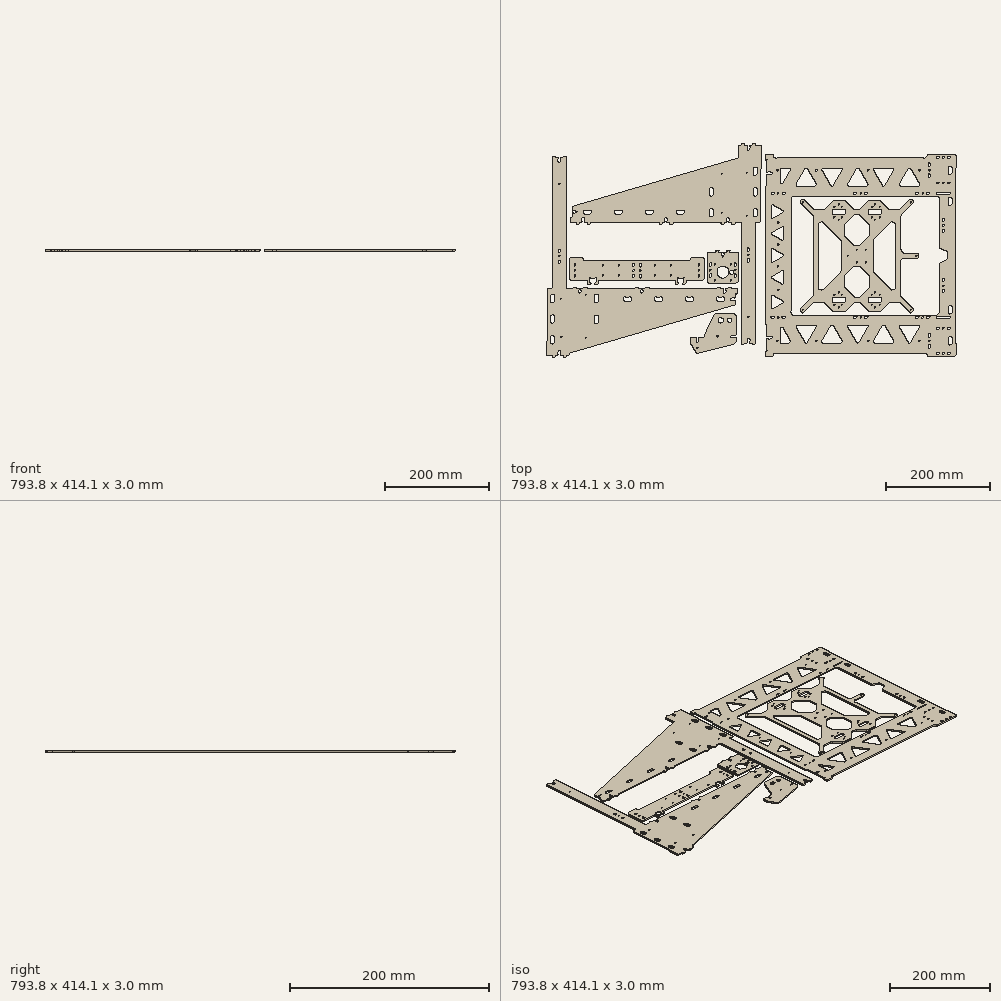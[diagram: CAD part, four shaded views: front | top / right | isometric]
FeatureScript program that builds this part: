
annotation { "Feature Type Name" : "Feature", "Feature Type Description" : "" }
export const myFeature = defineFeature(function(context is Context, id is Id, definition is map)
    precondition{}
    {
        {
            var Q0;
            Q0=qCreatedBy(makeId("Top.planeOp"),FACE);
            var sketch = newSketch(context, id + "F0", { "sketchPlane" : qUnion([Q0])});
            skFitSpline(sketch, "E0", {"points": [v(-205.76, 133.1) * mm, v(-205.54, 133.1) * mm, v(-205.33, 133.16) * mm, v(-205.16, 133.3) * mm]});
            skFitSpline(sketch, "E1", {"points": [v(-211.3, 171.1) * mm, v(-211.08, 171.1) * mm, v(-210.87, 171.16) * mm, v(-210.7, 171.3) * mm]});
            skFitSpline(sketch, "E2", {"points": [v(-203.99, 176.1) * mm, v(-204.2, 176.1) * mm, v(-204.42, 176.02) * mm, v(-204.59, 175.9) * mm]});
            skLineSegment(sketch, "E3", {"start": v(-205.16, 133.3) * mm, "end": v(-198.79, 138.1) * mm});
            skLineSegment(sketch, "E4", {"start": v(-210.7, 171.3) * mm, "end": v(-204.59, 175.9) * mm});
            skLineSegment(sketch, "E5", {"start": v(-213.3, 171.1) * mm, "end": v(-211.3, 171.1) * mm});
            skFitSpline(sketch, "E6", {"points": [v(-141.15, -195.58) * mm, v(-140.94, -195.58) * mm, v(-140.73, -195.5) * mm, v(-140.55, -195.38) * mm]});
            skFitSpline(sketch, "E7", {"points": [v(-146.69, -157.58) * mm, v(-146.47, -157.58) * mm, v(-146.26, -157.5) * mm, v(-146.09, -157.38) * mm]});
            skFitSpline(sketch, "E8", {"points": [v(-139.38, -152.58) * mm, v(-139.6, -152.58) * mm, v(-139.8, -152.65) * mm, v(-139.98, -152.78) * mm]});
            skLineSegment(sketch, "E9", {"start": v(-207.76, 133.1) * mm, "end": v(-205.91, 133.1) * mm});
            skLineSegment(sketch, "E10", {"start": v(-205.91, 133.1) * mm, "end": v(-205.77, 133.1) * mm});
            skLineSegment(sketch, "E11", {"start": v(-205.77, 133.1) * mm, "end": v(-205.76, 133.1) * mm});
            skLineSegment(sketch, "E12", {"start": v(-140.55, -195.38) * mm, "end": v(-134.18, -190.58) * mm});
            skLineSegment(sketch, "E13", {"start": v(-146.09, -157.38) * mm, "end": v(-139.98, -152.78) * mm});
            skLineSegment(sketch, "E14", {"start": v(-148.69, -157.58) * mm, "end": v(-146.68, -157.58) * mm});
            skFitSpline(sketch, "E15", {"points": [v(-352, -198.94) * mm, v(-352.22, -199) * mm, v(-352.37, -199.2) * mm, v(-352.37, -199.42) * mm]});
            skLineSegment(sketch, "E16", {"start": v(-143.15, -195.58) * mm, "end": v(-141.3, -195.58) * mm});
            skLineSegment(sketch, "E17", {"start": v(-141.3, -195.58) * mm, "end": v(-141.16, -195.58) * mm});
            skLineSegment(sketch, "E18", {"start": v(-141.16, -195.58) * mm, "end": v(-141.15, -195.58) * mm});
            skLineSegment(sketch, "E19", {"start": v(-396.82, -199.05) * mm, "end": v(-396.82, -204.05) * mm});
            skFitSpline(sketch, "E20", {"points": [v(396.82, 180.1) * mm, v(396.82, 182.86) * mm, v(394.58, 185.1) * mm, v(391.82, 185.1) * mm]});
            skFitSpline(sketch, "E21", {"points": [v(332.72, 179.1) * mm, v(336.37, 179.1) * mm, v(339.56, 181.57) * mm, v(340.47, 185.1) * mm]});
            skLineSegment(sketch, "E22", {"start": v(-352.37, -199.42) * mm, "end": v(-352.37, -204.05) * mm});
            skFitSpline(sketch, "E23", {"points": [v(41.82, 185.1) * mm, v(42.73, 181.57) * mm, v(45.92, 179.1) * mm, v(49.56, 179.1) * mm]});
            skLineSegment(sketch, "E24", {"start": v(394.82, 158.1) * mm, "end": v(396.82, 160.1) * mm});
            skLineSegment(sketch, "E25", {"start": v(396.82, 160.1) * mm, "end": v(396.82, 180.1) * mm});
            skFitSpline(sketch, "E26", {"points": [v(29.05, 175.1) * mm, v(29.23, 175.1) * mm, v(29.4, 175.2) * mm, v(29.48, 175.35) * mm]});
            skFitSpline(sketch, "E27", {"points": [v(30.17, 174.66) * mm, v(30.35, 174.77) * mm, v(30.45, 174.98) * mm, v(30.4, 175.18) * mm]});
            skFitSpline(sketch, "E28", {"points": [v(30.4, 175.18) * mm, v(30.37, 175.4) * mm, v(30.21, 175.55) * mm, v(30, 175.6) * mm]});
            skFitSpline(sketch, "E29", {"points": [v(30, 175.6) * mm, v(29.8, 175.63) * mm, v(29.59, 175.53) * mm, v(29.48, 175.35) * mm]});
            skFitSpline(sketch, "E30", {"points": [v(30.17, 174.66) * mm, v(30.01, 174.58) * mm, v(29.92, 174.41) * mm, v(29.92, 174.23) * mm]});
            skLineSegment(sketch, "E31", {"start": v(391.82, 185.1) * mm, "end": v(340.47, 185.1) * mm});
            skFitSpline(sketch, "E32", {"points": [v(29.92, 124.31) * mm, v(29.92, 124.14) * mm, v(30.01, 123.97) * mm, v(30.17, 123.88) * mm]});
            skFitSpline(sketch, "E33", {"points": [v(29.48, 123.2) * mm, v(29.59, 123.02) * mm, v(29.8, 122.92) * mm, v(30, 122.96) * mm]});
            skFitSpline(sketch, "E34", {"points": [v(30, 122.96) * mm, v(30.21, 123) * mm, v(30.37, 123.15) * mm, v(30.4, 123.36) * mm]});
            skFitSpline(sketch, "E35", {"points": [v(30.4, 123.36) * mm, v(30.45, 123.57) * mm, v(30.35, 123.78) * mm, v(30.17, 123.88) * mm]});
            skFitSpline(sketch, "E36", {"points": [v(29.48, 123.2) * mm, v(29.4, 123.35) * mm, v(29.23, 123.45) * mm, v(29.05, 123.45) * mm]});
            skLineSegment(sketch, "E37", {"start": v(332.72, 179.1) * mm, "end": v(49.56, 179.1) * mm});
            skFitSpline(sketch, "E38", {"points": [v(29.05, -143.25) * mm, v(29.23, -143.25) * mm, v(29.4, -143.16) * mm, v(29.48, -143) * mm]});
            skFitSpline(sketch, "E39", {"points": [v(30.17, -143.69) * mm, v(30.35, -143.58) * mm, v(30.45, -143.37) * mm, v(30.4, -143.17) * mm]});
            skFitSpline(sketch, "E40", {"points": [v(30.4, -143.17) * mm, v(30.37, -142.96) * mm, v(30.21, -142.8) * mm, v(30, -142.76) * mm]});
            skFitSpline(sketch, "E41", {"points": [v(30, -142.76) * mm, v(29.8, -142.72) * mm, v(29.59, -142.82) * mm, v(29.48, -143) * mm]});
            skFitSpline(sketch, "E42", {"points": [v(30.17, -143.69) * mm, v(30.01, -143.77) * mm, v(29.92, -143.94) * mm, v(29.92, -144.12) * mm]});
            skLineSegment(sketch, "E43", {"start": v(41.82, 185.1) * mm, "end": v(26.82, 185.1) * mm});
            skLineSegment(sketch, "E44", {"start": v(26.82, 185.1) * mm, "end": v(26.82, 175.1) * mm});
            skLineSegment(sketch, "E45", {"start": v(26.82, 175.1) * mm, "end": v(29.05, 175.1) * mm});
            skFitSpline(sketch, "E46", {"points": [v(29.92, -194.04) * mm, v(29.92, -194.21) * mm, v(30.01, -194.38) * mm, v(30.17, -194.47) * mm]});
            skFitSpline(sketch, "E47", {"points": [v(29.48, -195.15) * mm, v(29.59, -195.33) * mm, v(29.8, -195.43) * mm, v(30, -195.4) * mm]});
            skFitSpline(sketch, "E48", {"points": [v(30, -195.4) * mm, v(30.21, -195.36) * mm, v(30.37, -195.2) * mm, v(30.4, -194.99) * mm]});
            skFitSpline(sketch, "E49", {"points": [v(30.4, -194.99) * mm, v(30.45, -194.78) * mm, v(30.35, -194.57) * mm, v(30.17, -194.47) * mm]});
            skFitSpline(sketch, "E50", {"points": [v(29.48, -195.15) * mm, v(29.4, -195) * mm, v(29.23, -194.9) * mm, v(29.05, -194.9) * mm]});
            skLineSegment(sketch, "E51", {"start": v(29.92, 174.23) * mm, "end": v(29.92, 150.87) * mm});
            skLineSegment(sketch, "E52", {"start": v(29.92, 150.87) * mm, "end": v(32.92, 150.87) * mm});
            skLineSegment(sketch, "E53", {"start": v(32.92, 150.87) * mm, "end": v(32.92, 152.15) * mm});
            skLineSegment(sketch, "E54", {"start": v(32.92, 152.15) * mm, "end": v(36.92, 152.15) * mm});
            skLineSegment(sketch, "E55", {"start": v(36.92, 152.15) * mm, "end": v(36.92, 150.87) * mm});
            skLineSegment(sketch, "E56", {"start": v(36.92, 150.87) * mm, "end": v(39.92, 150.87) * mm});
            skLineSegment(sketch, "E57", {"start": v(39.92, 150.87) * mm, "end": v(39.92, 147.67) * mm});
            skLineSegment(sketch, "E58", {"start": v(39.92, 147.67) * mm, "end": v(36.92, 147.67) * mm});
            skLineSegment(sketch, "E59", {"start": v(36.92, 147.67) * mm, "end": v(36.92, 146.4) * mm});
            skLineSegment(sketch, "E60", {"start": v(36.92, 146.4) * mm, "end": v(32.92, 146.4) * mm});
            skLineSegment(sketch, "E61", {"start": v(32.92, 146.4) * mm, "end": v(32.92, 147.67) * mm});
            skLineSegment(sketch, "E62", {"start": v(32.92, 147.67) * mm, "end": v(29.92, 147.67) * mm});
            skLineSegment(sketch, "E63", {"start": v(29.92, 147.67) * mm, "end": v(29.92, 124.31) * mm});
            skFitSpline(sketch, "E64", {"points": [v(49.56, -198.9) * mm, v(45.92, -198.9) * mm, v(42.73, -201.37) * mm, v(41.82, -204.9) * mm]});
            skLineSegment(sketch, "E65", {"start": v(29.05, 123.45) * mm, "end": v(26.82, 123.45) * mm});
            skLineSegment(sketch, "E66", {"start": v(26.82, 123.45) * mm, "end": v(26.82, -143.25) * mm});
            skLineSegment(sketch, "E67", {"start": v(26.82, -143.25) * mm, "end": v(29.05, -143.25) * mm});
            skFitSpline(sketch, "E68", {"points": [v(340.47, -204.9) * mm, v(339.56, -201.37) * mm, v(336.37, -198.9) * mm, v(332.72, -198.9) * mm]});
            skLineSegment(sketch, "E69", {"start": v(29.92, -144.12) * mm, "end": v(29.92, -167.48) * mm});
            skLineSegment(sketch, "E70", {"start": v(29.92, -167.48) * mm, "end": v(32.92, -167.48) * mm});
            skLineSegment(sketch, "E71", {"start": v(32.92, -167.48) * mm, "end": v(32.92, -166.2) * mm});
            skLineSegment(sketch, "E72", {"start": v(32.92, -166.2) * mm, "end": v(36.92, -166.2) * mm});
            skLineSegment(sketch, "E73", {"start": v(36.92, -166.2) * mm, "end": v(36.92, -167.48) * mm});
            skLineSegment(sketch, "E74", {"start": v(36.92, -167.48) * mm, "end": v(39.92, -167.48) * mm});
            skLineSegment(sketch, "E75", {"start": v(39.92, -167.48) * mm, "end": v(39.92, -170.68) * mm});
            skLineSegment(sketch, "E76", {"start": v(39.92, -170.68) * mm, "end": v(36.92, -170.68) * mm});
            skLineSegment(sketch, "E77", {"start": v(36.92, -170.68) * mm, "end": v(36.92, -171.95) * mm});
            skLineSegment(sketch, "E78", {"start": v(36.92, -171.95) * mm, "end": v(32.92, -171.95) * mm});
            skLineSegment(sketch, "E79", {"start": v(32.92, -171.95) * mm, "end": v(32.92, -170.68) * mm});
            skLineSegment(sketch, "E80", {"start": v(32.92, -170.68) * mm, "end": v(29.92, -170.68) * mm});
            skLineSegment(sketch, "E81", {"start": v(29.92, -170.68) * mm, "end": v(29.92, -194.04) * mm});
            skFitSpline(sketch, "E82", {"points": [v(391.82, -204.9) * mm, v(394.58, -204.9) * mm, v(396.82, -202.66) * mm, v(396.82, -199.9) * mm]});
            skLineSegment(sketch, "E83", {"start": v(29.05, -194.9) * mm, "end": v(26.82, -194.9) * mm});
            skLineSegment(sketch, "E84", {"start": v(26.82, -194.9) * mm, "end": v(26.82, -204.9) * mm});
            skLineSegment(sketch, "E85", {"start": v(26.82, -204.9) * mm, "end": v(41.82, -204.9) * mm});
            skLineSegment(sketch, "E86", {"start": v(49.56, -198.9) * mm, "end": v(332.72, -198.9) * mm});
            skFitSpline(sketch, "E87", {"points": [v(378.82, -3.18) * mm, v(378.82, -2.4) * mm, v(378.37, -1.7) * mm, v(377.66, -1.36) * mm]});
            skLineSegment(sketch, "E88", {"start": v(340.47, -204.9) * mm, "end": v(391.82, -204.9) * mm});
            skFitSpline(sketch, "E89", {"points": [v(363.7, 6.43) * mm, v(363.7, 5.65) * mm, v(364.14, 4.94) * mm, v(364.85, 4.61) * mm]});
            skLineSegment(sketch, "E90", {"start": v(396.82, -199.9) * mm, "end": v(396.82, -179.9) * mm});
            skLineSegment(sketch, "E91", {"start": v(396.82, -179.9) * mm, "end": v(394.82, -177.9) * mm});
            skLineSegment(sketch, "E92", {"start": v(394.82, -177.9) * mm, "end": v(394.82, 158.1) * mm});
            skFitSpline(sketch, "E93", {"points": [v(363.7, 97.1) * mm, v(363.7, 101.5) * mm, v(360.12, 105.09) * mm, v(355.71, 105.1) * mm]});
            skLineSegment(sketch, "E94", {"start": v(378.82, -16.62) * mm, "end": v(378.82, -3.18) * mm});
            skFitSpline(sketch, "E95", {"points": [v(84.82, 105.1) * mm, v(82.7, 105.1) * mm, v(80.66, 104.25) * mm, v(79.16, 102.75) * mm]});
            skFitSpline(sketch, "E96", {"points": [v(79.16, 102.75) * mm, v(77.66, 101.25) * mm, v(76.82, 99.22) * mm, v(76.82, 97.1) * mm]});
            skLineSegment(sketch, "E97", {"start": v(377.66, -1.36) * mm, "end": v(364.85, 4.61) * mm});
            skFitSpline(sketch, "E98", {"points": [v(76.82, -116.9) * mm, v(76.82, -121.32) * mm, v(80.4, -124.9) * mm, v(84.82, -124.9) * mm]});
            skLineSegment(sketch, "E99", {"start": v(363.7, 6.43) * mm, "end": v(363.7, 97.1) * mm});
            skFitSpline(sketch, "E100", {"points": [v(355.71, -124.9) * mm, v(360.12, -124.9) * mm, v(363.7, -121.31) * mm, v(363.7, -116.9) * mm]});
            skLineSegment(sketch, "E101", {"start": v(355.71, 105.1) * mm, "end": v(84.82, 105.1) * mm});
            skFitSpline(sketch, "E102", {"points": [v(364.86, -24.31) * mm, v(364.15, -24.64) * mm, v(363.7, -25.35) * mm, v(363.7, -26.13) * mm]});
            skLineSegment(sketch, "E103", {"start": v(76.82, 97.1) * mm, "end": v(76.82, -116.9) * mm});
            skFitSpline(sketch, "E104", {"points": [v(377.65, -18.44) * mm, v(378.36, -18.11) * mm, v(378.82, -17.4) * mm, v(378.82, -16.62) * mm]});
            skLineSegment(sketch, "E105", {"start": v(84.82, -124.9) * mm, "end": v(355.71, -124.9) * mm});
            skFitSpline(sketch, "E106", {"points": [v(289.45, -144.33) * mm, v(288.38, -144.33) * mm, v(287.4, -144.9) * mm, v(286.86, -145.83) * mm]});
            skFitSpline(sketch, "E107", {"points": [v(286.86, -145.83) * mm, v(286.32, -146.76) * mm, v(286.32, -147.9) * mm, v(286.86, -148.83) * mm]});
            skLineSegment(sketch, "E108", {"start": v(363.7, -116.9) * mm, "end": v(363.7, -26.13) * mm});
            skFitSpline(sketch, "E109", {"points": [v(303.56, -177.76) * mm, v(304.1, -178.69) * mm, v(305.08, -179.26) * mm, v(306.16, -179.26) * mm]});
            skFitSpline(sketch, "E110", {"points": [v(306.16, -179.26) * mm, v(307.23, -179.26) * mm, v(308.22, -178.69) * mm, v(308.75, -177.76) * mm]});
            skLineSegment(sketch, "E111", {"start": v(364.86, -24.31) * mm, "end": v(377.65, -18.44) * mm});
            skFitSpline(sketch, "E112", {"points": [v(325.45, -148.83) * mm, v(326, -147.9) * mm, v(326, -146.76) * mm, v(325.45, -145.83) * mm]});
            skFitSpline(sketch, "E113", {"points": [v(325.45, -145.83) * mm, v(324.92, -144.9) * mm, v(323.93, -144.33) * mm, v(322.86, -144.33) * mm]});
            skLineSegment(sketch, "E114", {"start": v(322.86, -144.33) * mm, "end": v(289.45, -144.33) * mm});
            skFitSpline(sketch, "E115", {"points": [v(236.86, -174.76) * mm, v(236.32, -175.69) * mm, v(236.32, -176.83) * mm, v(236.86, -177.76) * mm]});
            skFitSpline(sketch, "E116", {"points": [v(236.86, -177.76) * mm, v(237.4, -178.69) * mm, v(238.38, -179.26) * mm, v(239.46, -179.26) * mm]});
            skLineSegment(sketch, "E117", {"start": v(286.86, -148.83) * mm, "end": v(303.56, -177.76) * mm});
            skFitSpline(sketch, "E118", {"points": [v(258.75, -145.83) * mm, v(258.22, -144.9) * mm, v(257.23, -144.33) * mm, v(256.16, -144.33) * mm]});
            skFitSpline(sketch, "E119", {"points": [v(256.16, -144.33) * mm, v(255.08, -144.33) * mm, v(254.1, -144.9) * mm, v(253.56, -145.83) * mm]});
            skLineSegment(sketch, "E120", {"start": v(308.75, -177.76) * mm, "end": v(325.45, -148.83) * mm});
            skFitSpline(sketch, "E121", {"points": [v(272.86, -179.26) * mm, v(273.93, -179.26) * mm, v(274.92, -178.69) * mm, v(275.46, -177.76) * mm]});
            skFitSpline(sketch, "E122", {"points": [v(275.46, -177.76) * mm, v(276, -176.83) * mm, v(276, -175.69) * mm, v(275.46, -174.76) * mm]});
            skLineSegment(sketch, "E123", {"start": v(272.86, -179.26) * mm, "end": v(239.46, -179.26) * mm});
            skFitSpline(sketch, "E124", {"points": [v(189.45, -144.33) * mm, v(188.38, -144.33) * mm, v(187.4, -144.9) * mm, v(186.86, -145.83) * mm]});
            skFitSpline(sketch, "E125", {"points": [v(186.86, -145.83) * mm, v(186.32, -146.76) * mm, v(186.32, -147.9) * mm, v(186.86, -148.83) * mm]});
            skLineSegment(sketch, "E126", {"start": v(236.86, -174.76) * mm, "end": v(253.56, -145.83) * mm});
            skFitSpline(sketch, "E127", {"points": [v(203.56, -177.76) * mm, v(204.1, -178.69) * mm, v(205.08, -179.26) * mm, v(206.16, -179.26) * mm]});
            skFitSpline(sketch, "E128", {"points": [v(206.16, -179.26) * mm, v(207.23, -179.26) * mm, v(208.22, -178.69) * mm, v(208.75, -177.76) * mm]});
            skLineSegment(sketch, "E129", {"start": v(258.75, -145.83) * mm, "end": v(275.46, -174.76) * mm});
            skFitSpline(sketch, "E130", {"points": [v(225.45, -148.83) * mm, v(226, -147.9) * mm, v(226, -146.76) * mm, v(225.45, -145.83) * mm]});
            skFitSpline(sketch, "E131", {"points": [v(225.45, -145.83) * mm, v(224.92, -144.9) * mm, v(223.93, -144.33) * mm, v(222.86, -144.33) * mm]});
            skLineSegment(sketch, "E132", {"start": v(222.86, -144.33) * mm, "end": v(189.45, -144.33) * mm});
            skFitSpline(sketch, "E133", {"points": [v(136.86, -174.76) * mm, v(136.32, -175.69) * mm, v(136.32, -176.83) * mm, v(136.86, -177.76) * mm]});
            skFitSpline(sketch, "E134", {"points": [v(136.86, -177.76) * mm, v(137.4, -178.69) * mm, v(138.38, -179.26) * mm, v(139.46, -179.26) * mm]});
            skLineSegment(sketch, "E135", {"start": v(186.86, -148.83) * mm, "end": v(203.56, -177.76) * mm});
            skFitSpline(sketch, "E136", {"points": [v(158.75, -145.83) * mm, v(158.22, -144.9) * mm, v(157.23, -144.33) * mm, v(156.16, -144.33) * mm]});
            skFitSpline(sketch, "E137", {"points": [v(156.16, -144.33) * mm, v(155.08, -144.33) * mm, v(154.1, -144.9) * mm, v(153.56, -145.83) * mm]});
            skLineSegment(sketch, "E138", {"start": v(208.75, -177.76) * mm, "end": v(225.45, -148.83) * mm});
            skFitSpline(sketch, "E139", {"points": [v(172.86, -179.26) * mm, v(173.93, -179.26) * mm, v(174.92, -178.69) * mm, v(175.46, -177.76) * mm]});
            skFitSpline(sketch, "E140", {"points": [v(175.46, -177.76) * mm, v(176, -176.83) * mm, v(176, -175.69) * mm, v(175.46, -174.76) * mm]});
            skLineSegment(sketch, "E141", {"start": v(172.86, -179.26) * mm, "end": v(139.46, -179.26) * mm});
            skFitSpline(sketch, "E142", {"points": [v(89.45, -144.33) * mm, v(88.38, -144.33) * mm, v(87.4, -144.9) * mm, v(86.86, -145.83) * mm]});
            skFitSpline(sketch, "E143", {"points": [v(86.86, -145.83) * mm, v(86.32, -146.76) * mm, v(86.32, -147.9) * mm, v(86.86, -148.83) * mm]});
            skLineSegment(sketch, "E144", {"start": v(136.86, -174.76) * mm, "end": v(153.56, -145.83) * mm});
            skFitSpline(sketch, "E145", {"points": [v(103.56, -177.76) * mm, v(104.1, -178.69) * mm, v(105.08, -179.26) * mm, v(106.16, -179.26) * mm]});
            skFitSpline(sketch, "E146", {"points": [v(106.16, -179.26) * mm, v(107.23, -179.26) * mm, v(108.22, -178.69) * mm, v(108.75, -177.76) * mm]});
            skLineSegment(sketch, "E147", {"start": v(158.75, -145.83) * mm, "end": v(175.46, -174.76) * mm});
            skFitSpline(sketch, "E148", {"points": [v(125.45, -148.83) * mm, v(126, -147.9) * mm, v(126, -146.76) * mm, v(125.45, -145.83) * mm]});
            skFitSpline(sketch, "E149", {"points": [v(125.45, -145.83) * mm, v(124.92, -144.9) * mm, v(123.93, -144.33) * mm, v(122.86, -144.33) * mm]});
            skLineSegment(sketch, "E150", {"start": v(122.86, -144.33) * mm, "end": v(89.45, -144.33) * mm});
            skFitSpline(sketch, "E151", {"points": [v(286.86, 129.03) * mm, v(286.32, 128.1) * mm, v(286.32, 126.95) * mm, v(286.86, 126.03) * mm]});
            skFitSpline(sketch, "E152", {"points": [v(286.86, 126.03) * mm, v(287.4, 125.1) * mm, v(288.38, 124.53) * mm, v(289.45, 124.53) * mm]});
            skLineSegment(sketch, "E153", {"start": v(86.86, -148.83) * mm, "end": v(103.56, -177.76) * mm});
            skFitSpline(sketch, "E154", {"points": [v(308.75, 157.95) * mm, v(308.22, 158.88) * mm, v(307.23, 159.45) * mm, v(306.16, 159.45) * mm]});
            skFitSpline(sketch, "E155", {"points": [v(306.16, 159.45) * mm, v(305.08, 159.45) * mm, v(304.1, 158.88) * mm, v(303.56, 157.95) * mm]});
            skLineSegment(sketch, "E156", {"start": v(108.75, -177.76) * mm, "end": v(125.45, -148.83) * mm});
            skFitSpline(sketch, "E157", {"points": [v(322.86, 124.53) * mm, v(323.93, 124.53) * mm, v(324.92, 125.1) * mm, v(325.45, 126.03) * mm]});
            skFitSpline(sketch, "E158", {"points": [v(325.45, 126.03) * mm, v(326, 126.95) * mm, v(326, 128.1) * mm, v(325.45, 129.03) * mm]});
            skLineSegment(sketch, "E159", {"start": v(322.86, 124.53) * mm, "end": v(289.45, 124.53) * mm});
            skFitSpline(sketch, "E160", {"points": [v(239.46, 159.45) * mm, v(238.38, 159.45) * mm, v(237.4, 158.88) * mm, v(236.86, 157.95) * mm]});
            skFitSpline(sketch, "E161", {"points": [v(236.86, 157.95) * mm, v(236.32, 157.02) * mm, v(236.32, 155.88) * mm, v(236.86, 154.95) * mm]});
            skLineSegment(sketch, "E162", {"start": v(286.86, 129.03) * mm, "end": v(303.56, 157.95) * mm});
            skFitSpline(sketch, "E163", {"points": [v(253.56, 126.03) * mm, v(254.1, 125.1) * mm, v(255.08, 124.53) * mm, v(256.16, 124.53) * mm]});
            skFitSpline(sketch, "E164", {"points": [v(256.16, 124.53) * mm, v(257.23, 124.53) * mm, v(258.22, 125.1) * mm, v(258.75, 126.03) * mm]});
            skLineSegment(sketch, "E165", {"start": v(308.75, 157.95) * mm, "end": v(325.45, 129.03) * mm});
            skFitSpline(sketch, "E166", {"points": [v(275.46, 154.95) * mm, v(276, 155.88) * mm, v(276, 157.02) * mm, v(275.46, 157.95) * mm]});
            skFitSpline(sketch, "E167", {"points": [v(275.46, 157.95) * mm, v(274.92, 158.88) * mm, v(273.93, 159.45) * mm, v(272.86, 159.45) * mm]});
            skLineSegment(sketch, "E168", {"start": v(272.86, 159.45) * mm, "end": v(239.46, 159.45) * mm});
            skFitSpline(sketch, "E169", {"points": [v(186.86, 129.03) * mm, v(186.32, 128.1) * mm, v(186.32, 126.95) * mm, v(186.86, 126.03) * mm]});
            skFitSpline(sketch, "E170", {"points": [v(186.86, 126.03) * mm, v(187.4, 125.1) * mm, v(188.38, 124.53) * mm, v(189.45, 124.53) * mm]});
            skLineSegment(sketch, "E171", {"start": v(236.86, 154.95) * mm, "end": v(253.56, 126.03) * mm});
            skFitSpline(sketch, "E172", {"points": [v(208.75, 157.95) * mm, v(208.22, 158.88) * mm, v(207.23, 159.45) * mm, v(206.16, 159.45) * mm]});
            skFitSpline(sketch, "E173", {"points": [v(206.16, 159.45) * mm, v(205.08, 159.45) * mm, v(204.1, 158.88) * mm, v(203.56, 157.95) * mm]});
            skLineSegment(sketch, "E174", {"start": v(258.75, 126.03) * mm, "end": v(275.46, 154.95) * mm});
            skFitSpline(sketch, "E175", {"points": [v(222.86, 124.53) * mm, v(223.93, 124.53) * mm, v(224.92, 125.1) * mm, v(225.45, 126.03) * mm]});
            skFitSpline(sketch, "E176", {"points": [v(225.45, 126.03) * mm, v(226, 126.95) * mm, v(226, 128.1) * mm, v(225.45, 129.03) * mm]});
            skLineSegment(sketch, "E177", {"start": v(222.86, 124.53) * mm, "end": v(189.45, 124.53) * mm});
            skFitSpline(sketch, "E178", {"points": [v(139.46, 159.45) * mm, v(138.38, 159.45) * mm, v(137.4, 158.88) * mm, v(136.86, 157.95) * mm]});
            skFitSpline(sketch, "E179", {"points": [v(136.86, 157.95) * mm, v(136.32, 157.02) * mm, v(136.32, 155.88) * mm, v(136.86, 154.95) * mm]});
            skLineSegment(sketch, "E180", {"start": v(186.86, 129.03) * mm, "end": v(203.56, 157.95) * mm});
            skFitSpline(sketch, "E181", {"points": [v(153.56, 126.03) * mm, v(154.1, 125.1) * mm, v(155.08, 124.53) * mm, v(156.16, 124.53) * mm]});
            skFitSpline(sketch, "E182", {"points": [v(156.16, 124.53) * mm, v(157.23, 124.53) * mm, v(158.22, 125.1) * mm, v(158.75, 126.03) * mm]});
            skLineSegment(sketch, "E183", {"start": v(208.75, 157.95) * mm, "end": v(225.45, 129.03) * mm});
            skFitSpline(sketch, "E184", {"points": [v(175.46, 154.95) * mm, v(176, 155.88) * mm, v(176, 157.02) * mm, v(175.46, 157.95) * mm]});
            skFitSpline(sketch, "E185", {"points": [v(175.46, 157.95) * mm, v(174.92, 158.88) * mm, v(173.93, 159.45) * mm, v(172.86, 159.45) * mm]});
            skLineSegment(sketch, "E186", {"start": v(172.86, 159.45) * mm, "end": v(139.46, 159.45) * mm});
            skFitSpline(sketch, "E187", {"points": [v(86.86, 129.03) * mm, v(86.32, 128.1) * mm, v(86.32, 126.95) * mm, v(86.86, 126.03) * mm]});
            skFitSpline(sketch, "E188", {"points": [v(86.86, 126.03) * mm, v(87.4, 125.1) * mm, v(88.38, 124.53) * mm, v(89.45, 124.53) * mm]});
            skLineSegment(sketch, "E189", {"start": v(136.86, 154.95) * mm, "end": v(153.56, 126.03) * mm});
            skFitSpline(sketch, "E190", {"points": [v(108.75, 157.95) * mm, v(108.22, 158.88) * mm, v(107.23, 159.45) * mm, v(106.16, 159.45) * mm]});
            skFitSpline(sketch, "E191", {"points": [v(106.16, 159.45) * mm, v(105.08, 159.45) * mm, v(104.1, 158.88) * mm, v(103.56, 157.95) * mm]});
            skLineSegment(sketch, "E192", {"start": v(158.75, 126.03) * mm, "end": v(175.46, 154.95) * mm});
            skFitSpline(sketch, "E193", {"points": [v(122.86, 124.53) * mm, v(123.93, 124.53) * mm, v(124.92, 125.1) * mm, v(125.45, 126.03) * mm]});
            skFitSpline(sketch, "E194", {"points": [v(125.45, 126.03) * mm, v(126, 126.95) * mm, v(126, 128.1) * mm, v(125.45, 129.03) * mm]});
            skLineSegment(sketch, "E195", {"start": v(122.86, 124.53) * mm, "end": v(89.45, 124.53) * mm});
            skFitSpline(sketch, "E196", {"points": [v(39.12, -111.23) * mm, v(39.12, -111.95) * mm, v(39.51, -112.62) * mm, v(40.14, -112.98) * mm]});
            skFitSpline(sketch, "E197", {"points": [v(40.14, -112.98) * mm, v(40.76, -113.35) * mm, v(41.54, -113.35) * mm, v(42.16, -112.98) * mm]});
            skLineSegment(sketch, "E198", {"start": v(86.86, 129.03) * mm, "end": v(103.56, 157.95) * mm});
            skFitSpline(sketch, "E199", {"points": [v(61.69, -101.71) * mm, v(62.31, -101.35) * mm, v(62.7, -100.68) * mm, v(62.7, -99.96) * mm]});
            skFitSpline(sketch, "E200", {"points": [v(62.7, -99.96) * mm, v(62.7, -99.23) * mm, v(62.31, -98.57) * mm, v(61.69, -98.2) * mm]});
            skLineSegment(sketch, "E201", {"start": v(108.75, 157.95) * mm, "end": v(125.45, 129.03) * mm});
            skFitSpline(sketch, "E202", {"points": [v(42.16, -86.93) * mm, v(41.54, -86.57) * mm, v(40.76, -86.57) * mm, v(40.14, -86.93) * mm]});
            skFitSpline(sketch, "E203", {"points": [v(40.14, -86.93) * mm, v(39.51, -87.3) * mm, v(39.12, -87.96) * mm, v(39.12, -88.68) * mm]});
            skLineSegment(sketch, "E204", {"start": v(39.12, -88.68) * mm, "end": v(39.12, -111.23) * mm});
            skFitSpline(sketch, "E205", {"points": [v(59.66, -65.44) * mm, v(60.29, -65.8) * mm, v(61.06, -65.8) * mm, v(61.69, -65.44) * mm]});
            skFitSpline(sketch, "E206", {"points": [v(61.69, -65.44) * mm, v(62.31, -65.08) * mm, v(62.7, -64.4) * mm, v(62.7, -63.68) * mm]});
            skLineSegment(sketch, "E207", {"start": v(42.16, -112.98) * mm, "end": v(61.69, -101.71) * mm});
            skFitSpline(sketch, "E208", {"points": [v(40.14, -50.66) * mm, v(39.51, -51.02) * mm, v(39.12, -51.69) * mm, v(39.12, -52.41) * mm]});
            skFitSpline(sketch, "E209", {"points": [v(39.12, -52.41) * mm, v(39.12, -53.13) * mm, v(39.51, -53.8) * mm, v(40.14, -54.16) * mm]});
            skLineSegment(sketch, "E210", {"start": v(61.69, -98.2) * mm, "end": v(42.16, -86.93) * mm});
            skFitSpline(sketch, "E211", {"points": [v(62.7, -41.14) * mm, v(62.7, -40.41) * mm, v(62.31, -39.75) * mm, v(61.69, -39.38) * mm]});
            skFitSpline(sketch, "E212", {"points": [v(61.69, -39.38) * mm, v(61.06, -39.02) * mm, v(60.29, -39.02) * mm, v(59.66, -39.38) * mm]});
            skLineSegment(sketch, "E213", {"start": v(62.7, -41.14) * mm, "end": v(62.7, -63.68) * mm});
            skFitSpline(sketch, "E214", {"points": [v(39.12, -21.18) * mm, v(39.12, -21.9) * mm, v(39.51, -22.58) * mm, v(40.14, -22.94) * mm]});
            skFitSpline(sketch, "E215", {"points": [v(40.14, -22.94) * mm, v(40.76, -23.3) * mm, v(41.54, -23.3) * mm, v(42.16, -22.94) * mm]});
            skLineSegment(sketch, "E216", {"start": v(59.66, -65.44) * mm, "end": v(40.14, -54.16) * mm});
            skFitSpline(sketch, "E217", {"points": [v(61.69, -11.66) * mm, v(62.31, -11.3) * mm, v(62.7, -10.63) * mm, v(62.7, -9.91) * mm]});
            skFitSpline(sketch, "E218", {"points": [v(62.7, -9.91) * mm, v(62.7, -9.19) * mm, v(62.31, -8.52) * mm, v(61.69, -8.16) * mm]});
            skLineSegment(sketch, "E219", {"start": v(40.14, -50.66) * mm, "end": v(59.66, -39.38) * mm});
            skFitSpline(sketch, "E220", {"points": [v(42.16, 3.12) * mm, v(41.54, 3.48) * mm, v(40.76, 3.48) * mm, v(40.14, 3.12) * mm]});
            skFitSpline(sketch, "E221", {"points": [v(40.14, 3.12) * mm, v(39.51, 2.75) * mm, v(39.12, 2.09) * mm, v(39.12, 1.36) * mm]});
            skLineSegment(sketch, "E222", {"start": v(39.12, 1.36) * mm, "end": v(39.12, -21.18) * mm});
            skFitSpline(sketch, "E223", {"points": [v(59.66, 19.57) * mm, v(60.29, 19.2) * mm, v(61.06, 19.2) * mm, v(61.69, 19.57) * mm]});
            skFitSpline(sketch, "E224", {"points": [v(61.69, 19.57) * mm, v(62.31, 19.93) * mm, v(62.7, 20.6) * mm, v(62.7, 21.32) * mm]});
            skLineSegment(sketch, "E225", {"start": v(42.16, -22.94) * mm, "end": v(61.69, -11.66) * mm});
            skFitSpline(sketch, "E226", {"points": [v(40.14, 34.35) * mm, v(39.51, 33.99) * mm, v(39.12, 33.32) * mm, v(39.12, 32.6) * mm]});
            skFitSpline(sketch, "E227", {"points": [v(39.12, 32.6) * mm, v(39.12, 31.87) * mm, v(39.51, 31.2) * mm, v(40.14, 30.84) * mm]});
            skLineSegment(sketch, "E228", {"start": v(61.69, -8.16) * mm, "end": v(42.16, 3.12) * mm});
            skFitSpline(sketch, "E229", {"points": [v(62.7, 43.87) * mm, v(62.7, 44.6) * mm, v(62.31, 45.26) * mm, v(61.69, 45.62) * mm]});
            skFitSpline(sketch, "E230", {"points": [v(61.69, 45.62) * mm, v(61.06, 45.99) * mm, v(60.29, 45.99) * mm, v(59.66, 45.62) * mm]});
            skLineSegment(sketch, "E231", {"start": v(62.7, 43.87) * mm, "end": v(62.7, 21.32) * mm});
            skFitSpline(sketch, "E232", {"points": [v(39.12, 63.82) * mm, v(39.12, 63.1) * mm, v(39.51, 62.43) * mm, v(40.14, 62.07) * mm]});
            skFitSpline(sketch, "E233", {"points": [v(40.14, 62.07) * mm, v(40.76, 61.7) * mm, v(41.54, 61.7) * mm, v(42.16, 62.07) * mm]});
            skLineSegment(sketch, "E234", {"start": v(59.66, 19.57) * mm, "end": v(40.14, 30.84) * mm});
            skFitSpline(sketch, "E235", {"points": [v(61.69, 73.34) * mm, v(62.31, 73.7) * mm, v(62.7, 74.37) * mm, v(62.7, 75.1) * mm]});
            skFitSpline(sketch, "E236", {"points": [v(62.7, 75.1) * mm, v(62.7, 75.82) * mm, v(62.31, 76.49) * mm, v(61.69, 76.85) * mm]});
            skLineSegment(sketch, "E237", {"start": v(40.14, 34.35) * mm, "end": v(59.66, 45.62) * mm});
            skFitSpline(sketch, "E238", {"points": [v(42.16, 88.12) * mm, v(41.54, 88.49) * mm, v(40.76, 88.49) * mm, v(40.14, 88.12) * mm]});
            skFitSpline(sketch, "E239", {"points": [v(40.14, 88.12) * mm, v(39.51, 87.76) * mm, v(39.12, 87.1) * mm, v(39.12, 86.37) * mm]});
            skLineSegment(sketch, "E240", {"start": v(39.12, 86.37) * mm, "end": v(39.12, 63.82) * mm});
            skFitSpline(sketch, "E241", {"points": [v(388.82, -170.9) * mm, v(388.82, -169.47) * mm, v(388.05, -168.15) * mm, v(386.82, -167.44) * mm]});
            skFitSpline(sketch, "E242", {"points": [v(386.82, -167.44) * mm, v(385.58, -166.72) * mm, v(384.05, -166.72) * mm, v(382.82, -167.44) * mm]});
            skFitSpline(sketch, "E243", {"points": [v(382.82, -167.44) * mm, v(381.58, -168.15) * mm, v(380.82, -169.47) * mm, v(380.82, -170.9) * mm]});
            skLineSegment(sketch, "E244", {"start": v(42.16, 62.07) * mm, "end": v(61.69, 73.34) * mm});
            skFitSpline(sketch, "E245", {"points": [v(380.82, -178.9) * mm, v(380.82, -180.33) * mm, v(381.58, -181.65) * mm, v(382.82, -182.37) * mm]});
            skFitSpline(sketch, "E246", {"points": [v(382.82, -182.37) * mm, v(384.05, -183.08) * mm, v(385.58, -183.08) * mm, v(386.82, -182.37) * mm]});
            skFitSpline(sketch, "E247", {"points": [v(386.82, -182.37) * mm, v(388.05, -181.65) * mm, v(388.82, -180.33) * mm, v(388.82, -178.9) * mm]});
            skLineSegment(sketch, "E248", {"start": v(61.69, 76.85) * mm, "end": v(42.16, 88.12) * mm});
            skFitSpline(sketch, "E249", {"points": [v(388.82, -110.9) * mm, v(388.82, -109.47) * mm, v(388.05, -108.15) * mm, v(386.82, -107.44) * mm]});
            skFitSpline(sketch, "E250", {"points": [v(386.82, -107.44) * mm, v(385.58, -106.72) * mm, v(384.05, -106.72) * mm, v(382.82, -107.44) * mm]});
            skFitSpline(sketch, "E251", {"points": [v(382.82, -107.44) * mm, v(381.58, -108.15) * mm, v(380.82, -109.47) * mm, v(380.82, -110.9) * mm]});
            skLineSegment(sketch, "E252", {"start": v(388.82, -178.9) * mm, "end": v(388.82, -170.9) * mm});
            skFitSpline(sketch, "E253", {"points": [v(380.82, -118.9) * mm, v(380.82, -120.33) * mm, v(381.58, -121.65) * mm, v(382.82, -122.37) * mm]});
            skFitSpline(sketch, "E254", {"points": [v(382.82, -122.37) * mm, v(384.05, -123.08) * mm, v(385.58, -123.08) * mm, v(386.82, -122.37) * mm]});
            skFitSpline(sketch, "E255", {"points": [v(386.82, -122.37) * mm, v(388.05, -121.65) * mm, v(388.82, -120.33) * mm, v(388.82, -118.9) * mm]});
            skLineSegment(sketch, "E256", {"start": v(380.82, -170.9) * mm, "end": v(380.82, -178.9) * mm});
            skFitSpline(sketch, "E257", {"points": [v(388.82, 99.1) * mm, v(388.82, 100.53) * mm, v(388.05, 101.85) * mm, v(386.82, 102.56) * mm]});
            skFitSpline(sketch, "E258", {"points": [v(386.82, 102.56) * mm, v(385.58, 103.28) * mm, v(384.05, 103.28) * mm, v(382.82, 102.56) * mm]});
            skFitSpline(sketch, "E259", {"points": [v(382.82, 102.56) * mm, v(381.58, 101.85) * mm, v(380.82, 100.53) * mm, v(380.82, 99.1) * mm]});
            skLineSegment(sketch, "E260", {"start": v(388.82, -118.9) * mm, "end": v(388.82, -110.9) * mm});
            skFitSpline(sketch, "E261", {"points": [v(380.82, 91.1) * mm, v(380.82, 89.67) * mm, v(381.58, 88.35) * mm, v(382.82, 87.63) * mm]});
            skFitSpline(sketch, "E262", {"points": [v(382.82, 87.63) * mm, v(384.05, 86.92) * mm, v(385.58, 86.92) * mm, v(386.82, 87.63) * mm]});
            skFitSpline(sketch, "E263", {"points": [v(386.82, 87.63) * mm, v(388.05, 88.35) * mm, v(388.82, 89.67) * mm, v(388.82, 91.1) * mm]});
            skLineSegment(sketch, "E264", {"start": v(380.82, -110.9) * mm, "end": v(380.82, -118.9) * mm});
            skFitSpline(sketch, "E265", {"points": [v(388.82, 159.1) * mm, v(388.82, 160.53) * mm, v(388.05, 161.85) * mm, v(386.82, 162.56) * mm]});
            skFitSpline(sketch, "E266", {"points": [v(386.82, 162.56) * mm, v(385.58, 163.28) * mm, v(384.05, 163.28) * mm, v(382.82, 162.56) * mm]});
            skFitSpline(sketch, "E267", {"points": [v(382.82, 162.56) * mm, v(381.58, 161.85) * mm, v(380.82, 160.53) * mm, v(380.82, 159.1) * mm]});
            skLineSegment(sketch, "E268", {"start": v(388.82, 91.1) * mm, "end": v(388.82, 99.1) * mm});
            skFitSpline(sketch, "E269", {"points": [v(380.82, 151.1) * mm, v(380.82, 149.67) * mm, v(381.58, 148.35) * mm, v(382.82, 147.63) * mm]});
            skFitSpline(sketch, "E270", {"points": [v(382.82, 147.63) * mm, v(384.05, 146.92) * mm, v(385.58, 146.92) * mm, v(386.82, 147.63) * mm]});
            skFitSpline(sketch, "E271", {"points": [v(386.82, 147.63) * mm, v(388.05, 148.35) * mm, v(388.82, 149.67) * mm, v(388.82, 151.1) * mm]});
            skFitSpline(sketch, "E272", {"points": [v(358.12, -129.3) * mm, v(358.12, -129.11) * mm, v(358.02, -128.95) * mm, v(357.87, -128.86) * mm]});
            skFitSpline(sketch, "E273", {"points": [v(358.55, -128.18) * mm, v(358.45, -128) * mm, v(358.24, -127.9) * mm, v(358.03, -127.93) * mm]});
            skFitSpline(sketch, "E274", {"points": [v(358.03, -127.93) * mm, v(357.82, -127.97) * mm, v(357.66, -128.13) * mm, v(357.62, -128.34) * mm]});
            skFitSpline(sketch, "E275", {"points": [v(357.62, -128.34) * mm, v(357.59, -128.55) * mm, v(357.69, -128.76) * mm, v(357.87, -128.86) * mm]});
            skFitSpline(sketch, "E276", {"points": [v(358.55, -128.18) * mm, v(358.64, -128.33) * mm, v(358.8, -128.43) * mm, v(358.98, -128.43) * mm]});
            skLineSegment(sketch, "E277", {"start": v(380.82, 99.1) * mm, "end": v(380.82, 91.1) * mm});
            skFitSpline(sketch, "E278", {"points": [v(384.65, -128.43) * mm, v(384.83, -128.43) * mm, v(385, -128.33) * mm, v(385.08, -128.18) * mm]});
            skFitSpline(sketch, "E279", {"points": [v(385.77, -128.86) * mm, v(385.95, -128.76) * mm, v(386.05, -128.55) * mm, v(386, -128.34) * mm]});
            skFitSpline(sketch, "E280", {"points": [v(386, -128.34) * mm, v(385.97, -128.13) * mm, v(385.81, -127.97) * mm, v(385.6, -127.93) * mm]});
            skFitSpline(sketch, "E281", {"points": [v(385.6, -127.93) * mm, v(385.4, -127.9) * mm, v(385.19, -128) * mm, v(385.08, -128.18) * mm]});
            skFitSpline(sketch, "E282", {"points": [v(385.77, -128.86) * mm, v(385.61, -128.95) * mm, v(385.52, -129.11) * mm, v(385.52, -129.3) * mm]});
            skLineSegment(sketch, "E283", {"start": v(388.82, 151.1) * mm, "end": v(388.82, 159.1) * mm});
            skFitSpline(sketch, "E284", {"points": [v(385.52, -130.86) * mm, v(385.52, -131.04) * mm, v(385.61, -131.2) * mm, v(385.77, -131.3) * mm]});
            skFitSpline(sketch, "E285", {"points": [v(385.08, -131.98) * mm, v(385.19, -132.16) * mm, v(385.4, -132.26) * mm, v(385.6, -132.22) * mm]});
            skFitSpline(sketch, "E286", {"points": [v(385.6, -132.22) * mm, v(385.81, -132.18) * mm, v(385.97, -132.02) * mm, v(386, -131.81) * mm]});
            skFitSpline(sketch, "E287", {"points": [v(386, -131.81) * mm, v(386.05, -131.6) * mm, v(385.95, -131.4) * mm, v(385.77, -131.3) * mm]});
            skFitSpline(sketch, "E288", {"points": [v(385.08, -131.98) * mm, v(385, -131.82) * mm, v(384.83, -131.73) * mm, v(384.65, -131.73) * mm]});
            skLineSegment(sketch, "E289", {"start": v(380.82, 159.1) * mm, "end": v(380.82, 151.1) * mm});
            skFitSpline(sketch, "E290", {"points": [v(358.98, -131.73) * mm, v(358.8, -131.73) * mm, v(358.64, -131.82) * mm, v(358.55, -131.98) * mm]});
            skFitSpline(sketch, "E291", {"points": [v(357.87, -131.3) * mm, v(357.69, -131.4) * mm, v(357.59, -131.6) * mm, v(357.62, -131.81) * mm]});
            skFitSpline(sketch, "E292", {"points": [v(357.62, -131.81) * mm, v(357.66, -132.02) * mm, v(357.82, -132.18) * mm, v(358.03, -132.22) * mm]});
            skFitSpline(sketch, "E293", {"points": [v(358.03, -132.22) * mm, v(358.24, -132.26) * mm, v(358.45, -132.16) * mm, v(358.55, -131.98) * mm]});
            skFitSpline(sketch, "E294", {"points": [v(357.87, -131.3) * mm, v(358.02, -131.2) * mm, v(358.12, -131.04) * mm, v(358.12, -130.86) * mm]});
            skLineSegment(sketch, "E295", {"start": v(358.98, -128.43) * mm, "end": v(384.65, -128.43) * mm});
            skFitSpline(sketch, "E296", {"points": [v(358.12, 111.06) * mm, v(358.12, 111.24) * mm, v(358.02, 111.4) * mm, v(357.87, 111.49) * mm]});
            skFitSpline(sketch, "E297", {"points": [v(358.55, 112.17) * mm, v(358.45, 112.35) * mm, v(358.24, 112.45) * mm, v(358.03, 112.42) * mm]});
            skFitSpline(sketch, "E298", {"points": [v(358.03, 112.42) * mm, v(357.82, 112.38) * mm, v(357.66, 112.22) * mm, v(357.62, 112) * mm]});
            skFitSpline(sketch, "E299", {"points": [v(357.62, 112) * mm, v(357.59, 111.8) * mm, v(357.69, 111.6) * mm, v(357.87, 111.49) * mm]});
            skFitSpline(sketch, "E300", {"points": [v(358.55, 112.17) * mm, v(358.64, 112.02) * mm, v(358.8, 111.92) * mm, v(358.98, 111.92) * mm]});
            skLineSegment(sketch, "E301", {"start": v(385.52, -129.3) * mm, "end": v(385.52, -130.86) * mm});
            skFitSpline(sketch, "E302", {"points": [v(384.65, 111.92) * mm, v(384.83, 111.92) * mm, v(385, 112.02) * mm, v(385.08, 112.17) * mm]});
            skFitSpline(sketch, "E303", {"points": [v(385.77, 111.49) * mm, v(385.95, 111.6) * mm, v(386.05, 111.8) * mm, v(386, 112) * mm]});
            skFitSpline(sketch, "E304", {"points": [v(386, 112) * mm, v(385.97, 112.22) * mm, v(385.81, 112.38) * mm, v(385.6, 112.42) * mm]});
            skFitSpline(sketch, "E305", {"points": [v(385.6, 112.42) * mm, v(385.4, 112.45) * mm, v(385.19, 112.35) * mm, v(385.08, 112.17) * mm]});
            skFitSpline(sketch, "E306", {"points": [v(385.77, 111.49) * mm, v(385.61, 111.4) * mm, v(385.52, 111.24) * mm, v(385.52, 111.06) * mm]});
            skLineSegment(sketch, "E307", {"start": v(384.65, -131.73) * mm, "end": v(358.98, -131.73) * mm});
            skFitSpline(sketch, "E308", {"points": [v(385.52, 109.49) * mm, v(385.52, 109.31) * mm, v(385.61, 109.15) * mm, v(385.77, 109.06) * mm]});
            skFitSpline(sketch, "E309", {"points": [v(385.08, 108.37) * mm, v(385.19, 108.2) * mm, v(385.4, 108.1) * mm, v(385.6, 108.13) * mm]});
            skFitSpline(sketch, "E310", {"points": [v(385.6, 108.13) * mm, v(385.81, 108.17) * mm, v(385.97, 108.33) * mm, v(386, 108.54) * mm]});
            skFitSpline(sketch, "E311", {"points": [v(386, 108.54) * mm, v(386.05, 108.74) * mm, v(385.95, 108.95) * mm, v(385.77, 109.06) * mm]});
            skFitSpline(sketch, "E312", {"points": [v(385.08, 108.37) * mm, v(385, 108.53) * mm, v(384.83, 108.62) * mm, v(384.65, 108.62) * mm]});
            skLineSegment(sketch, "E313", {"start": v(358.12, -130.86) * mm, "end": v(358.12, -129.3) * mm});
            skFitSpline(sketch, "E314", {"points": [v(358.98, 108.62) * mm, v(358.8, 108.62) * mm, v(358.64, 108.53) * mm, v(358.55, 108.37) * mm]});
            skFitSpline(sketch, "E315", {"points": [v(357.87, 109.06) * mm, v(357.69, 108.95) * mm, v(357.59, 108.74) * mm, v(357.62, 108.54) * mm]});
            skFitSpline(sketch, "E316", {"points": [v(357.62, 108.54) * mm, v(357.66, 108.33) * mm, v(357.82, 108.17) * mm, v(358.03, 108.13) * mm]});
            skFitSpline(sketch, "E317", {"points": [v(358.03, 108.13) * mm, v(358.24, 108.1) * mm, v(358.45, 108.2) * mm, v(358.55, 108.37) * mm]});
            skFitSpline(sketch, "E318", {"points": [v(357.87, 109.06) * mm, v(358.02, 109.15) * mm, v(358.12, 109.31) * mm, v(358.12, 109.49) * mm]});
            skLineSegment(sketch, "E319", {"start": v(358.98, 111.92) * mm, "end": v(384.65, 111.92) * mm});
            skFitSpline(sketch, "E320", {"points": [v(379.32, -198.94) * mm, v(379.32, -198.76) * mm, v(379.22, -198.6) * mm, v(379.07, -198.5) * mm]});
            skFitSpline(sketch, "E321", {"points": [v(379.75, -197.82) * mm, v(379.65, -197.64) * mm, v(379.44, -197.54) * mm, v(379.23, -197.58) * mm]});
            skFitSpline(sketch, "E322", {"points": [v(379.23, -197.58) * mm, v(379.02, -197.62) * mm, v(378.86, -197.78) * mm, v(378.82, -197.99) * mm]});
            skFitSpline(sketch, "E323", {"points": [v(378.82, -197.99) * mm, v(378.79, -198.2) * mm, v(378.89, -198.4) * mm, v(379.07, -198.5) * mm]});
            skFitSpline(sketch, "E324", {"points": [v(379.75, -197.82) * mm, v(379.84, -197.98) * mm, v(380, -198.07) * mm, v(380.18, -198.07) * mm]});
            skLineSegment(sketch, "E325", {"start": v(385.52, 111.06) * mm, "end": v(385.52, 109.49) * mm});
            skFitSpline(sketch, "E326", {"points": [v(384.65, -198.07) * mm, v(384.83, -198.07) * mm, v(385, -197.98) * mm, v(385.08, -197.82) * mm]});
            skFitSpline(sketch, "E327", {"points": [v(385.77, -198.5) * mm, v(385.95, -198.4) * mm, v(386.05, -198.2) * mm, v(386, -197.99) * mm]});
            skFitSpline(sketch, "E328", {"points": [v(386, -197.99) * mm, v(385.97, -197.78) * mm, v(385.81, -197.62) * mm, v(385.6, -197.58) * mm]});
            skFitSpline(sketch, "E329", {"points": [v(385.6, -197.58) * mm, v(385.4, -197.54) * mm, v(385.19, -197.64) * mm, v(385.08, -197.82) * mm]});
            skFitSpline(sketch, "E330", {"points": [v(385.77, -198.5) * mm, v(385.61, -198.6) * mm, v(385.52, -198.76) * mm, v(385.52, -198.94) * mm]});
            skLineSegment(sketch, "E331", {"start": v(384.65, 108.62) * mm, "end": v(358.98, 108.62) * mm});
            skFitSpline(sketch, "E332", {"points": [v(385.52, -200.5) * mm, v(385.52, -200.68) * mm, v(385.61, -200.85) * mm, v(385.77, -200.94) * mm]});
            skFitSpline(sketch, "E333", {"points": [v(385.08, -201.62) * mm, v(385.19, -201.8) * mm, v(385.4, -201.9) * mm, v(385.6, -201.86) * mm]});
            skFitSpline(sketch, "E334", {"points": [v(385.6, -201.86) * mm, v(385.81, -201.83) * mm, v(385.97, -201.67) * mm, v(386, -201.46) * mm]});
            skFitSpline(sketch, "E335", {"points": [v(386, -201.46) * mm, v(386.05, -201.25) * mm, v(385.95, -201.04) * mm, v(385.77, -200.94) * mm]});
            skFitSpline(sketch, "E336", {"points": [v(385.08, -201.62) * mm, v(385, -201.47) * mm, v(384.83, -201.37) * mm, v(384.65, -201.37) * mm]});
            skLineSegment(sketch, "E337", {"start": v(358.12, 109.49) * mm, "end": v(358.12, 111.06) * mm});
            skFitSpline(sketch, "E338", {"points": [v(380.18, -201.37) * mm, v(380, -201.37) * mm, v(379.84, -201.47) * mm, v(379.75, -201.62) * mm]});
            skFitSpline(sketch, "E339", {"points": [v(379.07, -200.94) * mm, v(378.89, -201.04) * mm, v(378.79, -201.25) * mm, v(378.82, -201.46) * mm]});
            skFitSpline(sketch, "E340", {"points": [v(378.82, -201.46) * mm, v(378.86, -201.67) * mm, v(379.02, -201.83) * mm, v(379.23, -201.86) * mm]});
            skFitSpline(sketch, "E341", {"points": [v(379.23, -201.86) * mm, v(379.44, -201.9) * mm, v(379.65, -201.8) * mm, v(379.75, -201.62) * mm]});
            skFitSpline(sketch, "E342", {"points": [v(379.07, -200.94) * mm, v(379.22, -200.85) * mm, v(379.32, -200.68) * mm, v(379.32, -200.5) * mm]});
            skLineSegment(sketch, "E343", {"start": v(380.18, -198.07) * mm, "end": v(384.65, -198.07) * mm});
            skFitSpline(sketch, "E344", {"points": [v(358.12, -198.94) * mm, v(358.12, -198.76) * mm, v(358.02, -198.6) * mm, v(357.87, -198.5) * mm]});
            skFitSpline(sketch, "E345", {"points": [v(358.55, -197.82) * mm, v(358.45, -197.64) * mm, v(358.24, -197.54) * mm, v(358.03, -197.58) * mm]});
            skFitSpline(sketch, "E346", {"points": [v(358.03, -197.58) * mm, v(357.82, -197.62) * mm, v(357.66, -197.78) * mm, v(357.62, -197.99) * mm]});
            skFitSpline(sketch, "E347", {"points": [v(357.62, -197.99) * mm, v(357.59, -198.2) * mm, v(357.69, -198.4) * mm, v(357.87, -198.5) * mm]});
            skFitSpline(sketch, "E348", {"points": [v(358.55, -197.82) * mm, v(358.64, -197.98) * mm, v(358.8, -198.07) * mm, v(358.98, -198.07) * mm]});
            skLineSegment(sketch, "E349", {"start": v(385.52, -198.94) * mm, "end": v(385.52, -200.5) * mm});
            skFitSpline(sketch, "E350", {"points": [v(363.45, -198.07) * mm, v(363.63, -198.07) * mm, v(363.8, -197.98) * mm, v(363.88, -197.82) * mm]});
            skFitSpline(sketch, "E351", {"points": [v(364.57, -198.5) * mm, v(364.75, -198.4) * mm, v(364.85, -198.2) * mm, v(364.8, -197.99) * mm]});
            skFitSpline(sketch, "E352", {"points": [v(364.8, -197.99) * mm, v(364.77, -197.78) * mm, v(364.61, -197.62) * mm, v(364.4, -197.58) * mm]});
            skFitSpline(sketch, "E353", {"points": [v(364.4, -197.58) * mm, v(364.2, -197.54) * mm, v(363.99, -197.64) * mm, v(363.88, -197.82) * mm]});
            skFitSpline(sketch, "E354", {"points": [v(364.57, -198.5) * mm, v(364.41, -198.6) * mm, v(364.32, -198.76) * mm, v(364.32, -198.94) * mm]});
            skLineSegment(sketch, "E355", {"start": v(384.65, -201.37) * mm, "end": v(380.18, -201.37) * mm});
            skFitSpline(sketch, "E356", {"points": [v(364.32, -200.5) * mm, v(364.32, -200.68) * mm, v(364.41, -200.85) * mm, v(364.57, -200.94) * mm]});
            skFitSpline(sketch, "E357", {"points": [v(363.88, -201.62) * mm, v(363.99, -201.8) * mm, v(364.2, -201.9) * mm, v(364.4, -201.86) * mm]});
            skFitSpline(sketch, "E358", {"points": [v(364.4, -201.86) * mm, v(364.61, -201.83) * mm, v(364.77, -201.67) * mm, v(364.8, -201.46) * mm]});
            skFitSpline(sketch, "E359", {"points": [v(364.8, -201.46) * mm, v(364.85, -201.25) * mm, v(364.75, -201.04) * mm, v(364.57, -200.94) * mm]});
            skFitSpline(sketch, "E360", {"points": [v(363.88, -201.62) * mm, v(363.8, -201.47) * mm, v(363.63, -201.37) * mm, v(363.45, -201.37) * mm]});
            skLineSegment(sketch, "E361", {"start": v(379.32, -200.5) * mm, "end": v(379.32, -198.94) * mm});
            skFitSpline(sketch, "E362", {"points": [v(358.98, -201.37) * mm, v(358.8, -201.37) * mm, v(358.64, -201.47) * mm, v(358.55, -201.62) * mm]});
            skFitSpline(sketch, "E363", {"points": [v(357.87, -200.94) * mm, v(357.69, -201.04) * mm, v(357.59, -201.25) * mm, v(357.62, -201.46) * mm]});
            skFitSpline(sketch, "E364", {"points": [v(357.62, -201.46) * mm, v(357.66, -201.67) * mm, v(357.82, -201.83) * mm, v(358.03, -201.86) * mm]});
            skFitSpline(sketch, "E365", {"points": [v(358.03, -201.86) * mm, v(358.24, -201.9) * mm, v(358.45, -201.8) * mm, v(358.55, -201.62) * mm]});
            skFitSpline(sketch, "E366", {"points": [v(357.87, -200.94) * mm, v(358.02, -200.85) * mm, v(358.12, -200.68) * mm, v(358.12, -200.5) * mm]});
            skLineSegment(sketch, "E367", {"start": v(358.98, -198.07) * mm, "end": v(363.45, -198.07) * mm});
            skFitSpline(sketch, "E368", {"points": [v(344.39, -188.9) * mm, v(344.2, -188.9) * mm, v(344.04, -189) * mm, v(343.96, -189.15) * mm]});
            skFitSpline(sketch, "E369", {"points": [v(343.27, -188.47) * mm, v(343.1, -188.57) * mm, v(343, -188.78) * mm, v(343.03, -188.99) * mm]});
            skFitSpline(sketch, "E370", {"points": [v(343.03, -188.99) * mm, v(343.07, -189.2) * mm, v(343.23, -189.36) * mm, v(343.44, -189.4) * mm]});
            skFitSpline(sketch, "E371", {"points": [v(343.44, -189.4) * mm, v(343.64, -189.43) * mm, v(343.85, -189.33) * mm, v(343.96, -189.15) * mm]});
            skFitSpline(sketch, "E372", {"points": [v(343.27, -188.47) * mm, v(343.43, -188.38) * mm, v(343.52, -188.21) * mm, v(343.52, -188.04) * mm]});
            skLineSegment(sketch, "E373", {"start": v(364.32, -198.94) * mm, "end": v(364.32, -200.5) * mm});
            skFitSpline(sketch, "E374", {"points": [v(343.52, -183.57) * mm, v(343.52, -183.39) * mm, v(343.43, -183.22) * mm, v(343.27, -183.14) * mm]});
            skFitSpline(sketch, "E375", {"points": [v(343.96, -182.45) * mm, v(343.85, -182.27) * mm, v(343.64, -182.17) * mm, v(343.44, -182.2) * mm]});
            skFitSpline(sketch, "E376", {"points": [v(343.44, -182.2) * mm, v(343.23, -182.25) * mm, v(343.07, -182.4) * mm, v(343.03, -182.62) * mm]});
            skFitSpline(sketch, "E377", {"points": [v(343.03, -182.62) * mm, v(343, -182.82) * mm, v(343.1, -183.03) * mm, v(343.27, -183.14) * mm]});
            skFitSpline(sketch, "E378", {"points": [v(343.96, -182.45) * mm, v(344.04, -182.6) * mm, v(344.2, -182.7) * mm, v(344.39, -182.7) * mm]});
            skLineSegment(sketch, "E379", {"start": v(363.45, -201.37) * mm, "end": v(358.98, -201.37) * mm});
            skFitSpline(sketch, "E380", {"points": [v(345.96, -182.7) * mm, v(346.13, -182.7) * mm, v(346.3, -182.6) * mm, v(346.39, -182.45) * mm]});
            skFitSpline(sketch, "E381", {"points": [v(347.07, -183.14) * mm, v(347.25, -183.03) * mm, v(347.35, -182.82) * mm, v(347.31, -182.62) * mm]});
            skFitSpline(sketch, "E382", {"points": [v(347.31, -182.62) * mm, v(347.28, -182.4) * mm, v(347.12, -182.25) * mm, v(346.9, -182.2) * mm]});
            skFitSpline(sketch, "E383", {"points": [v(346.9, -182.2) * mm, v(346.7, -182.17) * mm, v(346.5, -182.27) * mm, v(346.39, -182.45) * mm]});
            skFitSpline(sketch, "E384", {"points": [v(347.07, -183.14) * mm, v(346.92, -183.22) * mm, v(346.82, -183.39) * mm, v(346.82, -183.57) * mm]});
            skLineSegment(sketch, "E385", {"start": v(358.12, -200.5) * mm, "end": v(358.12, -198.94) * mm});
            skFitSpline(sketch, "E386", {"points": [v(346.82, -188.04) * mm, v(346.82, -188.21) * mm, v(346.92, -188.38) * mm, v(347.07, -188.47) * mm]});
            skFitSpline(sketch, "E387", {"points": [v(346.39, -189.15) * mm, v(346.5, -189.33) * mm, v(346.7, -189.43) * mm, v(346.9, -189.4) * mm]});
            skFitSpline(sketch, "E388", {"points": [v(346.9, -189.4) * mm, v(347.12, -189.36) * mm, v(347.28, -189.2) * mm, v(347.31, -188.99) * mm]});
            skFitSpline(sketch, "E389", {"points": [v(347.31, -188.99) * mm, v(347.35, -188.78) * mm, v(347.25, -188.57) * mm, v(347.07, -188.47) * mm]});
            skFitSpline(sketch, "E390", {"points": [v(346.39, -189.15) * mm, v(346.3, -189) * mm, v(346.13, -188.9) * mm, v(345.96, -188.9) * mm]});
            skLineSegment(sketch, "E391", {"start": v(343.52, -188.04) * mm, "end": v(343.52, -183.57) * mm});
            skFitSpline(sketch, "E392", {"points": [v(344.39, -167.7) * mm, v(344.2, -167.7) * mm, v(344.04, -167.8) * mm, v(343.96, -167.95) * mm]});
            skFitSpline(sketch, "E393", {"points": [v(343.27, -167.27) * mm, v(343.1, -167.37) * mm, v(343, -167.58) * mm, v(343.03, -167.79) * mm]});
            skFitSpline(sketch, "E394", {"points": [v(343.03, -167.79) * mm, v(343.07, -168) * mm, v(343.23, -168.16) * mm, v(343.44, -168.2) * mm]});
            skFitSpline(sketch, "E395", {"points": [v(343.44, -168.2) * mm, v(343.64, -168.23) * mm, v(343.85, -168.13) * mm, v(343.96, -167.95) * mm]});
            skFitSpline(sketch, "E396", {"points": [v(343.27, -167.27) * mm, v(343.43, -167.18) * mm, v(343.52, -167.01) * mm, v(343.52, -166.84) * mm]});
            skLineSegment(sketch, "E397", {"start": v(344.39, -182.7) * mm, "end": v(345.96, -182.7) * mm});
            skFitSpline(sketch, "E398", {"points": [v(343.52, -162.37) * mm, v(343.52, -162.19) * mm, v(343.43, -162.02) * mm, v(343.27, -161.94) * mm]});
            skFitSpline(sketch, "E399", {"points": [v(343.96, -161.25) * mm, v(343.85, -161.07) * mm, v(343.64, -160.97) * mm, v(343.44, -161) * mm]});
            skFitSpline(sketch, "E400", {"points": [v(343.44, -161) * mm, v(343.23, -161.05) * mm, v(343.07, -161.2) * mm, v(343.03, -161.42) * mm]});
            skFitSpline(sketch, "E401", {"points": [v(343.03, -161.42) * mm, v(343, -161.62) * mm, v(343.1, -161.83) * mm, v(343.27, -161.94) * mm]});
            skFitSpline(sketch, "E402", {"points": [v(343.96, -161.25) * mm, v(344.04, -161.4) * mm, v(344.2, -161.5) * mm, v(344.39, -161.5) * mm]});
            skLineSegment(sketch, "E403", {"start": v(346.82, -183.57) * mm, "end": v(346.82, -188.04) * mm});
            skFitSpline(sketch, "E404", {"points": [v(345.96, -161.5) * mm, v(346.13, -161.5) * mm, v(346.3, -161.4) * mm, v(346.39, -161.25) * mm]});
            skFitSpline(sketch, "E405", {"points": [v(347.07, -161.94) * mm, v(347.25, -161.83) * mm, v(347.35, -161.62) * mm, v(347.31, -161.42) * mm]});
            skFitSpline(sketch, "E406", {"points": [v(347.31, -161.42) * mm, v(347.28, -161.2) * mm, v(347.12, -161.05) * mm, v(346.9, -161) * mm]});
            skFitSpline(sketch, "E407", {"points": [v(346.9, -161) * mm, v(346.7, -160.97) * mm, v(346.5, -161.07) * mm, v(346.39, -161.25) * mm]});
            skFitSpline(sketch, "E408", {"points": [v(347.07, -161.94) * mm, v(346.92, -162.02) * mm, v(346.82, -162.19) * mm, v(346.82, -162.37) * mm]});
            skLineSegment(sketch, "E409", {"start": v(345.96, -188.9) * mm, "end": v(344.39, -188.9) * mm});
            skFitSpline(sketch, "E410", {"points": [v(346.82, -166.84) * mm, v(346.82, -167.01) * mm, v(346.92, -167.18) * mm, v(347.07, -167.27) * mm]});
            skFitSpline(sketch, "E411", {"points": [v(346.39, -167.95) * mm, v(346.5, -168.13) * mm, v(346.7, -168.23) * mm, v(346.9, -168.2) * mm]});
            skFitSpline(sketch, "E412", {"points": [v(346.9, -168.2) * mm, v(347.12, -168.16) * mm, v(347.28, -168) * mm, v(347.31, -167.79) * mm]});
            skFitSpline(sketch, "E413", {"points": [v(347.31, -167.79) * mm, v(347.35, -167.58) * mm, v(347.25, -167.37) * mm, v(347.07, -167.27) * mm]});
            skFitSpline(sketch, "E414", {"points": [v(346.39, -167.95) * mm, v(346.3, -167.8) * mm, v(346.13, -167.7) * mm, v(345.96, -167.7) * mm]});
            skLineSegment(sketch, "E415", {"start": v(343.52, -166.84) * mm, "end": v(343.52, -162.37) * mm});
            skFitSpline(sketch, "E416", {"points": [v(379.32, -149.9) * mm, v(379.32, -149.72) * mm, v(379.22, -149.55) * mm, v(379.07, -149.47) * mm]});
            skFitSpline(sketch, "E417", {"points": [v(379.75, -148.78) * mm, v(379.65, -148.6) * mm, v(379.44, -148.5) * mm, v(379.23, -148.54) * mm]});
            skFitSpline(sketch, "E418", {"points": [v(379.23, -148.54) * mm, v(379.02, -148.58) * mm, v(378.86, -148.74) * mm, v(378.82, -148.95) * mm]});
            skFitSpline(sketch, "E419", {"points": [v(378.82, -148.95) * mm, v(378.79, -149.15) * mm, v(378.89, -149.36) * mm, v(379.07, -149.47) * mm]});
            skFitSpline(sketch, "E420", {"points": [v(379.75, -148.78) * mm, v(379.84, -148.94) * mm, v(380, -149.03) * mm, v(380.18, -149.03) * mm]});
            skLineSegment(sketch, "E421", {"start": v(344.39, -161.5) * mm, "end": v(345.96, -161.5) * mm});
            skFitSpline(sketch, "E422", {"points": [v(384.65, -149.03) * mm, v(384.83, -149.03) * mm, v(385, -148.94) * mm, v(385.08, -148.78) * mm]});
            skFitSpline(sketch, "E423", {"points": [v(385.77, -149.47) * mm, v(385.95, -149.36) * mm, v(386.05, -149.15) * mm, v(386, -148.95) * mm]});
            skFitSpline(sketch, "E424", {"points": [v(386, -148.95) * mm, v(385.97, -148.74) * mm, v(385.81, -148.58) * mm, v(385.6, -148.54) * mm]});
            skFitSpline(sketch, "E425", {"points": [v(385.6, -148.54) * mm, v(385.4, -148.5) * mm, v(385.19, -148.6) * mm, v(385.08, -148.78) * mm]});
            skFitSpline(sketch, "E426", {"points": [v(385.77, -149.47) * mm, v(385.61, -149.55) * mm, v(385.52, -149.72) * mm, v(385.52, -149.9) * mm]});
            skLineSegment(sketch, "E427", {"start": v(346.82, -162.37) * mm, "end": v(346.82, -166.84) * mm});
            skFitSpline(sketch, "E428", {"points": [v(385.52, -151.47) * mm, v(385.52, -151.64) * mm, v(385.61, -151.8) * mm, v(385.77, -151.9) * mm]});
            skFitSpline(sketch, "E429", {"points": [v(385.08, -152.58) * mm, v(385.19, -152.76) * mm, v(385.4, -152.86) * mm, v(385.6, -152.82) * mm]});
            skFitSpline(sketch, "E430", {"points": [v(385.6, -152.82) * mm, v(385.81, -152.79) * mm, v(385.97, -152.63) * mm, v(386, -152.42) * mm]});
            skFitSpline(sketch, "E431", {"points": [v(386, -152.42) * mm, v(386.05, -152.21) * mm, v(385.95, -152) * mm, v(385.77, -151.9) * mm]});
            skFitSpline(sketch, "E432", {"points": [v(385.08, -152.58) * mm, v(385, -152.43) * mm, v(384.83, -152.33) * mm, v(384.65, -152.33) * mm]});
            skLineSegment(sketch, "E433", {"start": v(345.96, -167.7) * mm, "end": v(344.39, -167.7) * mm});
            skFitSpline(sketch, "E434", {"points": [v(380.18, -152.33) * mm, v(380, -152.33) * mm, v(379.84, -152.43) * mm, v(379.75, -152.58) * mm]});
            skFitSpline(sketch, "E435", {"points": [v(379.07, -151.9) * mm, v(378.89, -152) * mm, v(378.79, -152.21) * mm, v(378.82, -152.42) * mm]});
            skFitSpline(sketch, "E436", {"points": [v(378.82, -152.42) * mm, v(378.86, -152.63) * mm, v(379.02, -152.79) * mm, v(379.23, -152.82) * mm]});
            skFitSpline(sketch, "E437", {"points": [v(379.23, -152.82) * mm, v(379.44, -152.86) * mm, v(379.65, -152.76) * mm, v(379.75, -152.58) * mm]});
            skFitSpline(sketch, "E438", {"points": [v(379.07, -151.9) * mm, v(379.22, -151.8) * mm, v(379.32, -151.64) * mm, v(379.32, -151.47) * mm]});
            skLineSegment(sketch, "E439", {"start": v(380.18, -149.03) * mm, "end": v(384.65, -149.03) * mm});
            skFitSpline(sketch, "E440", {"points": [v(358.12, -149.9) * mm, v(358.12, -149.72) * mm, v(358.02, -149.55) * mm, v(357.87, -149.47) * mm]});
            skFitSpline(sketch, "E441", {"points": [v(358.55, -148.78) * mm, v(358.45, -148.6) * mm, v(358.24, -148.5) * mm, v(358.03, -148.54) * mm]});
            skFitSpline(sketch, "E442", {"points": [v(358.03, -148.54) * mm, v(357.82, -148.58) * mm, v(357.66, -148.74) * mm, v(357.62, -148.95) * mm]});
            skFitSpline(sketch, "E443", {"points": [v(357.62, -148.95) * mm, v(357.59, -149.15) * mm, v(357.69, -149.36) * mm, v(357.87, -149.47) * mm]});
            skFitSpline(sketch, "E444", {"points": [v(358.55, -148.78) * mm, v(358.64, -148.94) * mm, v(358.8, -149.03) * mm, v(358.98, -149.03) * mm]});
            skLineSegment(sketch, "E445", {"start": v(385.52, -149.9) * mm, "end": v(385.52, -151.47) * mm});
            skFitSpline(sketch, "E446", {"points": [v(363.45, -149.03) * mm, v(363.63, -149.03) * mm, v(363.8, -148.94) * mm, v(363.88, -148.78) * mm]});
            skFitSpline(sketch, "E447", {"points": [v(364.57, -149.47) * mm, v(364.75, -149.36) * mm, v(364.85, -149.15) * mm, v(364.8, -148.95) * mm]});
            skFitSpline(sketch, "E448", {"points": [v(364.8, -148.95) * mm, v(364.77, -148.74) * mm, v(364.61, -148.58) * mm, v(364.4, -148.54) * mm]});
            skFitSpline(sketch, "E449", {"points": [v(364.4, -148.54) * mm, v(364.2, -148.5) * mm, v(363.99, -148.6) * mm, v(363.88, -148.78) * mm]});
            skFitSpline(sketch, "E450", {"points": [v(364.57, -149.47) * mm, v(364.41, -149.55) * mm, v(364.32, -149.72) * mm, v(364.32, -149.9) * mm]});
            skLineSegment(sketch, "E451", {"start": v(384.65, -152.33) * mm, "end": v(380.18, -152.33) * mm});
            skFitSpline(sketch, "E452", {"points": [v(364.32, -151.47) * mm, v(364.32, -151.64) * mm, v(364.41, -151.8) * mm, v(364.57, -151.9) * mm]});
            skFitSpline(sketch, "E453", {"points": [v(363.88, -152.58) * mm, v(363.99, -152.76) * mm, v(364.2, -152.86) * mm, v(364.4, -152.82) * mm]});
            skFitSpline(sketch, "E454", {"points": [v(364.4, -152.82) * mm, v(364.61, -152.79) * mm, v(364.77, -152.63) * mm, v(364.8, -152.42) * mm]});
            skFitSpline(sketch, "E455", {"points": [v(364.8, -152.42) * mm, v(364.85, -152.21) * mm, v(364.75, -152) * mm, v(364.57, -151.9) * mm]});
            skFitSpline(sketch, "E456", {"points": [v(363.88, -152.58) * mm, v(363.8, -152.43) * mm, v(363.63, -152.33) * mm, v(363.45, -152.33) * mm]});
            skLineSegment(sketch, "E457", {"start": v(379.32, -151.47) * mm, "end": v(379.32, -149.9) * mm});
            skFitSpline(sketch, "E458", {"points": [v(358.98, -152.33) * mm, v(358.8, -152.33) * mm, v(358.64, -152.43) * mm, v(358.55, -152.58) * mm]});
            skFitSpline(sketch, "E459", {"points": [v(357.87, -151.9) * mm, v(357.69, -152) * mm, v(357.59, -152.21) * mm, v(357.62, -152.42) * mm]});
            skFitSpline(sketch, "E460", {"points": [v(357.62, -152.42) * mm, v(357.66, -152.63) * mm, v(357.82, -152.79) * mm, v(358.03, -152.82) * mm]});
            skFitSpline(sketch, "E461", {"points": [v(358.03, -152.82) * mm, v(358.24, -152.86) * mm, v(358.45, -152.76) * mm, v(358.55, -152.58) * mm]});
            skFitSpline(sketch, "E462", {"points": [v(357.87, -151.9) * mm, v(358.02, -151.8) * mm, v(358.12, -151.64) * mm, v(358.12, -151.47) * mm]});
            skLineSegment(sketch, "E463", {"start": v(358.98, -149.03) * mm, "end": v(363.45, -149.03) * mm});
            skFitSpline(sketch, "E464", {"points": [v(339.07, -131.3) * mm, v(339.22, -131.2) * mm, v(339.32, -131.04) * mm, v(339.32, -130.86) * mm]});
            skFitSpline(sketch, "E465", {"points": [v(339.07, -131.3) * mm, v(338.89, -131.4) * mm, v(338.79, -131.6) * mm, v(338.82, -131.81) * mm]});
            skFitSpline(sketch, "E466", {"points": [v(338.82, -131.81) * mm, v(338.86, -132.02) * mm, v(339.02, -132.18) * mm, v(339.23, -132.22) * mm]});
            skFitSpline(sketch, "E467", {"points": [v(339.23, -132.22) * mm, v(339.44, -132.26) * mm, v(339.65, -132.16) * mm, v(339.75, -131.98) * mm]});
            skFitSpline(sketch, "E468", {"points": [v(340.18, -131.73) * mm, v(340, -131.73) * mm, v(339.84, -131.82) * mm, v(339.75, -131.98) * mm]});
            skLineSegment(sketch, "E469", {"start": v(364.32, -149.9) * mm, "end": v(364.32, -151.47) * mm});
            skFitSpline(sketch, "E470", {"points": [v(345.08, -131.98) * mm, v(345, -131.82) * mm, v(344.83, -131.73) * mm, v(344.65, -131.73) * mm]});
            skFitSpline(sketch, "E471", {"points": [v(345.08, -131.98) * mm, v(345.19, -132.16) * mm, v(345.4, -132.26) * mm, v(345.6, -132.22) * mm]});
            skFitSpline(sketch, "E472", {"points": [v(345.6, -132.22) * mm, v(345.81, -132.18) * mm, v(345.97, -132.02) * mm, v(346, -131.81) * mm]});
            skFitSpline(sketch, "E473", {"points": [v(346, -131.81) * mm, v(346.05, -131.6) * mm, v(345.95, -131.4) * mm, v(345.77, -131.3) * mm]});
            skFitSpline(sketch, "E474", {"points": [v(345.52, -130.86) * mm, v(345.52, -131.04) * mm, v(345.61, -131.2) * mm, v(345.77, -131.3) * mm]});
            skLineSegment(sketch, "E475", {"start": v(363.45, -152.33) * mm, "end": v(358.98, -152.33) * mm});
            skFitSpline(sketch, "E476", {"points": [v(345.77, -128.86) * mm, v(345.61, -128.95) * mm, v(345.52, -129.11) * mm, v(345.52, -129.3) * mm]});
            skFitSpline(sketch, "E477", {"points": [v(345.77, -128.86) * mm, v(345.95, -128.76) * mm, v(346.05, -128.55) * mm, v(346, -128.34) * mm]});
            skFitSpline(sketch, "E478", {"points": [v(346, -128.34) * mm, v(345.97, -128.13) * mm, v(345.81, -127.97) * mm, v(345.6, -127.93) * mm]});
            skFitSpline(sketch, "E479", {"points": [v(345.6, -127.93) * mm, v(345.4, -127.9) * mm, v(345.19, -128) * mm, v(345.08, -128.18) * mm]});
            skFitSpline(sketch, "E480", {"points": [v(344.65, -128.43) * mm, v(344.83, -128.43) * mm, v(345, -128.33) * mm, v(345.08, -128.18) * mm]});
            skLineSegment(sketch, "E481", {"start": v(358.12, -151.47) * mm, "end": v(358.12, -149.9) * mm});
            skFitSpline(sketch, "E482", {"points": [v(339.75, -128.18) * mm, v(339.84, -128.33) * mm, v(340, -128.43) * mm, v(340.18, -128.43) * mm]});
            skFitSpline(sketch, "E483", {"points": [v(339.75, -128.18) * mm, v(339.65, -128) * mm, v(339.44, -127.9) * mm, v(339.23, -127.93) * mm]});
            skFitSpline(sketch, "E484", {"points": [v(339.23, -127.93) * mm, v(339.02, -127.97) * mm, v(338.86, -128.13) * mm, v(338.82, -128.34) * mm]});
            skFitSpline(sketch, "E485", {"points": [v(338.82, -128.34) * mm, v(338.79, -128.55) * mm, v(338.89, -128.76) * mm, v(339.07, -128.86) * mm]});
            skFitSpline(sketch, "E486", {"points": [v(339.32, -129.3) * mm, v(339.32, -129.11) * mm, v(339.22, -128.95) * mm, v(339.07, -128.86) * mm]});
            skLineSegment(sketch, "E487", {"start": v(340.18, -131.73) * mm, "end": v(344.65, -131.73) * mm});
            skFitSpline(sketch, "E488", {"points": [v(317.87, -131.3) * mm, v(318.02, -131.2) * mm, v(318.12, -131.04) * mm, v(318.12, -130.86) * mm]});
            skFitSpline(sketch, "E489", {"points": [v(317.87, -131.3) * mm, v(317.69, -131.4) * mm, v(317.59, -131.6) * mm, v(317.62, -131.81) * mm]});
            skFitSpline(sketch, "E490", {"points": [v(317.62, -131.81) * mm, v(317.66, -132.02) * mm, v(317.82, -132.18) * mm, v(318.03, -132.22) * mm]});
            skFitSpline(sketch, "E491", {"points": [v(318.03, -132.22) * mm, v(318.24, -132.26) * mm, v(318.45, -132.16) * mm, v(318.55, -131.98) * mm]});
            skFitSpline(sketch, "E492", {"points": [v(318.98, -131.73) * mm, v(318.8, -131.73) * mm, v(318.64, -131.82) * mm, v(318.55, -131.98) * mm]});
            skLineSegment(sketch, "E493", {"start": v(345.52, -130.86) * mm, "end": v(345.52, -129.3) * mm});
            skFitSpline(sketch, "E494", {"points": [v(323.88, -131.98) * mm, v(323.8, -131.82) * mm, v(323.63, -131.73) * mm, v(323.45, -131.73) * mm]});
            skFitSpline(sketch, "E495", {"points": [v(323.88, -131.98) * mm, v(323.99, -132.16) * mm, v(324.2, -132.26) * mm, v(324.4, -132.22) * mm]});
            skFitSpline(sketch, "E496", {"points": [v(324.4, -132.22) * mm, v(324.61, -132.18) * mm, v(324.77, -132.02) * mm, v(324.8, -131.81) * mm]});
            skFitSpline(sketch, "E497", {"points": [v(324.8, -131.81) * mm, v(324.85, -131.6) * mm, v(324.75, -131.4) * mm, v(324.57, -131.3) * mm]});
            skFitSpline(sketch, "E498", {"points": [v(324.32, -130.86) * mm, v(324.32, -131.04) * mm, v(324.41, -131.2) * mm, v(324.57, -131.3) * mm]});
            skLineSegment(sketch, "E499", {"start": v(344.65, -128.43) * mm, "end": v(340.18, -128.43) * mm});
            skFitSpline(sketch, "E500", {"points": [v(324.57, -128.86) * mm, v(324.41, -128.95) * mm, v(324.32, -129.11) * mm, v(324.32, -129.3) * mm]});
            skFitSpline(sketch, "E501", {"points": [v(324.57, -128.86) * mm, v(324.75, -128.76) * mm, v(324.85, -128.55) * mm, v(324.8, -128.34) * mm]});
            skFitSpline(sketch, "E502", {"points": [v(324.8, -128.34) * mm, v(324.77, -128.13) * mm, v(324.61, -127.97) * mm, v(324.4, -127.93) * mm]});
            skFitSpline(sketch, "E503", {"points": [v(324.4, -127.93) * mm, v(324.2, -127.9) * mm, v(323.99, -128) * mm, v(323.88, -128.18) * mm]});
            skFitSpline(sketch, "E504", {"points": [v(323.45, -128.43) * mm, v(323.63, -128.43) * mm, v(323.8, -128.33) * mm, v(323.88, -128.18) * mm]});
            skLineSegment(sketch, "E505", {"start": v(339.32, -129.3) * mm, "end": v(339.32, -130.86) * mm});
            skFitSpline(sketch, "E506", {"points": [v(318.55, -128.18) * mm, v(318.64, -128.33) * mm, v(318.8, -128.43) * mm, v(318.98, -128.43) * mm]});
            skFitSpline(sketch, "E507", {"points": [v(318.55, -128.18) * mm, v(318.45, -128) * mm, v(318.24, -127.9) * mm, v(318.03, -127.93) * mm]});
            skFitSpline(sketch, "E508", {"points": [v(318.03, -127.93) * mm, v(317.82, -127.97) * mm, v(317.66, -128.13) * mm, v(317.62, -128.34) * mm]});
            skFitSpline(sketch, "E509", {"points": [v(317.62, -128.34) * mm, v(317.59, -128.55) * mm, v(317.69, -128.76) * mm, v(317.87, -128.86) * mm]});
            skFitSpline(sketch, "E510", {"points": [v(318.12, -129.3) * mm, v(318.12, -129.11) * mm, v(318.02, -128.95) * mm, v(317.87, -128.86) * mm]});
            skLineSegment(sketch, "E511", {"start": v(318.98, -131.73) * mm, "end": v(323.45, -131.73) * mm});
            skFitSpline(sketch, "E512", {"points": [v(219.32, -129.3) * mm, v(219.32, -129.11) * mm, v(219.22, -128.95) * mm, v(219.07, -128.86) * mm]});
            skFitSpline(sketch, "E513", {"points": [v(219.75, -128.18) * mm, v(219.65, -128) * mm, v(219.44, -127.9) * mm, v(219.23, -127.93) * mm]});
            skFitSpline(sketch, "E514", {"points": [v(219.23, -127.93) * mm, v(219.02, -127.97) * mm, v(218.86, -128.13) * mm, v(218.82, -128.34) * mm]});
            skFitSpline(sketch, "E515", {"points": [v(218.82, -128.34) * mm, v(218.79, -128.55) * mm, v(218.89, -128.76) * mm, v(219.07, -128.86) * mm]});
            skFitSpline(sketch, "E516", {"points": [v(219.75, -128.18) * mm, v(219.84, -128.33) * mm, v(220, -128.43) * mm, v(220.18, -128.43) * mm]});
            skLineSegment(sketch, "E517", {"start": v(324.32, -130.86) * mm, "end": v(324.32, -129.3) * mm});
            skFitSpline(sketch, "E518", {"points": [v(224.65, -128.43) * mm, v(224.83, -128.43) * mm, v(225, -128.33) * mm, v(225.08, -128.18) * mm]});
            skFitSpline(sketch, "E519", {"points": [v(225.77, -128.86) * mm, v(225.95, -128.76) * mm, v(226.05, -128.55) * mm, v(226, -128.34) * mm]});
            skFitSpline(sketch, "E520", {"points": [v(226, -128.34) * mm, v(225.97, -128.13) * mm, v(225.81, -127.97) * mm, v(225.6, -127.93) * mm]});
            skFitSpline(sketch, "E521", {"points": [v(225.6, -127.93) * mm, v(225.4, -127.9) * mm, v(225.19, -128) * mm, v(225.08, -128.18) * mm]});
            skFitSpline(sketch, "E522", {"points": [v(225.77, -128.86) * mm, v(225.61, -128.95) * mm, v(225.52, -129.11) * mm, v(225.52, -129.3) * mm]});
            skLineSegment(sketch, "E523", {"start": v(323.45, -128.43) * mm, "end": v(318.98, -128.43) * mm});
            skFitSpline(sketch, "E524", {"points": [v(225.52, -130.86) * mm, v(225.52, -131.04) * mm, v(225.61, -131.2) * mm, v(225.77, -131.3) * mm]});
            skFitSpline(sketch, "E525", {"points": [v(225.08, -131.98) * mm, v(225.19, -132.16) * mm, v(225.4, -132.26) * mm, v(225.6, -132.22) * mm]});
            skFitSpline(sketch, "E526", {"points": [v(225.6, -132.22) * mm, v(225.81, -132.18) * mm, v(225.97, -132.02) * mm, v(226, -131.81) * mm]});
            skFitSpline(sketch, "E527", {"points": [v(226, -131.81) * mm, v(226.05, -131.6) * mm, v(225.95, -131.4) * mm, v(225.77, -131.3) * mm]});
            skFitSpline(sketch, "E528", {"points": [v(225.08, -131.98) * mm, v(225, -131.82) * mm, v(224.83, -131.73) * mm, v(224.65, -131.73) * mm]});
            skLineSegment(sketch, "E529", {"start": v(318.12, -129.3) * mm, "end": v(318.12, -130.86) * mm});
            skFitSpline(sketch, "E530", {"points": [v(220.18, -131.73) * mm, v(220, -131.73) * mm, v(219.84, -131.82) * mm, v(219.75, -131.98) * mm]});
            skFitSpline(sketch, "E531", {"points": [v(219.07, -131.3) * mm, v(218.89, -131.4) * mm, v(218.79, -131.6) * mm, v(218.82, -131.81) * mm]});
            skFitSpline(sketch, "E532", {"points": [v(218.82, -131.81) * mm, v(218.86, -132.02) * mm, v(219.02, -132.18) * mm, v(219.23, -132.22) * mm]});
            skFitSpline(sketch, "E533", {"points": [v(219.23, -132.22) * mm, v(219.44, -132.26) * mm, v(219.65, -132.16) * mm, v(219.75, -131.98) * mm]});
            skFitSpline(sketch, "E534", {"points": [v(219.07, -131.3) * mm, v(219.22, -131.2) * mm, v(219.32, -131.04) * mm, v(219.32, -130.86) * mm]});
            skLineSegment(sketch, "E535", {"start": v(220.18, -128.43) * mm, "end": v(224.65, -128.43) * mm});
            skFitSpline(sketch, "E536", {"points": [v(198.12, -129.3) * mm, v(198.12, -129.11) * mm, v(198.02, -128.95) * mm, v(197.87, -128.86) * mm]});
            skFitSpline(sketch, "E537", {"points": [v(198.55, -128.18) * mm, v(198.45, -128) * mm, v(198.24, -127.9) * mm, v(198.03, -127.93) * mm]});
            skFitSpline(sketch, "E538", {"points": [v(198.03, -127.93) * mm, v(197.82, -127.97) * mm, v(197.66, -128.13) * mm, v(197.62, -128.34) * mm]});
            skFitSpline(sketch, "E539", {"points": [v(197.62, -128.34) * mm, v(197.59, -128.55) * mm, v(197.69, -128.76) * mm, v(197.87, -128.86) * mm]});
            skFitSpline(sketch, "E540", {"points": [v(198.55, -128.18) * mm, v(198.64, -128.33) * mm, v(198.8, -128.43) * mm, v(198.98, -128.43) * mm]});
            skLineSegment(sketch, "E541", {"start": v(225.52, -129.3) * mm, "end": v(225.52, -130.86) * mm});
            skFitSpline(sketch, "E542", {"points": [v(203.45, -128.43) * mm, v(203.63, -128.43) * mm, v(203.8, -128.33) * mm, v(203.88, -128.18) * mm]});
            skFitSpline(sketch, "E543", {"points": [v(204.57, -128.86) * mm, v(204.75, -128.76) * mm, v(204.85, -128.55) * mm, v(204.8, -128.34) * mm]});
            skFitSpline(sketch, "E544", {"points": [v(204.8, -128.34) * mm, v(204.77, -128.13) * mm, v(204.61, -127.97) * mm, v(204.4, -127.93) * mm]});
            skFitSpline(sketch, "E545", {"points": [v(204.4, -127.93) * mm, v(204.2, -127.9) * mm, v(203.99, -128) * mm, v(203.88, -128.18) * mm]});
            skFitSpline(sketch, "E546", {"points": [v(204.57, -128.86) * mm, v(204.41, -128.95) * mm, v(204.32, -129.11) * mm, v(204.32, -129.3) * mm]});
            skLineSegment(sketch, "E547", {"start": v(224.65, -131.73) * mm, "end": v(220.18, -131.73) * mm});
            skFitSpline(sketch, "E548", {"points": [v(204.32, -130.86) * mm, v(204.32, -131.04) * mm, v(204.41, -131.2) * mm, v(204.57, -131.3) * mm]});
            skFitSpline(sketch, "E549", {"points": [v(203.88, -131.98) * mm, v(203.99, -132.16) * mm, v(204.2, -132.26) * mm, v(204.4, -132.22) * mm]});
            skFitSpline(sketch, "E550", {"points": [v(204.4, -132.22) * mm, v(204.61, -132.18) * mm, v(204.77, -132.02) * mm, v(204.8, -131.81) * mm]});
            skFitSpline(sketch, "E551", {"points": [v(204.8, -131.81) * mm, v(204.85, -131.6) * mm, v(204.75, -131.4) * mm, v(204.57, -131.3) * mm]});
            skFitSpline(sketch, "E552", {"points": [v(203.88, -131.98) * mm, v(203.8, -131.82) * mm, v(203.63, -131.73) * mm, v(203.45, -131.73) * mm]});
            skLineSegment(sketch, "E553", {"start": v(219.32, -130.86) * mm, "end": v(219.32, -129.3) * mm});
            skFitSpline(sketch, "E554", {"points": [v(198.98, -131.73) * mm, v(198.8, -131.73) * mm, v(198.64, -131.82) * mm, v(198.55, -131.98) * mm]});
            skFitSpline(sketch, "E555", {"points": [v(197.87, -131.3) * mm, v(197.69, -131.4) * mm, v(197.59, -131.6) * mm, v(197.62, -131.81) * mm]});
            skFitSpline(sketch, "E556", {"points": [v(197.62, -131.81) * mm, v(197.66, -132.02) * mm, v(197.82, -132.18) * mm, v(198.03, -132.22) * mm]});
            skFitSpline(sketch, "E557", {"points": [v(198.03, -132.22) * mm, v(198.24, -132.26) * mm, v(198.45, -132.16) * mm, v(198.55, -131.98) * mm]});
            skFitSpline(sketch, "E558", {"points": [v(197.87, -131.3) * mm, v(198.02, -131.2) * mm, v(198.12, -131.04) * mm, v(198.12, -130.86) * mm]});
            skLineSegment(sketch, "E559", {"start": v(198.98, -128.43) * mm, "end": v(203.45, -128.43) * mm});
            skFitSpline(sketch, "E560", {"points": [v(59.32, -129.3) * mm, v(59.32, -129.11) * mm, v(59.22, -128.95) * mm, v(59.07, -128.86) * mm]});
            skFitSpline(sketch, "E561", {"points": [v(59.75, -128.18) * mm, v(59.65, -128) * mm, v(59.44, -127.9) * mm, v(59.23, -127.93) * mm]});
            skFitSpline(sketch, "E562", {"points": [v(59.23, -127.93) * mm, v(59.02, -127.97) * mm, v(58.86, -128.13) * mm, v(58.82, -128.34) * mm]});
            skFitSpline(sketch, "E563", {"points": [v(58.82, -128.34) * mm, v(58.79, -128.55) * mm, v(58.89, -128.76) * mm, v(59.07, -128.86) * mm]});
            skFitSpline(sketch, "E564", {"points": [v(59.75, -128.18) * mm, v(59.84, -128.33) * mm, v(60, -128.43) * mm, v(60.18, -128.43) * mm]});
            skLineSegment(sketch, "E565", {"start": v(204.32, -129.3) * mm, "end": v(204.32, -130.86) * mm});
            skFitSpline(sketch, "E566", {"points": [v(64.65, -128.43) * mm, v(64.83, -128.43) * mm, v(65, -128.33) * mm, v(65.08, -128.18) * mm]});
            skFitSpline(sketch, "E567", {"points": [v(65.77, -128.86) * mm, v(65.95, -128.76) * mm, v(66.05, -128.55) * mm, v(66, -128.34) * mm]});
            skFitSpline(sketch, "E568", {"points": [v(66, -128.34) * mm, v(65.97, -128.13) * mm, v(65.81, -127.97) * mm, v(65.6, -127.93) * mm]});
            skFitSpline(sketch, "E569", {"points": [v(65.6, -127.93) * mm, v(65.4, -127.9) * mm, v(65.19, -128) * mm, v(65.08, -128.18) * mm]});
            skFitSpline(sketch, "E570", {"points": [v(65.77, -128.86) * mm, v(65.61, -128.95) * mm, v(65.52, -129.11) * mm, v(65.52, -129.3) * mm]});
            skLineSegment(sketch, "E571", {"start": v(203.45, -131.73) * mm, "end": v(198.98, -131.73) * mm});
            skFitSpline(sketch, "E572", {"points": [v(65.52, -130.86) * mm, v(65.52, -131.04) * mm, v(65.61, -131.2) * mm, v(65.77, -131.3) * mm]});
            skFitSpline(sketch, "E573", {"points": [v(65.08, -131.98) * mm, v(65.19, -132.16) * mm, v(65.4, -132.26) * mm, v(65.6, -132.22) * mm]});
            skFitSpline(sketch, "E574", {"points": [v(65.6, -132.22) * mm, v(65.81, -132.18) * mm, v(65.97, -132.02) * mm, v(66, -131.81) * mm]});
            skFitSpline(sketch, "E575", {"points": [v(66, -131.81) * mm, v(66.05, -131.6) * mm, v(65.95, -131.4) * mm, v(65.77, -131.3) * mm]});
            skFitSpline(sketch, "E576", {"points": [v(65.08, -131.98) * mm, v(65, -131.82) * mm, v(64.83, -131.73) * mm, v(64.65, -131.73) * mm]});
            skLineSegment(sketch, "E577", {"start": v(198.12, -130.86) * mm, "end": v(198.12, -129.3) * mm});
            skFitSpline(sketch, "E578", {"points": [v(60.18, -131.73) * mm, v(60, -131.73) * mm, v(59.84, -131.82) * mm, v(59.75, -131.98) * mm]});
            skFitSpline(sketch, "E579", {"points": [v(59.07, -131.3) * mm, v(58.89, -131.4) * mm, v(58.79, -131.6) * mm, v(58.82, -131.81) * mm]});
            skFitSpline(sketch, "E580", {"points": [v(58.82, -131.81) * mm, v(58.86, -132.02) * mm, v(59.02, -132.18) * mm, v(59.23, -132.22) * mm]});
            skFitSpline(sketch, "E581", {"points": [v(59.23, -132.22) * mm, v(59.44, -132.26) * mm, v(59.65, -132.16) * mm, v(59.75, -131.98) * mm]});
            skFitSpline(sketch, "E582", {"points": [v(59.07, -131.3) * mm, v(59.22, -131.2) * mm, v(59.32, -131.04) * mm, v(59.32, -130.86) * mm]});
            skLineSegment(sketch, "E583", {"start": v(60.18, -128.43) * mm, "end": v(64.65, -128.43) * mm});
            skFitSpline(sketch, "E584", {"points": [v(38.12, -129.3) * mm, v(38.12, -129.11) * mm, v(38.02, -128.95) * mm, v(37.87, -128.86) * mm]});
            skFitSpline(sketch, "E585", {"points": [v(38.55, -128.18) * mm, v(38.45, -128) * mm, v(38.24, -127.9) * mm, v(38.03, -127.93) * mm]});
            skFitSpline(sketch, "E586", {"points": [v(38.03, -127.93) * mm, v(37.82, -127.97) * mm, v(37.66, -128.13) * mm, v(37.62, -128.34) * mm]});
            skFitSpline(sketch, "E587", {"points": [v(37.62, -128.34) * mm, v(37.59, -128.55) * mm, v(37.69, -128.76) * mm, v(37.87, -128.86) * mm]});
            skFitSpline(sketch, "E588", {"points": [v(38.55, -128.18) * mm, v(38.64, -128.33) * mm, v(38.8, -128.43) * mm, v(38.98, -128.43) * mm]});
            skLineSegment(sketch, "E589", {"start": v(65.52, -129.3) * mm, "end": v(65.52, -130.86) * mm});
            skFitSpline(sketch, "E590", {"points": [v(43.45, -128.43) * mm, v(43.63, -128.43) * mm, v(43.8, -128.33) * mm, v(43.88, -128.18) * mm]});
            skFitSpline(sketch, "E591", {"points": [v(44.57, -128.86) * mm, v(44.75, -128.76) * mm, v(44.85, -128.55) * mm, v(44.8, -128.34) * mm]});
            skFitSpline(sketch, "E592", {"points": [v(44.8, -128.34) * mm, v(44.77, -128.13) * mm, v(44.61, -127.97) * mm, v(44.4, -127.93) * mm]});
            skFitSpline(sketch, "E593", {"points": [v(44.4, -127.93) * mm, v(44.2, -127.9) * mm, v(43.99, -128) * mm, v(43.88, -128.18) * mm]});
            skFitSpline(sketch, "E594", {"points": [v(44.57, -128.86) * mm, v(44.41, -128.95) * mm, v(44.32, -129.11) * mm, v(44.32, -129.3) * mm]});
            skLineSegment(sketch, "E595", {"start": v(64.65, -131.73) * mm, "end": v(60.18, -131.73) * mm});
            skFitSpline(sketch, "E596", {"points": [v(44.32, -130.86) * mm, v(44.32, -131.04) * mm, v(44.41, -131.2) * mm, v(44.57, -131.3) * mm]});
            skFitSpline(sketch, "E597", {"points": [v(43.88, -131.98) * mm, v(43.99, -132.16) * mm, v(44.2, -132.26) * mm, v(44.4, -132.22) * mm]});
            skFitSpline(sketch, "E598", {"points": [v(44.4, -132.22) * mm, v(44.61, -132.18) * mm, v(44.77, -132.02) * mm, v(44.8, -131.81) * mm]});
            skFitSpline(sketch, "E599", {"points": [v(44.8, -131.81) * mm, v(44.85, -131.6) * mm, v(44.75, -131.4) * mm, v(44.57, -131.3) * mm]});
            skFitSpline(sketch, "E600", {"points": [v(43.88, -131.98) * mm, v(43.8, -131.82) * mm, v(43.63, -131.73) * mm, v(43.45, -131.73) * mm]});
            skLineSegment(sketch, "E601", {"start": v(59.32, -130.86) * mm, "end": v(59.32, -129.3) * mm});
            skFitSpline(sketch, "E602", {"points": [v(38.98, -131.73) * mm, v(38.8, -131.73) * mm, v(38.64, -131.82) * mm, v(38.55, -131.98) * mm]});
            skFitSpline(sketch, "E603", {"points": [v(37.87, -131.3) * mm, v(37.69, -131.4) * mm, v(37.59, -131.6) * mm, v(37.62, -131.81) * mm]});
            skFitSpline(sketch, "E604", {"points": [v(37.62, -131.81) * mm, v(37.66, -132.02) * mm, v(37.82, -132.18) * mm, v(38.03, -132.22) * mm]});
            skFitSpline(sketch, "E605", {"points": [v(38.03, -132.22) * mm, v(38.24, -132.26) * mm, v(38.45, -132.16) * mm, v(38.55, -131.98) * mm]});
            skFitSpline(sketch, "E606", {"points": [v(37.87, -131.3) * mm, v(38.02, -131.2) * mm, v(38.12, -131.04) * mm, v(38.12, -130.86) * mm]});
            skLineSegment(sketch, "E607", {"start": v(38.98, -128.43) * mm, "end": v(43.45, -128.43) * mm});
            skFitSpline(sketch, "E608", {"points": [v(339.07, 109.06) * mm, v(339.22, 109.15) * mm, v(339.32, 109.31) * mm, v(339.32, 109.49) * mm]});
            skFitSpline(sketch, "E609", {"points": [v(339.07, 109.06) * mm, v(338.89, 108.95) * mm, v(338.79, 108.74) * mm, v(338.82, 108.54) * mm]});
            skFitSpline(sketch, "E610", {"points": [v(338.82, 108.54) * mm, v(338.86, 108.33) * mm, v(339.02, 108.17) * mm, v(339.23, 108.13) * mm]});
            skFitSpline(sketch, "E611", {"points": [v(339.23, 108.13) * mm, v(339.44, 108.1) * mm, v(339.65, 108.2) * mm, v(339.75, 108.37) * mm]});
            skFitSpline(sketch, "E612", {"points": [v(340.18, 108.62) * mm, v(340, 108.62) * mm, v(339.84, 108.53) * mm, v(339.75, 108.37) * mm]});
            skLineSegment(sketch, "E613", {"start": v(44.32, -129.3) * mm, "end": v(44.32, -130.86) * mm});
            skFitSpline(sketch, "E614", {"points": [v(345.08, 108.37) * mm, v(345, 108.53) * mm, v(344.83, 108.62) * mm, v(344.65, 108.62) * mm]});
            skFitSpline(sketch, "E615", {"points": [v(345.08, 108.37) * mm, v(345.19, 108.2) * mm, v(345.4, 108.1) * mm, v(345.6, 108.13) * mm]});
            skFitSpline(sketch, "E616", {"points": [v(345.6, 108.13) * mm, v(345.81, 108.17) * mm, v(345.97, 108.33) * mm, v(346, 108.54) * mm]});
            skFitSpline(sketch, "E617", {"points": [v(346, 108.54) * mm, v(346.05, 108.74) * mm, v(345.95, 108.95) * mm, v(345.77, 109.06) * mm]});
            skFitSpline(sketch, "E618", {"points": [v(345.52, 109.49) * mm, v(345.52, 109.31) * mm, v(345.61, 109.15) * mm, v(345.77, 109.06) * mm]});
            skLineSegment(sketch, "E619", {"start": v(43.45, -131.73) * mm, "end": v(38.98, -131.73) * mm});
            skFitSpline(sketch, "E620", {"points": [v(345.77, 111.49) * mm, v(345.61, 111.4) * mm, v(345.52, 111.24) * mm, v(345.52, 111.06) * mm]});
            skFitSpline(sketch, "E621", {"points": [v(345.77, 111.49) * mm, v(345.95, 111.6) * mm, v(346.05, 111.8) * mm, v(346, 112) * mm]});
            skFitSpline(sketch, "E622", {"points": [v(346, 112) * mm, v(345.97, 112.22) * mm, v(345.81, 112.38) * mm, v(345.6, 112.42) * mm]});
            skFitSpline(sketch, "E623", {"points": [v(345.6, 112.42) * mm, v(345.4, 112.45) * mm, v(345.19, 112.35) * mm, v(345.08, 112.17) * mm]});
            skFitSpline(sketch, "E624", {"points": [v(344.65, 111.92) * mm, v(344.83, 111.92) * mm, v(345, 112.02) * mm, v(345.08, 112.17) * mm]});
            skLineSegment(sketch, "E625", {"start": v(38.12, -130.86) * mm, "end": v(38.12, -129.3) * mm});
            skFitSpline(sketch, "E626", {"points": [v(339.75, 112.17) * mm, v(339.84, 112.02) * mm, v(340, 111.92) * mm, v(340.18, 111.92) * mm]});
            skFitSpline(sketch, "E627", {"points": [v(339.75, 112.17) * mm, v(339.65, 112.35) * mm, v(339.44, 112.45) * mm, v(339.23, 112.42) * mm]});
            skFitSpline(sketch, "E628", {"points": [v(339.23, 112.42) * mm, v(339.02, 112.38) * mm, v(338.86, 112.22) * mm, v(338.82, 112) * mm]});
            skFitSpline(sketch, "E629", {"points": [v(338.82, 112) * mm, v(338.79, 111.8) * mm, v(338.89, 111.6) * mm, v(339.07, 111.49) * mm]});
            skFitSpline(sketch, "E630", {"points": [v(339.32, 111.06) * mm, v(339.32, 111.24) * mm, v(339.22, 111.4) * mm, v(339.07, 111.49) * mm]});
            skLineSegment(sketch, "E631", {"start": v(340.18, 108.62) * mm, "end": v(344.65, 108.62) * mm});
            skFitSpline(sketch, "E632", {"points": [v(317.87, 109.06) * mm, v(318.02, 109.15) * mm, v(318.12, 109.31) * mm, v(318.12, 109.49) * mm]});
            skFitSpline(sketch, "E633", {"points": [v(317.87, 109.06) * mm, v(317.69, 108.95) * mm, v(317.59, 108.74) * mm, v(317.62, 108.54) * mm]});
            skFitSpline(sketch, "E634", {"points": [v(317.62, 108.54) * mm, v(317.66, 108.33) * mm, v(317.82, 108.17) * mm, v(318.03, 108.13) * mm]});
            skFitSpline(sketch, "E635", {"points": [v(318.03, 108.13) * mm, v(318.24, 108.1) * mm, v(318.45, 108.2) * mm, v(318.55, 108.37) * mm]});
            skFitSpline(sketch, "E636", {"points": [v(318.98, 108.62) * mm, v(318.8, 108.62) * mm, v(318.64, 108.53) * mm, v(318.55, 108.37) * mm]});
            skLineSegment(sketch, "E637", {"start": v(345.52, 109.49) * mm, "end": v(345.52, 111.06) * mm});
            skFitSpline(sketch, "E638", {"points": [v(323.88, 108.37) * mm, v(323.8, 108.53) * mm, v(323.63, 108.62) * mm, v(323.45, 108.62) * mm]});
            skFitSpline(sketch, "E639", {"points": [v(323.88, 108.37) * mm, v(323.99, 108.2) * mm, v(324.2, 108.1) * mm, v(324.4, 108.13) * mm]});
            skFitSpline(sketch, "E640", {"points": [v(324.4, 108.13) * mm, v(324.61, 108.17) * mm, v(324.77, 108.33) * mm, v(324.8, 108.54) * mm]});
            skFitSpline(sketch, "E641", {"points": [v(324.8, 108.54) * mm, v(324.85, 108.74) * mm, v(324.75, 108.95) * mm, v(324.57, 109.06) * mm]});
            skFitSpline(sketch, "E642", {"points": [v(324.32, 109.49) * mm, v(324.32, 109.31) * mm, v(324.41, 109.15) * mm, v(324.57, 109.06) * mm]});
            skLineSegment(sketch, "E643", {"start": v(344.65, 111.92) * mm, "end": v(340.18, 111.92) * mm});
            skFitSpline(sketch, "E644", {"points": [v(324.57, 111.49) * mm, v(324.41, 111.4) * mm, v(324.32, 111.24) * mm, v(324.32, 111.06) * mm]});
            skFitSpline(sketch, "E645", {"points": [v(324.57, 111.49) * mm, v(324.75, 111.6) * mm, v(324.85, 111.8) * mm, v(324.8, 112) * mm]});
            skFitSpline(sketch, "E646", {"points": [v(324.8, 112) * mm, v(324.77, 112.22) * mm, v(324.61, 112.38) * mm, v(324.4, 112.42) * mm]});
            skFitSpline(sketch, "E647", {"points": [v(324.4, 112.42) * mm, v(324.2, 112.45) * mm, v(323.99, 112.35) * mm, v(323.88, 112.17) * mm]});
            skFitSpline(sketch, "E648", {"points": [v(323.45, 111.92) * mm, v(323.63, 111.92) * mm, v(323.8, 112.02) * mm, v(323.88, 112.17) * mm]});
            skLineSegment(sketch, "E649", {"start": v(339.32, 111.06) * mm, "end": v(339.32, 109.49) * mm});
            skFitSpline(sketch, "E650", {"points": [v(318.55, 112.17) * mm, v(318.64, 112.02) * mm, v(318.8, 111.92) * mm, v(318.98, 111.92) * mm]});
            skFitSpline(sketch, "E651", {"points": [v(318.55, 112.17) * mm, v(318.45, 112.35) * mm, v(318.24, 112.45) * mm, v(318.03, 112.42) * mm]});
            skFitSpline(sketch, "E652", {"points": [v(318.03, 112.42) * mm, v(317.82, 112.38) * mm, v(317.66, 112.22) * mm, v(317.62, 112) * mm]});
            skFitSpline(sketch, "E653", {"points": [v(317.62, 112) * mm, v(317.59, 111.8) * mm, v(317.69, 111.6) * mm, v(317.87, 111.49) * mm]});
            skFitSpline(sketch, "E654", {"points": [v(318.12, 111.06) * mm, v(318.12, 111.24) * mm, v(318.02, 111.4) * mm, v(317.87, 111.49) * mm]});
            skLineSegment(sketch, "E655", {"start": v(318.98, 108.62) * mm, "end": v(323.45, 108.62) * mm});
            skFitSpline(sketch, "E656", {"points": [v(219.32, 111.06) * mm, v(219.32, 111.24) * mm, v(219.22, 111.4) * mm, v(219.07, 111.49) * mm]});
            skFitSpline(sketch, "E657", {"points": [v(219.75, 112.17) * mm, v(219.65, 112.35) * mm, v(219.44, 112.45) * mm, v(219.23, 112.42) * mm]});
            skFitSpline(sketch, "E658", {"points": [v(219.23, 112.42) * mm, v(219.02, 112.38) * mm, v(218.86, 112.22) * mm, v(218.82, 112) * mm]});
            skFitSpline(sketch, "E659", {"points": [v(218.82, 112) * mm, v(218.79, 111.8) * mm, v(218.89, 111.6) * mm, v(219.07, 111.49) * mm]});
            skFitSpline(sketch, "E660", {"points": [v(219.75, 112.17) * mm, v(219.84, 112.02) * mm, v(220, 111.92) * mm, v(220.18, 111.92) * mm]});
            skLineSegment(sketch, "E661", {"start": v(324.32, 109.49) * mm, "end": v(324.32, 111.06) * mm});
            skFitSpline(sketch, "E662", {"points": [v(224.65, 111.92) * mm, v(224.83, 111.92) * mm, v(225, 112.02) * mm, v(225.08, 112.17) * mm]});
            skFitSpline(sketch, "E663", {"points": [v(225.77, 111.49) * mm, v(225.95, 111.6) * mm, v(226.05, 111.8) * mm, v(226, 112) * mm]});
            skFitSpline(sketch, "E664", {"points": [v(226, 112) * mm, v(225.97, 112.22) * mm, v(225.81, 112.38) * mm, v(225.6, 112.42) * mm]});
            skFitSpline(sketch, "E665", {"points": [v(225.6, 112.42) * mm, v(225.4, 112.45) * mm, v(225.19, 112.35) * mm, v(225.08, 112.17) * mm]});
            skFitSpline(sketch, "E666", {"points": [v(225.77, 111.49) * mm, v(225.61, 111.4) * mm, v(225.52, 111.24) * mm, v(225.52, 111.06) * mm]});
            skLineSegment(sketch, "E667", {"start": v(323.45, 111.92) * mm, "end": v(318.98, 111.92) * mm});
            skFitSpline(sketch, "E668", {"points": [v(225.52, 109.49) * mm, v(225.52, 109.31) * mm, v(225.61, 109.15) * mm, v(225.77, 109.06) * mm]});
            skFitSpline(sketch, "E669", {"points": [v(225.08, 108.37) * mm, v(225.19, 108.2) * mm, v(225.4, 108.1) * mm, v(225.6, 108.13) * mm]});
            skFitSpline(sketch, "E670", {"points": [v(225.6, 108.13) * mm, v(225.81, 108.17) * mm, v(225.97, 108.33) * mm, v(226, 108.54) * mm]});
            skFitSpline(sketch, "E671", {"points": [v(226, 108.54) * mm, v(226.05, 108.74) * mm, v(225.95, 108.95) * mm, v(225.77, 109.06) * mm]});
            skFitSpline(sketch, "E672", {"points": [v(225.08, 108.37) * mm, v(225, 108.53) * mm, v(224.83, 108.62) * mm, v(224.65, 108.62) * mm]});
            skLineSegment(sketch, "E673", {"start": v(318.12, 111.06) * mm, "end": v(318.12, 109.49) * mm});
            skFitSpline(sketch, "E674", {"points": [v(220.18, 108.62) * mm, v(220, 108.62) * mm, v(219.84, 108.53) * mm, v(219.75, 108.37) * mm]});
            skFitSpline(sketch, "E675", {"points": [v(219.07, 109.06) * mm, v(218.89, 108.95) * mm, v(218.79, 108.74) * mm, v(218.82, 108.54) * mm]});
            skFitSpline(sketch, "E676", {"points": [v(218.82, 108.54) * mm, v(218.86, 108.33) * mm, v(219.02, 108.17) * mm, v(219.23, 108.13) * mm]});
            skFitSpline(sketch, "E677", {"points": [v(219.23, 108.13) * mm, v(219.44, 108.1) * mm, v(219.65, 108.2) * mm, v(219.75, 108.37) * mm]});
            skFitSpline(sketch, "E678", {"points": [v(219.07, 109.06) * mm, v(219.22, 109.15) * mm, v(219.32, 109.31) * mm, v(219.32, 109.49) * mm]});
            skLineSegment(sketch, "E679", {"start": v(220.18, 111.92) * mm, "end": v(224.65, 111.92) * mm});
            skFitSpline(sketch, "E680", {"points": [v(198.12, 111.06) * mm, v(198.12, 111.24) * mm, v(198.02, 111.4) * mm, v(197.87, 111.49) * mm]});
            skFitSpline(sketch, "E681", {"points": [v(198.55, 112.17) * mm, v(198.45, 112.35) * mm, v(198.24, 112.45) * mm, v(198.03, 112.42) * mm]});
            skFitSpline(sketch, "E682", {"points": [v(198.03, 112.42) * mm, v(197.82, 112.38) * mm, v(197.66, 112.22) * mm, v(197.62, 112) * mm]});
            skFitSpline(sketch, "E683", {"points": [v(197.62, 112) * mm, v(197.59, 111.8) * mm, v(197.69, 111.6) * mm, v(197.87, 111.49) * mm]});
            skFitSpline(sketch, "E684", {"points": [v(198.55, 112.17) * mm, v(198.64, 112.02) * mm, v(198.8, 111.92) * mm, v(198.98, 111.92) * mm]});
            skLineSegment(sketch, "E685", {"start": v(225.52, 111.06) * mm, "end": v(225.52, 109.49) * mm});
            skFitSpline(sketch, "E686", {"points": [v(203.45, 111.92) * mm, v(203.63, 111.92) * mm, v(203.8, 112.02) * mm, v(203.88, 112.17) * mm]});
            skFitSpline(sketch, "E687", {"points": [v(204.57, 111.49) * mm, v(204.75, 111.6) * mm, v(204.85, 111.8) * mm, v(204.8, 112) * mm]});
            skFitSpline(sketch, "E688", {"points": [v(204.8, 112) * mm, v(204.77, 112.22) * mm, v(204.61, 112.38) * mm, v(204.4, 112.42) * mm]});
            skFitSpline(sketch, "E689", {"points": [v(204.4, 112.42) * mm, v(204.2, 112.45) * mm, v(203.99, 112.35) * mm, v(203.88, 112.17) * mm]});
            skFitSpline(sketch, "E690", {"points": [v(204.57, 111.49) * mm, v(204.41, 111.4) * mm, v(204.32, 111.24) * mm, v(204.32, 111.06) * mm]});
            skLineSegment(sketch, "E691", {"start": v(224.65, 108.62) * mm, "end": v(220.18, 108.62) * mm});
            skFitSpline(sketch, "E692", {"points": [v(204.32, 109.49) * mm, v(204.32, 109.31) * mm, v(204.41, 109.15) * mm, v(204.57, 109.06) * mm]});
            skFitSpline(sketch, "E693", {"points": [v(203.88, 108.37) * mm, v(203.99, 108.2) * mm, v(204.2, 108.1) * mm, v(204.4, 108.13) * mm]});
            skFitSpline(sketch, "E694", {"points": [v(204.4, 108.13) * mm, v(204.61, 108.17) * mm, v(204.77, 108.33) * mm, v(204.8, 108.54) * mm]});
            skFitSpline(sketch, "E695", {"points": [v(204.8, 108.54) * mm, v(204.85, 108.74) * mm, v(204.75, 108.95) * mm, v(204.57, 109.06) * mm]});
            skFitSpline(sketch, "E696", {"points": [v(203.88, 108.37) * mm, v(203.8, 108.53) * mm, v(203.63, 108.62) * mm, v(203.45, 108.62) * mm]});
            skLineSegment(sketch, "E697", {"start": v(219.32, 109.49) * mm, "end": v(219.32, 111.06) * mm});
            skFitSpline(sketch, "E698", {"points": [v(198.98, 108.62) * mm, v(198.8, 108.62) * mm, v(198.64, 108.53) * mm, v(198.55, 108.37) * mm]});
            skFitSpline(sketch, "E699", {"points": [v(197.87, 109.06) * mm, v(197.69, 108.95) * mm, v(197.59, 108.74) * mm, v(197.62, 108.54) * mm]});
            skFitSpline(sketch, "E700", {"points": [v(197.62, 108.54) * mm, v(197.66, 108.33) * mm, v(197.82, 108.17) * mm, v(198.03, 108.13) * mm]});
            skFitSpline(sketch, "E701", {"points": [v(198.03, 108.13) * mm, v(198.24, 108.1) * mm, v(198.45, 108.2) * mm, v(198.55, 108.37) * mm]});
            skFitSpline(sketch, "E702", {"points": [v(197.87, 109.06) * mm, v(198.02, 109.15) * mm, v(198.12, 109.31) * mm, v(198.12, 109.49) * mm]});
            skLineSegment(sketch, "E703", {"start": v(198.98, 111.92) * mm, "end": v(203.45, 111.92) * mm});
            skFitSpline(sketch, "E704", {"points": [v(59.32, 111.06) * mm, v(59.32, 111.24) * mm, v(59.22, 111.4) * mm, v(59.07, 111.49) * mm]});
            skFitSpline(sketch, "E705", {"points": [v(59.75, 112.17) * mm, v(59.65, 112.35) * mm, v(59.44, 112.45) * mm, v(59.23, 112.42) * mm]});
            skFitSpline(sketch, "E706", {"points": [v(59.23, 112.42) * mm, v(59.02, 112.38) * mm, v(58.86, 112.22) * mm, v(58.82, 112) * mm]});
            skFitSpline(sketch, "E707", {"points": [v(58.82, 112) * mm, v(58.79, 111.8) * mm, v(58.89, 111.6) * mm, v(59.07, 111.49) * mm]});
            skFitSpline(sketch, "E708", {"points": [v(59.75, 112.17) * mm, v(59.84, 112.02) * mm, v(60, 111.92) * mm, v(60.18, 111.92) * mm]});
            skLineSegment(sketch, "E709", {"start": v(204.32, 111.06) * mm, "end": v(204.32, 109.49) * mm});
            skFitSpline(sketch, "E710", {"points": [v(64.65, 111.92) * mm, v(64.83, 111.92) * mm, v(65, 112.02) * mm, v(65.08, 112.17) * mm]});
            skFitSpline(sketch, "E711", {"points": [v(65.77, 111.49) * mm, v(65.95, 111.6) * mm, v(66.05, 111.8) * mm, v(66, 112) * mm]});
            skFitSpline(sketch, "E712", {"points": [v(66, 112) * mm, v(65.97, 112.22) * mm, v(65.81, 112.38) * mm, v(65.6, 112.42) * mm]});
            skFitSpline(sketch, "E713", {"points": [v(65.6, 112.42) * mm, v(65.4, 112.45) * mm, v(65.19, 112.35) * mm, v(65.08, 112.17) * mm]});
            skFitSpline(sketch, "E714", {"points": [v(65.77, 111.49) * mm, v(65.61, 111.4) * mm, v(65.52, 111.24) * mm, v(65.52, 111.06) * mm]});
            skLineSegment(sketch, "E715", {"start": v(203.45, 108.62) * mm, "end": v(198.98, 108.62) * mm});
            skFitSpline(sketch, "E716", {"points": [v(65.52, 109.49) * mm, v(65.52, 109.31) * mm, v(65.61, 109.15) * mm, v(65.77, 109.06) * mm]});
            skFitSpline(sketch, "E717", {"points": [v(65.08, 108.37) * mm, v(65.19, 108.2) * mm, v(65.4, 108.1) * mm, v(65.6, 108.13) * mm]});
            skFitSpline(sketch, "E718", {"points": [v(65.6, 108.13) * mm, v(65.81, 108.17) * mm, v(65.97, 108.33) * mm, v(66, 108.54) * mm]});
            skFitSpline(sketch, "E719", {"points": [v(66, 108.54) * mm, v(66.05, 108.74) * mm, v(65.95, 108.95) * mm, v(65.77, 109.06) * mm]});
            skFitSpline(sketch, "E720", {"points": [v(65.08, 108.37) * mm, v(65, 108.53) * mm, v(64.83, 108.62) * mm, v(64.65, 108.62) * mm]});
            skLineSegment(sketch, "E721", {"start": v(198.12, 109.49) * mm, "end": v(198.12, 111.06) * mm});
            skFitSpline(sketch, "E722", {"points": [v(60.18, 108.62) * mm, v(60, 108.62) * mm, v(59.84, 108.53) * mm, v(59.75, 108.37) * mm]});
            skFitSpline(sketch, "E723", {"points": [v(59.07, 109.06) * mm, v(58.89, 108.95) * mm, v(58.79, 108.74) * mm, v(58.82, 108.54) * mm]});
            skFitSpline(sketch, "E724", {"points": [v(58.82, 108.54) * mm, v(58.86, 108.33) * mm, v(59.02, 108.17) * mm, v(59.23, 108.13) * mm]});
            skFitSpline(sketch, "E725", {"points": [v(59.23, 108.13) * mm, v(59.44, 108.1) * mm, v(59.65, 108.2) * mm, v(59.75, 108.37) * mm]});
            skFitSpline(sketch, "E726", {"points": [v(59.07, 109.06) * mm, v(59.22, 109.15) * mm, v(59.32, 109.31) * mm, v(59.32, 109.49) * mm]});
            skLineSegment(sketch, "E727", {"start": v(60.18, 111.92) * mm, "end": v(64.65, 111.92) * mm});
            skFitSpline(sketch, "E728", {"points": [v(38.12, 111.06) * mm, v(38.12, 111.24) * mm, v(38.02, 111.4) * mm, v(37.87, 111.49) * mm]});
            skFitSpline(sketch, "E729", {"points": [v(38.55, 112.17) * mm, v(38.45, 112.35) * mm, v(38.24, 112.45) * mm, v(38.03, 112.42) * mm]});
            skFitSpline(sketch, "E730", {"points": [v(38.03, 112.42) * mm, v(37.82, 112.38) * mm, v(37.66, 112.22) * mm, v(37.62, 112) * mm]});
            skFitSpline(sketch, "E731", {"points": [v(37.62, 112) * mm, v(37.59, 111.8) * mm, v(37.69, 111.6) * mm, v(37.87, 111.49) * mm]});
            skFitSpline(sketch, "E732", {"points": [v(38.55, 112.17) * mm, v(38.64, 112.02) * mm, v(38.8, 111.92) * mm, v(38.98, 111.92) * mm]});
            skLineSegment(sketch, "E733", {"start": v(65.52, 111.06) * mm, "end": v(65.52, 109.49) * mm});
            skFitSpline(sketch, "E734", {"points": [v(43.45, 111.92) * mm, v(43.63, 111.92) * mm, v(43.8, 112.02) * mm, v(43.88, 112.17) * mm]});
            skFitSpline(sketch, "E735", {"points": [v(44.57, 111.49) * mm, v(44.75, 111.6) * mm, v(44.85, 111.8) * mm, v(44.8, 112) * mm]});
            skFitSpline(sketch, "E736", {"points": [v(44.8, 112) * mm, v(44.77, 112.22) * mm, v(44.61, 112.38) * mm, v(44.4, 112.42) * mm]});
            skFitSpline(sketch, "E737", {"points": [v(44.4, 112.42) * mm, v(44.2, 112.45) * mm, v(43.99, 112.35) * mm, v(43.88, 112.17) * mm]});
            skFitSpline(sketch, "E738", {"points": [v(44.57, 111.49) * mm, v(44.41, 111.4) * mm, v(44.32, 111.24) * mm, v(44.32, 111.06) * mm]});
            skLineSegment(sketch, "E739", {"start": v(64.65, 108.62) * mm, "end": v(60.18, 108.62) * mm});
            skFitSpline(sketch, "E740", {"points": [v(44.32, 109.49) * mm, v(44.32, 109.31) * mm, v(44.41, 109.15) * mm, v(44.57, 109.06) * mm]});
            skFitSpline(sketch, "E741", {"points": [v(43.88, 108.37) * mm, v(43.99, 108.2) * mm, v(44.2, 108.1) * mm, v(44.4, 108.13) * mm]});
            skFitSpline(sketch, "E742", {"points": [v(44.4, 108.13) * mm, v(44.61, 108.17) * mm, v(44.77, 108.33) * mm, v(44.8, 108.54) * mm]});
            skFitSpline(sketch, "E743", {"points": [v(44.8, 108.54) * mm, v(44.85, 108.74) * mm, v(44.75, 108.95) * mm, v(44.57, 109.06) * mm]});
            skFitSpline(sketch, "E744", {"points": [v(43.88, 108.37) * mm, v(43.8, 108.53) * mm, v(43.63, 108.62) * mm, v(43.45, 108.62) * mm]});
            skLineSegment(sketch, "E745", {"start": v(59.32, 109.49) * mm, "end": v(59.32, 111.06) * mm});
            skFitSpline(sketch, "E746", {"points": [v(38.98, 108.62) * mm, v(38.8, 108.62) * mm, v(38.64, 108.53) * mm, v(38.55, 108.37) * mm]});
            skFitSpline(sketch, "E747", {"points": [v(37.87, 109.06) * mm, v(37.69, 108.95) * mm, v(37.59, 108.74) * mm, v(37.62, 108.54) * mm]});
            skFitSpline(sketch, "E748", {"points": [v(37.62, 108.54) * mm, v(37.66, 108.33) * mm, v(37.82, 108.17) * mm, v(38.03, 108.13) * mm]});
            skFitSpline(sketch, "E749", {"points": [v(38.03, 108.13) * mm, v(38.24, 108.1) * mm, v(38.45, 108.2) * mm, v(38.55, 108.37) * mm]});
            skFitSpline(sketch, "E750", {"points": [v(37.87, 109.06) * mm, v(38.02, 109.15) * mm, v(38.12, 109.31) * mm, v(38.12, 109.49) * mm]});
            skLineSegment(sketch, "E751", {"start": v(38.98, 111.92) * mm, "end": v(43.45, 111.92) * mm});
            skFitSpline(sketch, "E752", {"points": [v(379.07, 129.66) * mm, v(379.22, 129.75) * mm, v(379.32, 129.92) * mm, v(379.32, 130.1) * mm]});
            skFitSpline(sketch, "E753", {"points": [v(379.07, 129.66) * mm, v(378.89, 129.56) * mm, v(378.79, 129.35) * mm, v(378.82, 129.14) * mm]});
            skFitSpline(sketch, "E754", {"points": [v(378.82, 129.14) * mm, v(378.86, 128.93) * mm, v(379.02, 128.77) * mm, v(379.23, 128.74) * mm]});
            skFitSpline(sketch, "E755", {"points": [v(379.23, 128.74) * mm, v(379.44, 128.7) * mm, v(379.65, 128.8) * mm, v(379.75, 128.98) * mm]});
            skFitSpline(sketch, "E756", {"points": [v(380.18, 129.23) * mm, v(380, 129.23) * mm, v(379.84, 129.13) * mm, v(379.75, 128.98) * mm]});
            skLineSegment(sketch, "E757", {"start": v(44.32, 111.06) * mm, "end": v(44.32, 109.49) * mm});
            skFitSpline(sketch, "E758", {"points": [v(385.08, 128.98) * mm, v(385, 129.13) * mm, v(384.83, 129.23) * mm, v(384.65, 129.23) * mm]});
            skFitSpline(sketch, "E759", {"points": [v(385.08, 128.98) * mm, v(385.19, 128.8) * mm, v(385.4, 128.7) * mm, v(385.6, 128.74) * mm]});
            skFitSpline(sketch, "E760", {"points": [v(385.6, 128.74) * mm, v(385.81, 128.77) * mm, v(385.97, 128.93) * mm, v(386, 129.14) * mm]});
            skFitSpline(sketch, "E761", {"points": [v(386, 129.14) * mm, v(386.05, 129.35) * mm, v(385.95, 129.56) * mm, v(385.77, 129.66) * mm]});
            skFitSpline(sketch, "E762", {"points": [v(385.52, 130.1) * mm, v(385.52, 129.92) * mm, v(385.61, 129.75) * mm, v(385.77, 129.66) * mm]});
            skLineSegment(sketch, "E763", {"start": v(43.45, 108.62) * mm, "end": v(38.98, 108.62) * mm});
            skFitSpline(sketch, "E764", {"points": [v(385.77, 132.1) * mm, v(385.61, 132) * mm, v(385.52, 131.84) * mm, v(385.52, 131.66) * mm]});
            skFitSpline(sketch, "E765", {"points": [v(385.77, 132.1) * mm, v(385.95, 132.2) * mm, v(386.05, 132.4) * mm, v(386, 132.61) * mm]});
            skFitSpline(sketch, "E766", {"points": [v(386, 132.61) * mm, v(385.97, 132.82) * mm, v(385.81, 132.98) * mm, v(385.6, 133.02) * mm]});
            skFitSpline(sketch, "E767", {"points": [v(385.6, 133.02) * mm, v(385.4, 133.06) * mm, v(385.19, 132.96) * mm, v(385.08, 132.78) * mm]});
            skFitSpline(sketch, "E768", {"points": [v(384.65, 132.53) * mm, v(384.83, 132.53) * mm, v(385, 132.62) * mm, v(385.08, 132.78) * mm]});
            skLineSegment(sketch, "E769", {"start": v(38.12, 109.49) * mm, "end": v(38.12, 111.06) * mm});
            skFitSpline(sketch, "E770", {"points": [v(379.75, 132.78) * mm, v(379.84, 132.62) * mm, v(380, 132.53) * mm, v(380.18, 132.53) * mm]});
            skFitSpline(sketch, "E771", {"points": [v(379.75, 132.78) * mm, v(379.65, 132.96) * mm, v(379.44, 133.06) * mm, v(379.23, 133.02) * mm]});
            skFitSpline(sketch, "E772", {"points": [v(379.23, 133.02) * mm, v(379.02, 132.98) * mm, v(378.86, 132.82) * mm, v(378.82, 132.61) * mm]});
            skFitSpline(sketch, "E773", {"points": [v(378.82, 132.61) * mm, v(378.79, 132.4) * mm, v(378.89, 132.2) * mm, v(379.07, 132.1) * mm]});
            skFitSpline(sketch, "E774", {"points": [v(379.32, 131.66) * mm, v(379.32, 131.84) * mm, v(379.22, 132) * mm, v(379.07, 132.1) * mm]});
            skLineSegment(sketch, "E775", {"start": v(380.18, 129.23) * mm, "end": v(384.65, 129.23) * mm});
            skFitSpline(sketch, "E776", {"points": [v(357.87, 129.66) * mm, v(358.02, 129.75) * mm, v(358.12, 129.92) * mm, v(358.12, 130.1) * mm]});
            skFitSpline(sketch, "E777", {"points": [v(357.87, 129.66) * mm, v(357.69, 129.56) * mm, v(357.59, 129.35) * mm, v(357.62, 129.14) * mm]});
            skFitSpline(sketch, "E778", {"points": [v(357.62, 129.14) * mm, v(357.66, 128.93) * mm, v(357.82, 128.77) * mm, v(358.03, 128.74) * mm]});
            skFitSpline(sketch, "E779", {"points": [v(358.03, 128.74) * mm, v(358.24, 128.7) * mm, v(358.45, 128.8) * mm, v(358.55, 128.98) * mm]});
            skFitSpline(sketch, "E780", {"points": [v(358.98, 129.23) * mm, v(358.8, 129.23) * mm, v(358.64, 129.13) * mm, v(358.55, 128.98) * mm]});
            skLineSegment(sketch, "E781", {"start": v(385.52, 130.1) * mm, "end": v(385.52, 131.66) * mm});
            skFitSpline(sketch, "E782", {"points": [v(363.88, 128.98) * mm, v(363.8, 129.13) * mm, v(363.63, 129.23) * mm, v(363.45, 129.23) * mm]});
            skFitSpline(sketch, "E783", {"points": [v(363.88, 128.98) * mm, v(363.99, 128.8) * mm, v(364.2, 128.7) * mm, v(364.4, 128.74) * mm]});
            skFitSpline(sketch, "E784", {"points": [v(364.4, 128.74) * mm, v(364.61, 128.77) * mm, v(364.77, 128.93) * mm, v(364.8, 129.14) * mm]});
            skFitSpline(sketch, "E785", {"points": [v(364.8, 129.14) * mm, v(364.85, 129.35) * mm, v(364.75, 129.56) * mm, v(364.57, 129.66) * mm]});
            skFitSpline(sketch, "E786", {"points": [v(364.32, 130.1) * mm, v(364.32, 129.92) * mm, v(364.41, 129.75) * mm, v(364.57, 129.66) * mm]});
            skLineSegment(sketch, "E787", {"start": v(384.65, 132.53) * mm, "end": v(380.18, 132.53) * mm});
            skFitSpline(sketch, "E788", {"points": [v(364.57, 132.1) * mm, v(364.41, 132) * mm, v(364.32, 131.84) * mm, v(364.32, 131.66) * mm]});
            skFitSpline(sketch, "E789", {"points": [v(364.57, 132.1) * mm, v(364.75, 132.2) * mm, v(364.85, 132.4) * mm, v(364.8, 132.61) * mm]});
            skFitSpline(sketch, "E790", {"points": [v(364.8, 132.61) * mm, v(364.77, 132.82) * mm, v(364.61, 132.98) * mm, v(364.4, 133.02) * mm]});
            skFitSpline(sketch, "E791", {"points": [v(364.4, 133.02) * mm, v(364.2, 133.06) * mm, v(363.99, 132.96) * mm, v(363.88, 132.78) * mm]});
            skFitSpline(sketch, "E792", {"points": [v(363.45, 132.53) * mm, v(363.63, 132.53) * mm, v(363.8, 132.62) * mm, v(363.88, 132.78) * mm]});
            skLineSegment(sketch, "E793", {"start": v(379.32, 131.66) * mm, "end": v(379.32, 130.1) * mm});
            skFitSpline(sketch, "E794", {"points": [v(358.55, 132.78) * mm, v(358.64, 132.62) * mm, v(358.8, 132.53) * mm, v(358.98, 132.53) * mm]});
            skFitSpline(sketch, "E795", {"points": [v(358.55, 132.78) * mm, v(358.45, 132.96) * mm, v(358.24, 133.06) * mm, v(358.03, 133.02) * mm]});
            skFitSpline(sketch, "E796", {"points": [v(358.03, 133.02) * mm, v(357.82, 132.98) * mm, v(357.66, 132.82) * mm, v(357.62, 132.61) * mm]});
            skFitSpline(sketch, "E797", {"points": [v(357.62, 132.61) * mm, v(357.59, 132.4) * mm, v(357.69, 132.2) * mm, v(357.87, 132.1) * mm]});
            skFitSpline(sketch, "E798", {"points": [v(358.12, 131.66) * mm, v(358.12, 131.84) * mm, v(358.02, 132) * mm, v(357.87, 132.1) * mm]});
            skLineSegment(sketch, "E799", {"start": v(358.98, 129.23) * mm, "end": v(363.45, 129.23) * mm});
            skFitSpline(sketch, "E800", {"points": [v(343.96, 148.15) * mm, v(344.04, 148) * mm, v(344.2, 147.9) * mm, v(344.39, 147.9) * mm]});
            skFitSpline(sketch, "E801", {"points": [v(343.96, 148.15) * mm, v(343.85, 148.33) * mm, v(343.64, 148.43) * mm, v(343.44, 148.4) * mm]});
            skFitSpline(sketch, "E802", {"points": [v(343.44, 148.4) * mm, v(343.23, 148.35) * mm, v(343.07, 148.2) * mm, v(343.03, 147.98) * mm]});
            skFitSpline(sketch, "E803", {"points": [v(343.03, 147.98) * mm, v(343, 147.78) * mm, v(343.1, 147.57) * mm, v(343.27, 147.46) * mm]});
            skFitSpline(sketch, "E804", {"points": [v(343.52, 147.03) * mm, v(343.52, 147.21) * mm, v(343.43, 147.38) * mm, v(343.27, 147.46) * mm]});
            skLineSegment(sketch, "E805", {"start": v(364.32, 130.1) * mm, "end": v(364.32, 131.66) * mm});
            skFitSpline(sketch, "E806", {"points": [v(343.27, 142.13) * mm, v(343.43, 142.22) * mm, v(343.52, 142.39) * mm, v(343.52, 142.56) * mm]});
            skFitSpline(sketch, "E807", {"points": [v(343.27, 142.13) * mm, v(343.1, 142.03) * mm, v(343, 141.82) * mm, v(343.03, 141.61) * mm]});
            skFitSpline(sketch, "E808", {"points": [v(343.03, 141.61) * mm, v(343.07, 141.4) * mm, v(343.23, 141.24) * mm, v(343.44, 141.2) * mm]});
            skFitSpline(sketch, "E809", {"points": [v(343.44, 141.2) * mm, v(343.64, 141.17) * mm, v(343.85, 141.27) * mm, v(343.96, 141.45) * mm]});
            skFitSpline(sketch, "E810", {"points": [v(344.39, 141.7) * mm, v(344.2, 141.7) * mm, v(344.04, 141.6) * mm, v(343.96, 141.45) * mm]});
            skLineSegment(sketch, "E811", {"start": v(363.45, 132.53) * mm, "end": v(358.98, 132.53) * mm});
            skFitSpline(sketch, "E812", {"points": [v(346.39, 141.45) * mm, v(346.3, 141.6) * mm, v(346.13, 141.7) * mm, v(345.96, 141.7) * mm]});
            skFitSpline(sketch, "E813", {"points": [v(346.39, 141.45) * mm, v(346.5, 141.27) * mm, v(346.7, 141.17) * mm, v(346.9, 141.2) * mm]});
            skFitSpline(sketch, "E814", {"points": [v(346.9, 141.2) * mm, v(347.12, 141.24) * mm, v(347.28, 141.4) * mm, v(347.31, 141.61) * mm]});
            skFitSpline(sketch, "E815", {"points": [v(347.31, 141.61) * mm, v(347.35, 141.82) * mm, v(347.25, 142.03) * mm, v(347.07, 142.13) * mm]});
            skFitSpline(sketch, "E816", {"points": [v(346.82, 142.56) * mm, v(346.82, 142.39) * mm, v(346.92, 142.22) * mm, v(347.07, 142.13) * mm]});
            skLineSegment(sketch, "E817", {"start": v(358.12, 131.66) * mm, "end": v(358.12, 130.1) * mm});
            skFitSpline(sketch, "E818", {"points": [v(347.07, 147.46) * mm, v(346.92, 147.38) * mm, v(346.82, 147.21) * mm, v(346.82, 147.03) * mm]});
            skFitSpline(sketch, "E819", {"points": [v(347.07, 147.46) * mm, v(347.25, 147.57) * mm, v(347.35, 147.78) * mm, v(347.31, 147.98) * mm]});
            skFitSpline(sketch, "E820", {"points": [v(347.31, 147.98) * mm, v(347.28, 148.2) * mm, v(347.12, 148.35) * mm, v(346.9, 148.4) * mm]});
            skFitSpline(sketch, "E821", {"points": [v(346.9, 148.4) * mm, v(346.7, 148.43) * mm, v(346.5, 148.33) * mm, v(346.39, 148.15) * mm]});
            skFitSpline(sketch, "E822", {"points": [v(345.96, 147.9) * mm, v(346.13, 147.9) * mm, v(346.3, 148) * mm, v(346.39, 148.15) * mm]});
            skLineSegment(sketch, "E823", {"start": v(343.52, 147.03) * mm, "end": v(343.52, 142.56) * mm});
            skFitSpline(sketch, "E824", {"points": [v(343.96, 169.35) * mm, v(344.04, 169.2) * mm, v(344.2, 169.1) * mm, v(344.39, 169.1) * mm]});
            skFitSpline(sketch, "E825", {"points": [v(343.96, 169.35) * mm, v(343.85, 169.53) * mm, v(343.64, 169.63) * mm, v(343.44, 169.6) * mm]});
            skFitSpline(sketch, "E826", {"points": [v(343.44, 169.6) * mm, v(343.23, 169.55) * mm, v(343.07, 169.4) * mm, v(343.03, 169.18) * mm]});
            skFitSpline(sketch, "E827", {"points": [v(343.03, 169.18) * mm, v(343, 168.98) * mm, v(343.1, 168.77) * mm, v(343.27, 168.66) * mm]});
            skFitSpline(sketch, "E828", {"points": [v(343.52, 168.23) * mm, v(343.52, 168.41) * mm, v(343.43, 168.58) * mm, v(343.27, 168.66) * mm]});
            skLineSegment(sketch, "E829", {"start": v(344.39, 141.7) * mm, "end": v(345.96, 141.7) * mm});
            skFitSpline(sketch, "E830", {"points": [v(343.27, 163.33) * mm, v(343.43, 163.42) * mm, v(343.52, 163.59) * mm, v(343.52, 163.76) * mm]});
            skFitSpline(sketch, "E831", {"points": [v(343.27, 163.33) * mm, v(343.1, 163.23) * mm, v(343, 163.02) * mm, v(343.03, 162.81) * mm]});
            skFitSpline(sketch, "E832", {"points": [v(343.03, 162.81) * mm, v(343.07, 162.6) * mm, v(343.23, 162.44) * mm, v(343.44, 162.4) * mm]});
            skFitSpline(sketch, "E833", {"points": [v(343.44, 162.4) * mm, v(343.64, 162.37) * mm, v(343.85, 162.47) * mm, v(343.96, 162.65) * mm]});
            skFitSpline(sketch, "E834", {"points": [v(344.39, 162.9) * mm, v(344.2, 162.9) * mm, v(344.04, 162.8) * mm, v(343.96, 162.65) * mm]});
            skLineSegment(sketch, "E835", {"start": v(346.82, 142.56) * mm, "end": v(346.82, 147.03) * mm});
            skFitSpline(sketch, "E836", {"points": [v(346.39, 162.65) * mm, v(346.3, 162.8) * mm, v(346.13, 162.9) * mm, v(345.96, 162.9) * mm]});
            skFitSpline(sketch, "E837", {"points": [v(346.39, 162.65) * mm, v(346.5, 162.47) * mm, v(346.7, 162.37) * mm, v(346.9, 162.4) * mm]});
            skFitSpline(sketch, "E838", {"points": [v(346.9, 162.4) * mm, v(347.12, 162.44) * mm, v(347.28, 162.6) * mm, v(347.31, 162.81) * mm]});
            skFitSpline(sketch, "E839", {"points": [v(347.31, 162.81) * mm, v(347.35, 163.02) * mm, v(347.25, 163.23) * mm, v(347.07, 163.33) * mm]});
            skFitSpline(sketch, "E840", {"points": [v(346.82, 163.76) * mm, v(346.82, 163.59) * mm, v(346.92, 163.42) * mm, v(347.07, 163.33) * mm]});
            skLineSegment(sketch, "E841", {"start": v(345.96, 147.9) * mm, "end": v(344.39, 147.9) * mm});
            skFitSpline(sketch, "E842", {"points": [v(347.07, 168.66) * mm, v(346.92, 168.58) * mm, v(346.82, 168.41) * mm, v(346.82, 168.23) * mm]});
            skFitSpline(sketch, "E843", {"points": [v(347.07, 168.66) * mm, v(347.25, 168.77) * mm, v(347.35, 168.98) * mm, v(347.31, 169.18) * mm]});
            skFitSpline(sketch, "E844", {"points": [v(347.31, 169.18) * mm, v(347.28, 169.4) * mm, v(347.12, 169.55) * mm, v(346.9, 169.6) * mm]});
            skFitSpline(sketch, "E845", {"points": [v(346.9, 169.6) * mm, v(346.7, 169.63) * mm, v(346.5, 169.53) * mm, v(346.39, 169.35) * mm]});
            skFitSpline(sketch, "E846", {"points": [v(345.96, 169.1) * mm, v(346.13, 169.1) * mm, v(346.3, 169.2) * mm, v(346.39, 169.35) * mm]});
            skLineSegment(sketch, "E847", {"start": v(343.52, 168.23) * mm, "end": v(343.52, 163.76) * mm});
            skFitSpline(sketch, "E848", {"points": [v(379.07, 178.7) * mm, v(379.22, 178.8) * mm, v(379.32, 178.96) * mm, v(379.32, 179.13) * mm]});
            skFitSpline(sketch, "E849", {"points": [v(379.07, 178.7) * mm, v(378.89, 178.6) * mm, v(378.79, 178.39) * mm, v(378.82, 178.18) * mm]});
            skFitSpline(sketch, "E850", {"points": [v(378.82, 178.18) * mm, v(378.86, 177.97) * mm, v(379.02, 177.81) * mm, v(379.23, 177.78) * mm]});
            skFitSpline(sketch, "E851", {"points": [v(379.23, 177.78) * mm, v(379.44, 177.74) * mm, v(379.65, 177.84) * mm, v(379.75, 178.02) * mm]});
            skFitSpline(sketch, "E852", {"points": [v(380.18, 178.27) * mm, v(380, 178.27) * mm, v(379.84, 178.17) * mm, v(379.75, 178.02) * mm]});
            skLineSegment(sketch, "E853", {"start": v(344.39, 162.9) * mm, "end": v(345.96, 162.9) * mm});
            skFitSpline(sketch, "E854", {"points": [v(385.08, 178.02) * mm, v(385, 178.17) * mm, v(384.83, 178.27) * mm, v(384.65, 178.27) * mm]});
            skFitSpline(sketch, "E855", {"points": [v(385.08, 178.02) * mm, v(385.19, 177.84) * mm, v(385.4, 177.74) * mm, v(385.6, 177.78) * mm]});
            skFitSpline(sketch, "E856", {"points": [v(385.6, 177.78) * mm, v(385.81, 177.81) * mm, v(385.97, 177.97) * mm, v(386, 178.18) * mm]});
            skFitSpline(sketch, "E857", {"points": [v(386, 178.18) * mm, v(386.05, 178.39) * mm, v(385.95, 178.6) * mm, v(385.77, 178.7) * mm]});
            skFitSpline(sketch, "E858", {"points": [v(385.52, 179.13) * mm, v(385.52, 178.96) * mm, v(385.61, 178.8) * mm, v(385.77, 178.7) * mm]});
            skLineSegment(sketch, "E859", {"start": v(346.82, 163.76) * mm, "end": v(346.82, 168.23) * mm});
            skFitSpline(sketch, "E860", {"points": [v(385.77, 181.13) * mm, v(385.61, 181.05) * mm, v(385.52, 180.88) * mm, v(385.52, 180.7) * mm]});
            skFitSpline(sketch, "E861", {"points": [v(385.77, 181.13) * mm, v(385.95, 181.24) * mm, v(386.05, 181.45) * mm, v(386, 181.65) * mm]});
            skFitSpline(sketch, "E862", {"points": [v(386, 181.65) * mm, v(385.97, 181.86) * mm, v(385.81, 182.02) * mm, v(385.6, 182.06) * mm]});
            skFitSpline(sketch, "E863", {"points": [v(385.6, 182.06) * mm, v(385.4, 182.1) * mm, v(385.19, 182) * mm, v(385.08, 181.82) * mm]});
            skFitSpline(sketch, "E864", {"points": [v(384.65, 181.57) * mm, v(384.83, 181.57) * mm, v(385, 181.66) * mm, v(385.08, 181.82) * mm]});
            skLineSegment(sketch, "E865", {"start": v(345.96, 169.1) * mm, "end": v(344.39, 169.1) * mm});
            skFitSpline(sketch, "E866", {"points": [v(379.75, 181.82) * mm, v(379.84, 181.66) * mm, v(380, 181.57) * mm, v(380.18, 181.57) * mm]});
            skFitSpline(sketch, "E867", {"points": [v(379.75, 181.82) * mm, v(379.65, 182) * mm, v(379.44, 182.1) * mm, v(379.23, 182.06) * mm]});
            skFitSpline(sketch, "E868", {"points": [v(379.23, 182.06) * mm, v(379.02, 182.02) * mm, v(378.86, 181.86) * mm, v(378.82, 181.65) * mm]});
            skFitSpline(sketch, "E869", {"points": [v(378.82, 181.65) * mm, v(378.79, 181.45) * mm, v(378.89, 181.24) * mm, v(379.07, 181.13) * mm]});
            skFitSpline(sketch, "E870", {"points": [v(379.32, 180.7) * mm, v(379.32, 180.88) * mm, v(379.22, 181.05) * mm, v(379.07, 181.13) * mm]});
            skLineSegment(sketch, "E871", {"start": v(380.18, 178.27) * mm, "end": v(384.65, 178.27) * mm});
            skFitSpline(sketch, "E872", {"points": [v(357.87, 178.7) * mm, v(358.02, 178.8) * mm, v(358.12, 178.96) * mm, v(358.12, 179.13) * mm]});
            skFitSpline(sketch, "E873", {"points": [v(357.87, 178.7) * mm, v(357.69, 178.6) * mm, v(357.59, 178.39) * mm, v(357.62, 178.18) * mm]});
            skFitSpline(sketch, "E874", {"points": [v(357.62, 178.18) * mm, v(357.66, 177.97) * mm, v(357.82, 177.81) * mm, v(358.03, 177.78) * mm]});
            skFitSpline(sketch, "E875", {"points": [v(358.03, 177.78) * mm, v(358.24, 177.74) * mm, v(358.45, 177.84) * mm, v(358.55, 178.02) * mm]});
            skFitSpline(sketch, "E876", {"points": [v(358.98, 178.27) * mm, v(358.8, 178.27) * mm, v(358.64, 178.17) * mm, v(358.55, 178.02) * mm]});
            skLineSegment(sketch, "E877", {"start": v(385.52, 179.13) * mm, "end": v(385.52, 180.7) * mm});
            skFitSpline(sketch, "E878", {"points": [v(363.88, 178.02) * mm, v(363.8, 178.17) * mm, v(363.63, 178.27) * mm, v(363.45, 178.27) * mm]});
            skFitSpline(sketch, "E879", {"points": [v(363.88, 178.02) * mm, v(363.99, 177.84) * mm, v(364.2, 177.74) * mm, v(364.4, 177.78) * mm]});
            skFitSpline(sketch, "E880", {"points": [v(364.4, 177.78) * mm, v(364.61, 177.81) * mm, v(364.77, 177.97) * mm, v(364.8, 178.18) * mm]});
            skFitSpline(sketch, "E881", {"points": [v(364.8, 178.18) * mm, v(364.85, 178.39) * mm, v(364.75, 178.6) * mm, v(364.57, 178.7) * mm]});
            skFitSpline(sketch, "E882", {"points": [v(364.32, 179.13) * mm, v(364.32, 178.96) * mm, v(364.41, 178.8) * mm, v(364.57, 178.7) * mm]});
            skLineSegment(sketch, "E883", {"start": v(384.65, 181.57) * mm, "end": v(380.18, 181.57) * mm});
            skFitSpline(sketch, "E884", {"points": [v(364.57, 181.13) * mm, v(364.41, 181.05) * mm, v(364.32, 180.88) * mm, v(364.32, 180.7) * mm]});
            skFitSpline(sketch, "E885", {"points": [v(364.57, 181.13) * mm, v(364.75, 181.24) * mm, v(364.85, 181.45) * mm, v(364.8, 181.65) * mm]});
            skFitSpline(sketch, "E886", {"points": [v(364.8, 181.65) * mm, v(364.77, 181.86) * mm, v(364.61, 182.02) * mm, v(364.4, 182.06) * mm]});
            skFitSpline(sketch, "E887", {"points": [v(364.4, 182.06) * mm, v(364.2, 182.1) * mm, v(363.99, 182) * mm, v(363.88, 181.82) * mm]});
            skFitSpline(sketch, "E888", {"points": [v(363.45, 181.57) * mm, v(363.63, 181.57) * mm, v(363.8, 181.66) * mm, v(363.88, 181.82) * mm]});
            skLineSegment(sketch, "E889", {"start": v(379.32, 180.7) * mm, "end": v(379.32, 179.13) * mm});
            skFitSpline(sketch, "E890", {"points": [v(358.55, 181.82) * mm, v(358.64, 181.66) * mm, v(358.8, 181.57) * mm, v(358.98, 181.57) * mm]});
            skFitSpline(sketch, "E891", {"points": [v(358.55, 181.82) * mm, v(358.45, 182) * mm, v(358.24, 182.1) * mm, v(358.03, 182.06) * mm]});
            skFitSpline(sketch, "E892", {"points": [v(358.03, 182.06) * mm, v(357.82, 182.02) * mm, v(357.66, 181.86) * mm, v(357.62, 181.65) * mm]});
            skFitSpline(sketch, "E893", {"points": [v(357.62, 181.65) * mm, v(357.59, 181.45) * mm, v(357.69, 181.24) * mm, v(357.87, 181.13) * mm]});
            skFitSpline(sketch, "E894", {"points": [v(358.12, 180.7) * mm, v(358.12, 180.88) * mm, v(358.02, 181.05) * mm, v(357.87, 181.13) * mm]});
            skLineSegment(sketch, "E895", {"start": v(358.98, 178.27) * mm, "end": v(363.45, 178.27) * mm});
            skFitSpline(sketch, "E896", {"points": [v(373.42, -199.72) * mm, v(373.42, -199.15) * mm, v(373.11, -198.62) * mm, v(372.62, -198.34) * mm]});
            skFitSpline(sketch, "E897", {"points": [v(372.62, -198.34) * mm, v(372.12, -198.05) * mm, v(371.51, -198.05) * mm, v(371.02, -198.34) * mm]});
            skFitSpline(sketch, "E898", {"points": [v(371.02, -198.34) * mm, v(370.52, -198.62) * mm, v(370.22, -199.15) * mm, v(370.22, -199.72) * mm]});
            skFitSpline(sketch, "E899", {"points": [v(370.22, -199.72) * mm, v(370.22, -200.3) * mm, v(370.52, -200.82) * mm, v(371.02, -201.1) * mm]});
            skFitSpline(sketch, "E900", {"points": [v(371.02, -201.1) * mm, v(371.51, -201.4) * mm, v(372.12, -201.4) * mm, v(372.62, -201.1) * mm]});
            skFitSpline(sketch, "E901", {"points": [v(372.62, -201.1) * mm, v(373.11, -200.82) * mm, v(373.42, -200.3) * mm, v(373.42, -199.72) * mm]});
            skLineSegment(sketch, "E902", {"start": v(364.32, 179.13) * mm, "end": v(364.32, 180.7) * mm});
            skFitSpline(sketch, "E903", {"points": [v(346.77, -175.2) * mm, v(346.77, -174.63) * mm, v(346.47, -174.1) * mm, v(345.97, -173.82) * mm]});
            skFitSpline(sketch, "E904", {"points": [v(345.97, -173.82) * mm, v(345.48, -173.53) * mm, v(344.87, -173.53) * mm, v(344.37, -173.82) * mm]});
            skFitSpline(sketch, "E905", {"points": [v(344.37, -173.82) * mm, v(343.88, -174.1) * mm, v(343.57, -174.63) * mm, v(343.57, -175.2) * mm]});
            skFitSpline(sketch, "E906", {"points": [v(343.57, -175.2) * mm, v(343.57, -175.77) * mm, v(343.88, -176.3) * mm, v(344.37, -176.59) * mm]});
            skFitSpline(sketch, "E907", {"points": [v(344.37, -176.59) * mm, v(344.87, -176.87) * mm, v(345.48, -176.87) * mm, v(345.97, -176.59) * mm]});
            skFitSpline(sketch, "E908", {"points": [v(345.97, -176.59) * mm, v(346.47, -176.3) * mm, v(346.77, -175.77) * mm, v(346.77, -175.2) * mm]});
            skLineSegment(sketch, "E909", {"start": v(363.45, 181.57) * mm, "end": v(358.98, 181.57) * mm});
            skFitSpline(sketch, "E910", {"points": [v(373.42, -150.68) * mm, v(373.42, -150.11) * mm, v(373.11, -149.58) * mm, v(372.62, -149.3) * mm]});
            skFitSpline(sketch, "E911", {"points": [v(372.62, -149.3) * mm, v(372.12, -149.01) * mm, v(371.51, -149.01) * mm, v(371.02, -149.3) * mm]});
            skFitSpline(sketch, "E912", {"points": [v(371.02, -149.3) * mm, v(370.52, -149.58) * mm, v(370.22, -150.11) * mm, v(370.22, -150.68) * mm]});
            skFitSpline(sketch, "E913", {"points": [v(370.22, -150.68) * mm, v(370.22, -151.25) * mm, v(370.52, -151.78) * mm, v(371.02, -152.07) * mm]});
            skFitSpline(sketch, "E914", {"points": [v(371.02, -152.07) * mm, v(371.51, -152.35) * mm, v(372.12, -152.35) * mm, v(372.62, -152.07) * mm]});
            skFitSpline(sketch, "E915", {"points": [v(372.62, -152.07) * mm, v(373.11, -151.78) * mm, v(373.42, -151.25) * mm, v(373.42, -150.68) * mm]});
            skLineSegment(sketch, "E916", {"start": v(358.12, 180.7) * mm, "end": v(358.12, 179.13) * mm});
            skFitSpline(sketch, "E917", {"points": [v(333.42, -130.08) * mm, v(333.42, -129.5) * mm, v(333.11, -128.98) * mm, v(332.62, -128.7) * mm]});
            skFitSpline(sketch, "E918", {"points": [v(332.62, -128.7) * mm, v(332.12, -128.4) * mm, v(331.51, -128.4) * mm, v(331.02, -128.7) * mm]});
            skFitSpline(sketch, "E919", {"points": [v(331.02, -128.7) * mm, v(330.52, -128.98) * mm, v(330.22, -129.5) * mm, v(330.22, -130.08) * mm]});
            skFitSpline(sketch, "E920", {"points": [v(330.22, -130.08) * mm, v(330.22, -130.96) * mm, v(330.93, -131.68) * mm, v(331.82, -131.68) * mm]});
            skFitSpline(sketch, "E921", {"points": [v(331.82, -131.68) * mm, v(332.7, -131.68) * mm, v(333.42, -130.96) * mm, v(333.42, -130.08) * mm]});
            skFitSpline(sketch, "E922", {"points": [v(213.42, -130.08) * mm, v(213.42, -129.5) * mm, v(213.11, -128.98) * mm, v(212.62, -128.7) * mm]});
            skFitSpline(sketch, "E923", {"points": [v(212.62, -128.7) * mm, v(212.12, -128.4) * mm, v(211.51, -128.4) * mm, v(211.02, -128.7) * mm]});
            skFitSpline(sketch, "E924", {"points": [v(211.02, -128.7) * mm, v(210.52, -128.98) * mm, v(210.22, -129.5) * mm, v(210.22, -130.08) * mm]});
            skFitSpline(sketch, "E925", {"points": [v(210.22, -130.08) * mm, v(210.22, -130.65) * mm, v(210.52, -131.18) * mm, v(211.02, -131.46) * mm]});
            skFitSpline(sketch, "E926", {"points": [v(211.02, -131.46) * mm, v(211.51, -131.75) * mm, v(212.12, -131.75) * mm, v(212.62, -131.46) * mm]});
            skFitSpline(sketch, "E927", {"points": [v(212.62, -131.46) * mm, v(213.11, -131.18) * mm, v(213.42, -130.65) * mm, v(213.42, -130.08) * mm]});
            skFitSpline(sketch, "E928", {"points": [v(53.42, -130.08) * mm, v(53.42, -129.5) * mm, v(53.12, -128.97) * mm, v(52.62, -128.69) * mm]});
            skFitSpline(sketch, "E929", {"points": [v(52.62, -128.69) * mm, v(52.12, -128.4) * mm, v(51.51, -128.4) * mm, v(51.02, -128.69) * mm]});
            skFitSpline(sketch, "E930", {"points": [v(51.02, -128.69) * mm, v(50.52, -128.97) * mm, v(50.22, -129.5) * mm, v(50.22, -130.08) * mm]});
            skFitSpline(sketch, "E931", {"points": [v(50.22, -130.08) * mm, v(50.21, -130.65) * mm, v(50.52, -131.18) * mm, v(51.02, -131.47) * mm]});
            skFitSpline(sketch, "E932", {"points": [v(51.02, -131.47) * mm, v(51.51, -131.76) * mm, v(52.12, -131.76) * mm, v(52.62, -131.47) * mm]});
            skFitSpline(sketch, "E933", {"points": [v(52.62, -131.47) * mm, v(53.12, -131.18) * mm, v(53.42, -130.65) * mm, v(53.42, -130.08) * mm]});
            skFitSpline(sketch, "E934", {"points": [v(333.42, 110.27) * mm, v(333.42, 110.84) * mm, v(333.11, 111.37) * mm, v(332.62, 111.66) * mm]});
            skFitSpline(sketch, "E935", {"points": [v(332.62, 111.66) * mm, v(332.12, 111.94) * mm, v(331.51, 111.94) * mm, v(331.02, 111.66) * mm]});
            skFitSpline(sketch, "E936", {"points": [v(331.02, 111.66) * mm, v(330.52, 111.37) * mm, v(330.22, 110.84) * mm, v(330.22, 110.27) * mm]});
            skFitSpline(sketch, "E937", {"points": [v(330.22, 110.27) * mm, v(330.22, 109.39) * mm, v(330.93, 108.67) * mm, v(331.82, 108.67) * mm]});
            skFitSpline(sketch, "E938", {"points": [v(331.82, 108.67) * mm, v(332.7, 108.67) * mm, v(333.42, 109.39) * mm, v(333.42, 110.27) * mm]});
            skFitSpline(sketch, "E939", {"points": [v(213.42, 110.27) * mm, v(213.42, 110.84) * mm, v(213.11, 111.37) * mm, v(212.62, 111.66) * mm]});
            skFitSpline(sketch, "E940", {"points": [v(212.62, 111.66) * mm, v(212.12, 111.94) * mm, v(211.51, 111.94) * mm, v(211.02, 111.66) * mm]});
            skFitSpline(sketch, "E941", {"points": [v(211.02, 111.66) * mm, v(210.52, 111.37) * mm, v(210.22, 110.84) * mm, v(210.22, 110.27) * mm]});
            skFitSpline(sketch, "E942", {"points": [v(210.22, 110.27) * mm, v(210.22, 109.7) * mm, v(210.52, 109.17) * mm, v(211.02, 108.89) * mm]});
            skFitSpline(sketch, "E943", {"points": [v(211.02, 108.89) * mm, v(211.51, 108.6) * mm, v(212.12, 108.6) * mm, v(212.62, 108.89) * mm]});
            skFitSpline(sketch, "E944", {"points": [v(212.62, 108.89) * mm, v(213.11, 109.17) * mm, v(213.42, 109.7) * mm, v(213.42, 110.27) * mm]});
            skFitSpline(sketch, "E945", {"points": [v(53.42, 110.27) * mm, v(53.42, 110.85) * mm, v(53.12, 111.38) * mm, v(52.62, 111.66) * mm]});
            skFitSpline(sketch, "E946", {"points": [v(52.62, 111.66) * mm, v(52.12, 111.95) * mm, v(51.51, 111.95) * mm, v(51.02, 111.66) * mm]});
            skFitSpline(sketch, "E947", {"points": [v(51.02, 111.66) * mm, v(50.52, 111.38) * mm, v(50.22, 110.85) * mm, v(50.22, 110.27) * mm]});
            skFitSpline(sketch, "E948", {"points": [v(50.22, 110.27) * mm, v(50.21, 109.7) * mm, v(50.52, 109.17) * mm, v(51.02, 108.88) * mm]});
            skFitSpline(sketch, "E949", {"points": [v(51.02, 108.88) * mm, v(51.51, 108.6) * mm, v(52.12, 108.6) * mm, v(52.62, 108.88) * mm]});
            skFitSpline(sketch, "E950", {"points": [v(52.62, 108.88) * mm, v(53.12, 109.17) * mm, v(53.42, 109.7) * mm, v(53.42, 110.27) * mm]});
            skFitSpline(sketch, "E951", {"points": [v(373.42, 130.88) * mm, v(373.42, 131.45) * mm, v(373.11, 131.98) * mm, v(372.62, 132.26) * mm]});
            skFitSpline(sketch, "E952", {"points": [v(372.62, 132.26) * mm, v(372.12, 132.55) * mm, v(371.51, 132.55) * mm, v(371.02, 132.26) * mm]});
            skFitSpline(sketch, "E953", {"points": [v(371.02, 132.26) * mm, v(370.52, 131.98) * mm, v(370.22, 131.45) * mm, v(370.22, 130.88) * mm]});
            skFitSpline(sketch, "E954", {"points": [v(370.22, 130.88) * mm, v(370.22, 130.3) * mm, v(370.52, 129.78) * mm, v(371.02, 129.5) * mm]});
            skFitSpline(sketch, "E955", {"points": [v(371.02, 129.5) * mm, v(371.51, 129.2) * mm, v(372.12, 129.2) * mm, v(372.62, 129.5) * mm]});
            skFitSpline(sketch, "E956", {"points": [v(372.62, 129.5) * mm, v(373.11, 129.78) * mm, v(373.42, 130.3) * mm, v(373.42, 130.88) * mm]});
            skFitSpline(sketch, "E957", {"points": [v(346.77, 155.4) * mm, v(346.77, 155.97) * mm, v(346.47, 156.5) * mm, v(345.97, 156.78) * mm]});
            skFitSpline(sketch, "E958", {"points": [v(345.97, 156.78) * mm, v(345.48, 157.07) * mm, v(344.87, 157.07) * mm, v(344.37, 156.78) * mm]});
            skFitSpline(sketch, "E959", {"points": [v(344.37, 156.78) * mm, v(343.88, 156.5) * mm, v(343.57, 155.97) * mm, v(343.57, 155.4) * mm]});
            skFitSpline(sketch, "E960", {"points": [v(343.57, 155.4) * mm, v(343.57, 154.83) * mm, v(343.88, 154.3) * mm, v(344.37, 154.01) * mm]});
            skFitSpline(sketch, "E961", {"points": [v(344.37, 154.01) * mm, v(344.87, 153.73) * mm, v(345.48, 153.73) * mm, v(345.97, 154.01) * mm]});
            skFitSpline(sketch, "E962", {"points": [v(345.97, 154.01) * mm, v(346.47, 154.3) * mm, v(346.77, 154.83) * mm, v(346.77, 155.4) * mm]});
            skFitSpline(sketch, "E963", {"points": [v(373.42, 179.92) * mm, v(373.42, 180.49) * mm, v(373.11, 181.02) * mm, v(372.62, 181.3) * mm]});
            skFitSpline(sketch, "E964", {"points": [v(372.62, 181.3) * mm, v(372.12, 181.59) * mm, v(371.51, 181.59) * mm, v(371.02, 181.3) * mm]});
            skFitSpline(sketch, "E965", {"points": [v(371.02, 181.3) * mm, v(370.52, 181.02) * mm, v(370.22, 180.49) * mm, v(370.22, 179.92) * mm]});
            skFitSpline(sketch, "E966", {"points": [v(370.22, 179.92) * mm, v(370.22, 179.35) * mm, v(370.52, 178.82) * mm, v(371.02, 178.53) * mm]});
            skFitSpline(sketch, "E967", {"points": [v(371.02, 178.53) * mm, v(371.51, 178.25) * mm, v(372.12, 178.25) * mm, v(372.62, 178.53) * mm]});
            skFitSpline(sketch, "E968", {"points": [v(372.62, 178.53) * mm, v(373.11, 178.82) * mm, v(373.42, 179.35) * mm, v(373.42, 179.92) * mm]});
            skFitSpline(sketch, "E969", {"points": [v(-357.78, -203.8) * mm, v(-357.7, -203.95) * mm, v(-357.53, -204.05) * mm, v(-357.35, -204.05) * mm]});
            skFitSpline(sketch, "E970", {"points": [v(-357.78, -203.8) * mm, v(-357.89, -203.61) * mm, v(-358.1, -203.52) * mm, v(-358.3, -203.55) * mm]});
            skFitSpline(sketch, "E971", {"points": [v(-358.3, -203.55) * mm, v(-358.51, -203.6) * mm, v(-358.67, -203.75) * mm, v(-358.7, -203.96) * mm]});
            skFitSpline(sketch, "E972", {"points": [v(-358.7, -203.96) * mm, v(-358.75, -204.17) * mm, v(-358.65, -204.37) * mm, v(-358.47, -204.48) * mm]});
            skFitSpline(sketch, "E973", {"points": [v(-358.22, -204.91) * mm, v(-358.22, -204.73) * mm, v(-358.31, -204.57) * mm, v(-358.47, -204.48) * mm]});
            skFitSpline(sketch, "E974", {"points": [v(-358.72, -207.05) * mm, v(-358.44, -207.05) * mm, v(-358.22, -206.82) * mm, v(-358.22, -206.55) * mm]});
            skFitSpline(sketch, "E975", {"points": [v(-364.22, -206.55) * mm, v(-364.22, -206.82) * mm, v(-364, -207.05) * mm, v(-363.72, -207.05) * mm]});
            skFitSpline(sketch, "E976", {"points": [v(-363.97, -204.48) * mm, v(-364.12, -204.57) * mm, v(-364.22, -204.73) * mm, v(-364.22, -204.91) * mm]});
            skFitSpline(sketch, "E977", {"points": [v(-363.97, -204.48) * mm, v(-363.79, -204.37) * mm, v(-363.69, -204.17) * mm, v(-363.72, -203.96) * mm]});
            skFitSpline(sketch, "E978", {"points": [v(-363.72, -203.96) * mm, v(-363.76, -203.75) * mm, v(-363.92, -203.6) * mm, v(-364.13, -203.55) * mm]});
            skFitSpline(sketch, "E979", {"points": [v(-364.13, -203.55) * mm, v(-364.34, -203.52) * mm, v(-364.55, -203.61) * mm, v(-364.65, -203.8) * mm]});
            skFitSpline(sketch, "E980", {"points": [v(-365.08, -204.05) * mm, v(-364.9, -204.05) * mm, v(-364.74, -203.95) * mm, v(-364.65, -203.8) * mm]});
            skLineSegment(sketch, "E981", {"start": v(-358.22, -204.91) * mm, "end": v(-358.22, -206.55) * mm});
            skFitSpline(sketch, "E982", {"points": [v(-378.98, -203.8) * mm, v(-378.9, -203.95) * mm, v(-378.73, -204.05) * mm, v(-378.55, -204.05) * mm]});
            skFitSpline(sketch, "E983", {"points": [v(-378.98, -203.8) * mm, v(-379.09, -203.61) * mm, v(-379.3, -203.52) * mm, v(-379.5, -203.55) * mm]});
            skFitSpline(sketch, "E984", {"points": [v(-379.5, -203.55) * mm, v(-379.71, -203.6) * mm, v(-379.87, -203.75) * mm, v(-379.9, -203.96) * mm]});
            skFitSpline(sketch, "E985", {"points": [v(-379.9, -203.96) * mm, v(-379.95, -204.17) * mm, v(-379.85, -204.37) * mm, v(-379.67, -204.48) * mm]});
            skFitSpline(sketch, "E986", {"points": [v(-379.42, -204.91) * mm, v(-379.42, -204.73) * mm, v(-379.51, -204.57) * mm, v(-379.67, -204.48) * mm]});
            skLineSegment(sketch, "E987", {"start": v(-358.72, -207.05) * mm, "end": v(-363.72, -207.05) * mm});
            skFitSpline(sketch, "E988", {"points": [v(-379.92, -207.05) * mm, v(-379.78, -207.05) * mm, v(-379.66, -207) * mm, v(-379.56, -206.9) * mm]});
            skFitSpline(sketch, "E989", {"points": [v(-379.56, -206.9) * mm, v(-379.47, -206.8) * mm, v(-379.42, -206.68) * mm, v(-379.42, -206.55) * mm]});
            skLineSegment(sketch, "E990", {"start": v(-364.22, -206.55) * mm, "end": v(-364.22, -204.91) * mm});
            skFitSpline(sketch, "E991", {"points": [v(-385.42, -206.55) * mm, v(-385.42, -206.82) * mm, v(-385.2, -207.05) * mm, v(-384.92, -207.05) * mm]});
            skLineSegment(sketch, "E992", {"start": v(-365.08, -204.05) * mm, "end": v(-370.22, -204.05) * mm});
            skLineSegment(sketch, "E993", {"start": v(-370.22, -204.05) * mm, "end": v(-370.22, -201.05) * mm});
            skLineSegment(sketch, "E994", {"start": v(-370.22, -201.05) * mm, "end": v(-368.94, -201.05) * mm});
            skLineSegment(sketch, "E995", {"start": v(-368.94, -201.05) * mm, "end": v(-368.94, -197.05) * mm});
            skLineSegment(sketch, "E996", {"start": v(-368.94, -197.05) * mm, "end": v(-370.22, -197.05) * mm});
            skLineSegment(sketch, "E997", {"start": v(-370.22, -197.05) * mm, "end": v(-370.22, -194.05) * mm});
            skLineSegment(sketch, "E998", {"start": v(-370.22, -194.05) * mm, "end": v(-373.42, -194.05) * mm});
            skLineSegment(sketch, "E999", {"start": v(-373.42, -194.05) * mm, "end": v(-373.42, -197.05) * mm});
            skLineSegment(sketch, "E1000", {"start": v(-373.42, -197.05) * mm, "end": v(-374.7, -197.05) * mm});
            skLineSegment(sketch, "E1001", {"start": v(-374.7, -197.05) * mm, "end": v(-374.7, -201.05) * mm});
            skLineSegment(sketch, "E1002", {"start": v(-374.7, -201.05) * mm, "end": v(-373.42, -201.05) * mm});
            skLineSegment(sketch, "E1003", {"start": v(-373.42, -201.05) * mm, "end": v(-373.42, -204.05) * mm});
            skLineSegment(sketch, "E1004", {"start": v(-373.42, -204.05) * mm, "end": v(-378.55, -204.05) * mm});
            skFitSpline(sketch, "E1005", {"points": [v(-385.17, -204.48) * mm, v(-385.32, -204.57) * mm, v(-385.42, -204.73) * mm, v(-385.42, -204.91) * mm]});
            skFitSpline(sketch, "E1006", {"points": [v(-385.17, -204.48) * mm, v(-384.99, -204.37) * mm, v(-384.89, -204.17) * mm, v(-384.92, -203.96) * mm]});
            skFitSpline(sketch, "E1007", {"points": [v(-384.92, -203.96) * mm, v(-384.96, -203.75) * mm, v(-385.12, -203.6) * mm, v(-385.33, -203.55) * mm]});
            skFitSpline(sketch, "E1008", {"points": [v(-385.33, -203.55) * mm, v(-385.54, -203.52) * mm, v(-385.75, -203.61) * mm, v(-385.85, -203.8) * mm]});
            skFitSpline(sketch, "E1009", {"points": [v(-386.28, -204.05) * mm, v(-386.1, -204.05) * mm, v(-385.94, -203.95) * mm, v(-385.85, -203.8) * mm]});
            skLineSegment(sketch, "E1010", {"start": v(-379.42, -204.91) * mm, "end": v(-379.42, -206.55) * mm});
            skLineSegment(sketch, "E1011", {"start": v(-379.92, -207.05) * mm, "end": v(-384.92, -207.05) * mm});
            skFitSpline(sketch, "E1012", {"points": [v(-385.85, -74.3) * mm, v(-385.94, -74.14) * mm, v(-386.1, -74.05) * mm, v(-386.28, -74.05) * mm]});
            skFitSpline(sketch, "E1013", {"points": [v(-385.85, -74.3) * mm, v(-385.75, -74.48) * mm, v(-385.54, -74.58) * mm, v(-385.33, -74.54) * mm]});
            skFitSpline(sketch, "E1014", {"points": [v(-385.33, -74.54) * mm, v(-385.12, -74.5) * mm, v(-384.96, -74.34) * mm, v(-384.92, -74.13) * mm]});
            skFitSpline(sketch, "E1015", {"points": [v(-384.92, -74.13) * mm, v(-384.89, -73.93) * mm, v(-384.99, -73.72) * mm, v(-385.17, -73.61) * mm]});
            skFitSpline(sketch, "E1016", {"points": [v(-385.17, -73.61) * mm, v(-385.32, -73.52) * mm, v(-385.42, -73.36) * mm, v(-385.42, -73.18) * mm]});
            skLineSegment(sketch, "E1017", {"start": v(-385.42, -206.55) * mm, "end": v(-385.42, -204.91) * mm});
            skLineSegment(sketch, "E1018", {"start": v(-385.42, -73.18) * mm, "end": v(-385.42, 178.45) * mm});
            skLineSegment(sketch, "E1019", {"start": v(-385.42, 178.45) * mm, "end": v(-385.42, 182.46) * mm});
            skLineSegment(sketch, "E1020", {"start": v(-386.28, -204.05) * mm, "end": v(-396.82, -204.05) * mm});
            skFitSpline(sketch, "E1021", {"points": [v(-358.47, -73.61) * mm, v(-358.31, -73.52) * mm, v(-358.22, -73.36) * mm, v(-358.22, -73.17) * mm]});
            skLineSegment(sketch, "E1022", {"start": v(-396.82, -199.05) * mm, "end": v(-396.82, -178.05) * mm});
            skLineSegment(sketch, "E1023", {"start": v(-396.82, -178.05) * mm, "end": v(-394.82, -176.05) * mm});
            skLineSegment(sketch, "E1024", {"start": v(-394.82, -176.05) * mm, "end": v(-394.82, -74.05) * mm});
            skLineSegment(sketch, "E1025", {"start": v(-394.82, -74.05) * mm, "end": v(-386.28, -74.05) * mm});
            skFitSpline(sketch, "E1026", {"points": [v(-358.47, -73.61) * mm, v(-358.65, -73.72) * mm, v(-358.75, -73.93) * mm, v(-358.7, -74.13) * mm]});
            skFitSpline(sketch, "E1027", {"points": [v(-358.7, -74.13) * mm, v(-358.67, -74.34) * mm, v(-358.51, -74.5) * mm, v(-358.3, -74.54) * mm]});
            skFitSpline(sketch, "E1028", {"points": [v(-358.3, -74.54) * mm, v(-358.1, -74.58) * mm, v(-357.89, -74.48) * mm, v(-357.78, -74.3) * mm]});
            skFitSpline(sketch, "E1029", {"points": [v(-357.35, -74.05) * mm, v(-357.53, -74.05) * mm, v(-357.7, -74.14) * mm, v(-357.78, -74.3) * mm]});
            skFitSpline(sketch, "E1030", {"points": [v(-345.85, -74.3) * mm, v(-345.94, -74.14) * mm, v(-346.1, -74.05) * mm, v(-346.28, -74.05) * mm]});
            skFitSpline(sketch, "E1031", {"points": [v(-345.85, -74.3) * mm, v(-345.75, -74.48) * mm, v(-345.54, -74.58) * mm, v(-345.33, -74.54) * mm]});
            skFitSpline(sketch, "E1032", {"points": [v(-345.33, -74.54) * mm, v(-345.12, -74.5) * mm, v(-344.96, -74.34) * mm, v(-344.92, -74.13) * mm]});
            skFitSpline(sketch, "E1033", {"points": [v(-344.92, -74.13) * mm, v(-344.89, -73.93) * mm, v(-344.99, -73.72) * mm, v(-345.17, -73.61) * mm]});
            skFitSpline(sketch, "E1034", {"points": [v(-345.42, -73.18) * mm, v(-345.42, -73.36) * mm, v(-345.32, -73.52) * mm, v(-345.17, -73.61) * mm]});
            skFitSpline(sketch, "E1035", {"points": [v(-344.92, -71.05) * mm, v(-345.2, -71.05) * mm, v(-345.42, -71.27) * mm, v(-345.42, -71.55) * mm]});
            skLineSegment(sketch, "E1036", {"start": v(-358.22, -73.17) * mm, "end": v(-358.22, 178.44) * mm});
            skLineSegment(sketch, "E1037", {"start": v(-358.22, 178.44) * mm, "end": v(-358.22, 182.41) * mm});
            skFitSpline(sketch, "E1038", {"points": [v(-339.42, -71.55) * mm, v(-339.42, -71.27) * mm, v(-339.64, -71.05) * mm, v(-339.92, -71.05) * mm]});
            skLineSegment(sketch, "E1039", {"start": v(-357.35, -74.05) * mm, "end": v(-346.28, -74.05) * mm});
            skFitSpline(sketch, "E1040", {"points": [v(-339.67, -73.61) * mm, v(-339.51, -73.52) * mm, v(-339.42, -73.36) * mm, v(-339.42, -73.18) * mm]});
            skFitSpline(sketch, "E1041", {"points": [v(-339.67, -73.61) * mm, v(-339.85, -73.72) * mm, v(-339.95, -73.93) * mm, v(-339.9, -74.13) * mm]});
            skFitSpline(sketch, "E1042", {"points": [v(-339.9, -74.13) * mm, v(-339.87, -74.34) * mm, v(-339.71, -74.5) * mm, v(-339.5, -74.54) * mm]});
            skFitSpline(sketch, "E1043", {"points": [v(-339.5, -74.54) * mm, v(-339.3, -74.58) * mm, v(-339.09, -74.48) * mm, v(-338.98, -74.3) * mm]});
            skFitSpline(sketch, "E1044", {"points": [v(-338.55, -74.05) * mm, v(-338.73, -74.05) * mm, v(-338.9, -74.14) * mm, v(-338.98, -74.3) * mm]});
            skLineSegment(sketch, "E1045", {"start": v(-345.42, -73.18) * mm, "end": v(-345.42, -71.55) * mm});
            skFitSpline(sketch, "E1046", {"points": [v(-324.65, -74.3) * mm, v(-324.74, -74.14) * mm, v(-324.9, -74.05) * mm, v(-325.08, -74.05) * mm]});
            skFitSpline(sketch, "E1047", {"points": [v(-324.65, -74.3) * mm, v(-324.55, -74.48) * mm, v(-324.34, -74.58) * mm, v(-324.13, -74.54) * mm]});
            skFitSpline(sketch, "E1048", {"points": [v(-324.13, -74.54) * mm, v(-323.92, -74.5) * mm, v(-323.76, -74.34) * mm, v(-323.72, -74.13) * mm]});
            skFitSpline(sketch, "E1049", {"points": [v(-323.72, -74.13) * mm, v(-323.69, -73.93) * mm, v(-323.79, -73.72) * mm, v(-323.97, -73.61) * mm]});
            skFitSpline(sketch, "E1050", {"points": [v(-324.22, -73.18) * mm, v(-324.22, -73.36) * mm, v(-324.12, -73.52) * mm, v(-323.97, -73.61) * mm]});
            skLineSegment(sketch, "E1051", {"start": v(-344.92, -71.05) * mm, "end": v(-339.92, -71.05) * mm});
            skFitSpline(sketch, "E1052", {"points": [v(-323.72, -71.05) * mm, v(-324, -71.05) * mm, v(-324.22, -71.27) * mm, v(-324.22, -71.55) * mm]});
            skLineSegment(sketch, "E1053", {"start": v(-339.42, -71.55) * mm, "end": v(-339.42, -73.18) * mm});
            skFitSpline(sketch, "E1054", {"points": [v(-318.22, -71.55) * mm, v(-318.22, -71.27) * mm, v(-318.44, -71.05) * mm, v(-318.72, -71.05) * mm]});
            skLineSegment(sketch, "E1055", {"start": v(-338.55, -74.05) * mm, "end": v(-333.42, -74.05) * mm});
            skLineSegment(sketch, "E1056", {"start": v(-333.42, -74.05) * mm, "end": v(-333.42, -77.05) * mm});
            skLineSegment(sketch, "E1057", {"start": v(-333.42, -77.05) * mm, "end": v(-334.7, -77.05) * mm});
            skLineSegment(sketch, "E1058", {"start": v(-334.7, -77.05) * mm, "end": v(-334.7, -81.05) * mm});
            skLineSegment(sketch, "E1059", {"start": v(-334.7, -81.05) * mm, "end": v(-333.42, -81.05) * mm});
            skLineSegment(sketch, "E1060", {"start": v(-333.42, -81.05) * mm, "end": v(-333.42, -84.05) * mm});
            skLineSegment(sketch, "E1061", {"start": v(-333.42, -84.05) * mm, "end": v(-330.22, -84.05) * mm});
            skLineSegment(sketch, "E1062", {"start": v(-330.22, -84.05) * mm, "end": v(-330.22, -81.05) * mm});
            skLineSegment(sketch, "E1063", {"start": v(-330.22, -81.05) * mm, "end": v(-328.94, -81.05) * mm});
            skLineSegment(sketch, "E1064", {"start": v(-328.94, -81.05) * mm, "end": v(-328.94, -77.05) * mm});
            skLineSegment(sketch, "E1065", {"start": v(-328.94, -77.05) * mm, "end": v(-330.22, -77.05) * mm});
            skLineSegment(sketch, "E1066", {"start": v(-330.22, -77.05) * mm, "end": v(-330.22, -74.05) * mm});
            skLineSegment(sketch, "E1067", {"start": v(-330.22, -74.05) * mm, "end": v(-325.08, -74.05) * mm});
            skFitSpline(sketch, "E1068", {"points": [v(-318.47, -73.61) * mm, v(-318.31, -73.52) * mm, v(-318.22, -73.36) * mm, v(-318.22, -73.18) * mm]});
            skFitSpline(sketch, "E1069", {"points": [v(-318.47, -73.61) * mm, v(-318.65, -73.72) * mm, v(-318.75, -73.93) * mm, v(-318.7, -74.13) * mm]});
            skFitSpline(sketch, "E1070", {"points": [v(-318.7, -74.13) * mm, v(-318.67, -74.34) * mm, v(-318.51, -74.5) * mm, v(-318.3, -74.54) * mm]});
            skFitSpline(sketch, "E1071", {"points": [v(-318.3, -74.54) * mm, v(-318.1, -74.58) * mm, v(-317.89, -74.48) * mm, v(-317.78, -74.3) * mm]});
            skFitSpline(sketch, "E1072", {"points": [v(-317.35, -74.05) * mm, v(-317.53, -74.05) * mm, v(-317.7, -74.14) * mm, v(-317.78, -74.3) * mm]});
            skLineSegment(sketch, "E1073", {"start": v(-324.22, -73.18) * mm, "end": v(-324.22, -71.55) * mm});
            skFitSpline(sketch, "E1074", {"points": [v(-225.85, -74.3) * mm, v(-225.94, -74.14) * mm, v(-226.1, -74.05) * mm, v(-226.28, -74.05) * mm]});
            skFitSpline(sketch, "E1075", {"points": [v(-225.85, -74.3) * mm, v(-225.75, -74.48) * mm, v(-225.54, -74.58) * mm, v(-225.33, -74.54) * mm]});
            skFitSpline(sketch, "E1076", {"points": [v(-225.33, -74.54) * mm, v(-225.12, -74.5) * mm, v(-224.96, -74.34) * mm, v(-224.92, -74.13) * mm]});
            skFitSpline(sketch, "E1077", {"points": [v(-224.92, -74.13) * mm, v(-224.89, -73.93) * mm, v(-224.99, -73.72) * mm, v(-225.17, -73.61) * mm]});
            skFitSpline(sketch, "E1078", {"points": [v(-225.42, -73.18) * mm, v(-225.42, -73.36) * mm, v(-225.32, -73.52) * mm, v(-225.17, -73.61) * mm]});
            skLineSegment(sketch, "E1079", {"start": v(-323.72, -71.05) * mm, "end": v(-318.72, -71.05) * mm});
            skFitSpline(sketch, "E1080", {"points": [v(-224.92, -71.05) * mm, v(-225.2, -71.05) * mm, v(-225.42, -71.27) * mm, v(-225.42, -71.55) * mm]});
            skLineSegment(sketch, "E1081", {"start": v(-318.22, -71.55) * mm, "end": v(-318.22, -73.18) * mm});
            skFitSpline(sketch, "E1082", {"points": [v(-219.42, -71.55) * mm, v(-219.42, -71.27) * mm, v(-219.64, -71.05) * mm, v(-219.92, -71.05) * mm]});
            skLineSegment(sketch, "E1083", {"start": v(-317.35, -74.05) * mm, "end": v(-226.28, -74.05) * mm});
            skFitSpline(sketch, "E1084", {"points": [v(-219.67, -73.61) * mm, v(-219.51, -73.52) * mm, v(-219.42, -73.36) * mm, v(-219.42, -73.18) * mm]});
            skFitSpline(sketch, "E1085", {"points": [v(-219.67, -73.61) * mm, v(-219.85, -73.72) * mm, v(-219.95, -73.93) * mm, v(-219.9, -74.13) * mm]});
            skFitSpline(sketch, "E1086", {"points": [v(-219.9, -74.13) * mm, v(-219.87, -74.34) * mm, v(-219.71, -74.5) * mm, v(-219.5, -74.54) * mm]});
            skFitSpline(sketch, "E1087", {"points": [v(-219.5, -74.54) * mm, v(-219.3, -74.58) * mm, v(-219.09, -74.48) * mm, v(-218.98, -74.3) * mm]});
            skFitSpline(sketch, "E1088", {"points": [v(-218.55, -74.05) * mm, v(-218.73, -74.05) * mm, v(-218.9, -74.14) * mm, v(-218.98, -74.3) * mm]});
            skLineSegment(sketch, "E1089", {"start": v(-225.42, -73.18) * mm, "end": v(-225.42, -71.55) * mm});
            skFitSpline(sketch, "E1090", {"points": [v(-204.65, -74.3) * mm, v(-204.74, -74.14) * mm, v(-204.9, -74.05) * mm, v(-205.08, -74.05) * mm]});
            skFitSpline(sketch, "E1091", {"points": [v(-204.65, -74.3) * mm, v(-204.55, -74.48) * mm, v(-204.34, -74.58) * mm, v(-204.13, -74.54) * mm]});
            skFitSpline(sketch, "E1092", {"points": [v(-204.13, -74.54) * mm, v(-203.92, -74.5) * mm, v(-203.76, -74.34) * mm, v(-203.72, -74.13) * mm]});
            skFitSpline(sketch, "E1093", {"points": [v(-203.72, -74.13) * mm, v(-203.69, -73.93) * mm, v(-203.79, -73.72) * mm, v(-203.97, -73.61) * mm]});
            skFitSpline(sketch, "E1094", {"points": [v(-204.22, -73.18) * mm, v(-204.22, -73.36) * mm, v(-204.12, -73.52) * mm, v(-203.97, -73.61) * mm]});
            skLineSegment(sketch, "E1095", {"start": v(-224.92, -71.05) * mm, "end": v(-219.92, -71.05) * mm});
            skFitSpline(sketch, "E1096", {"points": [v(-203.72, -71.05) * mm, v(-204, -71.05) * mm, v(-204.22, -71.27) * mm, v(-204.22, -71.55) * mm]});
            skLineSegment(sketch, "E1097", {"start": v(-219.42, -71.55) * mm, "end": v(-219.42, -73.18) * mm});
            skFitSpline(sketch, "E1098", {"points": [v(-198.22, -71.55) * mm, v(-198.22, -71.41) * mm, v(-198.27, -71.29) * mm, v(-198.36, -71.2) * mm]});
            skFitSpline(sketch, "E1099", {"points": [v(-198.36, -71.2) * mm, v(-198.46, -71.1) * mm, v(-198.58, -71.05) * mm, v(-198.72, -71.05) * mm]});
            skLineSegment(sketch, "E1100", {"start": v(-218.55, -74.05) * mm, "end": v(-213.42, -74.05) * mm});
            skLineSegment(sketch, "E1101", {"start": v(-213.42, -74.05) * mm, "end": v(-213.42, -77.05) * mm});
            skLineSegment(sketch, "E1102", {"start": v(-213.42, -77.05) * mm, "end": v(-214.7, -77.05) * mm});
            skLineSegment(sketch, "E1103", {"start": v(-214.7, -77.05) * mm, "end": v(-214.7, -81.05) * mm});
            skLineSegment(sketch, "E1104", {"start": v(-214.7, -81.05) * mm, "end": v(-213.42, -81.05) * mm});
            skLineSegment(sketch, "E1105", {"start": v(-213.42, -81.05) * mm, "end": v(-213.42, -84.05) * mm});
            skLineSegment(sketch, "E1106", {"start": v(-213.42, -84.05) * mm, "end": v(-210.22, -84.05) * mm});
            skLineSegment(sketch, "E1107", {"start": v(-210.22, -84.05) * mm, "end": v(-210.22, -81.05) * mm});
            skLineSegment(sketch, "E1108", {"start": v(-210.22, -81.05) * mm, "end": v(-208.94, -81.05) * mm});
            skLineSegment(sketch, "E1109", {"start": v(-208.94, -81.05) * mm, "end": v(-208.94, -77.05) * mm});
            skLineSegment(sketch, "E1110", {"start": v(-208.94, -77.05) * mm, "end": v(-210.22, -77.05) * mm});
            skLineSegment(sketch, "E1111", {"start": v(-210.22, -77.05) * mm, "end": v(-210.22, -74.05) * mm});
            skLineSegment(sketch, "E1112", {"start": v(-210.22, -74.05) * mm, "end": v(-205.08, -74.05) * mm});
            skFitSpline(sketch, "E1113", {"points": [v(-198.47, -73.61) * mm, v(-198.31, -73.52) * mm, v(-198.22, -73.36) * mm, v(-198.22, -73.18) * mm]});
            skFitSpline(sketch, "E1114", {"points": [v(-198.47, -73.61) * mm, v(-198.65, -73.72) * mm, v(-198.75, -73.93) * mm, v(-198.7, -74.13) * mm]});
            skFitSpline(sketch, "E1115", {"points": [v(-198.7, -74.13) * mm, v(-198.67, -74.34) * mm, v(-198.51, -74.5) * mm, v(-198.3, -74.54) * mm]});
            skFitSpline(sketch, "E1116", {"points": [v(-198.3, -74.54) * mm, v(-198.1, -74.58) * mm, v(-197.89, -74.48) * mm, v(-197.78, -74.3) * mm]});
            skFitSpline(sketch, "E1117", {"points": [v(-197.35, -74.05) * mm, v(-197.53, -74.05) * mm, v(-197.7, -74.14) * mm, v(-197.78, -74.3) * mm]});
            skLineSegment(sketch, "E1118", {"start": v(-204.22, -73.18) * mm, "end": v(-204.22, -71.55) * mm});
            skFitSpline(sketch, "E1119", {"points": [v(-65.85, -74.3) * mm, v(-65.94, -74.14) * mm, v(-66.1, -74.05) * mm, v(-66.28, -74.05) * mm]});
            skFitSpline(sketch, "E1120", {"points": [v(-65.85, -74.3) * mm, v(-65.75, -74.48) * mm, v(-65.54, -74.58) * mm, v(-65.33, -74.54) * mm]});
            skFitSpline(sketch, "E1121", {"points": [v(-65.33, -74.54) * mm, v(-65.12, -74.5) * mm, v(-64.96, -74.34) * mm, v(-64.92, -74.13) * mm]});
            skFitSpline(sketch, "E1122", {"points": [v(-64.92, -74.13) * mm, v(-64.89, -73.93) * mm, v(-64.99, -73.72) * mm, v(-65.17, -73.61) * mm]});
            skFitSpline(sketch, "E1123", {"points": [v(-65.42, -73.18) * mm, v(-65.42, -73.36) * mm, v(-65.32, -73.52) * mm, v(-65.17, -73.61) * mm]});
            skLineSegment(sketch, "E1124", {"start": v(-203.72, -71.05) * mm, "end": v(-198.72, -71.05) * mm});
            skFitSpline(sketch, "E1125", {"points": [v(-64.92, -71.05) * mm, v(-65.05, -71.05) * mm, v(-65.18, -71.1) * mm, v(-65.27, -71.2) * mm]});
            skFitSpline(sketch, "E1126", {"points": [v(-65.27, -71.2) * mm, v(-65.36, -71.29) * mm, v(-65.42, -71.41) * mm, v(-65.42, -71.55) * mm]});
            skLineSegment(sketch, "E1127", {"start": v(-198.22, -71.55) * mm, "end": v(-198.22, -73.18) * mm});
            skFitSpline(sketch, "E1128", {"points": [v(-59.42, -71.55) * mm, v(-59.42, -71.27) * mm, v(-59.64, -71.05) * mm, v(-59.92, -71.05) * mm]});
            skLineSegment(sketch, "E1129", {"start": v(-197.35, -74.05) * mm, "end": v(-66.28, -74.05) * mm});
            skFitSpline(sketch, "E1130", {"points": [v(-59.67, -73.61) * mm, v(-59.51, -73.52) * mm, v(-59.42, -73.36) * mm, v(-59.42, -73.18) * mm]});
            skFitSpline(sketch, "E1131", {"points": [v(-59.67, -73.61) * mm, v(-59.85, -73.72) * mm, v(-59.95, -73.93) * mm, v(-59.9, -74.13) * mm]});
            skFitSpline(sketch, "E1132", {"points": [v(-59.9, -74.13) * mm, v(-59.87, -74.34) * mm, v(-59.71, -74.5) * mm, v(-59.5, -74.54) * mm]});
            skFitSpline(sketch, "E1133", {"points": [v(-59.5, -74.54) * mm, v(-59.3, -74.58) * mm, v(-59.09, -74.48) * mm, v(-58.98, -74.3) * mm]});
            skFitSpline(sketch, "E1134", {"points": [v(-58.55, -74.05) * mm, v(-58.73, -74.05) * mm, v(-58.9, -74.14) * mm, v(-58.98, -74.3) * mm]});
            skLineSegment(sketch, "E1135", {"start": v(-65.42, -73.18) * mm, "end": v(-65.42, -71.55) * mm});
            skFitSpline(sketch, "E1136", {"points": [v(-44.65, -74.3) * mm, v(-44.74, -74.14) * mm, v(-44.9, -74.05) * mm, v(-45.08, -74.05) * mm]});
            skFitSpline(sketch, "E1137", {"points": [v(-44.65, -74.3) * mm, v(-44.55, -74.48) * mm, v(-44.34, -74.58) * mm, v(-44.13, -74.54) * mm]});
            skFitSpline(sketch, "E1138", {"points": [v(-44.13, -74.54) * mm, v(-43.92, -74.5) * mm, v(-43.76, -74.34) * mm, v(-43.72, -74.13) * mm]});
            skFitSpline(sketch, "E1139", {"points": [v(-43.72, -74.13) * mm, v(-43.69, -73.93) * mm, v(-43.79, -73.72) * mm, v(-43.97, -73.61) * mm]});
            skFitSpline(sketch, "E1140", {"points": [v(-44.22, -73.18) * mm, v(-44.22, -73.36) * mm, v(-44.12, -73.52) * mm, v(-43.97, -73.61) * mm]});
            skLineSegment(sketch, "E1141", {"start": v(-64.92, -71.05) * mm, "end": v(-59.92, -71.05) * mm});
            skFitSpline(sketch, "E1142", {"points": [v(-43.72, -71.05) * mm, v(-44, -71.05) * mm, v(-44.22, -71.27) * mm, v(-44.22, -71.55) * mm]});
            skLineSegment(sketch, "E1143", {"start": v(-59.42, -71.55) * mm, "end": v(-59.42, -73.18) * mm});
            skFitSpline(sketch, "E1144", {"points": [v(-38.22, -71.55) * mm, v(-38.22, -71.27) * mm, v(-38.44, -71.05) * mm, v(-38.72, -71.05) * mm]});
            skLineSegment(sketch, "E1145", {"start": v(-58.55, -74.05) * mm, "end": v(-53.42, -74.05) * mm});
            skLineSegment(sketch, "E1146", {"start": v(-53.42, -74.05) * mm, "end": v(-53.42, -77.05) * mm});
            skLineSegment(sketch, "E1147", {"start": v(-53.42, -77.05) * mm, "end": v(-54.7, -77.05) * mm});
            skLineSegment(sketch, "E1148", {"start": v(-54.7, -77.05) * mm, "end": v(-54.7, -81.05) * mm});
            skLineSegment(sketch, "E1149", {"start": v(-54.7, -81.05) * mm, "end": v(-53.42, -81.05) * mm});
            skLineSegment(sketch, "E1150", {"start": v(-53.42, -81.05) * mm, "end": v(-53.42, -84.05) * mm});
            skLineSegment(sketch, "E1151", {"start": v(-53.42, -84.05) * mm, "end": v(-50.22, -84.05) * mm});
            skLineSegment(sketch, "E1152", {"start": v(-50.22, -84.05) * mm, "end": v(-50.22, -81.05) * mm});
            skLineSegment(sketch, "E1153", {"start": v(-50.22, -81.05) * mm, "end": v(-48.94, -81.05) * mm});
            skLineSegment(sketch, "E1154", {"start": v(-48.94, -81.05) * mm, "end": v(-48.94, -77.05) * mm});
            skLineSegment(sketch, "E1155", {"start": v(-48.94, -77.05) * mm, "end": v(-50.22, -77.05) * mm});
            skLineSegment(sketch, "E1156", {"start": v(-50.22, -77.05) * mm, "end": v(-50.22, -74.05) * mm});
            skLineSegment(sketch, "E1157", {"start": v(-50.22, -74.05) * mm, "end": v(-45.08, -74.05) * mm});
            skFitSpline(sketch, "E1158", {"points": [v(-38.47, -73.61) * mm, v(-38.31, -73.52) * mm, v(-38.22, -73.36) * mm, v(-38.22, -73.18) * mm]});
            skFitSpline(sketch, "E1159", {"points": [v(-38.47, -73.61) * mm, v(-38.65, -73.72) * mm, v(-38.75, -73.93) * mm, v(-38.7, -74.13) * mm]});
            skFitSpline(sketch, "E1160", {"points": [v(-38.7, -74.13) * mm, v(-38.67, -74.34) * mm, v(-38.51, -74.5) * mm, v(-38.3, -74.54) * mm]});
            skFitSpline(sketch, "E1161", {"points": [v(-38.3, -74.54) * mm, v(-38.1, -74.58) * mm, v(-37.89, -74.48) * mm, v(-37.78, -74.3) * mm]});
            skFitSpline(sketch, "E1162", {"points": [v(-37.35, -74.05) * mm, v(-37.53, -74.05) * mm, v(-37.7, -74.14) * mm, v(-37.78, -74.3) * mm]});
            skLineSegment(sketch, "E1163", {"start": v(-44.22, -73.18) * mm, "end": v(-44.22, -71.55) * mm});
            skFitSpline(sketch, "E1164", {"points": [v(-29.48, -84.45) * mm, v(-29.4, -84.6) * mm, v(-29.23, -84.7) * mm, v(-29.05, -84.7) * mm]});
            skFitSpline(sketch, "E1165", {"points": [v(-29.48, -84.45) * mm, v(-29.59, -84.26) * mm, v(-29.8, -84.17) * mm, v(-30, -84.2) * mm]});
            skFitSpline(sketch, "E1166", {"points": [v(-30, -84.2) * mm, v(-30.21, -84.24) * mm, v(-30.37, -84.4) * mm, v(-30.4, -84.6) * mm]});
            skFitSpline(sketch, "E1167", {"points": [v(-30.4, -84.6) * mm, v(-30.45, -84.82) * mm, v(-30.35, -85.02) * mm, v(-30.17, -85.13) * mm]});
            skFitSpline(sketch, "E1168", {"points": [v(-29.92, -85.56) * mm, v(-29.92, -85.38) * mm, v(-30.01, -85.22) * mm, v(-30.17, -85.13) * mm]});
            skLineSegment(sketch, "E1169", {"start": v(-43.72, -71.05) * mm, "end": v(-38.72, -71.05) * mm});
            skLineSegment(sketch, "E1170", {"start": v(-38.22, -71.55) * mm, "end": v(-38.22, -73.18) * mm});
            skLineSegment(sketch, "E1171", {"start": v(-37.35, -74.05) * mm, "end": v(-26.82, -74.05) * mm});
            skLineSegment(sketch, "E1172", {"start": v(-26.82, -74.05) * mm, "end": v(-26.82, -84.7) * mm});
            skLineSegment(sketch, "E1173", {"start": v(-26.82, -84.7) * mm, "end": v(-29.05, -84.7) * mm});
            skFitSpline(sketch, "E1174", {"points": [v(-55.82, -98.05) * mm, v(-53.6, -98.05) * mm, v(-51.82, -96.26) * mm, v(-51.82, -94.05) * mm]});
            skFitSpline(sketch, "E1175", {"points": [v(-51.82, -94.05) * mm, v(-51.82, -91.84) * mm, v(-53.6, -90.05) * mm, v(-55.82, -90.05) * mm]});
            skLineSegment(sketch, "E1176", {"start": v(-29.92, -85.56) * mm, "end": v(-29.92, -93.1) * mm});
            skLineSegment(sketch, "E1177", {"start": v(-29.92, -93.1) * mm, "end": v(-32.92, -93.1) * mm});
            skLineSegment(sketch, "E1178", {"start": v(-32.92, -93.1) * mm, "end": v(-32.92, -91.82) * mm});
            skLineSegment(sketch, "E1179", {"start": v(-32.92, -91.82) * mm, "end": v(-36.92, -91.82) * mm});
            skLineSegment(sketch, "E1180", {"start": v(-36.92, -91.82) * mm, "end": v(-36.92, -93.1) * mm});
            skLineSegment(sketch, "E1181", {"start": v(-36.92, -93.1) * mm, "end": v(-39.92, -93.1) * mm});
            skLineSegment(sketch, "E1182", {"start": v(-39.92, -93.1) * mm, "end": v(-39.92, -96.3) * mm});
            skLineSegment(sketch, "E1183", {"start": v(-39.92, -96.3) * mm, "end": v(-36.92, -96.3) * mm});
            skLineSegment(sketch, "E1184", {"start": v(-36.92, -96.3) * mm, "end": v(-36.92, -97.57) * mm});
            skLineSegment(sketch, "E1185", {"start": v(-36.92, -97.57) * mm, "end": v(-32.92, -97.57) * mm});
            skLineSegment(sketch, "E1186", {"start": v(-32.92, -97.57) * mm, "end": v(-32.92, -96.3) * mm});
            skLineSegment(sketch, "E1187", {"start": v(-32.92, -96.3) * mm, "end": v(-29.92, -96.3) * mm});
            skLineSegment(sketch, "E1188", {"start": v(-29.92, -96.3) * mm, "end": v(-29.92, -105.04) * mm});
            skLineSegment(sketch, "E1189", {"start": v(-29.92, -105.04) * mm, "end": v(-352, -198.94) * mm});
            skFitSpline(sketch, "E1190", {"points": [v(-63.82, -90.05) * mm, v(-66.03, -90.05) * mm, v(-67.82, -91.84) * mm, v(-67.82, -94.05) * mm]});
            skFitSpline(sketch, "E1191", {"points": [v(-67.82, -94.05) * mm, v(-67.82, -96.26) * mm, v(-66.03, -98.05) * mm, v(-63.82, -98.05) * mm]});
            skLineSegment(sketch, "E1192", {"start": v(-352.37, -204.05) * mm, "end": v(-357.35, -204.05) * mm});
            skFitSpline(sketch, "E1193", {"points": [v(-115.82, -98.05) * mm, v(-113.6, -98.05) * mm, v(-111.82, -96.26) * mm, v(-111.82, -94.05) * mm]});
            skFitSpline(sketch, "E1194", {"points": [v(-111.82, -94.05) * mm, v(-111.82, -91.84) * mm, v(-113.6, -90.05) * mm, v(-115.82, -90.05) * mm]});
            skLineSegment(sketch, "E1195", {"start": v(-63.82, -98.05) * mm, "end": v(-55.82, -98.05) * mm});
            skFitSpline(sketch, "E1196", {"points": [v(-123.82, -90.05) * mm, v(-126.03, -90.05) * mm, v(-127.82, -91.84) * mm, v(-127.82, -94.05) * mm]});
            skFitSpline(sketch, "E1197", {"points": [v(-127.82, -94.05) * mm, v(-127.82, -96.26) * mm, v(-126.03, -98.05) * mm, v(-123.82, -98.05) * mm]});
            skLineSegment(sketch, "E1198", {"start": v(-55.82, -90.05) * mm, "end": v(-63.82, -90.05) * mm});
            skFitSpline(sketch, "E1199", {"points": [v(-175.82, -98.05) * mm, v(-173.6, -98.05) * mm, v(-171.82, -96.26) * mm, v(-171.82, -94.05) * mm]});
            skFitSpline(sketch, "E1200", {"points": [v(-171.82, -94.05) * mm, v(-171.82, -91.84) * mm, v(-173.6, -90.05) * mm, v(-175.82, -90.05) * mm]});
            skLineSegment(sketch, "E1201", {"start": v(-123.82, -98.05) * mm, "end": v(-115.82, -98.05) * mm});
            skFitSpline(sketch, "E1202", {"points": [v(-183.82, -90.05) * mm, v(-186.03, -90.05) * mm, v(-187.82, -91.84) * mm, v(-187.82, -94.05) * mm]});
            skFitSpline(sketch, "E1203", {"points": [v(-187.82, -94.05) * mm, v(-187.82, -96.26) * mm, v(-186.03, -98.05) * mm, v(-183.82, -98.05) * mm]});
            skLineSegment(sketch, "E1204", {"start": v(-115.82, -90.05) * mm, "end": v(-123.82, -90.05) * mm});
            skFitSpline(sketch, "E1205", {"points": [v(-235.82, -98.05) * mm, v(-233.6, -98.05) * mm, v(-231.82, -96.26) * mm, v(-231.82, -94.05) * mm]});
            skFitSpline(sketch, "E1206", {"points": [v(-231.82, -94.05) * mm, v(-231.82, -91.84) * mm, v(-233.6, -90.05) * mm, v(-235.82, -90.05) * mm]});
            skLineSegment(sketch, "E1207", {"start": v(-183.82, -98.05) * mm, "end": v(-175.82, -98.05) * mm});
            skFitSpline(sketch, "E1208", {"points": [v(-243.82, -90.05) * mm, v(-246.03, -90.05) * mm, v(-247.82, -91.84) * mm, v(-247.82, -94.05) * mm]});
            skFitSpline(sketch, "E1209", {"points": [v(-247.82, -94.05) * mm, v(-247.82, -96.26) * mm, v(-246.03, -98.05) * mm, v(-243.82, -98.05) * mm]});
            skLineSegment(sketch, "E1210", {"start": v(-175.82, -90.05) * mm, "end": v(-183.82, -90.05) * mm});
            skFitSpline(sketch, "E1211", {"points": [v(-303.82, -97.05) * mm, v(-303.81, -99.25) * mm, v(-302.02, -101.04) * mm, v(-299.82, -101.04) * mm]});
            skFitSpline(sketch, "E1212", {"points": [v(-299.82, -101.04) * mm, v(-297.61, -101.04) * mm, v(-295.82, -99.25) * mm, v(-295.82, -97.05) * mm]});
            skLineSegment(sketch, "E1213", {"start": v(-243.82, -98.05) * mm, "end": v(-235.82, -98.05) * mm});
            skFitSpline(sketch, "E1214", {"points": [v(-295.82, -89.05) * mm, v(-295.82, -86.84) * mm, v(-297.61, -85.05) * mm, v(-299.82, -85.05) * mm]});
            skFitSpline(sketch, "E1215", {"points": [v(-299.82, -85.05) * mm, v(-302.02, -85.05) * mm, v(-303.81, -86.84) * mm, v(-303.82, -89.05) * mm]});
            skLineSegment(sketch, "E1216", {"start": v(-235.82, -90.05) * mm, "end": v(-243.82, -90.05) * mm});
            skFitSpline(sketch, "E1217", {"points": [v(-303.82, -137.05) * mm, v(-303.81, -139.25) * mm, v(-302.02, -141.04) * mm, v(-299.82, -141.04) * mm]});
            skFitSpline(sketch, "E1218", {"points": [v(-299.82, -141.04) * mm, v(-297.61, -141.04) * mm, v(-295.82, -139.25) * mm, v(-295.82, -137.05) * mm]});
            skLineSegment(sketch, "E1219", {"start": v(-303.82, -89.05) * mm, "end": v(-303.82, -97.05) * mm});
            skFitSpline(sketch, "E1220", {"points": [v(-295.82, -129.05) * mm, v(-295.82, -126.84) * mm, v(-297.61, -125.05) * mm, v(-299.82, -125.05) * mm]});
            skFitSpline(sketch, "E1221", {"points": [v(-299.82, -125.05) * mm, v(-302.02, -125.05) * mm, v(-303.81, -126.84) * mm, v(-303.82, -129.05) * mm]});
            skLineSegment(sketch, "E1222", {"start": v(-295.82, -97.05) * mm, "end": v(-295.82, -89.05) * mm});
            skFitSpline(sketch, "E1223", {"points": [v(-388.82, -97.05) * mm, v(-388.82, -98.48) * mm, v(-388.05, -99.8) * mm, v(-386.82, -100.51) * mm]});
            skFitSpline(sketch, "E1224", {"points": [v(-386.82, -100.51) * mm, v(-385.58, -101.23) * mm, v(-384.05, -101.23) * mm, v(-382.82, -100.51) * mm]});
            skFitSpline(sketch, "E1225", {"points": [v(-382.82, -100.51) * mm, v(-381.58, -99.8) * mm, v(-380.82, -98.48) * mm, v(-380.82, -97.05) * mm]});
            skLineSegment(sketch, "E1226", {"start": v(-303.82, -129.05) * mm, "end": v(-303.82, -137.05) * mm});
            skFitSpline(sketch, "E1227", {"points": [v(-380.82, -89.05) * mm, v(-380.82, -87.62) * mm, v(-381.58, -86.3) * mm, v(-382.82, -85.58) * mm]});
            skFitSpline(sketch, "E1228", {"points": [v(-382.82, -85.58) * mm, v(-384.05, -84.87) * mm, v(-385.58, -84.87) * mm, v(-386.82, -85.58) * mm]});
            skFitSpline(sketch, "E1229", {"points": [v(-386.82, -85.58) * mm, v(-388.05, -86.3) * mm, v(-388.82, -87.62) * mm, v(-388.82, -89.05) * mm]});
            skLineSegment(sketch, "E1230", {"start": v(-295.82, -137.05) * mm, "end": v(-295.82, -129.05) * mm});
            skFitSpline(sketch, "E1231", {"points": [v(-388.82, -137.05) * mm, v(-388.82, -138.48) * mm, v(-388.05, -139.8) * mm, v(-386.82, -140.51) * mm]});
            skFitSpline(sketch, "E1232", {"points": [v(-386.82, -140.51) * mm, v(-385.58, -141.23) * mm, v(-384.05, -141.23) * mm, v(-382.82, -140.51) * mm]});
            skFitSpline(sketch, "E1233", {"points": [v(-382.82, -140.51) * mm, v(-381.58, -139.8) * mm, v(-380.82, -138.48) * mm, v(-380.82, -137.05) * mm]});
            skLineSegment(sketch, "E1234", {"start": v(-388.82, -89.05) * mm, "end": v(-388.82, -97.05) * mm});
            skFitSpline(sketch, "E1235", {"points": [v(-380.82, -129.05) * mm, v(-380.82, -127.62) * mm, v(-381.58, -126.3) * mm, v(-382.82, -125.58) * mm]});
            skFitSpline(sketch, "E1236", {"points": [v(-382.82, -125.58) * mm, v(-384.05, -124.87) * mm, v(-385.58, -124.87) * mm, v(-386.82, -125.58) * mm]});
            skFitSpline(sketch, "E1237", {"points": [v(-386.82, -125.58) * mm, v(-388.05, -126.3) * mm, v(-388.82, -127.62) * mm, v(-388.82, -129.05) * mm]});
            skLineSegment(sketch, "E1238", {"start": v(-380.82, -97.05) * mm, "end": v(-380.82, -89.05) * mm});
            skFitSpline(sketch, "E1239", {"points": [v(-388.82, -177.05) * mm, v(-388.82, -178.48) * mm, v(-388.05, -179.8) * mm, v(-386.82, -180.51) * mm]});
            skFitSpline(sketch, "E1240", {"points": [v(-386.82, -180.51) * mm, v(-385.58, -181.23) * mm, v(-384.05, -181.23) * mm, v(-382.82, -180.51) * mm]});
            skFitSpline(sketch, "E1241", {"points": [v(-382.82, -180.51) * mm, v(-381.58, -179.8) * mm, v(-380.82, -178.48) * mm, v(-380.82, -177.05) * mm]});
            skLineSegment(sketch, "E1242", {"start": v(-388.82, -129.05) * mm, "end": v(-388.82, -137.05) * mm});
            skFitSpline(sketch, "E1243", {"points": [v(-380.82, -169.05) * mm, v(-380.82, -167.62) * mm, v(-381.58, -166.3) * mm, v(-382.82, -165.58) * mm]});
            skFitSpline(sketch, "E1244", {"points": [v(-382.82, -165.58) * mm, v(-384.05, -164.87) * mm, v(-385.58, -164.87) * mm, v(-386.82, -165.58) * mm]});
            skFitSpline(sketch, "E1245", {"points": [v(-386.82, -165.58) * mm, v(-388.05, -166.3) * mm, v(-388.82, -167.62) * mm, v(-388.82, -169.05) * mm]});
            skFitSpline(sketch, "E1246", {"points": [v(-318.48, -86.85) * mm, v(-318.48, -86.38) * mm, v(-318.73, -85.95) * mm, v(-319.13, -85.72) * mm]});
            skFitSpline(sketch, "E1247", {"points": [v(-319.13, -85.72) * mm, v(-319.54, -85.49) * mm, v(-320.03, -85.49) * mm, v(-320.43, -85.72) * mm]});
            skFitSpline(sketch, "E1248", {"points": [v(-320.43, -85.72) * mm, v(-320.84, -85.95) * mm, v(-321.08, -86.38) * mm, v(-321.08, -86.85) * mm]});
            skFitSpline(sketch, "E1249", {"points": [v(-321.08, -86.85) * mm, v(-321.08, -87.31) * mm, v(-320.84, -87.74) * mm, v(-320.43, -87.97) * mm]});
            skFitSpline(sketch, "E1250", {"points": [v(-320.43, -87.97) * mm, v(-320.03, -88.2) * mm, v(-319.54, -88.2) * mm, v(-319.13, -87.97) * mm]});
            skFitSpline(sketch, "E1251", {"points": [v(-319.13, -87.97) * mm, v(-318.73, -87.74) * mm, v(-318.48, -87.31) * mm, v(-318.48, -86.85) * mm]});
            skLineSegment(sketch, "E1252", {"start": v(-380.82, -137.05) * mm, "end": v(-380.82, -129.05) * mm});
            skFitSpline(sketch, "E1253", {"points": [v(-318.5, -170.05) * mm, v(-318.5, -169.58) * mm, v(-318.75, -169.15) * mm, v(-319.15, -168.92) * mm]});
            skFitSpline(sketch, "E1254", {"points": [v(-319.15, -168.92) * mm, v(-319.55, -168.69) * mm, v(-320.05, -168.69) * mm, v(-320.45, -168.92) * mm]});
            skFitSpline(sketch, "E1255", {"points": [v(-320.45, -168.92) * mm, v(-320.85, -169.15) * mm, v(-321.1, -169.58) * mm, v(-321.1, -170.05) * mm]});
            skFitSpline(sketch, "E1256", {"points": [v(-321.1, -170.05) * mm, v(-321.1, -170.51) * mm, v(-320.85, -170.94) * mm, v(-320.45, -171.17) * mm]});
            skFitSpline(sketch, "E1257", {"points": [v(-320.45, -171.17) * mm, v(-320.05, -171.4) * mm, v(-319.55, -171.4) * mm, v(-319.15, -171.17) * mm]});
            skFitSpline(sketch, "E1258", {"points": [v(-319.15, -171.17) * mm, v(-318.75, -170.94) * mm, v(-318.5, -170.51) * mm, v(-318.5, -170.05) * mm]});
            skLineSegment(sketch, "E1259", {"start": v(-388.82, -169.05) * mm, "end": v(-388.82, -177.05) * mm});
            skFitSpline(sketch, "E1260", {"points": [v(-366.68, -93.05) * mm, v(-366.68, -92.58) * mm, v(-366.93, -92.15) * mm, v(-367.33, -91.92) * mm]});
            skFitSpline(sketch, "E1261", {"points": [v(-367.33, -91.92) * mm, v(-367.73, -91.69) * mm, v(-368.23, -91.69) * mm, v(-368.63, -91.92) * mm]});
            skFitSpline(sketch, "E1262", {"points": [v(-368.63, -91.92) * mm, v(-369.03, -92.15) * mm, v(-369.28, -92.58) * mm, v(-369.28, -93.05) * mm]});
            skFitSpline(sketch, "E1263", {"points": [v(-369.28, -93.05) * mm, v(-369.28, -93.51) * mm, v(-369.03, -93.94) * mm, v(-368.63, -94.17) * mm]});
            skFitSpline(sketch, "E1264", {"points": [v(-368.63, -94.17) * mm, v(-368.23, -94.4) * mm, v(-367.73, -94.4) * mm, v(-367.33, -94.17) * mm]});
            skFitSpline(sketch, "E1265", {"points": [v(-367.33, -94.17) * mm, v(-366.93, -93.94) * mm, v(-366.68, -93.51) * mm, v(-366.68, -93.05) * mm]});
            skLineSegment(sketch, "E1266", {"start": v(-380.82, -177.05) * mm, "end": v(-380.82, -169.05) * mm});
            skFitSpline(sketch, "E1267", {"points": [v(-366.7, -167.55) * mm, v(-366.7, -167.08) * mm, v(-366.95, -166.65) * mm, v(-367.35, -166.42) * mm]});
            skFitSpline(sketch, "E1268", {"points": [v(-367.35, -166.42) * mm, v(-367.75, -166.19) * mm, v(-368.25, -166.19) * mm, v(-368.65, -166.42) * mm]});
            skFitSpline(sketch, "E1269", {"points": [v(-368.65, -166.42) * mm, v(-369.05, -166.65) * mm, v(-369.3, -167.08) * mm, v(-369.3, -167.55) * mm]});
            skFitSpline(sketch, "E1270", {"points": [v(-369.3, -167.55) * mm, v(-369.3, -168.01) * mm, v(-369.05, -168.44) * mm, v(-368.65, -168.67) * mm]});
            skFitSpline(sketch, "E1271", {"points": [v(-368.65, -168.67) * mm, v(-368.25, -168.9) * mm, v(-367.75, -168.9) * mm, v(-367.35, -168.67) * mm]});
            skFitSpline(sketch, "E1272", {"points": [v(-367.35, -168.67) * mm, v(-366.95, -168.44) * mm, v(-366.7, -168.01) * mm, v(-366.7, -167.55) * mm]});
            skFitSpline(sketch, "E1273", {"points": [v(-221.98, -174.76) * mm, v(-222.16, -174.76) * mm, v(-222.32, -174.86) * mm, v(-222.41, -175.01) * mm]});
            skFitSpline(sketch, "E1274", {"points": [v(-223.1, -174.33) * mm, v(-223.28, -174.43) * mm, v(-223.37, -174.64) * mm, v(-223.34, -174.85) * mm]});
            skFitSpline(sketch, "E1275", {"points": [v(-223.34, -174.85) * mm, v(-223.3, -175.05) * mm, v(-223.14, -175.22) * mm, v(-222.93, -175.25) * mm]});
            skFitSpline(sketch, "E1276", {"points": [v(-222.93, -175.25) * mm, v(-222.72, -175.29) * mm, v(-222.52, -175.2) * mm, v(-222.41, -175.01) * mm]});
            skFitSpline(sketch, "E1277", {"points": [v(-223.1, -174.33) * mm, v(-222.94, -174.24) * mm, v(-222.84, -174.07) * mm, v(-222.84, -173.9) * mm]});
            skFitSpline(sketch, "E1278", {"points": [v(-222.84, -172.26) * mm, v(-222.84, -172.13) * mm, v(-222.9, -172) * mm, v(-223, -171.9) * mm]});
            skFitSpline(sketch, "E1279", {"points": [v(-223, -171.9) * mm, v(-223.08, -171.81) * mm, v(-223.21, -171.76) * mm, v(-223.34, -171.76) * mm]});
            skFitSpline(sketch, "E1280", {"points": [v(-228.34, -171.76) * mm, v(-228.48, -171.76) * mm, v(-228.6, -171.81) * mm, v(-228.7, -171.9) * mm]});
            skFitSpline(sketch, "E1281", {"points": [v(-228.7, -171.9) * mm, v(-228.8, -172) * mm, v(-228.84, -172.13) * mm, v(-228.84, -172.26) * mm]});
            skFitSpline(sketch, "E1282", {"points": [v(-228.84, -173.9) * mm, v(-228.84, -174.07) * mm, v(-228.75, -174.24) * mm, v(-228.6, -174.33) * mm]});
            skFitSpline(sketch, "E1283", {"points": [v(-229.28, -175.01) * mm, v(-229.17, -175.2) * mm, v(-228.96, -175.29) * mm, v(-228.76, -175.25) * mm]});
            skFitSpline(sketch, "E1284", {"points": [v(-228.76, -175.25) * mm, v(-228.55, -175.22) * mm, v(-228.39, -175.05) * mm, v(-228.35, -174.85) * mm]});
            skFitSpline(sketch, "E1285", {"points": [v(-228.35, -174.85) * mm, v(-228.32, -174.64) * mm, v(-228.41, -174.43) * mm, v(-228.6, -174.33) * mm]});
            skFitSpline(sketch, "E1286", {"points": [v(-229.28, -175.01) * mm, v(-229.37, -174.86) * mm, v(-229.53, -174.76) * mm, v(-229.71, -174.76) * mm]});
            skLineSegment(sketch, "E1287", {"start": v(-222.84, -173.9) * mm, "end": v(-222.84, -172.26) * mm});
            skFitSpline(sketch, "E1288", {"points": [v(-234.24, -188.17) * mm, v(-234.24, -189.1) * mm, v(-233.6, -189.9) * mm, v(-232.7, -190.12) * mm]});
            skLineSegment(sketch, "E1289", {"start": v(-223.34, -171.76) * mm, "end": v(-228.34, -171.76) * mm});
            skFitSpline(sketch, "E1290", {"points": [v(-204.82, -196.58) * mm, v(-202.74, -197.06) * mm, v(-200.56, -196.57) * mm, v(-198.89, -195.24) * mm]});
            skFitSpline(sketch, "E1291", {"points": [v(-198.89, -195.24) * mm, v(-197.22, -193.91) * mm, v(-196.24, -191.9) * mm, v(-196.24, -189.76) * mm]});
            skLineSegment(sketch, "E1292", {"start": v(-228.84, -172.26) * mm, "end": v(-228.84, -173.9) * mm});
            skFitSpline(sketch, "E1293", {"points": [v(-200.78, -174.76) * mm, v(-200.96, -174.76) * mm, v(-201.12, -174.86) * mm, v(-201.21, -175.01) * mm]});
            skFitSpline(sketch, "E1294", {"points": [v(-201.9, -174.33) * mm, v(-202.08, -174.43) * mm, v(-202.17, -174.64) * mm, v(-202.14, -174.85) * mm]});
            skFitSpline(sketch, "E1295", {"points": [v(-202.14, -174.85) * mm, v(-202.1, -175.05) * mm, v(-201.94, -175.22) * mm, v(-201.73, -175.25) * mm]});
            skFitSpline(sketch, "E1296", {"points": [v(-201.73, -175.25) * mm, v(-201.52, -175.29) * mm, v(-201.32, -175.2) * mm, v(-201.21, -175.01) * mm]});
            skFitSpline(sketch, "E1297", {"points": [v(-201.9, -174.33) * mm, v(-201.74, -174.24) * mm, v(-201.64, -174.07) * mm, v(-201.64, -173.9) * mm]});
            skLineSegment(sketch, "E1298", {"start": v(-229.71, -174.76) * mm, "end": v(-234.24, -174.76) * mm});
            skLineSegment(sketch, "E1299", {"start": v(-234.24, -174.76) * mm, "end": v(-234.24, -188.17) * mm});
            skFitSpline(sketch, "E1300", {"points": [v(-201.64, -172.26) * mm, v(-201.64, -172.13) * mm, v(-201.7, -172) * mm, v(-201.8, -171.9) * mm]});
            skFitSpline(sketch, "E1301", {"points": [v(-201.8, -171.9) * mm, v(-201.88, -171.81) * mm, v(-202.01, -171.76) * mm, v(-202.14, -171.76) * mm]});
            skLineSegment(sketch, "E1302", {"start": v(-232.7, -190.12) * mm, "end": v(-204.82, -196.58) * mm});
            skFitSpline(sketch, "E1303", {"points": [v(-207.14, -171.76) * mm, v(-207.42, -171.76) * mm, v(-207.64, -171.98) * mm, v(-207.64, -172.26) * mm]});
            skLineSegment(sketch, "E1304", {"start": v(-196.24, -189.76) * mm, "end": v(-196.24, -174.76) * mm});
            skLineSegment(sketch, "E1305", {"start": v(-196.24, -174.76) * mm, "end": v(-200.78, -174.76) * mm});
            skFitSpline(sketch, "E1306", {"points": [v(-207.64, -173.9) * mm, v(-207.64, -174.07) * mm, v(-207.55, -174.24) * mm, v(-207.4, -174.33) * mm]});
            skFitSpline(sketch, "E1307", {"points": [v(-208.08, -175.01) * mm, v(-207.97, -175.2) * mm, v(-207.76, -175.29) * mm, v(-207.56, -175.25) * mm]});
            skFitSpline(sketch, "E1308", {"points": [v(-207.56, -175.25) * mm, v(-207.35, -175.22) * mm, v(-207.19, -175.05) * mm, v(-207.15, -174.85) * mm]});
            skFitSpline(sketch, "E1309", {"points": [v(-207.15, -174.85) * mm, v(-207.12, -174.64) * mm, v(-207.21, -174.43) * mm, v(-207.4, -174.33) * mm]});
            skFitSpline(sketch, "E1310", {"points": [v(-208.08, -175.01) * mm, v(-208.17, -174.86) * mm, v(-208.33, -174.76) * mm, v(-208.51, -174.76) * mm]});
            skLineSegment(sketch, "E1311", {"start": v(-201.64, -173.9) * mm, "end": v(-201.64, -172.26) * mm});
            skFitSpline(sketch, "E1312", {"points": [v(-199.24, -189.76) * mm, v(-199.24, -188.33) * mm, v(-200, -187) * mm, v(-201.24, -186.3) * mm]});
            skFitSpline(sketch, "E1313", {"points": [v(-201.24, -186.3) * mm, v(-202.48, -185.57) * mm, v(-204, -185.57) * mm, v(-205.25, -186.3) * mm]});
            skFitSpline(sketch, "E1314", {"points": [v(-205.25, -186.3) * mm, v(-206.48, -187) * mm, v(-207.25, -188.33) * mm, v(-207.24, -189.76) * mm]});
            skFitSpline(sketch, "E1315", {"points": [v(-207.24, -189.76) * mm, v(-207.25, -191.2) * mm, v(-206.48, -192.52) * mm, v(-205.25, -193.23) * mm]});
            skFitSpline(sketch, "E1316", {"points": [v(-205.25, -193.23) * mm, v(-204, -193.95) * mm, v(-202.48, -193.95) * mm, v(-201.24, -193.23) * mm]});
            skFitSpline(sketch, "E1317", {"points": [v(-201.24, -193.23) * mm, v(-200, -192.52) * mm, v(-199.24, -191.2) * mm, v(-199.24, -189.76) * mm]});
            skLineSegment(sketch, "E1318", {"start": v(-202.14, -171.76) * mm, "end": v(-207.14, -171.76) * mm});
            skFitSpline(sketch, "E1319", {"points": [v(-174.3, 171.9) * mm, v(-174.49, 171.9) * mm, v(-174.65, 171.8) * mm, v(-174.74, 171.64) * mm]});
            skFitSpline(sketch, "E1320", {"points": [v(-175.43, 172.32) * mm, v(-175.6, 172.22) * mm, v(-175.7, 172.01) * mm, v(-175.67, 171.8) * mm]});
            skFitSpline(sketch, "E1321", {"points": [v(-175.67, 171.8) * mm, v(-175.63, 171.6) * mm, v(-175.47, 171.43) * mm, v(-175.26, 171.4) * mm]});
            skFitSpline(sketch, "E1322", {"points": [v(-175.26, 171.4) * mm, v(-175.06, 171.36) * mm, v(-174.85, 171.46) * mm, v(-174.74, 171.64) * mm]});
            skFitSpline(sketch, "E1323", {"points": [v(-175.43, 172.32) * mm, v(-175.27, 172.41) * mm, v(-175.18, 172.58) * mm, v(-175.18, 172.76) * mm]});
            skLineSegment(sketch, "E1324", {"start": v(-207.64, -172.26) * mm, "end": v(-207.64, -173.9) * mm});
            skFitSpline(sketch, "E1325", {"points": [v(-175.18, 174.4) * mm, v(-175.18, 174.52) * mm, v(-175.23, 174.65) * mm, v(-175.32, 174.74) * mm]});
            skFitSpline(sketch, "E1326", {"points": [v(-175.32, 174.74) * mm, v(-175.42, 174.84) * mm, v(-175.54, 174.9) * mm, v(-175.68, 174.9) * mm]});
            skLineSegment(sketch, "E1327", {"start": v(-208.51, -174.76) * mm, "end": v(-213.64, -174.76) * mm});
            skLineSegment(sketch, "E1328", {"start": v(-213.64, -174.76) * mm, "end": v(-213.64, -177.76) * mm});
            skLineSegment(sketch, "E1329", {"start": v(-213.64, -177.76) * mm, "end": v(-212.37, -177.76) * mm});
            skLineSegment(sketch, "E1330", {"start": v(-212.37, -177.76) * mm, "end": v(-212.37, -181.76) * mm});
            skLineSegment(sketch, "E1331", {"start": v(-212.37, -181.76) * mm, "end": v(-213.64, -181.76) * mm});
            skLineSegment(sketch, "E1332", {"start": v(-213.64, -181.76) * mm, "end": v(-213.64, -184.76) * mm});
            skLineSegment(sketch, "E1333", {"start": v(-213.64, -184.76) * mm, "end": v(-216.84, -184.76) * mm});
            skLineSegment(sketch, "E1334", {"start": v(-216.84, -184.76) * mm, "end": v(-216.84, -181.76) * mm});
            skLineSegment(sketch, "E1335", {"start": v(-216.84, -181.76) * mm, "end": v(-218.12, -181.76) * mm});
            skLineSegment(sketch, "E1336", {"start": v(-218.12, -181.76) * mm, "end": v(-218.12, -177.76) * mm});
            skLineSegment(sketch, "E1337", {"start": v(-218.12, -177.76) * mm, "end": v(-216.84, -177.76) * mm});
            skLineSegment(sketch, "E1338", {"start": v(-216.84, -177.76) * mm, "end": v(-216.84, -174.76) * mm});
            skLineSegment(sketch, "E1339", {"start": v(-216.84, -174.76) * mm, "end": v(-221.98, -174.76) * mm});
            skFitSpline(sketch, "E1340", {"points": [v(-180.68, 174.9) * mm, v(-180.8, 174.9) * mm, v(-180.94, 174.84) * mm, v(-181.03, 174.74) * mm]});
            skFitSpline(sketch, "E1341", {"points": [v(-181.03, 174.74) * mm, v(-181.12, 174.65) * mm, v(-181.18, 174.52) * mm, v(-181.18, 174.4) * mm]});
            skFitSpline(sketch, "E1342", {"points": [v(-181.18, 172.76) * mm, v(-181.18, 172.58) * mm, v(-181.08, 172.41) * mm, v(-180.93, 172.32) * mm]});
            skFitSpline(sketch, "E1343", {"points": [v(-181.6, 171.64) * mm, v(-181.5, 171.46) * mm, v(-181.3, 171.36) * mm, v(-181.09, 171.4) * mm]});
            skFitSpline(sketch, "E1344", {"points": [v(-181.09, 171.4) * mm, v(-180.88, 171.43) * mm, v(-180.72, 171.6) * mm, v(-180.68, 171.8) * mm]});
            skFitSpline(sketch, "E1345", {"points": [v(-180.68, 171.8) * mm, v(-180.65, 172.01) * mm, v(-180.74, 172.22) * mm, v(-180.93, 172.32) * mm]});
            skFitSpline(sketch, "E1346", {"points": [v(-181.6, 171.64) * mm, v(-181.7, 171.8) * mm, v(-181.86, 171.9) * mm, v(-182.04, 171.9) * mm]});
            skLineSegment(sketch, "E1347", {"start": v(-175.18, 172.76) * mm, "end": v(-175.18, 174.4) * mm});
            skFitSpline(sketch, "E1348", {"points": [v(-186.58, 158.48) * mm, v(-186.58, 157.55) * mm, v(-185.93, 156.74) * mm, v(-185.03, 156.53) * mm]});
            skLineSegment(sketch, "E1349", {"start": v(-175.68, 174.9) * mm, "end": v(-180.68, 174.9) * mm});
            skFitSpline(sketch, "E1350", {"points": [v(-157.15, 150.07) * mm, v(-155.07, 149.6) * mm, v(-152.89, 150.08) * mm, v(-151.22, 151.41) * mm]});
            skFitSpline(sketch, "E1351", {"points": [v(-151.22, 151.41) * mm, v(-149.55, 152.74) * mm, v(-148.58, 154.76) * mm, v(-148.58, 156.9) * mm]});
            skLineSegment(sketch, "E1352", {"start": v(-181.18, 174.4) * mm, "end": v(-181.18, 172.76) * mm});
            skFitSpline(sketch, "E1353", {"points": [v(-153.1, 171.9) * mm, v(-153.29, 171.9) * mm, v(-153.45, 171.8) * mm, v(-153.54, 171.64) * mm]});
            skFitSpline(sketch, "E1354", {"points": [v(-154.23, 172.32) * mm, v(-154.4, 172.22) * mm, v(-154.5, 172.01) * mm, v(-154.47, 171.8) * mm]});
            skFitSpline(sketch, "E1355", {"points": [v(-154.47, 171.8) * mm, v(-154.43, 171.6) * mm, v(-154.27, 171.43) * mm, v(-154.06, 171.4) * mm]});
            skFitSpline(sketch, "E1356", {"points": [v(-154.06, 171.4) * mm, v(-153.86, 171.36) * mm, v(-153.65, 171.46) * mm, v(-153.54, 171.64) * mm]});
            skFitSpline(sketch, "E1357", {"points": [v(-154.23, 172.32) * mm, v(-154.07, 172.41) * mm, v(-153.98, 172.58) * mm, v(-153.98, 172.76) * mm]});
            skLineSegment(sketch, "E1358", {"start": v(-182.04, 171.9) * mm, "end": v(-186.58, 171.9) * mm});
            skLineSegment(sketch, "E1359", {"start": v(-186.58, 171.9) * mm, "end": v(-186.58, 158.48) * mm});
            skFitSpline(sketch, "E1360", {"points": [v(-153.98, 174.4) * mm, v(-153.98, 174.52) * mm, v(-154.03, 174.65) * mm, v(-154.12, 174.74) * mm]});
            skFitSpline(sketch, "E1361", {"points": [v(-154.12, 174.74) * mm, v(-154.22, 174.84) * mm, v(-154.34, 174.9) * mm, v(-154.48, 174.9) * mm]});
            skLineSegment(sketch, "E1362", {"start": v(-185.03, 156.53) * mm, "end": v(-157.15, 150.07) * mm});
            skFitSpline(sketch, "E1363", {"points": [v(-159.48, 174.9) * mm, v(-159.75, 174.9) * mm, v(-159.98, 174.67) * mm, v(-159.98, 174.4) * mm]});
            skLineSegment(sketch, "E1364", {"start": v(-148.58, 156.9) * mm, "end": v(-148.58, 171.9) * mm});
            skLineSegment(sketch, "E1365", {"start": v(-148.58, 171.9) * mm, "end": v(-153.1, 171.9) * mm});
            skFitSpline(sketch, "E1366", {"points": [v(-159.98, 172.76) * mm, v(-159.98, 172.58) * mm, v(-159.88, 172.41) * mm, v(-159.73, 172.32) * mm]});
            skFitSpline(sketch, "E1367", {"points": [v(-160.4, 171.64) * mm, v(-160.3, 171.46) * mm, v(-160.1, 171.36) * mm, v(-159.89, 171.4) * mm]});
            skFitSpline(sketch, "E1368", {"points": [v(-159.89, 171.4) * mm, v(-159.68, 171.43) * mm, v(-159.52, 171.6) * mm, v(-159.48, 171.8) * mm]});
            skFitSpline(sketch, "E1369", {"points": [v(-159.48, 171.8) * mm, v(-159.45, 172.01) * mm, v(-159.54, 172.22) * mm, v(-159.73, 172.32) * mm]});
            skFitSpline(sketch, "E1370", {"points": [v(-160.4, 171.64) * mm, v(-160.5, 171.8) * mm, v(-160.66, 171.9) * mm, v(-160.84, 171.9) * mm]});
            skLineSegment(sketch, "E1371", {"start": v(-153.98, 172.76) * mm, "end": v(-153.98, 174.4) * mm});
            skFitSpline(sketch, "E1372", {"points": [v(-151.57, 156.9) * mm, v(-151.57, 158.32) * mm, v(-152.33, 159.64) * mm, v(-153.57, 160.36) * mm]});
            skFitSpline(sketch, "E1373", {"points": [v(-153.57, 160.36) * mm, v(-154.81, 161.08) * mm, v(-156.34, 161.08) * mm, v(-157.58, 160.36) * mm]});
            skFitSpline(sketch, "E1374", {"points": [v(-157.58, 160.36) * mm, v(-158.81, 159.64) * mm, v(-159.58, 158.32) * mm, v(-159.57, 156.9) * mm]});
            skFitSpline(sketch, "E1375", {"points": [v(-159.57, 156.9) * mm, v(-159.58, 155.46) * mm, v(-158.81, 154.14) * mm, v(-157.58, 153.42) * mm]});
            skFitSpline(sketch, "E1376", {"points": [v(-157.58, 153.42) * mm, v(-156.34, 152.7) * mm, v(-154.81, 152.7) * mm, v(-153.57, 153.42) * mm]});
            skFitSpline(sketch, "E1377", {"points": [v(-153.57, 153.42) * mm, v(-152.33, 154.14) * mm, v(-151.57, 155.46) * mm, v(-151.57, 156.9) * mm]});
            skLineSegment(sketch, "E1378", {"start": v(-154.48, 174.9) * mm, "end": v(-159.48, 174.9) * mm});
            skLineSegment(sketch, "E1379", {"start": v(-159.98, 174.4) * mm, "end": v(-159.98, 172.76) * mm});
            skFitSpline(sketch, "E1380", {"points": [v(61.75, -151.03) * mm, v(61.08, -149.85) * mm, v(59.7, -149.28) * mm, v(58.38, -149.63) * mm]});
            skFitSpline(sketch, "E1381", {"points": [v(58.38, -149.63) * mm, v(57.07, -149.98) * mm, v(56.16, -151.17) * mm, v(56.16, -152.53) * mm]});
            skLineSegment(sketch, "E1382", {"start": v(-160.84, 171.9) * mm, "end": v(-165.98, 171.9) * mm});
            skLineSegment(sketch, "E1383", {"start": v(-165.98, 171.9) * mm, "end": v(-165.98, 168.9) * mm});
            skLineSegment(sketch, "E1384", {"start": v(-165.98, 168.9) * mm, "end": v(-164.7, 168.9) * mm});
            skLineSegment(sketch, "E1385", {"start": v(-164.7, 168.9) * mm, "end": v(-164.7, 164.9) * mm});
            skLineSegment(sketch, "E1386", {"start": v(-164.7, 164.9) * mm, "end": v(-165.98, 164.9) * mm});
            skLineSegment(sketch, "E1387", {"start": v(-165.98, 164.9) * mm, "end": v(-165.98, 161.9) * mm});
            skLineSegment(sketch, "E1388", {"start": v(-165.98, 161.9) * mm, "end": v(-169.18, 161.9) * mm});
            skLineSegment(sketch, "E1389", {"start": v(-169.18, 161.9) * mm, "end": v(-169.18, 164.9) * mm});
            skLineSegment(sketch, "E1390", {"start": v(-169.18, 164.9) * mm, "end": v(-170.45, 164.9) * mm});
            skLineSegment(sketch, "E1391", {"start": v(-170.45, 164.9) * mm, "end": v(-170.45, 168.9) * mm});
            skLineSegment(sketch, "E1392", {"start": v(-170.45, 168.9) * mm, "end": v(-169.18, 168.9) * mm});
            skLineSegment(sketch, "E1393", {"start": v(-169.18, 168.9) * mm, "end": v(-169.18, 171.9) * mm});
            skLineSegment(sketch, "E1394", {"start": v(-169.18, 171.9) * mm, "end": v(-174.3, 171.9) * mm});
            skFitSpline(sketch, "E1395", {"points": [v(56.16, -176.26) * mm, v(56.16, -177.91) * mm, v(57.5, -179.26) * mm, v(59.16, -179.26) * mm]});
            skFitSpline(sketch, "E1396", {"points": [v(72.86, -179.26) * mm, v(73.93, -179.26) * mm, v(74.92, -178.69) * mm, v(75.46, -177.76) * mm]});
            skFitSpline(sketch, "E1397", {"points": [v(75.46, -177.76) * mm, v(76, -176.83) * mm, v(76, -175.69) * mm, v(75.46, -174.76) * mm]});
            skLineSegment(sketch, "E1398", {"start": v(56.16, -176.26) * mm, "end": v(56.16, -152.53) * mm});
            skFitSpline(sketch, "E1399", {"points": [v(56.16, 132.72) * mm, v(56.16, 131.36) * mm, v(57.07, 130.18) * mm, v(58.38, 129.82) * mm]});
            skFitSpline(sketch, "E1400", {"points": [v(58.38, 129.82) * mm, v(59.7, 129.47) * mm, v(61.08, 130.05) * mm, v(61.75, 131.22) * mm]});
            skLineSegment(sketch, "E1401", {"start": v(59.16, -179.26) * mm, "end": v(72.86, -179.26) * mm});
            skFitSpline(sketch, "E1402", {"points": [v(59.16, 159.45) * mm, v(57.5, 159.45) * mm, v(56.16, 158.1) * mm, v(56.16, 156.45) * mm]});
            skLineSegment(sketch, "E1403", {"start": v(61.75, -151.03) * mm, "end": v(75.46, -174.76) * mm});
            skFitSpline(sketch, "E1404", {"points": [v(75.46, 154.95) * mm, v(76, 155.88) * mm, v(76, 157.02) * mm, v(75.46, 157.95) * mm]});
            skFitSpline(sketch, "E1405", {"points": [v(75.46, 157.95) * mm, v(74.92, 158.88) * mm, v(73.93, 159.45) * mm, v(72.86, 159.45) * mm]});
            skFitSpline(sketch, "E1406", {"points": [v(53.42, -31.16) * mm, v(53.42, -30.59) * mm, v(53.12, -30.06) * mm, v(52.62, -29.77) * mm]});
            skFitSpline(sketch, "E1407", {"points": [v(52.62, -29.77) * mm, v(52.12, -29.48) * mm, v(51.51, -29.48) * mm, v(51.02, -29.77) * mm]});
            skFitSpline(sketch, "E1408", {"points": [v(51.02, -29.77) * mm, v(50.52, -30.06) * mm, v(50.22, -30.59) * mm, v(50.22, -31.16) * mm]});
            skFitSpline(sketch, "E1409", {"points": [v(50.22, -31.16) * mm, v(50.21, -31.73) * mm, v(50.52, -32.26) * mm, v(51.02, -32.55) * mm]});
            skFitSpline(sketch, "E1410", {"points": [v(51.02, -32.55) * mm, v(51.51, -32.84) * mm, v(52.12, -32.84) * mm, v(52.62, -32.55) * mm]});
            skFitSpline(sketch, "E1411", {"points": [v(52.62, -32.55) * mm, v(53.12, -32.26) * mm, v(53.42, -31.73) * mm, v(53.42, -31.16) * mm]});
            skLineSegment(sketch, "E1412", {"start": v(56.16, 156.45) * mm, "end": v(56.16, 132.72) * mm});
            skFitSpline(sketch, "E1413", {"points": [v(53.42, 11.34) * mm, v(53.42, 11.92) * mm, v(53.12, 12.45) * mm, v(52.62, 12.73) * mm]});
            skFitSpline(sketch, "E1414", {"points": [v(52.62, 12.73) * mm, v(52.12, 13.02) * mm, v(51.51, 13.02) * mm, v(51.02, 12.73) * mm]});
            skFitSpline(sketch, "E1415", {"points": [v(51.02, 12.73) * mm, v(50.52, 12.45) * mm, v(50.22, 11.92) * mm, v(50.22, 11.34) * mm]});
            skFitSpline(sketch, "E1416", {"points": [v(50.22, 11.34) * mm, v(50.21, 10.77) * mm, v(50.52, 10.24) * mm, v(51.02, 9.95) * mm]});
            skFitSpline(sketch, "E1417", {"points": [v(51.02, 9.95) * mm, v(51.51, 9.67) * mm, v(52.12, 9.67) * mm, v(52.62, 9.95) * mm]});
            skFitSpline(sketch, "E1418", {"points": [v(52.62, 9.95) * mm, v(53.12, 10.24) * mm, v(53.42, 10.77) * mm, v(53.42, 11.34) * mm]});
            skLineSegment(sketch, "E1419", {"start": v(59.16, 159.45) * mm, "end": v(72.86, 159.45) * mm});
            skFitSpline(sketch, "E1420", {"points": [v(53.42, 53.85) * mm, v(53.42, 54.42) * mm, v(53.12, 54.95) * mm, v(52.62, 55.24) * mm]});
            skFitSpline(sketch, "E1421", {"points": [v(52.62, 55.24) * mm, v(52.12, 55.53) * mm, v(51.51, 55.53) * mm, v(51.02, 55.24) * mm]});
            skFitSpline(sketch, "E1422", {"points": [v(51.02, 55.24) * mm, v(50.52, 54.95) * mm, v(50.22, 54.42) * mm, v(50.22, 53.85) * mm]});
            skFitSpline(sketch, "E1423", {"points": [v(50.22, 53.85) * mm, v(50.21, 53.27) * mm, v(50.52, 52.74) * mm, v(51.02, 52.46) * mm]});
            skFitSpline(sketch, "E1424", {"points": [v(51.02, 52.46) * mm, v(51.51, 52.17) * mm, v(52.12, 52.17) * mm, v(52.62, 52.46) * mm]});
            skFitSpline(sketch, "E1425", {"points": [v(52.62, 52.46) * mm, v(53.12, 52.74) * mm, v(53.42, 53.27) * mm, v(53.42, 53.85) * mm]});
            skLineSegment(sketch, "E1426", {"start": v(61.75, 131.22) * mm, "end": v(75.46, 154.95) * mm});
            skFitSpline(sketch, "E1427", {"points": [v(53.42, -31.16) * mm, v(53.42, -30.59) * mm, v(53.12, -30.06) * mm, v(52.62, -29.77) * mm]});
            skFitSpline(sketch, "E1428", {"points": [v(52.62, -29.77) * mm, v(52.12, -29.48) * mm, v(51.51, -29.48) * mm, v(51.02, -29.77) * mm]});
            skFitSpline(sketch, "E1429", {"points": [v(51.02, -29.77) * mm, v(50.52, -30.06) * mm, v(50.22, -30.59) * mm, v(50.22, -31.16) * mm]});
            skFitSpline(sketch, "E1430", {"points": [v(50.22, -31.16) * mm, v(50.21, -31.73) * mm, v(50.52, -32.26) * mm, v(51.02, -32.55) * mm]});
            skFitSpline(sketch, "E1431", {"points": [v(51.02, -32.55) * mm, v(51.51, -32.84) * mm, v(52.12, -32.84) * mm, v(52.62, -32.55) * mm]});
            skFitSpline(sketch, "E1432", {"points": [v(52.62, -32.55) * mm, v(53.12, -32.26) * mm, v(53.42, -31.73) * mm, v(53.42, -31.16) * mm]});
            skFitSpline(sketch, "E1433", {"points": [v(53.42, -31.16) * mm, v(53.42, -30.59) * mm, v(53.12, -30.06) * mm, v(52.62, -29.77) * mm]});
            skFitSpline(sketch, "E1434", {"points": [v(52.62, -29.77) * mm, v(52.12, -29.48) * mm, v(51.51, -29.48) * mm, v(51.02, -29.77) * mm]});
            skFitSpline(sketch, "E1435", {"points": [v(51.02, -29.77) * mm, v(50.52, -30.06) * mm, v(50.22, -30.59) * mm, v(50.22, -31.16) * mm]});
            skFitSpline(sketch, "E1436", {"points": [v(50.22, -31.16) * mm, v(50.21, -31.73) * mm, v(50.52, -32.26) * mm, v(51.02, -32.55) * mm]});
            skFitSpline(sketch, "E1437", {"points": [v(51.02, -32.55) * mm, v(51.51, -32.84) * mm, v(52.12, -32.84) * mm, v(52.62, -32.55) * mm]});
            skFitSpline(sketch, "E1438", {"points": [v(52.62, -32.55) * mm, v(53.12, -32.26) * mm, v(53.42, -31.73) * mm, v(53.42, -31.16) * mm]});
            skFitSpline(sketch, "E1439", {"points": [v(53.42, -76.18) * mm, v(53.42, -75.61) * mm, v(53.12, -75.08) * mm, v(52.62, -74.8) * mm]});
            skFitSpline(sketch, "E1440", {"points": [v(52.62, -74.8) * mm, v(52.12, -74.5) * mm, v(51.51, -74.5) * mm, v(51.02, -74.8) * mm]});
            skFitSpline(sketch, "E1441", {"points": [v(51.02, -74.8) * mm, v(50.52, -75.08) * mm, v(50.22, -75.61) * mm, v(50.22, -76.18) * mm]});
            skFitSpline(sketch, "E1442", {"points": [v(50.22, -76.18) * mm, v(50.21, -76.76) * mm, v(50.52, -77.29) * mm, v(51.02, -77.57) * mm]});
            skFitSpline(sketch, "E1443", {"points": [v(51.02, -77.57) * mm, v(51.51, -77.86) * mm, v(52.12, -77.86) * mm, v(52.62, -77.57) * mm]});
            skFitSpline(sketch, "E1444", {"points": [v(52.62, -77.57) * mm, v(53.12, -77.29) * mm, v(53.42, -76.76) * mm, v(53.42, -76.18) * mm]});
            skFitSpline(sketch, "E1445", {"points": [v(371.03, -82.13) * mm, v(370.85, -82.13) * mm, v(370.69, -82.22) * mm, v(370.6, -82.38) * mm]});
            skFitSpline(sketch, "E1446", {"points": [v(369.92, -81.7) * mm, v(369.74, -81.8) * mm, v(369.64, -82) * mm, v(369.67, -82.21) * mm]});
            skFitSpline(sketch, "E1447", {"points": [v(369.67, -82.21) * mm, v(369.71, -82.42) * mm, v(369.87, -82.58) * mm, v(370.08, -82.62) * mm]});
            skFitSpline(sketch, "E1448", {"points": [v(370.08, -82.62) * mm, v(370.29, -82.66) * mm, v(370.5, -82.56) * mm, v(370.6, -82.38) * mm]});
            skFitSpline(sketch, "E1449", {"points": [v(369.92, -81.7) * mm, v(370.07, -81.6) * mm, v(370.17, -81.44) * mm, v(370.17, -81.26) * mm]});
            skFitSpline(sketch, "E1450", {"points": [v(370.17, -76.8) * mm, v(370.17, -76.61) * mm, v(370.07, -76.45) * mm, v(369.92, -76.36) * mm]});
            skFitSpline(sketch, "E1451", {"points": [v(370.6, -75.68) * mm, v(370.5, -75.5) * mm, v(370.29, -75.4) * mm, v(370.08, -75.43) * mm]});
            skFitSpline(sketch, "E1452", {"points": [v(370.08, -75.43) * mm, v(369.87, -75.47) * mm, v(369.71, -75.63) * mm, v(369.67, -75.84) * mm]});
            skFitSpline(sketch, "E1453", {"points": [v(369.67, -75.84) * mm, v(369.64, -76.05) * mm, v(369.74, -76.26) * mm, v(369.92, -76.36) * mm]});
            skFitSpline(sketch, "E1454", {"points": [v(370.6, -75.68) * mm, v(370.69, -75.83) * mm, v(370.85, -75.93) * mm, v(371.03, -75.93) * mm]});
            skFitSpline(sketch, "E1455", {"points": [v(372.6, -75.93) * mm, v(372.78, -75.93) * mm, v(372.94, -75.83) * mm, v(373.03, -75.68) * mm]});
            skFitSpline(sketch, "E1456", {"points": [v(373.72, -76.36) * mm, v(373.9, -76.26) * mm, v(374, -76.05) * mm, v(373.96, -75.84) * mm]});
            skFitSpline(sketch, "E1457", {"points": [v(373.96, -75.84) * mm, v(373.92, -75.63) * mm, v(373.76, -75.47) * mm, v(373.55, -75.43) * mm]});
            skFitSpline(sketch, "E1458", {"points": [v(373.55, -75.43) * mm, v(373.35, -75.4) * mm, v(373.14, -75.5) * mm, v(373.03, -75.68) * mm]});
            skFitSpline(sketch, "E1459", {"points": [v(373.72, -76.36) * mm, v(373.56, -76.45) * mm, v(373.47, -76.61) * mm, v(373.47, -76.8) * mm]});
            skFitSpline(sketch, "E1460", {"points": [v(373.47, -81.26) * mm, v(373.47, -81.44) * mm, v(373.56, -81.6) * mm, v(373.72, -81.7) * mm]});
            skFitSpline(sketch, "E1461", {"points": [v(373.03, -82.38) * mm, v(373.14, -82.56) * mm, v(373.35, -82.66) * mm, v(373.55, -82.62) * mm]});
            skFitSpline(sketch, "E1462", {"points": [v(373.55, -82.62) * mm, v(373.76, -82.58) * mm, v(373.92, -82.42) * mm, v(373.96, -82.21) * mm]});
            skFitSpline(sketch, "E1463", {"points": [v(373.96, -82.21) * mm, v(374, -82) * mm, v(373.9, -81.8) * mm, v(373.72, -81.7) * mm]});
            skFitSpline(sketch, "E1464", {"points": [v(373.03, -82.38) * mm, v(372.94, -82.22) * mm, v(372.78, -82.13) * mm, v(372.6, -82.13) * mm]});
            skLineSegment(sketch, "E1465", {"start": v(370.17, -81.26) * mm, "end": v(370.17, -76.8) * mm});
            skFitSpline(sketch, "E1466", {"points": [v(371.03, -60.93) * mm, v(370.85, -60.93) * mm, v(370.69, -61.02) * mm, v(370.6, -61.18) * mm]});
            skFitSpline(sketch, "E1467", {"points": [v(369.92, -60.5) * mm, v(369.74, -60.6) * mm, v(369.64, -60.8) * mm, v(369.67, -61.01) * mm]});
            skFitSpline(sketch, "E1468", {"points": [v(369.67, -61.01) * mm, v(369.71, -61.22) * mm, v(369.87, -61.38) * mm, v(370.08, -61.42) * mm]});
            skFitSpline(sketch, "E1469", {"points": [v(370.08, -61.42) * mm, v(370.29, -61.46) * mm, v(370.5, -61.36) * mm, v(370.6, -61.18) * mm]});
            skFitSpline(sketch, "E1470", {"points": [v(369.92, -60.5) * mm, v(370.07, -60.4) * mm, v(370.17, -60.24) * mm, v(370.17, -60.06) * mm]});
            skLineSegment(sketch, "E1471", {"start": v(371.03, -75.93) * mm, "end": v(372.6, -75.93) * mm});
            skFitSpline(sketch, "E1472", {"points": [v(370.17, -55.6) * mm, v(370.17, -55.41) * mm, v(370.07, -55.25) * mm, v(369.92, -55.16) * mm]});
            skFitSpline(sketch, "E1473", {"points": [v(370.6, -54.48) * mm, v(370.5, -54.3) * mm, v(370.29, -54.2) * mm, v(370.08, -54.23) * mm]});
            skFitSpline(sketch, "E1474", {"points": [v(370.08, -54.23) * mm, v(369.87, -54.27) * mm, v(369.71, -54.43) * mm, v(369.67, -54.64) * mm]});
            skFitSpline(sketch, "E1475", {"points": [v(369.67, -54.64) * mm, v(369.64, -54.85) * mm, v(369.74, -55.06) * mm, v(369.92, -55.16) * mm]});
            skFitSpline(sketch, "E1476", {"points": [v(370.6, -54.48) * mm, v(370.69, -54.63) * mm, v(370.85, -54.73) * mm, v(371.03, -54.73) * mm]});
            skLineSegment(sketch, "E1477", {"start": v(373.47, -76.8) * mm, "end": v(373.47, -81.26) * mm});
            skFitSpline(sketch, "E1478", {"points": [v(372.6, -54.73) * mm, v(372.78, -54.73) * mm, v(372.94, -54.63) * mm, v(373.03, -54.48) * mm]});
            skFitSpline(sketch, "E1479", {"points": [v(373.72, -55.16) * mm, v(373.9, -55.06) * mm, v(374, -54.85) * mm, v(373.96, -54.64) * mm]});
            skFitSpline(sketch, "E1480", {"points": [v(373.96, -54.64) * mm, v(373.92, -54.43) * mm, v(373.76, -54.27) * mm, v(373.55, -54.23) * mm]});
            skFitSpline(sketch, "E1481", {"points": [v(373.55, -54.23) * mm, v(373.35, -54.2) * mm, v(373.14, -54.3) * mm, v(373.03, -54.48) * mm]});
            skFitSpline(sketch, "E1482", {"points": [v(373.72, -55.16) * mm, v(373.56, -55.25) * mm, v(373.47, -55.41) * mm, v(373.47, -55.6) * mm]});
            skLineSegment(sketch, "E1483", {"start": v(372.6, -82.13) * mm, "end": v(371.03, -82.13) * mm});
            skFitSpline(sketch, "E1484", {"points": [v(373.47, -60.06) * mm, v(373.47, -60.24) * mm, v(373.56, -60.4) * mm, v(373.72, -60.5) * mm]});
            skFitSpline(sketch, "E1485", {"points": [v(373.03, -61.18) * mm, v(373.14, -61.36) * mm, v(373.35, -61.46) * mm, v(373.55, -61.42) * mm]});
            skFitSpline(sketch, "E1486", {"points": [v(373.55, -61.42) * mm, v(373.76, -61.38) * mm, v(373.92, -61.22) * mm, v(373.96, -61.01) * mm]});
            skFitSpline(sketch, "E1487", {"points": [v(373.96, -61.01) * mm, v(374, -60.8) * mm, v(373.9, -60.6) * mm, v(373.72, -60.5) * mm]});
            skFitSpline(sketch, "E1488", {"points": [v(373.03, -61.18) * mm, v(372.94, -61.02) * mm, v(372.78, -60.93) * mm, v(372.6, -60.93) * mm]});
            skLineSegment(sketch, "E1489", {"start": v(370.17, -60.06) * mm, "end": v(370.17, -55.6) * mm});
            skFitSpline(sketch, "E1490", {"points": [v(373.42, -68.43) * mm, v(373.42, -67.86) * mm, v(373.11, -67.33) * mm, v(372.62, -67.04) * mm]});
            skFitSpline(sketch, "E1491", {"points": [v(372.62, -67.04) * mm, v(372.12, -66.76) * mm, v(371.51, -66.76) * mm, v(371.02, -67.04) * mm]});
            skFitSpline(sketch, "E1492", {"points": [v(371.02, -67.04) * mm, v(370.52, -67.33) * mm, v(370.22, -67.86) * mm, v(370.22, -68.43) * mm]});
            skFitSpline(sketch, "E1493", {"points": [v(370.22, -68.43) * mm, v(370.22, -69) * mm, v(370.52, -69.53) * mm, v(371.02, -69.81) * mm]});
            skFitSpline(sketch, "E1494", {"points": [v(371.02, -69.81) * mm, v(371.51, -70.1) * mm, v(372.12, -70.1) * mm, v(372.62, -69.81) * mm]});
            skFitSpline(sketch, "E1495", {"points": [v(372.62, -69.81) * mm, v(373.11, -69.53) * mm, v(373.42, -69) * mm, v(373.42, -68.43) * mm]});
            skLineSegment(sketch, "E1496", {"start": v(371.03, -54.73) * mm, "end": v(372.6, -54.73) * mm});
            skFitSpline(sketch, "E1497", {"points": [v(-372.6, -3.55) * mm, v(-372.78, -3.55) * mm, v(-372.94, -3.64) * mm, v(-373.03, -3.8) * mm]});
            skFitSpline(sketch, "E1498", {"points": [v(-373.72, -3.11) * mm, v(-373.9, -3.22) * mm, v(-374, -3.43) * mm, v(-373.96, -3.63) * mm]});
            skFitSpline(sketch, "E1499", {"points": [v(-373.96, -3.63) * mm, v(-373.92, -3.84) * mm, v(-373.76, -4) * mm, v(-373.55, -4.04) * mm]});
            skFitSpline(sketch, "E1500", {"points": [v(-373.55, -4.04) * mm, v(-373.35, -4.08) * mm, v(-373.14, -3.98) * mm, v(-373.03, -3.8) * mm]});
            skFitSpline(sketch, "E1501", {"points": [v(-373.72, -3.11) * mm, v(-373.56, -3.02) * mm, v(-373.47, -2.86) * mm, v(-373.47, -2.68) * mm]});
            skLineSegment(sketch, "E1502", {"start": v(373.47, -55.6) * mm, "end": v(373.47, -60.06) * mm});
            skFitSpline(sketch, "E1503", {"points": [v(-373.47, 1.79) * mm, v(-373.47, 1.97) * mm, v(-373.56, 2.13) * mm, v(-373.72, 2.22) * mm]});
            skFitSpline(sketch, "E1504", {"points": [v(-373.03, 2.9) * mm, v(-373.14, 3.09) * mm, v(-373.35, 3.18) * mm, v(-373.55, 3.15) * mm]});
            skFitSpline(sketch, "E1505", {"points": [v(-373.55, 3.15) * mm, v(-373.76, 3.1) * mm, v(-373.92, 2.95) * mm, v(-373.96, 2.74) * mm]});
            skFitSpline(sketch, "E1506", {"points": [v(-373.96, 2.74) * mm, v(-374, 2.53) * mm, v(-373.9, 2.33) * mm, v(-373.72, 2.22) * mm]});
            skFitSpline(sketch, "E1507", {"points": [v(-373.03, 2.9) * mm, v(-372.94, 2.75) * mm, v(-372.78, 2.65) * mm, v(-372.6, 2.65) * mm]});
            skLineSegment(sketch, "E1508", {"start": v(372.6, -60.93) * mm, "end": v(371.03, -60.93) * mm});
            skFitSpline(sketch, "E1509", {"points": [v(-371.03, 2.65) * mm, v(-370.85, 2.65) * mm, v(-370.69, 2.75) * mm, v(-370.6, 2.9) * mm]});
            skFitSpline(sketch, "E1510", {"points": [v(-369.92, 2.22) * mm, v(-369.74, 2.33) * mm, v(-369.64, 2.53) * mm, v(-369.67, 2.74) * mm]});
            skFitSpline(sketch, "E1511", {"points": [v(-369.67, 2.74) * mm, v(-369.71, 2.95) * mm, v(-369.87, 3.1) * mm, v(-370.08, 3.15) * mm]});
            skFitSpline(sketch, "E1512", {"points": [v(-370.08, 3.15) * mm, v(-370.29, 3.18) * mm, v(-370.5, 3.09) * mm, v(-370.6, 2.9) * mm]});
            skFitSpline(sketch, "E1513", {"points": [v(-369.92, 2.22) * mm, v(-370.07, 2.13) * mm, v(-370.17, 1.97) * mm, v(-370.17, 1.79) * mm]});
            skFitSpline(sketch, "E1514", {"points": [v(-370.17, -2.68) * mm, v(-370.17, -2.86) * mm, v(-370.07, -3.02) * mm, v(-369.92, -3.11) * mm]});
            skFitSpline(sketch, "E1515", {"points": [v(-370.6, -3.8) * mm, v(-370.5, -3.98) * mm, v(-370.29, -4.08) * mm, v(-370.08, -4.04) * mm]});
            skFitSpline(sketch, "E1516", {"points": [v(-370.08, -4.04) * mm, v(-369.87, -4) * mm, v(-369.71, -3.84) * mm, v(-369.67, -3.63) * mm]});
            skFitSpline(sketch, "E1517", {"points": [v(-369.67, -3.63) * mm, v(-369.64, -3.43) * mm, v(-369.74, -3.22) * mm, v(-369.92, -3.11) * mm]});
            skFitSpline(sketch, "E1518", {"points": [v(-370.6, -3.8) * mm, v(-370.69, -3.64) * mm, v(-370.85, -3.55) * mm, v(-371.03, -3.55) * mm]});
            skLineSegment(sketch, "E1519", {"start": v(-373.47, -2.68) * mm, "end": v(-373.47, 1.79) * mm});
            skFitSpline(sketch, "E1520", {"points": [v(-372.6, -24.75) * mm, v(-372.78, -24.75) * mm, v(-372.94, -24.84) * mm, v(-373.03, -25) * mm]});
            skFitSpline(sketch, "E1521", {"points": [v(-373.72, -24.31) * mm, v(-373.9, -24.42) * mm, v(-374, -24.63) * mm, v(-373.96, -24.83) * mm]});
            skFitSpline(sketch, "E1522", {"points": [v(-373.96, -24.83) * mm, v(-373.92, -25.04) * mm, v(-373.76, -25.2) * mm, v(-373.55, -25.24) * mm]});
            skFitSpline(sketch, "E1523", {"points": [v(-373.55, -25.24) * mm, v(-373.35, -25.28) * mm, v(-373.14, -25.18) * mm, v(-373.03, -25) * mm]});
            skFitSpline(sketch, "E1524", {"points": [v(-373.72, -24.31) * mm, v(-373.56, -24.22) * mm, v(-373.47, -24.06) * mm, v(-373.47, -23.88) * mm]});
            skLineSegment(sketch, "E1525", {"start": v(-372.6, 2.65) * mm, "end": v(-371.03, 2.65) * mm});
            skFitSpline(sketch, "E1526", {"points": [v(-373.47, -19.41) * mm, v(-373.47, -19.23) * mm, v(-373.56, -19.07) * mm, v(-373.72, -18.98) * mm]});
            skFitSpline(sketch, "E1527", {"points": [v(-373.03, -18.3) * mm, v(-373.14, -18.11) * mm, v(-373.35, -18.02) * mm, v(-373.55, -18.05) * mm]});
            skFitSpline(sketch, "E1528", {"points": [v(-373.55, -18.05) * mm, v(-373.76, -18.1) * mm, v(-373.92, -18.25) * mm, v(-373.96, -18.46) * mm]});
            skFitSpline(sketch, "E1529", {"points": [v(-373.96, -18.46) * mm, v(-374, -18.67) * mm, v(-373.9, -18.87) * mm, v(-373.72, -18.98) * mm]});
            skFitSpline(sketch, "E1530", {"points": [v(-373.03, -18.3) * mm, v(-372.94, -18.45) * mm, v(-372.78, -18.55) * mm, v(-372.6, -18.55) * mm]});
            skLineSegment(sketch, "E1531", {"start": v(-370.17, 1.79) * mm, "end": v(-370.17, -2.68) * mm});
            skFitSpline(sketch, "E1532", {"points": [v(-371.03, -18.55) * mm, v(-370.85, -18.55) * mm, v(-370.69, -18.45) * mm, v(-370.6, -18.3) * mm]});
            skFitSpline(sketch, "E1533", {"points": [v(-369.92, -18.98) * mm, v(-369.74, -18.87) * mm, v(-369.64, -18.67) * mm, v(-369.67, -18.46) * mm]});
            skFitSpline(sketch, "E1534", {"points": [v(-369.67, -18.46) * mm, v(-369.71, -18.25) * mm, v(-369.87, -18.1) * mm, v(-370.08, -18.05) * mm]});
            skFitSpline(sketch, "E1535", {"points": [v(-370.08, -18.05) * mm, v(-370.29, -18.02) * mm, v(-370.5, -18.11) * mm, v(-370.6, -18.3) * mm]});
            skFitSpline(sketch, "E1536", {"points": [v(-369.92, -18.98) * mm, v(-370.07, -19.07) * mm, v(-370.17, -19.23) * mm, v(-370.17, -19.41) * mm]});
            skLineSegment(sketch, "E1537", {"start": v(-371.03, -3.55) * mm, "end": v(-372.6, -3.55) * mm});
            skFitSpline(sketch, "E1538", {"points": [v(-370.17, -23.88) * mm, v(-370.17, -24.06) * mm, v(-370.07, -24.22) * mm, v(-369.92, -24.31) * mm]});
            skFitSpline(sketch, "E1539", {"points": [v(-370.6, -25) * mm, v(-370.5, -25.18) * mm, v(-370.29, -25.28) * mm, v(-370.08, -25.24) * mm]});
            skFitSpline(sketch, "E1540", {"points": [v(-370.08, -25.24) * mm, v(-369.87, -25.2) * mm, v(-369.71, -25.04) * mm, v(-369.67, -24.83) * mm]});
            skFitSpline(sketch, "E1541", {"points": [v(-369.67, -24.83) * mm, v(-369.64, -24.63) * mm, v(-369.74, -24.42) * mm, v(-369.92, -24.31) * mm]});
            skFitSpline(sketch, "E1542", {"points": [v(-370.6, -25) * mm, v(-370.69, -24.84) * mm, v(-370.85, -24.75) * mm, v(-371.03, -24.75) * mm]});
            skLineSegment(sketch, "E1543", {"start": v(-373.47, -23.88) * mm, "end": v(-373.47, -19.41) * mm});
            skFitSpline(sketch, "E1544", {"points": [v(-370.22, -11.05) * mm, v(-370.22, -10.47) * mm, v(-370.52, -9.95) * mm, v(-371.02, -9.66) * mm]});
            skFitSpline(sketch, "E1545", {"points": [v(-371.02, -9.66) * mm, v(-371.51, -9.37) * mm, v(-372.12, -9.37) * mm, v(-372.62, -9.66) * mm]});
            skFitSpline(sketch, "E1546", {"points": [v(-372.62, -9.66) * mm, v(-373.11, -9.95) * mm, v(-373.42, -10.47) * mm, v(-373.42, -11.05) * mm]});
            skFitSpline(sketch, "E1547", {"points": [v(-373.42, -11.05) * mm, v(-373.42, -11.62) * mm, v(-373.11, -12.15) * mm, v(-372.62, -12.43) * mm]});
            skFitSpline(sketch, "E1548", {"points": [v(-372.62, -12.43) * mm, v(-372.12, -12.72) * mm, v(-371.51, -12.72) * mm, v(-371.02, -12.43) * mm]});
            skFitSpline(sketch, "E1549", {"points": [v(-371.02, -12.43) * mm, v(-370.52, -12.15) * mm, v(-370.22, -11.62) * mm, v(-370.22, -11.05) * mm]});
            skLineSegment(sketch, "E1550", {"start": v(-372.6, -18.55) * mm, "end": v(-371.03, -18.55) * mm});
            skFitSpline(sketch, "E1551", {"points": [v(371.03, 34.92) * mm, v(370.85, 34.92) * mm, v(370.69, 34.83) * mm, v(370.6, 34.67) * mm]});
            skFitSpline(sketch, "E1552", {"points": [v(369.92, 35.36) * mm, v(369.74, 35.25) * mm, v(369.64, 35.04) * mm, v(369.67, 34.84) * mm]});
            skFitSpline(sketch, "E1553", {"points": [v(369.67, 34.84) * mm, v(369.71, 34.63) * mm, v(369.87, 34.47) * mm, v(370.08, 34.43) * mm]});
            skFitSpline(sketch, "E1554", {"points": [v(370.08, 34.43) * mm, v(370.29, 34.4) * mm, v(370.5, 34.5) * mm, v(370.6, 34.67) * mm]});
            skFitSpline(sketch, "E1555", {"points": [v(369.92, 35.36) * mm, v(370.07, 35.45) * mm, v(370.17, 35.61) * mm, v(370.17, 35.79) * mm]});
            skLineSegment(sketch, "E1556", {"start": v(-370.17, -19.41) * mm, "end": v(-370.17, -23.88) * mm});
            skFitSpline(sketch, "E1557", {"points": [v(370.17, 40.26) * mm, v(370.17, 40.44) * mm, v(370.07, 40.6) * mm, v(369.92, 40.69) * mm]});
            skFitSpline(sketch, "E1558", {"points": [v(370.6, 41.37) * mm, v(370.5, 41.55) * mm, v(370.29, 41.65) * mm, v(370.08, 41.62) * mm]});
            skFitSpline(sketch, "E1559", {"points": [v(370.08, 41.62) * mm, v(369.87, 41.58) * mm, v(369.71, 41.42) * mm, v(369.68, 41.2) * mm]});
            skFitSpline(sketch, "E1560", {"points": [v(369.68, 41.2) * mm, v(369.64, 41) * mm, v(369.74, 40.8) * mm, v(369.92, 40.69) * mm]});
            skFitSpline(sketch, "E1561", {"points": [v(370.6, 41.37) * mm, v(370.69, 41.22) * mm, v(370.85, 41.12) * mm, v(371.03, 41.12) * mm]});
            skLineSegment(sketch, "E1562", {"start": v(-371.03, -24.75) * mm, "end": v(-372.6, -24.75) * mm});
            skFitSpline(sketch, "E1563", {"points": [v(372.6, 41.12) * mm, v(372.78, 41.12) * mm, v(372.94, 41.22) * mm, v(373.03, 41.37) * mm]});
            skFitSpline(sketch, "E1564", {"points": [v(373.72, 40.69) * mm, v(373.9, 40.8) * mm, v(374, 41) * mm, v(373.96, 41.2) * mm]});
            skFitSpline(sketch, "E1565", {"points": [v(373.96, 41.2) * mm, v(373.92, 41.42) * mm, v(373.76, 41.58) * mm, v(373.55, 41.62) * mm]});
            skFitSpline(sketch, "E1566", {"points": [v(373.55, 41.62) * mm, v(373.35, 41.65) * mm, v(373.14, 41.55) * mm, v(373.03, 41.37) * mm]});
            skFitSpline(sketch, "E1567", {"points": [v(373.72, 40.69) * mm, v(373.56, 40.6) * mm, v(373.47, 40.44) * mm, v(373.47, 40.26) * mm]});
            skFitSpline(sketch, "E1568", {"points": [v(373.47, 35.79) * mm, v(373.47, 35.61) * mm, v(373.56, 35.45) * mm, v(373.72, 35.36) * mm]});
            skFitSpline(sketch, "E1569", {"points": [v(373.03, 34.67) * mm, v(373.14, 34.5) * mm, v(373.35, 34.4) * mm, v(373.55, 34.43) * mm]});
            skFitSpline(sketch, "E1570", {"points": [v(373.55, 34.43) * mm, v(373.76, 34.47) * mm, v(373.92, 34.63) * mm, v(373.96, 34.84) * mm]});
            skFitSpline(sketch, "E1571", {"points": [v(373.96, 34.84) * mm, v(374, 35.04) * mm, v(373.9, 35.25) * mm, v(373.72, 35.36) * mm]});
            skFitSpline(sketch, "E1572", {"points": [v(373.03, 34.67) * mm, v(372.94, 34.83) * mm, v(372.78, 34.92) * mm, v(372.6, 34.92) * mm]});
            skLineSegment(sketch, "E1573", {"start": v(370.17, 35.79) * mm, "end": v(370.17, 40.26) * mm});
            skFitSpline(sketch, "E1574", {"points": [v(371.03, 56.12) * mm, v(370.85, 56.12) * mm, v(370.69, 56.03) * mm, v(370.6, 55.87) * mm]});
            skFitSpline(sketch, "E1575", {"points": [v(369.92, 56.56) * mm, v(369.74, 56.45) * mm, v(369.64, 56.24) * mm, v(369.67, 56.04) * mm]});
            skFitSpline(sketch, "E1576", {"points": [v(369.67, 56.04) * mm, v(369.71, 55.83) * mm, v(369.87, 55.67) * mm, v(370.08, 55.63) * mm]});
            skFitSpline(sketch, "E1577", {"points": [v(370.08, 55.63) * mm, v(370.29, 55.6) * mm, v(370.5, 55.7) * mm, v(370.6, 55.87) * mm]});
            skFitSpline(sketch, "E1578", {"points": [v(369.92, 56.56) * mm, v(370.07, 56.65) * mm, v(370.17, 56.81) * mm, v(370.17, 56.99) * mm]});
            skLineSegment(sketch, "E1579", {"start": v(371.03, 41.12) * mm, "end": v(372.6, 41.12) * mm});
            skFitSpline(sketch, "E1580", {"points": [v(370.17, 61.46) * mm, v(370.17, 61.64) * mm, v(370.07, 61.8) * mm, v(369.92, 61.89) * mm]});
            skFitSpline(sketch, "E1581", {"points": [v(370.6, 62.57) * mm, v(370.5, 62.75) * mm, v(370.29, 62.85) * mm, v(370.08, 62.82) * mm]});
            skFitSpline(sketch, "E1582", {"points": [v(370.08, 62.82) * mm, v(369.87, 62.78) * mm, v(369.71, 62.62) * mm, v(369.68, 62.4) * mm]});
            skFitSpline(sketch, "E1583", {"points": [v(369.68, 62.4) * mm, v(369.64, 62.2) * mm, v(369.74, 62) * mm, v(369.92, 61.89) * mm]});
            skFitSpline(sketch, "E1584", {"points": [v(370.6, 62.57) * mm, v(370.69, 62.42) * mm, v(370.85, 62.32) * mm, v(371.03, 62.32) * mm]});
            skLineSegment(sketch, "E1585", {"start": v(373.47, 40.26) * mm, "end": v(373.47, 35.79) * mm});
            skFitSpline(sketch, "E1586", {"points": [v(372.6, 62.32) * mm, v(372.78, 62.32) * mm, v(372.94, 62.42) * mm, v(373.03, 62.57) * mm]});
            skFitSpline(sketch, "E1587", {"points": [v(373.72, 61.89) * mm, v(373.9, 62) * mm, v(374, 62.2) * mm, v(373.96, 62.4) * mm]});
            skFitSpline(sketch, "E1588", {"points": [v(373.96, 62.4) * mm, v(373.92, 62.62) * mm, v(373.76, 62.78) * mm, v(373.55, 62.82) * mm]});
            skFitSpline(sketch, "E1589", {"points": [v(373.55, 62.82) * mm, v(373.35, 62.85) * mm, v(373.14, 62.75) * mm, v(373.03, 62.57) * mm]});
            skFitSpline(sketch, "E1590", {"points": [v(373.72, 61.89) * mm, v(373.56, 61.8) * mm, v(373.47, 61.64) * mm, v(373.47, 61.46) * mm]});
            skLineSegment(sketch, "E1591", {"start": v(372.6, 34.92) * mm, "end": v(371.03, 34.92) * mm});
            skFitSpline(sketch, "E1592", {"points": [v(373.47, 56.99) * mm, v(373.47, 56.81) * mm, v(373.56, 56.65) * mm, v(373.72, 56.56) * mm]});
            skFitSpline(sketch, "E1593", {"points": [v(373.03, 55.87) * mm, v(373.14, 55.7) * mm, v(373.35, 55.6) * mm, v(373.55, 55.63) * mm]});
            skFitSpline(sketch, "E1594", {"points": [v(373.55, 55.63) * mm, v(373.76, 55.67) * mm, v(373.92, 55.83) * mm, v(373.96, 56.04) * mm]});
            skFitSpline(sketch, "E1595", {"points": [v(373.96, 56.04) * mm, v(374, 56.24) * mm, v(373.9, 56.45) * mm, v(373.72, 56.56) * mm]});
            skFitSpline(sketch, "E1596", {"points": [v(373.03, 55.87) * mm, v(372.94, 56.03) * mm, v(372.78, 56.12) * mm, v(372.6, 56.12) * mm]});
            skLineSegment(sketch, "E1597", {"start": v(370.17, 56.99) * mm, "end": v(370.17, 61.46) * mm});
            skFitSpline(sketch, "E1598", {"points": [v(373.42, 48.62) * mm, v(373.42, 49.2) * mm, v(373.11, 49.72) * mm, v(372.62, 50) * mm]});
            skFitSpline(sketch, "E1599", {"points": [v(372.62, 50) * mm, v(372.12, 50.3) * mm, v(371.51, 50.3) * mm, v(371.02, 50) * mm]});
            skFitSpline(sketch, "E1600", {"points": [v(371.02, 50) * mm, v(370.52, 49.72) * mm, v(370.22, 49.2) * mm, v(370.22, 48.62) * mm]});
            skFitSpline(sketch, "E1601", {"points": [v(370.22, 48.62) * mm, v(370.22, 48.05) * mm, v(370.52, 47.52) * mm, v(371.02, 47.24) * mm]});
            skFitSpline(sketch, "E1602", {"points": [v(371.02, 47.24) * mm, v(371.51, 46.95) * mm, v(372.12, 46.95) * mm, v(372.62, 47.24) * mm]});
            skFitSpline(sketch, "E1603", {"points": [v(372.62, 47.24) * mm, v(373.11, 47.52) * mm, v(373.42, 48.05) * mm, v(373.42, 48.62) * mm]});
            skLineSegment(sketch, "E1604", {"start": v(371.03, 62.32) * mm, "end": v(372.6, 62.32) * mm});
            skLineSegment(sketch, "E1605", {"start": v(373.47, 61.46) * mm, "end": v(373.47, 56.99) * mm});
            skLineSegment(sketch, "E1606", {"start": v(372.6, 56.12) * mm, "end": v(371.03, 56.12) * mm});
            skFitSpline(sketch, "E1607", {"points": [v(8.21, -182.45) * mm, v(8.22, -103.9) * mm, v(8.22, -25.33) * mm, v(8.23, 53.22) * mm]});
            skFitSpline(sketch, "E1608", {"points": [v(8.23, 53.22) * mm, v(8.24, 53.38) * mm, v(8.14, 53.53) * mm, v(7.99, 53.61) * mm]});
            skFitSpline(sketch, "E1609", {"points": [v(7.99, 53.61) * mm, v(7.8, 53.72) * mm, v(7.7, 53.93) * mm, v(7.75, 54.13) * mm]});
            skFitSpline(sketch, "E1610", {"points": [v(7.75, 54.13) * mm, v(7.78, 54.34) * mm, v(7.95, 54.5) * mm, v(8.15, 54.54) * mm]});
            skFitSpline(sketch, "E1611", {"points": [v(8.15, 54.54) * mm, v(8.36, 54.58) * mm, v(8.57, 54.48) * mm, v(8.67, 54.3) * mm]});
            skFitSpline(sketch, "E1612", {"points": [v(8.67, 54.3) * mm, v(8.76, 54.14) * mm, v(8.93, 54.05) * mm, v(9.1, 54.05) * mm]});
            skFitSpline(sketch, "E1613", {"points": [v(-31.33, 54.3) * mm, v(-31.24, 54.14) * mm, v(-31.07, 54.05) * mm, v(-30.9, 54.05) * mm]});
            skFitSpline(sketch, "E1614", {"points": [v(-31.33, 54.3) * mm, v(-31.43, 54.48) * mm, v(-31.64, 54.58) * mm, v(-31.85, 54.54) * mm]});
            skFitSpline(sketch, "E1615", {"points": [v(-31.85, 54.54) * mm, v(-32.05, 54.5) * mm, v(-32.22, 54.34) * mm, v(-32.25, 54.13) * mm]});
            skFitSpline(sketch, "E1616", {"points": [v(-32.25, 54.13) * mm, v(-32.3, 53.93) * mm, v(-32.2, 53.72) * mm, v(-32.01, 53.61) * mm]});
            skFitSpline(sketch, "E1617", {"points": [v(-31.76, 53.18) * mm, v(-31.76, 53.36) * mm, v(-31.86, 53.52) * mm, v(-32.01, 53.61) * mm]});
            skFitSpline(sketch, "E1618", {"points": [v(-32.26, 51.05) * mm, v(-31.98, 51.05) * mm, v(-31.76, 51.27) * mm, v(-31.76, 51.55) * mm]});
            skFitSpline(sketch, "E1619", {"points": [v(-37.76, 51.55) * mm, v(-37.76, 51.27) * mm, v(-37.54, 51.05) * mm, v(-37.26, 51.05) * mm]});
            skLineSegment(sketch, "E1620", {"start": v(9.1, 54.05) * mm, "end": v(17.64, 54.05) * mm});
            skLineSegment(sketch, "E1621", {"start": v(17.64, 54.05) * mm, "end": v(17.64, 156.05) * mm});
            skLineSegment(sketch, "E1622", {"start": v(17.64, 156.05) * mm, "end": v(19.64, 158.05) * mm});
            skLineSegment(sketch, "E1623", {"start": v(19.64, 158.05) * mm, "end": v(19.64, 179.04) * mm});
            skLineSegment(sketch, "E1624", {"start": v(19.64, 179.04) * mm, "end": v(19.64, 204.05) * mm});
            skLineSegment(sketch, "E1625", {"start": v(19.64, 204.05) * mm, "end": v(9.1, 204.05) * mm});
            skFitSpline(sketch, "E1626", {"points": [v(-37.51, 53.61) * mm, v(-37.67, 53.52) * mm, v(-37.76, 53.36) * mm, v(-37.76, 53.18) * mm]});
            skFitSpline(sketch, "E1627", {"points": [v(-37.51, 53.61) * mm, v(-37.33, 53.72) * mm, v(-37.23, 53.93) * mm, v(-37.27, 54.13) * mm]});
            skFitSpline(sketch, "E1628", {"points": [v(-37.27, 54.13) * mm, v(-37.3, 54.34) * mm, v(-37.47, 54.5) * mm, v(-37.67, 54.54) * mm]});
            skFitSpline(sketch, "E1629", {"points": [v(-37.67, 54.54) * mm, v(-37.88, 54.58) * mm, v(-38.09, 54.48) * mm, v(-38.2, 54.3) * mm]});
            skFitSpline(sketch, "E1630", {"points": [v(-38.63, 54.05) * mm, v(-38.45, 54.05) * mm, v(-38.28, 54.14) * mm, v(-38.2, 54.3) * mm]});
            skLineSegment(sketch, "E1631", {"start": v(-31.76, 53.18) * mm, "end": v(-31.76, 51.55) * mm});
            skFitSpline(sketch, "E1632", {"points": [v(-52.53, 54.3) * mm, v(-52.44, 54.14) * mm, v(-52.27, 54.05) * mm, v(-52.1, 54.05) * mm]});
            skFitSpline(sketch, "E1633", {"points": [v(-52.53, 54.3) * mm, v(-52.63, 54.48) * mm, v(-52.84, 54.58) * mm, v(-53.05, 54.54) * mm]});
            skFitSpline(sketch, "E1634", {"points": [v(-53.05, 54.54) * mm, v(-53.25, 54.5) * mm, v(-53.42, 54.34) * mm, v(-53.45, 54.13) * mm]});
            skFitSpline(sketch, "E1635", {"points": [v(-53.45, 54.13) * mm, v(-53.5, 53.93) * mm, v(-53.4, 53.72) * mm, v(-53.21, 53.61) * mm]});
            skFitSpline(sketch, "E1636", {"points": [v(-52.96, 53.18) * mm, v(-52.96, 53.36) * mm, v(-53.06, 53.52) * mm, v(-53.21, 53.61) * mm]});
            skLineSegment(sketch, "E1637", {"start": v(-32.26, 51.05) * mm, "end": v(-37.26, 51.05) * mm});
            skFitSpline(sketch, "E1638", {"points": [v(-53.46, 51.05) * mm, v(-53.19, 51.05) * mm, v(-52.96, 51.27) * mm, v(-52.96, 51.55) * mm]});
            skLineSegment(sketch, "E1639", {"start": v(-37.76, 51.55) * mm, "end": v(-37.76, 53.18) * mm});
            skFitSpline(sketch, "E1640", {"points": [v(-58.96, 51.55) * mm, v(-58.96, 51.41) * mm, v(-58.9, 51.29) * mm, v(-58.81, 51.2) * mm]});
            skFitSpline(sketch, "E1641", {"points": [v(-58.81, 51.2) * mm, v(-58.72, 51.1) * mm, v(-58.6, 51.05) * mm, v(-58.46, 51.05) * mm]});
            skLineSegment(sketch, "E1642", {"start": v(-38.63, 54.05) * mm, "end": v(-43.76, 54.05) * mm});
            skLineSegment(sketch, "E1643", {"start": v(-43.76, 54.05) * mm, "end": v(-43.76, 57.05) * mm});
            skLineSegment(sketch, "E1644", {"start": v(-43.76, 57.05) * mm, "end": v(-42.49, 57.05) * mm});
            skLineSegment(sketch, "E1645", {"start": v(-42.49, 57.05) * mm, "end": v(-42.49, 61.05) * mm});
            skLineSegment(sketch, "E1646", {"start": v(-42.49, 61.05) * mm, "end": v(-43.76, 61.05) * mm});
            skLineSegment(sketch, "E1647", {"start": v(-43.76, 61.05) * mm, "end": v(-43.76, 64.05) * mm});
            skLineSegment(sketch, "E1648", {"start": v(-43.76, 64.05) * mm, "end": v(-46.96, 64.05) * mm});
            skLineSegment(sketch, "E1649", {"start": v(-46.96, 64.05) * mm, "end": v(-46.96, 61.05) * mm});
            skLineSegment(sketch, "E1650", {"start": v(-46.96, 61.05) * mm, "end": v(-48.24, 61.05) * mm});
            skLineSegment(sketch, "E1651", {"start": v(-48.24, 61.05) * mm, "end": v(-48.24, 57.05) * mm});
            skLineSegment(sketch, "E1652", {"start": v(-48.24, 57.05) * mm, "end": v(-46.96, 57.05) * mm});
            skLineSegment(sketch, "E1653", {"start": v(-46.96, 57.05) * mm, "end": v(-46.96, 54.05) * mm});
            skLineSegment(sketch, "E1654", {"start": v(-46.96, 54.05) * mm, "end": v(-52.1, 54.05) * mm});
            skFitSpline(sketch, "E1655", {"points": [v(-58.71, 53.61) * mm, v(-58.87, 53.52) * mm, v(-58.96, 53.36) * mm, v(-58.96, 53.18) * mm]});
            skFitSpline(sketch, "E1656", {"points": [v(-58.71, 53.61) * mm, v(-58.53, 53.72) * mm, v(-58.43, 53.93) * mm, v(-58.47, 54.13) * mm]});
            skFitSpline(sketch, "E1657", {"points": [v(-58.47, 54.13) * mm, v(-58.5, 54.34) * mm, v(-58.67, 54.5) * mm, v(-58.87, 54.54) * mm]});
            skFitSpline(sketch, "E1658", {"points": [v(-58.87, 54.54) * mm, v(-59.08, 54.58) * mm, v(-59.29, 54.48) * mm, v(-59.4, 54.3) * mm]});
            skFitSpline(sketch, "E1659", {"points": [v(-59.83, 54.05) * mm, v(-59.65, 54.05) * mm, v(-59.48, 54.14) * mm, v(-59.4, 54.3) * mm]});
            skLineSegment(sketch, "E1660", {"start": v(-52.96, 53.18) * mm, "end": v(-52.96, 51.55) * mm});
            skFitSpline(sketch, "E1661", {"points": [v(-151.33, 54.3) * mm, v(-151.24, 54.14) * mm, v(-151.07, 54.05) * mm, v(-150.9, 54.05) * mm]});
            skFitSpline(sketch, "E1662", {"points": [v(-151.33, 54.3) * mm, v(-151.43, 54.48) * mm, v(-151.64, 54.58) * mm, v(-151.85, 54.54) * mm]});
            skFitSpline(sketch, "E1663", {"points": [v(-151.85, 54.54) * mm, v(-152.05, 54.5) * mm, v(-152.22, 54.34) * mm, v(-152.25, 54.13) * mm]});
            skFitSpline(sketch, "E1664", {"points": [v(-152.25, 54.13) * mm, v(-152.3, 53.93) * mm, v(-152.2, 53.72) * mm, v(-152.01, 53.61) * mm]});
            skFitSpline(sketch, "E1665", {"points": [v(-151.76, 53.18) * mm, v(-151.76, 53.36) * mm, v(-151.86, 53.52) * mm, v(-152.01, 53.61) * mm]});
            skLineSegment(sketch, "E1666", {"start": v(-53.46, 51.05) * mm, "end": v(-58.46, 51.05) * mm});
            skFitSpline(sketch, "E1667", {"points": [v(-152.26, 51.05) * mm, v(-151.98, 51.05) * mm, v(-151.76, 51.27) * mm, v(-151.76, 51.55) * mm]});
            skLineSegment(sketch, "E1668", {"start": v(-58.96, 51.55) * mm, "end": v(-58.96, 53.18) * mm});
            skFitSpline(sketch, "E1669", {"points": [v(-157.76, 51.55) * mm, v(-157.76, 51.41) * mm, v(-157.7, 51.29) * mm, v(-157.61, 51.2) * mm]});
            skFitSpline(sketch, "E1670", {"points": [v(-157.61, 51.2) * mm, v(-157.52, 51.1) * mm, v(-157.4, 51.05) * mm, v(-157.26, 51.05) * mm]});
            skLineSegment(sketch, "E1671", {"start": v(-59.83, 54.05) * mm, "end": v(-150.9, 54.05) * mm});
            skFitSpline(sketch, "E1672", {"points": [v(-157.51, 53.61) * mm, v(-157.67, 53.52) * mm, v(-157.76, 53.36) * mm, v(-157.76, 53.18) * mm]});
            skFitSpline(sketch, "E1673", {"points": [v(-157.51, 53.61) * mm, v(-157.33, 53.72) * mm, v(-157.23, 53.93) * mm, v(-157.27, 54.13) * mm]});
            skFitSpline(sketch, "E1674", {"points": [v(-157.27, 54.13) * mm, v(-157.3, 54.34) * mm, v(-157.47, 54.5) * mm, v(-157.67, 54.54) * mm]});
            skFitSpline(sketch, "E1675", {"points": [v(-157.67, 54.54) * mm, v(-157.88, 54.58) * mm, v(-158.09, 54.48) * mm, v(-158.2, 54.3) * mm]});
            skFitSpline(sketch, "E1676", {"points": [v(-158.63, 54.05) * mm, v(-158.45, 54.05) * mm, v(-158.28, 54.14) * mm, v(-158.2, 54.3) * mm]});
            skLineSegment(sketch, "E1677", {"start": v(-151.76, 53.18) * mm, "end": v(-151.76, 51.55) * mm});
            skFitSpline(sketch, "E1678", {"points": [v(-172.53, 54.3) * mm, v(-172.44, 54.14) * mm, v(-172.27, 54.05) * mm, v(-172.1, 54.05) * mm]});
            skFitSpline(sketch, "E1679", {"points": [v(-172.53, 54.3) * mm, v(-172.63, 54.48) * mm, v(-172.84, 54.58) * mm, v(-173.05, 54.54) * mm]});
            skFitSpline(sketch, "E1680", {"points": [v(-173.05, 54.54) * mm, v(-173.25, 54.5) * mm, v(-173.42, 54.34) * mm, v(-173.45, 54.13) * mm]});
            skFitSpline(sketch, "E1681", {"points": [v(-173.45, 54.13) * mm, v(-173.5, 53.93) * mm, v(-173.4, 53.72) * mm, v(-173.21, 53.61) * mm]});
            skFitSpline(sketch, "E1682", {"points": [v(-172.96, 53.18) * mm, v(-172.96, 53.36) * mm, v(-173.06, 53.52) * mm, v(-173.21, 53.61) * mm]});
            skLineSegment(sketch, "E1683", {"start": v(-152.26, 51.05) * mm, "end": v(-157.26, 51.05) * mm});
            skFitSpline(sketch, "E1684", {"points": [v(-173.46, 51.05) * mm, v(-173.33, 51.05) * mm, v(-173.2, 51.1) * mm, v(-173.1, 51.2) * mm]});
            skFitSpline(sketch, "E1685", {"points": [v(-173.1, 51.2) * mm, v(-173.01, 51.29) * mm, v(-172.96, 51.41) * mm, v(-172.96, 51.55) * mm]});
            skLineSegment(sketch, "E1686", {"start": v(-157.76, 51.55) * mm, "end": v(-157.76, 53.18) * mm});
            skFitSpline(sketch, "E1687", {"points": [v(-178.96, 51.55) * mm, v(-178.96, 51.41) * mm, v(-178.9, 51.29) * mm, v(-178.81, 51.2) * mm]});
            skFitSpline(sketch, "E1688", {"points": [v(-178.81, 51.2) * mm, v(-178.72, 51.1) * mm, v(-178.6, 51.05) * mm, v(-178.46, 51.05) * mm]});
            skLineSegment(sketch, "E1689", {"start": v(-158.63, 54.05) * mm, "end": v(-163.76, 54.05) * mm});
            skLineSegment(sketch, "E1690", {"start": v(-163.76, 54.05) * mm, "end": v(-163.76, 57.05) * mm});
            skLineSegment(sketch, "E1691", {"start": v(-163.76, 57.05) * mm, "end": v(-162.49, 57.05) * mm});
            skLineSegment(sketch, "E1692", {"start": v(-162.49, 57.05) * mm, "end": v(-162.49, 61.05) * mm});
            skLineSegment(sketch, "E1693", {"start": v(-162.49, 61.05) * mm, "end": v(-163.76, 61.05) * mm});
            skLineSegment(sketch, "E1694", {"start": v(-163.76, 61.05) * mm, "end": v(-163.76, 64.05) * mm});
            skLineSegment(sketch, "E1695", {"start": v(-163.76, 64.05) * mm, "end": v(-166.96, 64.05) * mm});
            skLineSegment(sketch, "E1696", {"start": v(-166.96, 64.05) * mm, "end": v(-166.96, 61.05) * mm});
            skLineSegment(sketch, "E1697", {"start": v(-166.96, 61.05) * mm, "end": v(-168.24, 61.05) * mm});
            skLineSegment(sketch, "E1698", {"start": v(-168.24, 61.05) * mm, "end": v(-168.24, 57.05) * mm});
            skLineSegment(sketch, "E1699", {"start": v(-168.24, 57.05) * mm, "end": v(-166.96, 57.05) * mm});
            skLineSegment(sketch, "E1700", {"start": v(-166.96, 57.05) * mm, "end": v(-166.96, 54.05) * mm});
            skLineSegment(sketch, "E1701", {"start": v(-166.96, 54.05) * mm, "end": v(-172.1, 54.05) * mm});
            skFitSpline(sketch, "E1702", {"points": [v(-178.71, 53.61) * mm, v(-178.87, 53.52) * mm, v(-178.96, 53.36) * mm, v(-178.96, 53.18) * mm]});
            skFitSpline(sketch, "E1703", {"points": [v(-178.71, 53.61) * mm, v(-178.53, 53.72) * mm, v(-178.43, 53.93) * mm, v(-178.47, 54.13) * mm]});
            skFitSpline(sketch, "E1704", {"points": [v(-178.47, 54.13) * mm, v(-178.5, 54.34) * mm, v(-178.67, 54.5) * mm, v(-178.87, 54.54) * mm]});
            skFitSpline(sketch, "E1705", {"points": [v(-178.87, 54.54) * mm, v(-179.08, 54.58) * mm, v(-179.29, 54.48) * mm, v(-179.4, 54.3) * mm]});
            skFitSpline(sketch, "E1706", {"points": [v(-179.83, 54.05) * mm, v(-179.65, 54.05) * mm, v(-179.48, 54.14) * mm, v(-179.4, 54.3) * mm]});
            skLineSegment(sketch, "E1707", {"start": v(-172.96, 53.18) * mm, "end": v(-172.96, 51.55) * mm});
            skFitSpline(sketch, "E1708", {"points": [v(-311.33, 54.3) * mm, v(-311.24, 54.14) * mm, v(-311.07, 54.05) * mm, v(-310.9, 54.05) * mm]});
            skFitSpline(sketch, "E1709", {"points": [v(-311.33, 54.3) * mm, v(-311.43, 54.48) * mm, v(-311.64, 54.58) * mm, v(-311.85, 54.54) * mm]});
            skFitSpline(sketch, "E1710", {"points": [v(-311.85, 54.54) * mm, v(-312.05, 54.5) * mm, v(-312.22, 54.34) * mm, v(-312.25, 54.13) * mm]});
            skFitSpline(sketch, "E1711", {"points": [v(-312.25, 54.13) * mm, v(-312.3, 53.93) * mm, v(-312.2, 53.72) * mm, v(-312.01, 53.61) * mm]});
            skFitSpline(sketch, "E1712", {"points": [v(-311.76, 53.18) * mm, v(-311.76, 53.36) * mm, v(-311.86, 53.52) * mm, v(-312.01, 53.61) * mm]});
            skLineSegment(sketch, "E1713", {"start": v(-173.46, 51.05) * mm, "end": v(-178.46, 51.05) * mm});
            skFitSpline(sketch, "E1714", {"points": [v(-312.26, 51.05) * mm, v(-311.98, 51.05) * mm, v(-311.76, 51.27) * mm, v(-311.76, 51.55) * mm]});
            skLineSegment(sketch, "E1715", {"start": v(-178.96, 51.55) * mm, "end": v(-178.96, 53.18) * mm});
            skFitSpline(sketch, "E1716", {"points": [v(-317.76, 51.55) * mm, v(-317.76, 51.27) * mm, v(-317.54, 51.05) * mm, v(-317.26, 51.05) * mm]});
            skLineSegment(sketch, "E1717", {"start": v(-179.83, 54.05) * mm, "end": v(-310.9, 54.05) * mm});
            skFitSpline(sketch, "E1718", {"points": [v(-317.51, 53.61) * mm, v(-317.67, 53.52) * mm, v(-317.76, 53.36) * mm, v(-317.76, 53.18) * mm]});
            skFitSpline(sketch, "E1719", {"points": [v(-317.51, 53.61) * mm, v(-317.33, 53.72) * mm, v(-317.23, 53.93) * mm, v(-317.27, 54.13) * mm]});
            skFitSpline(sketch, "E1720", {"points": [v(-317.27, 54.13) * mm, v(-317.3, 54.34) * mm, v(-317.47, 54.5) * mm, v(-317.67, 54.54) * mm]});
            skFitSpline(sketch, "E1721", {"points": [v(-317.67, 54.54) * mm, v(-317.88, 54.58) * mm, v(-318.09, 54.48) * mm, v(-318.2, 54.3) * mm]});
            skFitSpline(sketch, "E1722", {"points": [v(-318.63, 54.05) * mm, v(-318.45, 54.05) * mm, v(-318.28, 54.14) * mm, v(-318.2, 54.3) * mm]});
            skLineSegment(sketch, "E1723", {"start": v(-311.76, 53.18) * mm, "end": v(-311.76, 51.55) * mm});
            skFitSpline(sketch, "E1724", {"points": [v(-332.53, 54.3) * mm, v(-332.44, 54.14) * mm, v(-332.27, 54.05) * mm, v(-332.1, 54.05) * mm]});
            skFitSpline(sketch, "E1725", {"points": [v(-332.53, 54.3) * mm, v(-332.63, 54.48) * mm, v(-332.84, 54.58) * mm, v(-333.05, 54.54) * mm]});
            skFitSpline(sketch, "E1726", {"points": [v(-333.05, 54.54) * mm, v(-333.25, 54.5) * mm, v(-333.42, 54.34) * mm, v(-333.45, 54.13) * mm]});
            skFitSpline(sketch, "E1727", {"points": [v(-333.45, 54.13) * mm, v(-333.5, 53.93) * mm, v(-333.4, 53.72) * mm, v(-333.21, 53.61) * mm]});
            skFitSpline(sketch, "E1728", {"points": [v(-332.96, 53.18) * mm, v(-332.96, 53.36) * mm, v(-333.06, 53.52) * mm, v(-333.21, 53.61) * mm]});
            skLineSegment(sketch, "E1729", {"start": v(-312.26, 51.05) * mm, "end": v(-317.26, 51.05) * mm});
            skFitSpline(sketch, "E1730", {"points": [v(-333.46, 51.05) * mm, v(-333.33, 51.05) * mm, v(-333.2, 51.1) * mm, v(-333.1, 51.2) * mm]});
            skFitSpline(sketch, "E1731", {"points": [v(-333.1, 51.2) * mm, v(-333.01, 51.29) * mm, v(-332.96, 51.41) * mm, v(-332.96, 51.55) * mm]});
            skLineSegment(sketch, "E1732", {"start": v(-317.76, 51.55) * mm, "end": v(-317.76, 53.18) * mm});
            skFitSpline(sketch, "E1733", {"points": [v(-338.96, 51.55) * mm, v(-338.96, 51.41) * mm, v(-338.9, 51.29) * mm, v(-338.81, 51.2) * mm]});
            skFitSpline(sketch, "E1734", {"points": [v(-338.81, 51.2) * mm, v(-338.72, 51.1) * mm, v(-338.6, 51.05) * mm, v(-338.46, 51.05) * mm]});
            skLineSegment(sketch, "E1735", {"start": v(-318.63, 54.05) * mm, "end": v(-323.76, 54.05) * mm});
            skLineSegment(sketch, "E1736", {"start": v(-323.76, 54.05) * mm, "end": v(-323.76, 57.05) * mm});
            skLineSegment(sketch, "E1737", {"start": v(-323.76, 57.05) * mm, "end": v(-322.49, 57.05) * mm});
            skLineSegment(sketch, "E1738", {"start": v(-322.49, 57.05) * mm, "end": v(-322.49, 61.05) * mm});
            skLineSegment(sketch, "E1739", {"start": v(-322.49, 61.05) * mm, "end": v(-323.76, 61.05) * mm});
            skLineSegment(sketch, "E1740", {"start": v(-323.76, 61.05) * mm, "end": v(-323.76, 64.05) * mm});
            skLineSegment(sketch, "E1741", {"start": v(-323.76, 64.05) * mm, "end": v(-326.96, 64.05) * mm});
            skLineSegment(sketch, "E1742", {"start": v(-326.96, 64.05) * mm, "end": v(-326.96, 61.05) * mm});
            skLineSegment(sketch, "E1743", {"start": v(-326.96, 61.05) * mm, "end": v(-328.24, 61.05) * mm});
            skLineSegment(sketch, "E1744", {"start": v(-328.24, 61.05) * mm, "end": v(-328.24, 57.05) * mm});
            skLineSegment(sketch, "E1745", {"start": v(-328.24, 57.05) * mm, "end": v(-326.96, 57.05) * mm});
            skLineSegment(sketch, "E1746", {"start": v(-326.96, 57.05) * mm, "end": v(-326.96, 54.05) * mm});
            skLineSegment(sketch, "E1747", {"start": v(-326.96, 54.05) * mm, "end": v(-332.1, 54.05) * mm});
            skFitSpline(sketch, "E1748", {"points": [v(-338.71, 53.61) * mm, v(-338.87, 53.52) * mm, v(-338.96, 53.36) * mm, v(-338.96, 53.18) * mm]});
            skFitSpline(sketch, "E1749", {"points": [v(-338.71, 53.61) * mm, v(-338.53, 53.72) * mm, v(-338.43, 53.93) * mm, v(-338.47, 54.13) * mm]});
            skFitSpline(sketch, "E1750", {"points": [v(-338.47, 54.13) * mm, v(-338.5, 54.34) * mm, v(-338.67, 54.5) * mm, v(-338.87, 54.54) * mm]});
            skFitSpline(sketch, "E1751", {"points": [v(-338.87, 54.54) * mm, v(-339.08, 54.58) * mm, v(-339.29, 54.48) * mm, v(-339.4, 54.3) * mm]});
            skFitSpline(sketch, "E1752", {"points": [v(-339.83, 54.05) * mm, v(-339.65, 54.05) * mm, v(-339.48, 54.14) * mm, v(-339.4, 54.3) * mm]});
            skLineSegment(sketch, "E1753", {"start": v(-332.96, 53.18) * mm, "end": v(-332.96, 51.55) * mm});
            skFitSpline(sketch, "E1754", {"points": [v(-347.7, 64.45) * mm, v(-347.78, 64.6) * mm, v(-347.95, 64.7) * mm, v(-348.13, 64.7) * mm]});
            skFitSpline(sketch, "E1755", {"points": [v(-347.7, 64.45) * mm, v(-347.59, 64.26) * mm, v(-347.38, 64.17) * mm, v(-347.17, 64.2) * mm]});
            skFitSpline(sketch, "E1756", {"points": [v(-347.17, 64.2) * mm, v(-346.97, 64.24) * mm, v(-346.8, 64.4) * mm, v(-346.77, 64.6) * mm]});
            skFitSpline(sketch, "E1757", {"points": [v(-346.77, 64.6) * mm, v(-346.73, 64.82) * mm, v(-346.83, 65.02) * mm, v(-347.01, 65.13) * mm]});
            skFitSpline(sketch, "E1758", {"points": [v(-347.26, 65.56) * mm, v(-347.26, 65.38) * mm, v(-347.17, 65.22) * mm, v(-347.01, 65.13) * mm]});
            skLineSegment(sketch, "E1759", {"start": v(-333.46, 51.05) * mm, "end": v(-338.46, 51.05) * mm});
            skLineSegment(sketch, "E1760", {"start": v(-338.96, 51.55) * mm, "end": v(-338.96, 53.18) * mm});
            skLineSegment(sketch, "E1761", {"start": v(-339.83, 54.05) * mm, "end": v(-350.36, 54.05) * mm});
            skLineSegment(sketch, "E1762", {"start": v(-350.36, 54.05) * mm, "end": v(-350.36, 64.7) * mm});
            skLineSegment(sketch, "E1763", {"start": v(-350.36, 64.7) * mm, "end": v(-348.13, 64.7) * mm});
            skFitSpline(sketch, "E1764", {"points": [v(-321.36, 78.05) * mm, v(-322.8, 78.05) * mm, v(-324.11, 77.28) * mm, v(-324.83, 76.05) * mm]});
            skFitSpline(sketch, "E1765", {"points": [v(-324.83, 76.05) * mm, v(-325.54, 74.8) * mm, v(-325.54, 73.28) * mm, v(-324.83, 72.05) * mm]});
            skFitSpline(sketch, "E1766", {"points": [v(-324.83, 72.05) * mm, v(-324.11, 70.8) * mm, v(-322.8, 70.05) * mm, v(-321.36, 70.05) * mm]});
            skFitSpline(sketch, "E1767", {"points": [v(-19.4, 203.8) * mm, v(-19.48, 203.95) * mm, v(-19.65, 204.05) * mm, v(-19.83, 204.05) * mm]});
            skFitSpline(sketch, "E1768", {"points": [v(-19.4, 203.8) * mm, v(-19.29, 203.61) * mm, v(-19.08, 203.52) * mm, v(-18.87, 203.55) * mm]});
            skFitSpline(sketch, "E1769", {"points": [v(-18.87, 203.55) * mm, v(-18.67, 203.6) * mm, v(-18.5, 203.75) * mm, v(-18.47, 203.96) * mm]});
            skFitSpline(sketch, "E1770", {"points": [v(-18.47, 203.96) * mm, v(-18.43, 204.17) * mm, v(-18.53, 204.37) * mm, v(-18.71, 204.48) * mm]});
            skFitSpline(sketch, "E1771", {"points": [v(-18.96, 204.91) * mm, v(-18.96, 204.73) * mm, v(-18.87, 204.57) * mm, v(-18.71, 204.48) * mm]});
            skFitSpline(sketch, "E1772", {"points": [v(-18.46, 207.05) * mm, v(-18.74, 207.05) * mm, v(-18.96, 206.82) * mm, v(-18.96, 206.55) * mm]});
            skFitSpline(sketch, "E1773", {"points": [v(-12.96, 206.55) * mm, v(-12.96, 206.82) * mm, v(-13.19, 207.05) * mm, v(-13.46, 207.05) * mm]});
            skLineSegment(sketch, "E1774", {"start": v(-347.26, 65.56) * mm, "end": v(-347.26, 73.1) * mm});
            skLineSegment(sketch, "E1775", {"start": v(-347.26, 73.1) * mm, "end": v(-344.26, 73.1) * mm});
            skLineSegment(sketch, "E1776", {"start": v(-344.26, 73.1) * mm, "end": v(-344.26, 71.82) * mm});
            skLineSegment(sketch, "E1777", {"start": v(-344.26, 71.82) * mm, "end": v(-340.26, 71.82) * mm});
            skLineSegment(sketch, "E1778", {"start": v(-340.26, 71.82) * mm, "end": v(-340.26, 73.1) * mm});
            skLineSegment(sketch, "E1779", {"start": v(-340.26, 73.1) * mm, "end": v(-337.26, 73.1) * mm});
            skLineSegment(sketch, "E1780", {"start": v(-337.26, 73.1) * mm, "end": v(-337.26, 76.3) * mm});
            skLineSegment(sketch, "E1781", {"start": v(-337.26, 76.3) * mm, "end": v(-340.26, 76.3) * mm});
            skLineSegment(sketch, "E1782", {"start": v(-340.26, 76.3) * mm, "end": v(-340.26, 77.57) * mm});
            skLineSegment(sketch, "E1783", {"start": v(-340.26, 77.57) * mm, "end": v(-344.26, 77.57) * mm});
            skLineSegment(sketch, "E1784", {"start": v(-344.26, 77.57) * mm, "end": v(-344.26, 76.3) * mm});
            skLineSegment(sketch, "E1785", {"start": v(-344.26, 76.3) * mm, "end": v(-347.26, 76.3) * mm});
            skLineSegment(sketch, "E1786", {"start": v(-347.26, 76.3) * mm, "end": v(-347.26, 85.04) * mm});
            skLineSegment(sketch, "E1787", {"start": v(-347.26, 85.04) * mm, "end": v(-25.17, 178.94) * mm});
            skFitSpline(sketch, "E1788", {"points": [v(-13.21, 204.48) * mm, v(-13.06, 204.57) * mm, v(-12.96, 204.73) * mm, v(-12.96, 204.91) * mm]});
            skFitSpline(sketch, "E1789", {"points": [v(-13.21, 204.48) * mm, v(-13.4, 204.37) * mm, v(-13.5, 204.17) * mm, v(-13.45, 203.96) * mm]});
            skFitSpline(sketch, "E1790", {"points": [v(-13.45, 203.96) * mm, v(-13.42, 203.75) * mm, v(-13.26, 203.6) * mm, v(-13.05, 203.55) * mm]});
            skFitSpline(sketch, "E1791", {"points": [v(-13.05, 203.55) * mm, v(-12.84, 203.52) * mm, v(-12.63, 203.61) * mm, v(-12.53, 203.8) * mm]});
            skFitSpline(sketch, "E1792", {"points": [v(-12.1, 204.05) * mm, v(-12.27, 204.05) * mm, v(-12.44, 203.95) * mm, v(-12.53, 203.8) * mm]});
            skLineSegment(sketch, "E1793", {"start": v(-18.96, 204.91) * mm, "end": v(-18.96, 206.55) * mm});
            skFitSpline(sketch, "E1794", {"points": [v(1.8, 203.8) * mm, v(1.72, 203.95) * mm, v(1.55, 204.05) * mm, v(1.37, 204.05) * mm]});
            skFitSpline(sketch, "E1795", {"points": [v(1.8, 203.8) * mm, v(1.91, 203.61) * mm, v(2.12, 203.52) * mm, v(2.33, 203.55) * mm]});
            skFitSpline(sketch, "E1796", {"points": [v(2.33, 203.55) * mm, v(2.53, 203.6) * mm, v(2.7, 203.75) * mm, v(2.73, 203.96) * mm]});
            skFitSpline(sketch, "E1797", {"points": [v(2.73, 203.96) * mm, v(2.77, 204.17) * mm, v(2.67, 204.37) * mm, v(2.49, 204.48) * mm]});
            skFitSpline(sketch, "E1798", {"points": [v(2.24, 204.91) * mm, v(2.24, 204.73) * mm, v(2.33, 204.57) * mm, v(2.49, 204.48) * mm]});
            skLineSegment(sketch, "E1799", {"start": v(-18.46, 207.05) * mm, "end": v(-13.46, 207.05) * mm});
            skFitSpline(sketch, "E1800", {"points": [v(2.74, 207.05) * mm, v(2.46, 207.05) * mm, v(2.24, 206.82) * mm, v(2.24, 206.55) * mm]});
            skLineSegment(sketch, "E1801", {"start": v(-12.96, 206.55) * mm, "end": v(-12.96, 204.91) * mm});
            skFitSpline(sketch, "E1802", {"points": [v(8.24, 206.55) * mm, v(8.24, 206.82) * mm, v(8.01, 207.05) * mm, v(7.74, 207.05) * mm]});
            skLineSegment(sketch, "E1803", {"start": v(-12.1, 204.05) * mm, "end": v(-6.96, 204.05) * mm});
            skLineSegment(sketch, "E1804", {"start": v(-6.96, 204.05) * mm, "end": v(-6.96, 201.05) * mm});
            skLineSegment(sketch, "E1805", {"start": v(-6.96, 201.05) * mm, "end": v(-8.24, 201.05) * mm});
            skLineSegment(sketch, "E1806", {"start": v(-8.24, 201.05) * mm, "end": v(-8.24, 197.05) * mm});
            skLineSegment(sketch, "E1807", {"start": v(-8.24, 197.05) * mm, "end": v(-6.96, 197.05) * mm});
            skLineSegment(sketch, "E1808", {"start": v(-6.96, 197.05) * mm, "end": v(-6.96, 194.05) * mm});
            skLineSegment(sketch, "E1809", {"start": v(-6.96, 194.05) * mm, "end": v(-3.76, 194.05) * mm});
            skLineSegment(sketch, "E1810", {"start": v(-3.76, 194.05) * mm, "end": v(-3.76, 197.05) * mm});
            skLineSegment(sketch, "E1811", {"start": v(-3.76, 197.05) * mm, "end": v(-2.49, 197.05) * mm});
            skLineSegment(sketch, "E1812", {"start": v(-2.49, 197.05) * mm, "end": v(-2.49, 201.05) * mm});
            skLineSegment(sketch, "E1813", {"start": v(-2.49, 201.05) * mm, "end": v(-3.76, 201.05) * mm});
            skLineSegment(sketch, "E1814", {"start": v(-3.76, 201.05) * mm, "end": v(-3.76, 204.05) * mm});
            skLineSegment(sketch, "E1815", {"start": v(-3.76, 204.05) * mm, "end": v(1.37, 204.05) * mm});
            skFitSpline(sketch, "E1816", {"points": [v(7.99, 204.48) * mm, v(8.14, 204.57) * mm, v(8.24, 204.73) * mm, v(8.24, 204.91) * mm]});
            skFitSpline(sketch, "E1817", {"points": [v(7.99, 204.48) * mm, v(7.8, 204.37) * mm, v(7.7, 204.17) * mm, v(7.75, 203.96) * mm]});
            skFitSpline(sketch, "E1818", {"points": [v(7.75, 203.96) * mm, v(7.78, 203.75) * mm, v(7.95, 203.6) * mm, v(8.15, 203.55) * mm]});
            skFitSpline(sketch, "E1819", {"points": [v(8.15, 203.55) * mm, v(8.36, 203.52) * mm, v(8.57, 203.61) * mm, v(8.67, 203.8) * mm]});
            skFitSpline(sketch, "E1820", {"points": [v(9.1, 204.05) * mm, v(8.93, 204.05) * mm, v(8.76, 203.95) * mm, v(8.67, 203.8) * mm]});
            skLineSegment(sketch, "E1821", {"start": v(2.24, 204.91) * mm, "end": v(2.24, 206.55) * mm});
            skLineSegment(sketch, "E1822", {"start": v(2.74, 207.05) * mm, "end": v(7.74, 207.05) * mm});
            skLineSegment(sketch, "E1823", {"start": v(8.24, 206.55) * mm, "end": v(8.24, 204.91) * mm});
            skFitSpline(sketch, "E1824", {"points": [v(-24.81, 179.42) * mm, v(-24.81, 179.2) * mm, v(-24.96, 179) * mm, v(-25.17, 178.94) * mm]});
            skFitSpline(sketch, "E1825", {"points": [v(-313.36, 70.05) * mm, v(-311.93, 70.05) * mm, v(-310.61, 70.8) * mm, v(-309.9, 72.05) * mm]});
            skFitSpline(sketch, "E1826", {"points": [v(-309.9, 72.05) * mm, v(-309.18, 73.28) * mm, v(-309.18, 74.8) * mm, v(-309.9, 76.05) * mm]});
            skFitSpline(sketch, "E1827", {"points": [v(-309.9, 76.05) * mm, v(-310.61, 77.28) * mm, v(-311.93, 78.05) * mm, v(-313.36, 78.05) * mm]});
            skLineSegment(sketch, "E1828", {"start": v(-19.83, 204.05) * mm, "end": v(-24.81, 204.05) * mm});
            skLineSegment(sketch, "E1829", {"start": v(-24.81, 204.05) * mm, "end": v(-24.81, 179.42) * mm});
            skFitSpline(sketch, "E1830", {"points": [v(-261.36, 78.05) * mm, v(-262.8, 78.05) * mm, v(-264.11, 77.28) * mm, v(-264.83, 76.05) * mm]});
            skFitSpline(sketch, "E1831", {"points": [v(-264.83, 76.05) * mm, v(-265.54, 74.8) * mm, v(-265.54, 73.28) * mm, v(-264.83, 72.05) * mm]});
            skFitSpline(sketch, "E1832", {"points": [v(-264.83, 72.05) * mm, v(-264.11, 70.8) * mm, v(-262.8, 70.05) * mm, v(-261.36, 70.05) * mm]});
            skLineSegment(sketch, "E1833", {"start": v(-313.36, 78.05) * mm, "end": v(-321.36, 78.05) * mm});
            skFitSpline(sketch, "E1834", {"points": [v(-253.36, 70.05) * mm, v(-251.93, 70.05) * mm, v(-250.61, 70.8) * mm, v(-249.9, 72.05) * mm]});
            skFitSpline(sketch, "E1835", {"points": [v(-249.9, 72.05) * mm, v(-249.18, 73.28) * mm, v(-249.18, 74.8) * mm, v(-249.9, 76.05) * mm]});
            skFitSpline(sketch, "E1836", {"points": [v(-249.9, 76.05) * mm, v(-250.61, 77.28) * mm, v(-251.93, 78.05) * mm, v(-253.36, 78.05) * mm]});
            skLineSegment(sketch, "E1837", {"start": v(-321.36, 70.05) * mm, "end": v(-313.36, 70.05) * mm});
            skFitSpline(sketch, "E1838", {"points": [v(-201.36, 78.05) * mm, v(-202.8, 78.05) * mm, v(-204.11, 77.28) * mm, v(-204.83, 76.05) * mm]});
            skFitSpline(sketch, "E1839", {"points": [v(-204.83, 76.05) * mm, v(-205.54, 74.8) * mm, v(-205.54, 73.28) * mm, v(-204.83, 72.05) * mm]});
            skFitSpline(sketch, "E1840", {"points": [v(-204.83, 72.05) * mm, v(-204.11, 70.8) * mm, v(-202.8, 70.05) * mm, v(-201.36, 70.05) * mm]});
            skLineSegment(sketch, "E1841", {"start": v(-253.36, 78.05) * mm, "end": v(-261.36, 78.05) * mm});
            skFitSpline(sketch, "E1842", {"points": [v(-193.36, 70.05) * mm, v(-191.93, 70.05) * mm, v(-190.61, 70.8) * mm, v(-189.9, 72.05) * mm]});
            skFitSpline(sketch, "E1843", {"points": [v(-189.9, 72.05) * mm, v(-189.18, 73.28) * mm, v(-189.18, 74.8) * mm, v(-189.9, 76.05) * mm]});
            skFitSpline(sketch, "E1844", {"points": [v(-189.9, 76.05) * mm, v(-190.61, 77.28) * mm, v(-191.93, 78.05) * mm, v(-193.36, 78.05) * mm]});
            skLineSegment(sketch, "E1845", {"start": v(-261.36, 70.05) * mm, "end": v(-253.36, 70.05) * mm});
            skFitSpline(sketch, "E1846", {"points": [v(-141.36, 78.05) * mm, v(-142.8, 78.05) * mm, v(-144.11, 77.28) * mm, v(-144.83, 76.05) * mm]});
            skFitSpline(sketch, "E1847", {"points": [v(-144.83, 76.05) * mm, v(-145.54, 74.8) * mm, v(-145.54, 73.28) * mm, v(-144.83, 72.05) * mm]});
            skFitSpline(sketch, "E1848", {"points": [v(-144.83, 72.05) * mm, v(-144.11, 70.8) * mm, v(-142.8, 70.05) * mm, v(-141.36, 70.05) * mm]});
            skLineSegment(sketch, "E1849", {"start": v(-193.36, 78.05) * mm, "end": v(-201.36, 78.05) * mm});
            skFitSpline(sketch, "E1850", {"points": [v(-133.36, 70.05) * mm, v(-131.93, 70.05) * mm, v(-130.61, 70.8) * mm, v(-129.9, 72.05) * mm]});
            skFitSpline(sketch, "E1851", {"points": [v(-129.9, 72.05) * mm, v(-129.18, 73.28) * mm, v(-129.18, 74.8) * mm, v(-129.9, 76.05) * mm]});
            skFitSpline(sketch, "E1852", {"points": [v(-129.9, 76.05) * mm, v(-130.61, 77.28) * mm, v(-131.93, 78.05) * mm, v(-133.36, 78.05) * mm]});
            skLineSegment(sketch, "E1853", {"start": v(-201.36, 70.05) * mm, "end": v(-193.36, 70.05) * mm});
            skFitSpline(sketch, "E1854", {"points": [v(-73.36, 77.05) * mm, v(-73.36, 78.48) * mm, v(-74.12, 79.8) * mm, v(-75.36, 80.51) * mm]});
            skFitSpline(sketch, "E1855", {"points": [v(-75.36, 80.51) * mm, v(-76.6, 81.22) * mm, v(-78.12, 81.22) * mm, v(-79.36, 80.51) * mm]});
            skFitSpline(sketch, "E1856", {"points": [v(-79.36, 80.51) * mm, v(-80.6, 79.8) * mm, v(-81.36, 78.48) * mm, v(-81.36, 77.05) * mm]});
            skLineSegment(sketch, "E1857", {"start": v(-133.36, 78.05) * mm, "end": v(-141.36, 78.05) * mm});
            skFitSpline(sketch, "E1858", {"points": [v(-81.36, 69.05) * mm, v(-81.36, 67.62) * mm, v(-80.6, 66.3) * mm, v(-79.36, 65.58) * mm]});
            skFitSpline(sketch, "E1859", {"points": [v(-79.36, 65.58) * mm, v(-78.12, 64.87) * mm, v(-76.6, 64.87) * mm, v(-75.36, 65.58) * mm]});
            skFitSpline(sketch, "E1860", {"points": [v(-75.36, 65.58) * mm, v(-74.12, 66.3) * mm, v(-73.36, 67.62) * mm, v(-73.36, 69.05) * mm]});
            skLineSegment(sketch, "E1861", {"start": v(-141.36, 70.05) * mm, "end": v(-133.36, 70.05) * mm});
            skFitSpline(sketch, "E1862", {"points": [v(-73.36, 117.05) * mm, v(-73.36, 118.48) * mm, v(-74.12, 119.8) * mm, v(-75.36, 120.51) * mm]});
            skFitSpline(sketch, "E1863", {"points": [v(-75.36, 120.51) * mm, v(-76.6, 121.22) * mm, v(-78.12, 121.22) * mm, v(-79.36, 120.51) * mm]});
            skFitSpline(sketch, "E1864", {"points": [v(-79.36, 120.51) * mm, v(-80.6, 119.8) * mm, v(-81.36, 118.48) * mm, v(-81.36, 117.05) * mm]});
            skLineSegment(sketch, "E1865", {"start": v(-73.36, 69.05) * mm, "end": v(-73.36, 77.05) * mm});
            skFitSpline(sketch, "E1866", {"points": [v(-81.36, 109.05) * mm, v(-81.36, 107.62) * mm, v(-80.6, 106.3) * mm, v(-79.36, 105.58) * mm]});
            skFitSpline(sketch, "E1867", {"points": [v(-79.36, 105.58) * mm, v(-78.12, 104.87) * mm, v(-76.6, 104.87) * mm, v(-75.36, 105.58) * mm]});
            skFitSpline(sketch, "E1868", {"points": [v(-75.36, 105.58) * mm, v(-74.12, 106.3) * mm, v(-73.36, 107.62) * mm, v(-73.36, 109.05) * mm]});
            skLineSegment(sketch, "E1869", {"start": v(-81.36, 77.05) * mm, "end": v(-81.36, 69.05) * mm});
            skFitSpline(sketch, "E1870", {"points": [v(11.64, 77.05) * mm, v(11.64, 78.48) * mm, v(10.88, 79.8) * mm, v(9.64, 80.51) * mm]});
            skFitSpline(sketch, "E1871", {"points": [v(9.64, 80.51) * mm, v(8.4, 81.22) * mm, v(6.88, 81.22) * mm, v(5.64, 80.51) * mm]});
            skFitSpline(sketch, "E1872", {"points": [v(5.64, 80.51) * mm, v(4.4, 79.8) * mm, v(3.64, 78.48) * mm, v(3.64, 77.05) * mm]});
            skLineSegment(sketch, "E1873", {"start": v(-73.36, 109.05) * mm, "end": v(-73.36, 117.05) * mm});
            skFitSpline(sketch, "E1874", {"points": [v(3.64, 69.05) * mm, v(3.64, 67.62) * mm, v(4.4, 66.3) * mm, v(5.64, 65.58) * mm]});
            skFitSpline(sketch, "E1875", {"points": [v(5.64, 65.58) * mm, v(6.88, 64.87) * mm, v(8.4, 64.87) * mm, v(9.64, 65.58) * mm]});
            skFitSpline(sketch, "E1876", {"points": [v(9.64, 65.58) * mm, v(10.88, 66.3) * mm, v(11.64, 67.62) * mm, v(11.64, 69.05) * mm]});
            skLineSegment(sketch, "E1877", {"start": v(-81.36, 117.05) * mm, "end": v(-81.36, 109.05) * mm});
            skFitSpline(sketch, "E1878", {"points": [v(11.64, 117.05) * mm, v(11.64, 118.48) * mm, v(10.88, 119.8) * mm, v(9.64, 120.51) * mm]});
            skFitSpline(sketch, "E1879", {"points": [v(9.64, 120.51) * mm, v(8.4, 121.22) * mm, v(6.88, 121.22) * mm, v(5.64, 120.51) * mm]});
            skFitSpline(sketch, "E1880", {"points": [v(5.64, 120.51) * mm, v(4.4, 119.8) * mm, v(3.64, 118.48) * mm, v(3.64, 117.05) * mm]});
            skLineSegment(sketch, "E1881", {"start": v(11.64, 69.05) * mm, "end": v(11.64, 77.05) * mm});
            skFitSpline(sketch, "E1882", {"points": [v(3.64, 109.05) * mm, v(3.64, 107.62) * mm, v(4.4, 106.3) * mm, v(5.64, 105.58) * mm]});
            skFitSpline(sketch, "E1883", {"points": [v(5.64, 105.58) * mm, v(6.88, 104.87) * mm, v(8.4, 104.87) * mm, v(9.64, 105.58) * mm]});
            skFitSpline(sketch, "E1884", {"points": [v(9.64, 105.58) * mm, v(10.88, 106.3) * mm, v(11.64, 107.62) * mm, v(11.64, 109.05) * mm]});
            skLineSegment(sketch, "E1885", {"start": v(3.64, 77.05) * mm, "end": v(3.64, 69.05) * mm});
            skFitSpline(sketch, "E1886", {"points": [v(11.64, 157.05) * mm, v(11.64, 158.48) * mm, v(10.88, 159.8) * mm, v(9.64, 160.51) * mm]});
            skFitSpline(sketch, "E1887", {"points": [v(9.64, 160.51) * mm, v(8.4, 161.22) * mm, v(6.88, 161.22) * mm, v(5.64, 160.51) * mm]});
            skFitSpline(sketch, "E1888", {"points": [v(5.64, 160.51) * mm, v(4.4, 159.8) * mm, v(3.64, 158.48) * mm, v(3.64, 157.05) * mm]});
            skLineSegment(sketch, "E1889", {"start": v(11.64, 109.05) * mm, "end": v(11.64, 117.05) * mm});
            skFitSpline(sketch, "E1890", {"points": [v(3.64, 149.05) * mm, v(3.64, 147.62) * mm, v(4.4, 146.3) * mm, v(5.64, 145.58) * mm]});
            skFitSpline(sketch, "E1891", {"points": [v(5.64, 145.58) * mm, v(6.88, 144.87) * mm, v(8.4, 144.87) * mm, v(9.64, 145.58) * mm]});
            skFitSpline(sketch, "E1892", {"points": [v(9.64, 145.58) * mm, v(10.88, 146.3) * mm, v(11.64, 147.62) * mm, v(11.64, 149.05) * mm]});
            skFitSpline(sketch, "E1893", {"points": [v(-7.9, 66.83) * mm, v(-7.9, 67.3) * mm, v(-8.15, 67.73) * mm, v(-8.55, 67.96) * mm]});
            skFitSpline(sketch, "E1894", {"points": [v(-8.55, 67.96) * mm, v(-8.95, 68.2) * mm, v(-9.45, 68.2) * mm, v(-9.85, 67.96) * mm]});
            skFitSpline(sketch, "E1895", {"points": [v(-9.85, 67.96) * mm, v(-10.25, 67.73) * mm, v(-10.5, 67.3) * mm, v(-10.5, 66.83) * mm]});
            skFitSpline(sketch, "E1896", {"points": [v(-10.5, 66.83) * mm, v(-10.5, 66.37) * mm, v(-10.25, 65.94) * mm, v(-9.85, 65.7) * mm]});
            skFitSpline(sketch, "E1897", {"points": [v(-9.85, 65.7) * mm, v(-9.45, 65.48) * mm, v(-8.95, 65.48) * mm, v(-8.55, 65.7) * mm]});
            skFitSpline(sketch, "E1898", {"points": [v(-8.55, 65.7) * mm, v(-8.15, 65.94) * mm, v(-7.9, 66.37) * mm, v(-7.9, 66.83) * mm]});
            skLineSegment(sketch, "E1899", {"start": v(3.64, 117.05) * mm, "end": v(3.64, 109.05) * mm});
            skFitSpline(sketch, "E1900", {"points": [v(-7.88, 150.03) * mm, v(-7.88, 150.5) * mm, v(-8.13, 150.93) * mm, v(-8.53, 151.16) * mm]});
            skFitSpline(sketch, "E1901", {"points": [v(-8.53, 151.16) * mm, v(-8.93, 151.4) * mm, v(-9.43, 151.4) * mm, v(-9.83, 151.16) * mm]});
            skFitSpline(sketch, "E1902", {"points": [v(-9.83, 151.16) * mm, v(-10.23, 150.93) * mm, v(-10.48, 150.5) * mm, v(-10.48, 150.03) * mm]});
            skFitSpline(sketch, "E1903", {"points": [v(-10.48, 150.03) * mm, v(-10.48, 149.57) * mm, v(-10.23, 149.14) * mm, v(-9.83, 148.9) * mm]});
            skFitSpline(sketch, "E1904", {"points": [v(-9.83, 148.9) * mm, v(-9.43, 148.68) * mm, v(-8.93, 148.68) * mm, v(-8.53, 148.9) * mm]});
            skFitSpline(sketch, "E1905", {"points": [v(-8.53, 148.9) * mm, v(-8.13, 149.14) * mm, v(-7.88, 149.57) * mm, v(-7.88, 150.03) * mm]});
            skLineSegment(sketch, "E1906", {"start": v(11.64, 149.05) * mm, "end": v(11.64, 157.05) * mm});
            skFitSpline(sketch, "E1907", {"points": [v(-56.1, 73.06) * mm, v(-56.1, 73.52) * mm, v(-56.34, 73.95) * mm, v(-56.74, 74.19) * mm]});
            skFitSpline(sketch, "E1908", {"points": [v(-56.74, 74.19) * mm, v(-57.15, 74.42) * mm, v(-57.64, 74.42) * mm, v(-58.05, 74.19) * mm]});
            skFitSpline(sketch, "E1909", {"points": [v(-58.05, 74.19) * mm, v(-58.45, 73.95) * mm, v(-58.7, 73.52) * mm, v(-58.7, 73.06) * mm]});
            skFitSpline(sketch, "E1910", {"points": [v(-58.7, 73.06) * mm, v(-58.7, 72.6) * mm, v(-58.45, 72.16) * mm, v(-58.05, 71.93) * mm]});
            skFitSpline(sketch, "E1911", {"points": [v(-58.05, 71.93) * mm, v(-57.64, 71.7) * mm, v(-57.15, 71.7) * mm, v(-56.74, 71.93) * mm]});
            skFitSpline(sketch, "E1912", {"points": [v(-56.74, 71.93) * mm, v(-56.34, 72.16) * mm, v(-56.1, 72.6) * mm, v(-56.1, 73.06) * mm]});
            skLineSegment(sketch, "E1913", {"start": v(3.64, 157.05) * mm, "end": v(3.64, 149.05) * mm});
            skFitSpline(sketch, "E1914", {"points": [v(-56.08, 147.56) * mm, v(-56.08, 148.02) * mm, v(-56.32, 148.45) * mm, v(-56.73, 148.68) * mm]});
            skFitSpline(sketch, "E1915", {"points": [v(-56.73, 148.68) * mm, v(-57.13, 148.92) * mm, v(-57.62, 148.92) * mm, v(-58.03, 148.68) * mm]});
            skFitSpline(sketch, "E1916", {"points": [v(-58.03, 148.68) * mm, v(-58.43, 148.45) * mm, v(-58.68, 148.02) * mm, v(-58.68, 147.56) * mm]});
            skFitSpline(sketch, "E1917", {"points": [v(-58.68, 147.56) * mm, v(-58.68, 147.1) * mm, v(-58.43, 146.66) * mm, v(-58.03, 146.43) * mm]});
            skFitSpline(sketch, "E1918", {"points": [v(-58.03, 146.43) * mm, v(-57.62, 146.2) * mm, v(-57.13, 146.2) * mm, v(-56.73, 146.43) * mm]});
            skFitSpline(sketch, "E1919", {"points": [v(-56.73, 146.43) * mm, v(-56.32, 146.66) * mm, v(-56.08, 147.1) * mm, v(-56.08, 147.56) * mm]});
            skFitSpline(sketch, "E1920", {"points": [v(-4.58, -16.45) * mm, v(-4.4, -16.45) * mm, v(-4.23, -16.36) * mm, v(-4.14, -16.2) * mm]});
            skFitSpline(sketch, "E1921", {"points": [v(-3.46, -16.89) * mm, v(-3.28, -16.78) * mm, v(-3.18, -16.57) * mm, v(-3.22, -16.37) * mm]});
            skFitSpline(sketch, "E1922", {"points": [v(-3.22, -16.37) * mm, v(-3.26, -16.16) * mm, v(-3.42, -16) * mm, v(-3.62, -15.96) * mm]});
            skFitSpline(sketch, "E1923", {"points": [v(-3.62, -15.96) * mm, v(-3.83, -15.92) * mm, v(-4.04, -16.02) * mm, v(-4.14, -16.2) * mm]});
            skFitSpline(sketch, "E1924", {"points": [v(-3.46, -16.89) * mm, v(-3.62, -16.98) * mm, v(-3.71, -17.14) * mm, v(-3.71, -17.32) * mm]});
            skFitSpline(sketch, "E1925", {"points": [v(-3.71, -21.79) * mm, v(-3.71, -21.97) * mm, v(-3.62, -22.13) * mm, v(-3.46, -22.22) * mm]});
            skFitSpline(sketch, "E1926", {"points": [v(-4.14, -22.9) * mm, v(-4.04, -23.09) * mm, v(-3.83, -23.18) * mm, v(-3.62, -23.15) * mm]});
            skFitSpline(sketch, "E1927", {"points": [v(-3.62, -23.15) * mm, v(-3.42, -23.1) * mm, v(-3.26, -22.95) * mm, v(-3.22, -22.74) * mm]});
            skFitSpline(sketch, "E1928", {"points": [v(-3.22, -22.74) * mm, v(-3.18, -22.53) * mm, v(-3.28, -22.33) * mm, v(-3.46, -22.22) * mm]});
            skFitSpline(sketch, "E1929", {"points": [v(-4.14, -22.9) * mm, v(-4.23, -22.75) * mm, v(-4.4, -22.65) * mm, v(-4.58, -22.65) * mm]});
            skFitSpline(sketch, "E1930", {"points": [v(-6.15, -22.65) * mm, v(-6.32, -22.65) * mm, v(-6.49, -22.75) * mm, v(-6.58, -22.9) * mm]});
            skFitSpline(sketch, "E1931", {"points": [v(-7.26, -22.22) * mm, v(-7.44, -22.33) * mm, v(-7.54, -22.53) * mm, v(-7.5, -22.74) * mm]});
            skFitSpline(sketch, "E1932", {"points": [v(-7.5, -22.74) * mm, v(-7.47, -22.95) * mm, v(-7.3, -23.1) * mm, v(-7.1, -23.15) * mm]});
            skFitSpline(sketch, "E1933", {"points": [v(-7.1, -23.15) * mm, v(-6.9, -23.18) * mm, v(-6.68, -23.09) * mm, v(-6.58, -22.9) * mm]});
            skFitSpline(sketch, "E1934", {"points": [v(-7.26, -22.22) * mm, v(-7.1, -22.13) * mm, v(-7.01, -21.97) * mm, v(-7.01, -21.79) * mm]});
            skFitSpline(sketch, "E1935", {"points": [v(-7.01, -17.32) * mm, v(-7.01, -17.14) * mm, v(-7.1, -16.98) * mm, v(-7.26, -16.89) * mm]});
            skFitSpline(sketch, "E1936", {"points": [v(-6.58, -16.2) * mm, v(-6.68, -16.02) * mm, v(-6.9, -15.92) * mm, v(-7.1, -15.96) * mm]});
            skFitSpline(sketch, "E1937", {"points": [v(-7.1, -15.96) * mm, v(-7.3, -16) * mm, v(-7.47, -16.16) * mm, v(-7.5, -16.37) * mm]});
            skFitSpline(sketch, "E1938", {"points": [v(-7.5, -16.37) * mm, v(-7.54, -16.57) * mm, v(-7.44, -16.78) * mm, v(-7.26, -16.89) * mm]});
            skFitSpline(sketch, "E1939", {"points": [v(-6.58, -16.2) * mm, v(-6.49, -16.36) * mm, v(-6.32, -16.45) * mm, v(-6.15, -16.45) * mm]});
            skLineSegment(sketch, "E1940", {"start": v(-3.71, -17.32) * mm, "end": v(-3.71, -21.79) * mm});
            skFitSpline(sketch, "E1941", {"points": [v(-4.58, 4.75) * mm, v(-4.4, 4.75) * mm, v(-4.23, 4.84) * mm, v(-4.14, 5) * mm]});
            skFitSpline(sketch, "E1942", {"points": [v(-3.46, 4.31) * mm, v(-3.28, 4.42) * mm, v(-3.18, 4.63) * mm, v(-3.22, 4.83) * mm]});
            skFitSpline(sketch, "E1943", {"points": [v(-3.22, 4.83) * mm, v(-3.26, 5.04) * mm, v(-3.42, 5.2) * mm, v(-3.62, 5.24) * mm]});
            skFitSpline(sketch, "E1944", {"points": [v(-3.62, 5.24) * mm, v(-3.83, 5.28) * mm, v(-4.04, 5.18) * mm, v(-4.14, 5) * mm]});
            skFitSpline(sketch, "E1945", {"points": [v(-3.46, 4.31) * mm, v(-3.62, 4.22) * mm, v(-3.71, 4.06) * mm, v(-3.71, 3.88) * mm]});
            skLineSegment(sketch, "E1946", {"start": v(-4.58, -22.65) * mm, "end": v(-6.15, -22.65) * mm});
            skFitSpline(sketch, "E1947", {"points": [v(-3.71, -0.59) * mm, v(-3.71, -0.77) * mm, v(-3.62, -0.93) * mm, v(-3.46, -1.02) * mm]});
            skFitSpline(sketch, "E1948", {"points": [v(-4.14, -1.7) * mm, v(-4.04, -1.89) * mm, v(-3.83, -1.98) * mm, v(-3.62, -1.95) * mm]});
            skFitSpline(sketch, "E1949", {"points": [v(-3.62, -1.95) * mm, v(-3.42, -1.9) * mm, v(-3.26, -1.75) * mm, v(-3.22, -1.54) * mm]});
            skFitSpline(sketch, "E1950", {"points": [v(-3.22, -1.54) * mm, v(-3.18, -1.33) * mm, v(-3.28, -1.13) * mm, v(-3.46, -1.02) * mm]});
            skFitSpline(sketch, "E1951", {"points": [v(-4.14, -1.7) * mm, v(-4.23, -1.55) * mm, v(-4.4, -1.45) * mm, v(-4.58, -1.45) * mm]});
            skLineSegment(sketch, "E1952", {"start": v(-7.01, -21.79) * mm, "end": v(-7.01, -17.32) * mm});
            skFitSpline(sketch, "E1953", {"points": [v(-6.15, -1.45) * mm, v(-6.32, -1.45) * mm, v(-6.49, -1.55) * mm, v(-6.58, -1.7) * mm]});
            skFitSpline(sketch, "E1954", {"points": [v(-7.26, -1.02) * mm, v(-7.44, -1.13) * mm, v(-7.54, -1.33) * mm, v(-7.5, -1.54) * mm]});
            skFitSpline(sketch, "E1955", {"points": [v(-7.5, -1.54) * mm, v(-7.47, -1.75) * mm, v(-7.3, -1.9) * mm, v(-7.1, -1.95) * mm]});
            skFitSpline(sketch, "E1956", {"points": [v(-7.1, -1.95) * mm, v(-6.9, -1.98) * mm, v(-6.68, -1.89) * mm, v(-6.58, -1.7) * mm]});
            skFitSpline(sketch, "E1957", {"points": [v(-7.26, -1.02) * mm, v(-7.1, -0.93) * mm, v(-7.01, -0.77) * mm, v(-7.01, -0.59) * mm]});
            skLineSegment(sketch, "E1958", {"start": v(-6.15, -16.45) * mm, "end": v(-4.58, -16.45) * mm});
            skFitSpline(sketch, "E1959", {"points": [v(-7.01, 3.88) * mm, v(-7.01, 4.06) * mm, v(-7.1, 4.22) * mm, v(-7.26, 4.31) * mm]});
            skFitSpline(sketch, "E1960", {"points": [v(-6.58, 5) * mm, v(-6.68, 5.18) * mm, v(-6.9, 5.28) * mm, v(-7.1, 5.24) * mm]});
            skFitSpline(sketch, "E1961", {"points": [v(-7.1, 5.24) * mm, v(-7.3, 5.2) * mm, v(-7.47, 5.04) * mm, v(-7.5, 4.83) * mm]});
            skFitSpline(sketch, "E1962", {"points": [v(-7.5, 4.83) * mm, v(-7.54, 4.63) * mm, v(-7.44, 4.42) * mm, v(-7.26, 4.31) * mm]});
            skFitSpline(sketch, "E1963", {"points": [v(-6.58, 5) * mm, v(-6.49, 4.84) * mm, v(-6.32, 4.75) * mm, v(-6.15, 4.75) * mm]});
            skLineSegment(sketch, "E1964", {"start": v(-3.71, 3.88) * mm, "end": v(-3.71, -0.59) * mm});
            skFitSpline(sketch, "E1965", {"points": [v(-3.76, -8.95) * mm, v(-3.76, -8.38) * mm, v(-4.07, -7.85) * mm, v(-4.56, -7.57) * mm]});
            skFitSpline(sketch, "E1966", {"points": [v(-4.56, -7.57) * mm, v(-5.06, -7.28) * mm, v(-5.67, -7.28) * mm, v(-6.16, -7.57) * mm]});
            skFitSpline(sketch, "E1967", {"points": [v(-6.16, -7.57) * mm, v(-6.66, -7.85) * mm, v(-6.96, -8.38) * mm, v(-6.96, -8.95) * mm]});
            skFitSpline(sketch, "E1968", {"points": [v(-6.96, -8.95) * mm, v(-6.96, -9.84) * mm, v(-6.24, -10.55) * mm, v(-5.36, -10.55) * mm]});
            skFitSpline(sketch, "E1969", {"points": [v(-5.36, -10.55) * mm, v(-4.48, -10.55) * mm, v(-3.76, -9.84) * mm, v(-3.76, -8.95) * mm]});
            skLineSegment(sketch, "E1970", {"start": v(-4.58, -1.45) * mm, "end": v(-6.15, -1.45) * mm});
            skLineSegment(sketch, "E1971", {"start": v(-7.01, -0.59) * mm, "end": v(-7.01, 3.88) * mm});
            skFitSpline(sketch, "E1972", {"points": [v(-198.79, 163.83) * mm, v(-198.79, 164) * mm, v(-198.88, 164.17) * mm, v(-199.04, 164.26) * mm]});
            skFitSpline(sketch, "E1973", {"points": [v(-198.35, 164.94) * mm, v(-198.46, 165.12) * mm, v(-198.67, 165.22) * mm, v(-198.87, 165.18) * mm]});
            skFitSpline(sketch, "E1974", {"points": [v(-198.87, 165.18) * mm, v(-199.08, 165.15) * mm, v(-199.24, 164.99) * mm, v(-199.28, 164.78) * mm]});
            skFitSpline(sketch, "E1975", {"points": [v(-199.28, 164.78) * mm, v(-199.32, 164.57) * mm, v(-199.22, 164.36) * mm, v(-199.04, 164.26) * mm]});
            skFitSpline(sketch, "E1976", {"points": [v(-198.35, 164.94) * mm, v(-198.26, 164.79) * mm, v(-198.1, 164.7) * mm, v(-197.92, 164.7) * mm]});
            skLineSegment(sketch, "E1977", {"start": v(-6.15, 4.75) * mm, "end": v(-4.58, 4.75) * mm});
            skFitSpline(sketch, "E1978", {"points": [v(-196.29, 164.7) * mm, v(-196.01, 164.7) * mm, v(-195.79, 164.92) * mm, v(-195.79, 165.2) * mm]});
            skFitSpline(sketch, "E1979", {"points": [v(-195.79, 170.2) * mm, v(-195.79, 170.47) * mm, v(-196.01, 170.7) * mm, v(-196.29, 170.7) * mm]});
            skLineSegment(sketch, "E1980", {"start": v(-208.79, 155.5) * mm, "end": v(-208.79, 158.7) * mm});
            skLineSegment(sketch, "E1981", {"start": v(-208.79, 158.7) * mm, "end": v(-205.79, 158.7) * mm});
            skLineSegment(sketch, "E1982", {"start": v(-205.79, 158.7) * mm, "end": v(-205.79, 159.97) * mm});
            skLineSegment(sketch, "E1983", {"start": v(-205.79, 159.97) * mm, "end": v(-201.79, 159.97) * mm});
            skLineSegment(sketch, "E1984", {"start": v(-201.79, 159.97) * mm, "end": v(-201.79, 158.7) * mm});
            skLineSegment(sketch, "E1985", {"start": v(-201.79, 158.7) * mm, "end": v(-198.79, 158.7) * mm});
            skLineSegment(sketch, "E1986", {"start": v(-198.79, 158.7) * mm, "end": v(-198.79, 163.83) * mm});
            skFitSpline(sketch, "E1987", {"points": [v(-197.92, 170.7) * mm, v(-198.1, 170.7) * mm, v(-198.26, 170.6) * mm, v(-198.35, 170.44) * mm]});
            skFitSpline(sketch, "E1988", {"points": [v(-199.04, 171.12) * mm, v(-199.22, 171.02) * mm, v(-199.32, 170.81) * mm, v(-199.28, 170.6) * mm]});
            skFitSpline(sketch, "E1989", {"points": [v(-199.28, 170.6) * mm, v(-199.24, 170.4) * mm, v(-199.08, 170.24) * mm, v(-198.87, 170.2) * mm]});
            skFitSpline(sketch, "E1990", {"points": [v(-198.87, 170.2) * mm, v(-198.67, 170.16) * mm, v(-198.46, 170.26) * mm, v(-198.35, 170.44) * mm]});
            skFitSpline(sketch, "E1991", {"points": [v(-199.04, 171.12) * mm, v(-198.88, 171.21) * mm, v(-198.79, 171.38) * mm, v(-198.79, 171.56) * mm]});
            skLineSegment(sketch, "E1992", {"start": v(-197.92, 164.7) * mm, "end": v(-196.29, 164.7) * mm});
            skLineSegment(sketch, "E1993", {"start": v(-195.79, 165.2) * mm, "end": v(-195.79, 170.2) * mm});
            skFitSpline(sketch, "E1994", {"points": [v(-244.79, 171.1) * mm, v(-245.32, 171.1) * mm, v(-245.83, 170.88) * mm, v(-246.2, 170.5) * mm]});
            skFitSpline(sketch, "E1995", {"points": [v(-246.2, 170.5) * mm, v(-246.58, 170.13) * mm, v(-246.79, 169.62) * mm, v(-246.79, 169.1) * mm]});
            skLineSegment(sketch, "E1996", {"start": v(-196.29, 170.7) * mm, "end": v(-197.92, 170.7) * mm});
            skFitSpline(sketch, "E1997", {"points": [v(-246.79, 135.1) * mm, v(-246.79, 134.56) * mm, v(-246.58, 134.05) * mm, v(-246.2, 133.68) * mm]});
            skFitSpline(sketch, "E1998", {"points": [v(-246.2, 133.68) * mm, v(-245.83, 133.3) * mm, v(-245.32, 133.1) * mm, v(-244.79, 133.1) * mm]});
            skLineSegment(sketch, "E1999", {"start": v(-198.79, 171.56) * mm, "end": v(-198.79, 176.1) * mm});
            skLineSegment(sketch, "E2000", {"start": v(-198.79, 176.1) * mm, "end": v(-203.99, 176.1) * mm});
            skFitSpline(sketch, "E2001", {"points": [v(-198.79, 142.63) * mm, v(-198.79, 142.8) * mm, v(-198.88, 142.97) * mm, v(-199.04, 143.06) * mm]});
            skFitSpline(sketch, "E2002", {"points": [v(-198.35, 143.74) * mm, v(-198.46, 143.92) * mm, v(-198.67, 144.02) * mm, v(-198.87, 143.98) * mm]});
            skFitSpline(sketch, "E2003", {"points": [v(-198.87, 143.98) * mm, v(-199.08, 143.95) * mm, v(-199.24, 143.79) * mm, v(-199.28, 143.58) * mm]});
            skFitSpline(sketch, "E2004", {"points": [v(-199.28, 143.58) * mm, v(-199.32, 143.37) * mm, v(-199.22, 143.16) * mm, v(-199.04, 143.06) * mm]});
            skFitSpline(sketch, "E2005", {"points": [v(-198.35, 143.74) * mm, v(-198.26, 143.59) * mm, v(-198.1, 143.5) * mm, v(-197.92, 143.5) * mm]});
            skLineSegment(sketch, "E2006", {"start": v(-213.3, 171.1) * mm, "end": v(-244.79, 171.1) * mm});
            skFitSpline(sketch, "E2007", {"points": [v(-196.29, 143.5) * mm, v(-196.01, 143.5) * mm, v(-195.79, 143.72) * mm, v(-195.79, 144) * mm]});
            skLineSegment(sketch, "E2008", {"start": v(-246.79, 169.1) * mm, "end": v(-246.79, 135.1) * mm});
            skFitSpline(sketch, "E2009", {"points": [v(-195.79, 149) * mm, v(-195.79, 149.27) * mm, v(-196.01, 149.5) * mm, v(-196.29, 149.5) * mm]});
            skLineSegment(sketch, "E2010", {"start": v(-244.79, 133.1) * mm, "end": v(-207.76, 133.1) * mm});
            skFitSpline(sketch, "E2011", {"points": [v(-197.92, 149.5) * mm, v(-198.1, 149.5) * mm, v(-198.26, 149.4) * mm, v(-198.35, 149.24) * mm]});
            skFitSpline(sketch, "E2012", {"points": [v(-199.04, 149.92) * mm, v(-199.22, 149.82) * mm, v(-199.32, 149.61) * mm, v(-199.28, 149.4) * mm]});
            skFitSpline(sketch, "E2013", {"points": [v(-199.28, 149.4) * mm, v(-199.24, 149.2) * mm, v(-199.08, 149.04) * mm, v(-198.87, 149) * mm]});
            skFitSpline(sketch, "E2014", {"points": [v(-198.87, 149) * mm, v(-198.67, 148.96) * mm, v(-198.46, 149.06) * mm, v(-198.35, 149.24) * mm]});
            skFitSpline(sketch, "E2015", {"points": [v(-199.04, 149.92) * mm, v(-198.88, 150.01) * mm, v(-198.79, 150.18) * mm, v(-198.79, 150.36) * mm]});
            skLineSegment(sketch, "E2016", {"start": v(-197.92, 143.5) * mm, "end": v(-196.29, 143.5) * mm});
            skFitSpline(sketch, "E2017", {"points": [v(-215.47, 152.1) * mm, v(-215.47, 156.06) * mm, v(-217.59, 159.72) * mm, v(-221.02, 161.7) * mm]});
            skFitSpline(sketch, "E2018", {"points": [v(-221.02, 161.7) * mm, v(-224.45, 163.69) * mm, v(-228.69, 163.69) * mm, v(-232.12, 161.7) * mm]});
            skFitSpline(sketch, "E2019", {"points": [v(-232.12, 161.7) * mm, v(-235.55, 159.72) * mm, v(-237.67, 156.06) * mm, v(-237.67, 152.1) * mm]});
            skFitSpline(sketch, "E2020", {"points": [v(-237.67, 152.1) * mm, v(-237.67, 148.13) * mm, v(-235.55, 144.46) * mm, v(-232.12, 142.48) * mm]});
            skFitSpline(sketch, "E2021", {"points": [v(-232.12, 142.48) * mm, v(-228.69, 140.5) * mm, v(-224.45, 140.5) * mm, v(-221.02, 142.48) * mm]});
            skFitSpline(sketch, "E2022", {"points": [v(-221.02, 142.48) * mm, v(-217.59, 144.46) * mm, v(-215.47, 148.13) * mm, v(-215.47, 152.1) * mm]});
            skLineSegment(sketch, "E2023", {"start": v(-195.79, 144) * mm, "end": v(-195.79, 149) * mm});
            skFitSpline(sketch, "E2024", {"points": [v(-209.47, 136.6) * mm, v(-209.47, 137.16) * mm, v(-209.77, 137.7) * mm, v(-210.27, 137.98) * mm]});
            skFitSpline(sketch, "E2025", {"points": [v(-210.27, 137.98) * mm, v(-210.77, 138.26) * mm, v(-211.37, 138.26) * mm, v(-211.87, 137.98) * mm]});
            skFitSpline(sketch, "E2026", {"points": [v(-211.87, 137.98) * mm, v(-212.37, 137.7) * mm, v(-212.67, 137.16) * mm, v(-212.67, 136.6) * mm]});
            skFitSpline(sketch, "E2027", {"points": [v(-212.67, 136.6) * mm, v(-212.67, 136.02) * mm, v(-212.37, 135.5) * mm, v(-211.87, 135.2) * mm]});
            skFitSpline(sketch, "E2028", {"points": [v(-211.87, 135.2) * mm, v(-211.37, 134.92) * mm, v(-210.77, 134.92) * mm, v(-210.27, 135.2) * mm]});
            skFitSpline(sketch, "E2029", {"points": [v(-210.27, 135.2) * mm, v(-209.77, 135.5) * mm, v(-209.47, 136.02) * mm, v(-209.47, 136.6) * mm]});
            skLineSegment(sketch, "E2030", {"start": v(-196.29, 149.5) * mm, "end": v(-197.92, 149.5) * mm});
            skFitSpline(sketch, "E2031", {"points": [v(-240.47, 136.6) * mm, v(-240.47, 137.16) * mm, v(-240.77, 137.7) * mm, v(-241.27, 137.98) * mm]});
            skFitSpline(sketch, "E2032", {"points": [v(-241.27, 137.98) * mm, v(-241.77, 138.26) * mm, v(-242.37, 138.26) * mm, v(-242.87, 137.98) * mm]});
            skFitSpline(sketch, "E2033", {"points": [v(-242.87, 137.98) * mm, v(-243.37, 137.7) * mm, v(-243.67, 137.16) * mm, v(-243.67, 136.6) * mm]});
            skFitSpline(sketch, "E2034", {"points": [v(-243.67, 136.6) * mm, v(-243.67, 135.7) * mm, v(-242.95, 135) * mm, v(-242.07, 135) * mm]});
            skFitSpline(sketch, "E2035", {"points": [v(-242.07, 135) * mm, v(-241.19, 135) * mm, v(-240.47, 135.7) * mm, v(-240.47, 136.6) * mm]});
            skLineSegment(sketch, "E2036", {"start": v(-198.79, 150.36) * mm, "end": v(-198.79, 155.5) * mm});
            skLineSegment(sketch, "E2037", {"start": v(-198.79, 155.5) * mm, "end": v(-201.79, 155.5) * mm});
            skLineSegment(sketch, "E2038", {"start": v(-201.79, 155.5) * mm, "end": v(-201.79, 154.22) * mm});
            skLineSegment(sketch, "E2039", {"start": v(-201.79, 154.22) * mm, "end": v(-205.79, 154.22) * mm});
            skLineSegment(sketch, "E2040", {"start": v(-205.79, 154.22) * mm, "end": v(-205.79, 155.5) * mm});
            skLineSegment(sketch, "E2041", {"start": v(-205.79, 155.5) * mm, "end": v(-208.79, 155.5) * mm});
            skFitSpline(sketch, "E2042", {"points": [v(-209.47, 167.6) * mm, v(-209.47, 168.16) * mm, v(-209.77, 168.7) * mm, v(-210.27, 168.98) * mm]});
            skFitSpline(sketch, "E2043", {"points": [v(-210.27, 168.98) * mm, v(-210.77, 169.26) * mm, v(-211.37, 169.26) * mm, v(-211.87, 168.98) * mm]});
            skFitSpline(sketch, "E2044", {"points": [v(-211.87, 168.98) * mm, v(-212.37, 168.7) * mm, v(-212.67, 168.16) * mm, v(-212.67, 167.6) * mm]});
            skFitSpline(sketch, "E2045", {"points": [v(-212.67, 167.6) * mm, v(-212.67, 167.02) * mm, v(-212.37, 166.5) * mm, v(-211.87, 166.2) * mm]});
            skFitSpline(sketch, "E2046", {"points": [v(-211.87, 166.2) * mm, v(-211.37, 165.92) * mm, v(-210.77, 165.92) * mm, v(-210.27, 166.2) * mm]});
            skFitSpline(sketch, "E2047", {"points": [v(-210.27, 166.2) * mm, v(-209.77, 166.5) * mm, v(-209.47, 167.02) * mm, v(-209.47, 167.6) * mm]});
            skFitSpline(sketch, "E2048", {"points": [v(-240.47, 167.6) * mm, v(-240.47, 168.16) * mm, v(-240.77, 168.7) * mm, v(-241.27, 168.98) * mm]});
            skFitSpline(sketch, "E2049", {"points": [v(-241.27, 168.98) * mm, v(-241.77, 169.26) * mm, v(-242.37, 169.26) * mm, v(-242.87, 168.98) * mm]});
            skFitSpline(sketch, "E2050", {"points": [v(-242.87, 168.98) * mm, v(-243.37, 168.7) * mm, v(-243.67, 168.16) * mm, v(-243.67, 167.6) * mm]});
            skFitSpline(sketch, "E2051", {"points": [v(-243.67, 167.6) * mm, v(-243.67, 166.7) * mm, v(-242.95, 166) * mm, v(-242.07, 166) * mm]});
            skFitSpline(sketch, "E2052", {"points": [v(-242.07, 166) * mm, v(-241.19, 166) * mm, v(-240.47, 166.7) * mm, v(-240.47, 167.6) * mm]});
            skLineSegment(sketch, "E2053", {"start": v(-198.79, 138.1) * mm, "end": v(-198.79, 142.63) * mm});
            skFitSpline(sketch, "E2054", {"points": [v(-346.89, -13.67) * mm, v(-348.21, -13.67) * mm, v(-349.49, -14.2) * mm, v(-350.42, -15.13) * mm]});
            skFitSpline(sketch, "E2055", {"points": [v(-350.42, -15.13) * mm, v(-351.36, -16.07) * mm, v(-351.89, -17.34) * mm, v(-351.89, -18.67) * mm]});
            skLineSegment(sketch, "E2056", {"start": v(-119.27, -20.05) * mm, "end": v(-324.15, -20.05) * mm});
            skFitSpline(sketch, "E2057", {"points": [v(-351.89, -53.05) * mm, v(-351.89, -55.82) * mm, v(-349.65, -58.05) * mm, v(-346.89, -58.05) * mm]});
            skLineSegment(sketch, "E2058", {"start": v(-325.1, -19.35) * mm, "end": v(-326.67, -14.37) * mm});
            skFitSpline(sketch, "E2059", {"points": [v(-316.71, -58.55) * mm, v(-316.71, -58.28) * mm, v(-316.94, -58.05) * mm, v(-317.21, -58.05) * mm]});
            skFitSpline(sketch, "E2060", {"points": [v(-296.21, -58.05) * mm, v(-296.35, -58.05) * mm, v(-296.47, -58.1) * mm, v(-296.57, -58.2) * mm]});
            skFitSpline(sketch, "E2061", {"points": [v(-296.57, -58.2) * mm, v(-296.66, -58.3) * mm, v(-296.71, -58.42) * mm, v(-296.71, -58.55) * mm]});
            skLineSegment(sketch, "E2062", {"start": v(-327.62, -13.67) * mm, "end": v(-346.89, -13.67) * mm});
            skFitSpline(sketch, "E2063", {"points": [v(-146.7, -58.55) * mm, v(-146.7, -58.28) * mm, v(-146.93, -58.05) * mm, v(-147.2, -58.05) * mm]});
            skLineSegment(sketch, "E2064", {"start": v(-351.89, -18.67) * mm, "end": v(-351.89, -53.05) * mm});
            skFitSpline(sketch, "E2065", {"points": [v(-146.7, -64.05) * mm, v(-146.7, -65.16) * mm, v(-145.81, -66.05) * mm, v(-144.7, -66.05) * mm]});
            skLineSegment(sketch, "E2066", {"start": v(-346.89, -58.05) * mm, "end": v(-317.21, -58.05) * mm});
            skFitSpline(sketch, "E2067", {"points": [v(-133.44, -65.27) * mm, v(-132.32, -63.63) * mm, v(-132.6, -61.4) * mm, v(-134.1, -60.1) * mm]});
            skFitSpline(sketch, "E2068", {"points": [v(-134.1, -60.1) * mm, v(-135.6, -58.78) * mm, v(-137.83, -58.78) * mm, v(-139.32, -60.1) * mm]});
            skFitSpline(sketch, "E2069", {"points": [v(-139.32, -60.1) * mm, v(-140.81, -61.4) * mm, v(-141.1, -63.63) * mm, v(-139.98, -65.27) * mm]});
            skLineSegment(sketch, "E2070", {"start": v(-296.21, -58.05) * mm, "end": v(-147.2, -58.05) * mm});
            skFitSpline(sketch, "E2071", {"points": [v(-128.7, -66.05) * mm, v(-128.18, -66.05) * mm, v(-127.67, -65.84) * mm, v(-127.3, -65.47) * mm]});
            skFitSpline(sketch, "E2072", {"points": [v(-127.3, -65.47) * mm, v(-126.92, -65.1) * mm, v(-126.7, -64.58) * mm, v(-126.7, -64.05) * mm]});
            skLineSegment(sketch, "E2073", {"start": v(-146.7, -58.55) * mm, "end": v(-146.7, -64.05) * mm});
            skFitSpline(sketch, "E2074", {"points": [v(-126.2, -58.05) * mm, v(-126.49, -58.05) * mm, v(-126.7, -58.28) * mm, v(-126.7, -58.55) * mm]});
            skLineSegment(sketch, "E2075", {"start": v(-144.7, -66.05) * mm, "end": v(-140.4, -66.05) * mm});
            skFitSpline(sketch, "E2076", {"points": [v(-96.54, -58.05) * mm, v(-93.78, -58.05) * mm, v(-91.54, -55.82) * mm, v(-91.54, -53.05) * mm]});
            skLineSegment(sketch, "E2077", {"start": v(-133.03, -66.05) * mm, "end": v(-128.7, -66.05) * mm});
            skFitSpline(sketch, "E2078", {"points": [v(-91.54, -18.67) * mm, v(-91.54, -15.9) * mm, v(-93.78, -13.67) * mm, v(-96.54, -13.67) * mm]});
            skLineSegment(sketch, "E2079", {"start": v(-126.7, -64.05) * mm, "end": v(-126.7, -58.55) * mm});
            skLineSegment(sketch, "E2080", {"start": v(-126.2, -58.05) * mm, "end": v(-96.54, -58.05) * mm});
            skFitSpline(sketch, "E2081", {"points": [v(-102.32, -31.17) * mm, v(-102.5, -31.17) * mm, v(-102.66, -31.26) * mm, v(-102.75, -31.42) * mm]});
            skFitSpline(sketch, "E2082", {"points": [v(-103.44, -30.73) * mm, v(-103.62, -30.84) * mm, v(-103.72, -31.05) * mm, v(-103.68, -31.25) * mm]});
            skFitSpline(sketch, "E2083", {"points": [v(-103.68, -31.25) * mm, v(-103.64, -31.46) * mm, v(-103.48, -31.62) * mm, v(-103.27, -31.66) * mm]});
            skFitSpline(sketch, "E2084", {"points": [v(-103.27, -31.66) * mm, v(-103.07, -31.7) * mm, v(-102.86, -31.6) * mm, v(-102.75, -31.42) * mm]});
            skFitSpline(sketch, "E2085", {"points": [v(-103.44, -30.73) * mm, v(-103.28, -30.64) * mm, v(-103.19, -30.48) * mm, v(-103.19, -30.3) * mm]});
            skLineSegment(sketch, "E2086", {"start": v(-91.54, -53.05) * mm, "end": v(-91.54, -18.67) * mm});
            skFitSpline(sketch, "E2087", {"points": [v(-103.19, -25.83) * mm, v(-103.19, -25.65) * mm, v(-103.28, -25.49) * mm, v(-103.44, -25.4) * mm]});
            skFitSpline(sketch, "E2088", {"points": [v(-102.75, -24.72) * mm, v(-102.86, -24.53) * mm, v(-103.07, -24.44) * mm, v(-103.27, -24.47) * mm]});
            skFitSpline(sketch, "E2089", {"points": [v(-103.27, -24.47) * mm, v(-103.48, -24.51) * mm, v(-103.64, -24.67) * mm, v(-103.68, -24.88) * mm]});
            skFitSpline(sketch, "E2090", {"points": [v(-103.68, -24.88) * mm, v(-103.72, -25.09) * mm, v(-103.62, -25.3) * mm, v(-103.44, -25.4) * mm]});
            skFitSpline(sketch, "E2091", {"points": [v(-102.75, -24.72) * mm, v(-102.67, -24.87) * mm, v(-102.5, -24.97) * mm, v(-102.32, -24.97) * mm]});
            skLineSegment(sketch, "E2092", {"start": v(-96.54, -13.67) * mm, "end": v(-115.8, -13.67) * mm});
            skFitSpline(sketch, "E2093", {"points": [v(-100.75, -24.97) * mm, v(-100.57, -24.97) * mm, v(-100.4, -24.87) * mm, v(-100.32, -24.72) * mm]});
            skFitSpline(sketch, "E2094", {"points": [v(-99.64, -25.4) * mm, v(-99.46, -25.3) * mm, v(-99.36, -25.09) * mm, v(-99.4, -24.88) * mm]});
            skFitSpline(sketch, "E2095", {"points": [v(-99.4, -24.88) * mm, v(-99.43, -24.67) * mm, v(-99.6, -24.51) * mm, v(-99.8, -24.47) * mm]});
            skFitSpline(sketch, "E2096", {"points": [v(-99.8, -24.47) * mm, v(-100, -24.44) * mm, v(-100.22, -24.53) * mm, v(-100.32, -24.72) * mm]});
            skFitSpline(sketch, "E2097", {"points": [v(-99.64, -25.4) * mm, v(-99.8, -25.49) * mm, v(-99.89, -25.65) * mm, v(-99.89, -25.83) * mm]});
            skLineSegment(sketch, "E2098", {"start": v(-116.76, -14.37) * mm, "end": v(-118.32, -19.35) * mm});
            skFitSpline(sketch, "E2099", {"points": [v(-99.89, -30.3) * mm, v(-99.89, -30.48) * mm, v(-99.8, -30.64) * mm, v(-99.64, -30.73) * mm]});
            skFitSpline(sketch, "E2100", {"points": [v(-100.32, -31.42) * mm, v(-100.22, -31.6) * mm, v(-100, -31.7) * mm, v(-99.8, -31.66) * mm]});
            skFitSpline(sketch, "E2101", {"points": [v(-99.8, -31.66) * mm, v(-99.6, -31.62) * mm, v(-99.43, -31.46) * mm, v(-99.4, -31.25) * mm]});
            skFitSpline(sketch, "E2102", {"points": [v(-99.4, -31.25) * mm, v(-99.36, -31.05) * mm, v(-99.46, -30.84) * mm, v(-99.64, -30.73) * mm]});
            skFitSpline(sketch, "E2103", {"points": [v(-100.32, -31.42) * mm, v(-100.4, -31.26) * mm, v(-100.57, -31.17) * mm, v(-100.75, -31.17) * mm]});
            skLineSegment(sketch, "E2104", {"start": v(-103.19, -30.3) * mm, "end": v(-103.19, -25.83) * mm});
            skFitSpline(sketch, "E2105", {"points": [v(-102.32, -52.37) * mm, v(-102.5, -52.37) * mm, v(-102.66, -52.46) * mm, v(-102.75, -52.62) * mm]});
            skFitSpline(sketch, "E2106", {"points": [v(-103.44, -51.93) * mm, v(-103.62, -52.04) * mm, v(-103.72, -52.25) * mm, v(-103.68, -52.45) * mm]});
            skFitSpline(sketch, "E2107", {"points": [v(-103.68, -52.45) * mm, v(-103.64, -52.66) * mm, v(-103.48, -52.82) * mm, v(-103.27, -52.86) * mm]});
            skFitSpline(sketch, "E2108", {"points": [v(-103.27, -52.86) * mm, v(-103.07, -52.9) * mm, v(-102.86, -52.8) * mm, v(-102.75, -52.62) * mm]});
            skFitSpline(sketch, "E2109", {"points": [v(-103.44, -51.93) * mm, v(-103.28, -51.84) * mm, v(-103.19, -51.68) * mm, v(-103.19, -51.5) * mm]});
            skLineSegment(sketch, "E2110", {"start": v(-102.32, -24.97) * mm, "end": v(-100.75, -24.97) * mm});
            skFitSpline(sketch, "E2111", {"points": [v(-103.19, -47.03) * mm, v(-103.19, -46.85) * mm, v(-103.28, -46.69) * mm, v(-103.44, -46.6) * mm]});
            skFitSpline(sketch, "E2112", {"points": [v(-102.75, -45.92) * mm, v(-102.86, -45.73) * mm, v(-103.07, -45.64) * mm, v(-103.27, -45.67) * mm]});
            skFitSpline(sketch, "E2113", {"points": [v(-103.27, -45.67) * mm, v(-103.48, -45.71) * mm, v(-103.64, -45.87) * mm, v(-103.68, -46.08) * mm]});
            skFitSpline(sketch, "E2114", {"points": [v(-103.68, -46.08) * mm, v(-103.72, -46.29) * mm, v(-103.62, -46.5) * mm, v(-103.44, -46.6) * mm]});
            skFitSpline(sketch, "E2115", {"points": [v(-102.75, -45.92) * mm, v(-102.67, -46.07) * mm, v(-102.5, -46.17) * mm, v(-102.32, -46.17) * mm]});
            skLineSegment(sketch, "E2116", {"start": v(-99.89, -25.83) * mm, "end": v(-99.89, -30.3) * mm});
            skFitSpline(sketch, "E2117", {"points": [v(-100.75, -46.17) * mm, v(-100.57, -46.17) * mm, v(-100.4, -46.07) * mm, v(-100.32, -45.92) * mm]});
            skFitSpline(sketch, "E2118", {"points": [v(-99.64, -46.6) * mm, v(-99.46, -46.5) * mm, v(-99.36, -46.29) * mm, v(-99.4, -46.08) * mm]});
            skFitSpline(sketch, "E2119", {"points": [v(-99.4, -46.08) * mm, v(-99.43, -45.87) * mm, v(-99.6, -45.71) * mm, v(-99.8, -45.67) * mm]});
            skFitSpline(sketch, "E2120", {"points": [v(-99.8, -45.67) * mm, v(-100, -45.64) * mm, v(-100.22, -45.73) * mm, v(-100.32, -45.92) * mm]});
            skFitSpline(sketch, "E2121", {"points": [v(-99.64, -46.6) * mm, v(-99.8, -46.69) * mm, v(-99.89, -46.85) * mm, v(-99.89, -47.03) * mm]});
            skLineSegment(sketch, "E2122", {"start": v(-100.75, -31.17) * mm, "end": v(-102.32, -31.17) * mm});
            skFitSpline(sketch, "E2123", {"points": [v(-99.89, -51.5) * mm, v(-99.89, -51.68) * mm, v(-99.8, -51.84) * mm, v(-99.64, -51.93) * mm]});
            skFitSpline(sketch, "E2124", {"points": [v(-100.32, -52.62) * mm, v(-100.22, -52.8) * mm, v(-100, -52.9) * mm, v(-99.8, -52.86) * mm]});
            skFitSpline(sketch, "E2125", {"points": [v(-99.8, -52.86) * mm, v(-99.6, -52.82) * mm, v(-99.43, -52.66) * mm, v(-99.4, -52.45) * mm]});
            skFitSpline(sketch, "E2126", {"points": [v(-99.4, -52.45) * mm, v(-99.36, -52.25) * mm, v(-99.46, -52.04) * mm, v(-99.64, -51.93) * mm]});
            skFitSpline(sketch, "E2127", {"points": [v(-100.32, -52.62) * mm, v(-100.4, -52.46) * mm, v(-100.57, -52.37) * mm, v(-100.75, -52.37) * mm]});
            skLineSegment(sketch, "E2128", {"start": v(-103.19, -51.5) * mm, "end": v(-103.19, -47.03) * mm});
            skFitSpline(sketch, "E2129", {"points": [v(-216.2, -31.55) * mm, v(-216.37, -31.55) * mm, v(-216.54, -31.65) * mm, v(-216.63, -31.8) * mm]});
            skFitSpline(sketch, "E2130", {"points": [v(-217.31, -31.12) * mm, v(-217.5, -31.23) * mm, v(-217.6, -31.43) * mm, v(-217.55, -31.64) * mm]});
            skFitSpline(sketch, "E2131", {"points": [v(-217.55, -31.64) * mm, v(-217.52, -31.85) * mm, v(-217.36, -32.01) * mm, v(-217.15, -32.05) * mm]});
            skFitSpline(sketch, "E2132", {"points": [v(-217.15, -32.05) * mm, v(-216.94, -32.08) * mm, v(-216.73, -31.99) * mm, v(-216.63, -31.8) * mm]});
            skFitSpline(sketch, "E2133", {"points": [v(-217.31, -31.12) * mm, v(-217.16, -31.03) * mm, v(-217.06, -30.87) * mm, v(-217.06, -30.69) * mm]});
            skLineSegment(sketch, "E2134", {"start": v(-102.32, -46.17) * mm, "end": v(-100.75, -46.17) * mm});
            skFitSpline(sketch, "E2135", {"points": [v(-217.06, -26.22) * mm, v(-217.06, -26.04) * mm, v(-217.16, -25.88) * mm, v(-217.31, -25.79) * mm]});
            skFitSpline(sketch, "E2136", {"points": [v(-216.63, -25.1) * mm, v(-216.73, -24.92) * mm, v(-216.94, -24.83) * mm, v(-217.15, -24.86) * mm]});
            skFitSpline(sketch, "E2137", {"points": [v(-217.15, -24.86) * mm, v(-217.36, -24.9) * mm, v(-217.52, -25.06) * mm, v(-217.55, -25.27) * mm]});
            skFitSpline(sketch, "E2138", {"points": [v(-217.55, -25.27) * mm, v(-217.6, -25.47) * mm, v(-217.5, -25.68) * mm, v(-217.31, -25.79) * mm]});
            skFitSpline(sketch, "E2139", {"points": [v(-216.63, -25.1) * mm, v(-216.54, -25.26) * mm, v(-216.37, -25.35) * mm, v(-216.2, -25.35) * mm]});
            skLineSegment(sketch, "E2140", {"start": v(-99.89, -47.03) * mm, "end": v(-99.89, -51.5) * mm});
            skFitSpline(sketch, "E2141", {"points": [v(-214.63, -25.35) * mm, v(-214.45, -25.35) * mm, v(-214.28, -25.26) * mm, v(-214.2, -25.1) * mm]});
            skFitSpline(sketch, "E2142", {"points": [v(-213.51, -25.79) * mm, v(-213.33, -25.68) * mm, v(-213.23, -25.47) * mm, v(-213.27, -25.27) * mm]});
            skFitSpline(sketch, "E2143", {"points": [v(-213.27, -25.27) * mm, v(-213.3, -25.06) * mm, v(-213.47, -24.9) * mm, v(-213.68, -24.86) * mm]});
            skFitSpline(sketch, "E2144", {"points": [v(-213.68, -24.86) * mm, v(-213.88, -24.83) * mm, v(-214.1, -24.92) * mm, v(-214.2, -25.1) * mm]});
            skFitSpline(sketch, "E2145", {"points": [v(-213.51, -25.79) * mm, v(-213.67, -25.88) * mm, v(-213.76, -26.04) * mm, v(-213.76, -26.22) * mm]});
            skLineSegment(sketch, "E2146", {"start": v(-100.75, -52.37) * mm, "end": v(-102.32, -52.37) * mm});
            skFitSpline(sketch, "E2147", {"points": [v(-213.76, -30.69) * mm, v(-213.76, -30.87) * mm, v(-213.67, -31.03) * mm, v(-213.51, -31.12) * mm]});
            skFitSpline(sketch, "E2148", {"points": [v(-214.2, -31.8) * mm, v(-214.1, -31.99) * mm, v(-213.88, -32.08) * mm, v(-213.68, -32.05) * mm]});
            skFitSpline(sketch, "E2149", {"points": [v(-213.68, -32.05) * mm, v(-213.47, -32.01) * mm, v(-213.3, -31.85) * mm, v(-213.27, -31.64) * mm]});
            skFitSpline(sketch, "E2150", {"points": [v(-213.27, -31.64) * mm, v(-213.23, -31.43) * mm, v(-213.33, -31.23) * mm, v(-213.51, -31.12) * mm]});
            skFitSpline(sketch, "E2151", {"points": [v(-214.2, -31.8) * mm, v(-214.28, -31.65) * mm, v(-214.45, -31.55) * mm, v(-214.63, -31.55) * mm]});
            skLineSegment(sketch, "E2152", {"start": v(-217.06, -30.69) * mm, "end": v(-217.06, -26.22) * mm});
            skFitSpline(sketch, "E2153", {"points": [v(-216.2, -52.75) * mm, v(-216.37, -52.75) * mm, v(-216.54, -52.85) * mm, v(-216.63, -53) * mm]});
            skFitSpline(sketch, "E2154", {"points": [v(-217.31, -52.32) * mm, v(-217.5, -52.43) * mm, v(-217.6, -52.63) * mm, v(-217.55, -52.84) * mm]});
            skFitSpline(sketch, "E2155", {"points": [v(-217.55, -52.84) * mm, v(-217.52, -53.05) * mm, v(-217.36, -53.21) * mm, v(-217.15, -53.25) * mm]});
            skFitSpline(sketch, "E2156", {"points": [v(-217.15, -53.25) * mm, v(-216.94, -53.28) * mm, v(-216.73, -53.19) * mm, v(-216.63, -53) * mm]});
            skFitSpline(sketch, "E2157", {"points": [v(-217.31, -52.32) * mm, v(-217.16, -52.23) * mm, v(-217.06, -52.07) * mm, v(-217.06, -51.89) * mm]});
            skLineSegment(sketch, "E2158", {"start": v(-216.2, -25.35) * mm, "end": v(-214.63, -25.35) * mm});
            skFitSpline(sketch, "E2159", {"points": [v(-217.06, -47.42) * mm, v(-217.06, -47.24) * mm, v(-217.16, -47.08) * mm, v(-217.31, -46.99) * mm]});
            skFitSpline(sketch, "E2160", {"points": [v(-216.63, -46.3) * mm, v(-216.73, -46.12) * mm, v(-216.94, -46.03) * mm, v(-217.15, -46.06) * mm]});
            skFitSpline(sketch, "E2161", {"points": [v(-217.15, -46.06) * mm, v(-217.36, -46.1) * mm, v(-217.52, -46.26) * mm, v(-217.55, -46.47) * mm]});
            skFitSpline(sketch, "E2162", {"points": [v(-217.55, -46.47) * mm, v(-217.6, -46.67) * mm, v(-217.5, -46.88) * mm, v(-217.31, -46.99) * mm]});
            skFitSpline(sketch, "E2163", {"points": [v(-216.63, -46.3) * mm, v(-216.54, -46.46) * mm, v(-216.37, -46.55) * mm, v(-216.2, -46.55) * mm]});
            skLineSegment(sketch, "E2164", {"start": v(-213.76, -26.22) * mm, "end": v(-213.76, -30.69) * mm});
            skFitSpline(sketch, "E2165", {"points": [v(-214.63, -46.55) * mm, v(-214.45, -46.55) * mm, v(-214.28, -46.46) * mm, v(-214.2, -46.3) * mm]});
            skFitSpline(sketch, "E2166", {"points": [v(-213.51, -46.99) * mm, v(-213.33, -46.88) * mm, v(-213.23, -46.67) * mm, v(-213.27, -46.47) * mm]});
            skFitSpline(sketch, "E2167", {"points": [v(-213.27, -46.47) * mm, v(-213.3, -46.26) * mm, v(-213.47, -46.1) * mm, v(-213.68, -46.06) * mm]});
            skFitSpline(sketch, "E2168", {"points": [v(-213.68, -46.06) * mm, v(-213.88, -46.03) * mm, v(-214.1, -46.12) * mm, v(-214.2, -46.3) * mm]});
            skFitSpline(sketch, "E2169", {"points": [v(-213.51, -46.99) * mm, v(-213.67, -47.08) * mm, v(-213.76, -47.24) * mm, v(-213.76, -47.42) * mm]});
            skLineSegment(sketch, "E2170", {"start": v(-214.63, -31.55) * mm, "end": v(-216.2, -31.55) * mm});
            skFitSpline(sketch, "E2171", {"points": [v(-213.76, -51.89) * mm, v(-213.76, -52.07) * mm, v(-213.67, -52.23) * mm, v(-213.51, -52.32) * mm]});
            skFitSpline(sketch, "E2172", {"points": [v(-214.2, -53) * mm, v(-214.1, -53.19) * mm, v(-213.88, -53.28) * mm, v(-213.68, -53.25) * mm]});
            skFitSpline(sketch, "E2173", {"points": [v(-213.68, -53.25) * mm, v(-213.47, -53.21) * mm, v(-213.3, -53.05) * mm, v(-213.27, -52.84) * mm]});
            skFitSpline(sketch, "E2174", {"points": [v(-213.27, -52.84) * mm, v(-213.23, -52.63) * mm, v(-213.33, -52.43) * mm, v(-213.51, -52.32) * mm]});
            skFitSpline(sketch, "E2175", {"points": [v(-214.2, -53) * mm, v(-214.28, -52.85) * mm, v(-214.45, -52.75) * mm, v(-214.63, -52.75) * mm]});
            skLineSegment(sketch, "E2176", {"start": v(-217.06, -51.89) * mm, "end": v(-217.06, -47.42) * mm});
            skFitSpline(sketch, "E2177", {"points": [v(-228.8, -31.55) * mm, v(-228.97, -31.55) * mm, v(-229.14, -31.65) * mm, v(-229.23, -31.8) * mm]});
            skFitSpline(sketch, "E2178", {"points": [v(-229.91, -31.12) * mm, v(-230.1, -31.23) * mm, v(-230.2, -31.43) * mm, v(-230.15, -31.64) * mm]});
            skFitSpline(sketch, "E2179", {"points": [v(-230.15, -31.64) * mm, v(-230.12, -31.85) * mm, v(-229.96, -32.01) * mm, v(-229.75, -32.05) * mm]});
            skFitSpline(sketch, "E2180", {"points": [v(-229.75, -32.05) * mm, v(-229.54, -32.08) * mm, v(-229.33, -31.99) * mm, v(-229.23, -31.8) * mm]});
            skFitSpline(sketch, "E2181", {"points": [v(-229.91, -31.12) * mm, v(-229.76, -31.03) * mm, v(-229.66, -30.87) * mm, v(-229.66, -30.69) * mm]});
            skLineSegment(sketch, "E2182", {"start": v(-216.2, -46.55) * mm, "end": v(-214.63, -46.55) * mm});
            skFitSpline(sketch, "E2183", {"points": [v(-229.66, -26.22) * mm, v(-229.66, -26.04) * mm, v(-229.76, -25.88) * mm, v(-229.91, -25.79) * mm]});
            skFitSpline(sketch, "E2184", {"points": [v(-229.23, -25.1) * mm, v(-229.33, -24.92) * mm, v(-229.54, -24.83) * mm, v(-229.75, -24.86) * mm]});
            skFitSpline(sketch, "E2185", {"points": [v(-229.75, -24.86) * mm, v(-229.96, -24.9) * mm, v(-230.12, -25.06) * mm, v(-230.15, -25.27) * mm]});
            skFitSpline(sketch, "E2186", {"points": [v(-230.15, -25.27) * mm, v(-230.2, -25.47) * mm, v(-230.1, -25.68) * mm, v(-229.91, -25.79) * mm]});
            skFitSpline(sketch, "E2187", {"points": [v(-229.23, -25.1) * mm, v(-229.14, -25.26) * mm, v(-228.97, -25.35) * mm, v(-228.8, -25.35) * mm]});
            skLineSegment(sketch, "E2188", {"start": v(-213.76, -47.42) * mm, "end": v(-213.76, -51.89) * mm});
            skFitSpline(sketch, "E2189", {"points": [v(-227.23, -25.35) * mm, v(-227.05, -25.35) * mm, v(-226.88, -25.26) * mm, v(-226.8, -25.1) * mm]});
            skFitSpline(sketch, "E2190", {"points": [v(-226.11, -25.79) * mm, v(-225.93, -25.68) * mm, v(-225.83, -25.47) * mm, v(-225.87, -25.27) * mm]});
            skFitSpline(sketch, "E2191", {"points": [v(-225.87, -25.27) * mm, v(-225.9, -25.06) * mm, v(-226.07, -24.9) * mm, v(-226.28, -24.86) * mm]});
            skFitSpline(sketch, "E2192", {"points": [v(-226.28, -24.86) * mm, v(-226.48, -24.83) * mm, v(-226.7, -24.92) * mm, v(-226.8, -25.1) * mm]});
            skFitSpline(sketch, "E2193", {"points": [v(-226.11, -25.79) * mm, v(-226.27, -25.88) * mm, v(-226.36, -26.04) * mm, v(-226.36, -26.22) * mm]});
            skLineSegment(sketch, "E2194", {"start": v(-214.63, -52.75) * mm, "end": v(-216.2, -52.75) * mm});
            skFitSpline(sketch, "E2195", {"points": [v(-226.36, -30.69) * mm, v(-226.36, -30.87) * mm, v(-226.27, -31.03) * mm, v(-226.11, -31.12) * mm]});
            skFitSpline(sketch, "E2196", {"points": [v(-226.8, -31.8) * mm, v(-226.7, -31.99) * mm, v(-226.48, -32.08) * mm, v(-226.28, -32.05) * mm]});
            skFitSpline(sketch, "E2197", {"points": [v(-226.28, -32.05) * mm, v(-226.07, -32.01) * mm, v(-225.9, -31.85) * mm, v(-225.87, -31.64) * mm]});
            skFitSpline(sketch, "E2198", {"points": [v(-225.87, -31.64) * mm, v(-225.83, -31.43) * mm, v(-225.93, -31.23) * mm, v(-226.11, -31.12) * mm]});
            skFitSpline(sketch, "E2199", {"points": [v(-226.8, -31.8) * mm, v(-226.88, -31.65) * mm, v(-227.05, -31.55) * mm, v(-227.23, -31.55) * mm]});
            skLineSegment(sketch, "E2200", {"start": v(-229.66, -30.69) * mm, "end": v(-229.66, -26.22) * mm});
            skFitSpline(sketch, "E2201", {"points": [v(-228.8, -52.75) * mm, v(-228.97, -52.75) * mm, v(-229.14, -52.85) * mm, v(-229.23, -53) * mm]});
            skFitSpline(sketch, "E2202", {"points": [v(-229.91, -52.32) * mm, v(-230.1, -52.43) * mm, v(-230.2, -52.63) * mm, v(-230.15, -52.84) * mm]});
            skFitSpline(sketch, "E2203", {"points": [v(-230.15, -52.84) * mm, v(-230.12, -53.05) * mm, v(-229.96, -53.21) * mm, v(-229.75, -53.25) * mm]});
            skFitSpline(sketch, "E2204", {"points": [v(-229.75, -53.25) * mm, v(-229.54, -53.28) * mm, v(-229.33, -53.19) * mm, v(-229.23, -53) * mm]});
            skFitSpline(sketch, "E2205", {"points": [v(-229.91, -52.32) * mm, v(-229.76, -52.23) * mm, v(-229.66, -52.07) * mm, v(-229.66, -51.89) * mm]});
            skLineSegment(sketch, "E2206", {"start": v(-228.8, -25.35) * mm, "end": v(-227.23, -25.35) * mm});
            skFitSpline(sketch, "E2207", {"points": [v(-229.66, -47.42) * mm, v(-229.66, -47.24) * mm, v(-229.76, -47.08) * mm, v(-229.91, -46.99) * mm]});
            skFitSpline(sketch, "E2208", {"points": [v(-229.23, -46.3) * mm, v(-229.33, -46.12) * mm, v(-229.54, -46.03) * mm, v(-229.75, -46.06) * mm]});
            skFitSpline(sketch, "E2209", {"points": [v(-229.75, -46.06) * mm, v(-229.96, -46.1) * mm, v(-230.12, -46.26) * mm, v(-230.15, -46.47) * mm]});
            skFitSpline(sketch, "E2210", {"points": [v(-230.15, -46.47) * mm, v(-230.2, -46.67) * mm, v(-230.1, -46.88) * mm, v(-229.91, -46.99) * mm]});
            skFitSpline(sketch, "E2211", {"points": [v(-229.23, -46.3) * mm, v(-229.14, -46.46) * mm, v(-228.97, -46.55) * mm, v(-228.8, -46.55) * mm]});
            skLineSegment(sketch, "E2212", {"start": v(-226.36, -26.22) * mm, "end": v(-226.36, -30.69) * mm});
            skFitSpline(sketch, "E2213", {"points": [v(-227.23, -46.55) * mm, v(-227.05, -46.55) * mm, v(-226.88, -46.46) * mm, v(-226.8, -46.3) * mm]});
            skFitSpline(sketch, "E2214", {"points": [v(-226.11, -46.99) * mm, v(-225.93, -46.88) * mm, v(-225.83, -46.67) * mm, v(-225.87, -46.47) * mm]});
            skFitSpline(sketch, "E2215", {"points": [v(-225.87, -46.47) * mm, v(-225.9, -46.26) * mm, v(-226.07, -46.1) * mm, v(-226.28, -46.06) * mm]});
            skFitSpline(sketch, "E2216", {"points": [v(-226.28, -46.06) * mm, v(-226.48, -46.03) * mm, v(-226.7, -46.12) * mm, v(-226.8, -46.3) * mm]});
            skFitSpline(sketch, "E2217", {"points": [v(-226.11, -46.99) * mm, v(-226.27, -47.08) * mm, v(-226.36, -47.24) * mm, v(-226.36, -47.42) * mm]});
            skLineSegment(sketch, "E2218", {"start": v(-227.23, -31.55) * mm, "end": v(-228.8, -31.55) * mm});
            skFitSpline(sketch, "E2219", {"points": [v(-226.36, -51.89) * mm, v(-226.36, -52.07) * mm, v(-226.27, -52.23) * mm, v(-226.11, -52.32) * mm]});
            skFitSpline(sketch, "E2220", {"points": [v(-226.8, -53) * mm, v(-226.7, -53.19) * mm, v(-226.48, -53.28) * mm, v(-226.28, -53.25) * mm]});
            skFitSpline(sketch, "E2221", {"points": [v(-226.28, -53.25) * mm, v(-226.07, -53.21) * mm, v(-225.9, -53.05) * mm, v(-225.87, -52.84) * mm]});
            skFitSpline(sketch, "E2222", {"points": [v(-225.87, -52.84) * mm, v(-225.83, -52.63) * mm, v(-225.93, -52.43) * mm, v(-226.11, -52.32) * mm]});
            skFitSpline(sketch, "E2223", {"points": [v(-226.8, -53) * mm, v(-226.88, -52.85) * mm, v(-227.05, -52.75) * mm, v(-227.23, -52.75) * mm]});
            skLineSegment(sketch, "E2224", {"start": v(-229.66, -51.89) * mm, "end": v(-229.66, -47.42) * mm});
            skFitSpline(sketch, "E2225", {"points": [v(-340.67, -31.42) * mm, v(-340.76, -31.26) * mm, v(-340.92, -31.17) * mm, v(-341.1, -31.17) * mm]});
            skFitSpline(sketch, "E2226", {"points": [v(-340.67, -31.42) * mm, v(-340.57, -31.6) * mm, v(-340.36, -31.7) * mm, v(-340.15, -31.66) * mm]});
            skFitSpline(sketch, "E2227", {"points": [v(-340.15, -31.66) * mm, v(-339.94, -31.62) * mm, v(-339.78, -31.46) * mm, v(-339.75, -31.25) * mm]});
            skFitSpline(sketch, "E2228", {"points": [v(-339.75, -31.25) * mm, v(-339.7, -31.05) * mm, v(-339.8, -30.84) * mm, v(-339.99, -30.73) * mm]});
            skFitSpline(sketch, "E2229", {"points": [v(-340.24, -30.3) * mm, v(-340.24, -30.48) * mm, v(-340.14, -30.64) * mm, v(-339.99, -30.73) * mm]});
            skLineSegment(sketch, "E2230", {"start": v(-228.8, -46.55) * mm, "end": v(-227.23, -46.55) * mm});
            skFitSpline(sketch, "E2231", {"points": [v(-339.99, -25.4) * mm, v(-340.14, -25.49) * mm, v(-340.24, -25.65) * mm, v(-340.24, -25.83) * mm]});
            skFitSpline(sketch, "E2232", {"points": [v(-339.99, -25.4) * mm, v(-339.8, -25.3) * mm, v(-339.7, -25.09) * mm, v(-339.75, -24.88) * mm]});
            skFitSpline(sketch, "E2233", {"points": [v(-339.75, -24.88) * mm, v(-339.78, -24.67) * mm, v(-339.94, -24.51) * mm, v(-340.15, -24.47) * mm]});
            skFitSpline(sketch, "E2234", {"points": [v(-340.15, -24.47) * mm, v(-340.36, -24.44) * mm, v(-340.57, -24.53) * mm, v(-340.67, -24.72) * mm]});
            skFitSpline(sketch, "E2235", {"points": [v(-341.1, -24.97) * mm, v(-340.92, -24.97) * mm, v(-340.76, -24.87) * mm, v(-340.67, -24.72) * mm]});
            skLineSegment(sketch, "E2236", {"start": v(-226.36, -47.42) * mm, "end": v(-226.36, -51.89) * mm});
            skFitSpline(sketch, "E2237", {"points": [v(-343.1, -24.72) * mm, v(-343.02, -24.87) * mm, v(-342.85, -24.97) * mm, v(-342.67, -24.97) * mm]});
            skFitSpline(sketch, "E2238", {"points": [v(-343.1, -24.72) * mm, v(-343.2, -24.53) * mm, v(-343.42, -24.44) * mm, v(-343.62, -24.47) * mm]});
            skFitSpline(sketch, "E2239", {"points": [v(-343.62, -24.47) * mm, v(-343.83, -24.51) * mm, v(-344, -24.67) * mm, v(-344.03, -24.88) * mm]});
            skFitSpline(sketch, "E2240", {"points": [v(-344.03, -24.88) * mm, v(-344.07, -25.09) * mm, v(-343.97, -25.3) * mm, v(-343.79, -25.4) * mm]});
            skFitSpline(sketch, "E2241", {"points": [v(-343.54, -25.83) * mm, v(-343.54, -25.65) * mm, v(-343.63, -25.49) * mm, v(-343.79, -25.4) * mm]});
            skLineSegment(sketch, "E2242", {"start": v(-227.23, -52.75) * mm, "end": v(-228.8, -52.75) * mm});
            skFitSpline(sketch, "E2243", {"points": [v(-343.79, -30.73) * mm, v(-343.63, -30.64) * mm, v(-343.54, -30.48) * mm, v(-343.54, -30.3) * mm]});
            skFitSpline(sketch, "E2244", {"points": [v(-343.79, -30.73) * mm, v(-343.97, -30.84) * mm, v(-344.07, -31.05) * mm, v(-344.03, -31.25) * mm]});
            skFitSpline(sketch, "E2245", {"points": [v(-344.03, -31.25) * mm, v(-344, -31.46) * mm, v(-343.83, -31.62) * mm, v(-343.62, -31.66) * mm]});
            skFitSpline(sketch, "E2246", {"points": [v(-343.62, -31.66) * mm, v(-343.42, -31.7) * mm, v(-343.2, -31.6) * mm, v(-343.1, -31.42) * mm]});
            skFitSpline(sketch, "E2247", {"points": [v(-342.67, -31.17) * mm, v(-342.85, -31.17) * mm, v(-343.02, -31.26) * mm, v(-343.1, -31.42) * mm]});
            skLineSegment(sketch, "E2248", {"start": v(-340.24, -30.3) * mm, "end": v(-340.24, -25.83) * mm});
            skFitSpline(sketch, "E2249", {"points": [v(-340.67, -52.62) * mm, v(-340.76, -52.46) * mm, v(-340.92, -52.37) * mm, v(-341.1, -52.37) * mm]});
            skFitSpline(sketch, "E2250", {"points": [v(-340.67, -52.62) * mm, v(-340.57, -52.8) * mm, v(-340.36, -52.9) * mm, v(-340.15, -52.86) * mm]});
            skFitSpline(sketch, "E2251", {"points": [v(-340.15, -52.86) * mm, v(-339.94, -52.82) * mm, v(-339.78, -52.66) * mm, v(-339.75, -52.45) * mm]});
            skFitSpline(sketch, "E2252", {"points": [v(-339.75, -52.45) * mm, v(-339.7, -52.25) * mm, v(-339.8, -52.04) * mm, v(-339.99, -51.93) * mm]});
            skFitSpline(sketch, "E2253", {"points": [v(-340.24, -51.5) * mm, v(-340.24, -51.68) * mm, v(-340.14, -51.84) * mm, v(-339.99, -51.93) * mm]});
            skLineSegment(sketch, "E2254", {"start": v(-341.1, -24.97) * mm, "end": v(-342.67, -24.97) * mm});
            skFitSpline(sketch, "E2255", {"points": [v(-339.99, -46.6) * mm, v(-340.14, -46.69) * mm, v(-340.24, -46.85) * mm, v(-340.24, -47.03) * mm]});
            skFitSpline(sketch, "E2256", {"points": [v(-339.99, -46.6) * mm, v(-339.8, -46.5) * mm, v(-339.7, -46.29) * mm, v(-339.75, -46.08) * mm]});
            skFitSpline(sketch, "E2257", {"points": [v(-339.75, -46.08) * mm, v(-339.78, -45.87) * mm, v(-339.94, -45.71) * mm, v(-340.15, -45.67) * mm]});
            skFitSpline(sketch, "E2258", {"points": [v(-340.15, -45.67) * mm, v(-340.36, -45.64) * mm, v(-340.57, -45.73) * mm, v(-340.67, -45.92) * mm]});
            skFitSpline(sketch, "E2259", {"points": [v(-341.1, -46.17) * mm, v(-340.92, -46.17) * mm, v(-340.76, -46.07) * mm, v(-340.67, -45.92) * mm]});
            skLineSegment(sketch, "E2260", {"start": v(-343.54, -25.83) * mm, "end": v(-343.54, -30.3) * mm});
            skFitSpline(sketch, "E2261", {"points": [v(-343.1, -45.92) * mm, v(-343.02, -46.07) * mm, v(-342.85, -46.17) * mm, v(-342.67, -46.17) * mm]});
            skFitSpline(sketch, "E2262", {"points": [v(-343.1, -45.92) * mm, v(-343.2, -45.73) * mm, v(-343.42, -45.64) * mm, v(-343.62, -45.67) * mm]});
            skFitSpline(sketch, "E2263", {"points": [v(-343.62, -45.67) * mm, v(-343.83, -45.71) * mm, v(-344, -45.87) * mm, v(-344.03, -46.08) * mm]});
            skFitSpline(sketch, "E2264", {"points": [v(-344.03, -46.08) * mm, v(-344.07, -46.29) * mm, v(-343.97, -46.5) * mm, v(-343.79, -46.6) * mm]});
            skFitSpline(sketch, "E2265", {"points": [v(-343.54, -47.03) * mm, v(-343.54, -46.85) * mm, v(-343.63, -46.69) * mm, v(-343.79, -46.6) * mm]});
            skLineSegment(sketch, "E2266", {"start": v(-342.67, -31.17) * mm, "end": v(-341.1, -31.17) * mm});
            skFitSpline(sketch, "E2267", {"points": [v(-343.79, -51.93) * mm, v(-343.63, -51.84) * mm, v(-343.54, -51.68) * mm, v(-343.54, -51.5) * mm]});
            skFitSpline(sketch, "E2268", {"points": [v(-343.79, -51.93) * mm, v(-343.97, -52.04) * mm, v(-344.07, -52.25) * mm, v(-344.03, -52.45) * mm]});
            skFitSpline(sketch, "E2269", {"points": [v(-344.03, -52.45) * mm, v(-344, -52.66) * mm, v(-343.83, -52.82) * mm, v(-343.62, -52.86) * mm]});
            skFitSpline(sketch, "E2270", {"points": [v(-343.62, -52.86) * mm, v(-343.42, -52.9) * mm, v(-343.2, -52.8) * mm, v(-343.1, -52.62) * mm]});
            skFitSpline(sketch, "E2271", {"points": [v(-342.67, -52.37) * mm, v(-342.85, -52.37) * mm, v(-343.02, -52.46) * mm, v(-343.1, -52.62) * mm]});
            skLineSegment(sketch, "E2272", {"start": v(-340.24, -51.5) * mm, "end": v(-340.24, -47.03) * mm});
            skFitSpline(sketch, "E2273", {"points": [v(-99.94, -38.67) * mm, v(-99.94, -38.1) * mm, v(-100.24, -37.57) * mm, v(-100.74, -37.28) * mm]});
            skFitSpline(sketch, "E2274", {"points": [v(-100.74, -37.28) * mm, v(-101.23, -37) * mm, v(-101.84, -37) * mm, v(-102.34, -37.28) * mm]});
            skFitSpline(sketch, "E2275", {"points": [v(-102.34, -37.28) * mm, v(-102.83, -37.57) * mm, v(-103.14, -38.1) * mm, v(-103.14, -38.67) * mm]});
            skFitSpline(sketch, "E2276", {"points": [v(-103.14, -38.67) * mm, v(-103.14, -39.24) * mm, v(-102.83, -39.77) * mm, v(-102.34, -40.05) * mm]});
            skFitSpline(sketch, "E2277", {"points": [v(-102.34, -40.05) * mm, v(-101.84, -40.34) * mm, v(-101.23, -40.34) * mm, v(-100.74, -40.05) * mm]});
            skFitSpline(sketch, "E2278", {"points": [v(-100.74, -40.05) * mm, v(-100.24, -39.77) * mm, v(-99.94, -39.24) * mm, v(-99.94, -38.67) * mm]});
            skLineSegment(sketch, "E2279", {"start": v(-341.1, -46.17) * mm, "end": v(-342.67, -46.17) * mm});
            skFitSpline(sketch, "E2280", {"points": [v(-154.11, -28.67) * mm, v(-154.11, -28.1) * mm, v(-154.42, -27.57) * mm, v(-154.91, -27.28) * mm]});
            skFitSpline(sketch, "E2281", {"points": [v(-154.91, -27.28) * mm, v(-155.4, -27) * mm, v(-156.02, -27) * mm, v(-156.51, -27.28) * mm]});
            skFitSpline(sketch, "E2282", {"points": [v(-156.51, -27.28) * mm, v(-157, -27.57) * mm, v(-157.31, -28.1) * mm, v(-157.31, -28.67) * mm]});
            skFitSpline(sketch, "E2283", {"points": [v(-157.31, -28.67) * mm, v(-157.31, -29.24) * mm, v(-157, -29.77) * mm, v(-156.51, -30.05) * mm]});
            skFitSpline(sketch, "E2284", {"points": [v(-156.51, -30.05) * mm, v(-156.02, -30.34) * mm, v(-155.4, -30.34) * mm, v(-154.91, -30.05) * mm]});
            skFitSpline(sketch, "E2285", {"points": [v(-154.91, -30.05) * mm, v(-154.42, -29.77) * mm, v(-154.11, -29.24) * mm, v(-154.11, -28.67) * mm]});
            skLineSegment(sketch, "E2286", {"start": v(-343.54, -47.03) * mm, "end": v(-343.54, -51.5) * mm});
            skFitSpline(sketch, "E2287", {"points": [v(-154.11, -48.67) * mm, v(-154.11, -48.1) * mm, v(-154.42, -47.57) * mm, v(-154.91, -47.28) * mm]});
            skFitSpline(sketch, "E2288", {"points": [v(-154.91, -47.28) * mm, v(-155.4, -47) * mm, v(-156.02, -47) * mm, v(-156.51, -47.28) * mm]});
            skFitSpline(sketch, "E2289", {"points": [v(-156.51, -47.28) * mm, v(-157, -47.57) * mm, v(-157.31, -48.1) * mm, v(-157.31, -48.67) * mm]});
            skFitSpline(sketch, "E2290", {"points": [v(-157.31, -48.67) * mm, v(-157.31, -49.24) * mm, v(-157, -49.77) * mm, v(-156.51, -50.05) * mm]});
            skFitSpline(sketch, "E2291", {"points": [v(-156.51, -50.05) * mm, v(-156.02, -50.34) * mm, v(-155.4, -50.34) * mm, v(-154.91, -50.05) * mm]});
            skFitSpline(sketch, "E2292", {"points": [v(-154.91, -50.05) * mm, v(-154.42, -49.77) * mm, v(-154.11, -49.24) * mm, v(-154.11, -48.67) * mm]});
            skLineSegment(sketch, "E2293", {"start": v(-342.67, -52.37) * mm, "end": v(-341.1, -52.37) * mm});
            skFitSpline(sketch, "E2294", {"points": [v(-185.11, -28.67) * mm, v(-185.11, -28.1) * mm, v(-185.42, -27.57) * mm, v(-185.91, -27.28) * mm]});
            skFitSpline(sketch, "E2295", {"points": [v(-185.91, -27.28) * mm, v(-186.4, -27) * mm, v(-187.02, -27) * mm, v(-187.51, -27.28) * mm]});
            skFitSpline(sketch, "E2296", {"points": [v(-187.51, -27.28) * mm, v(-188, -27.57) * mm, v(-188.31, -28.1) * mm, v(-188.31, -28.67) * mm]});
            skFitSpline(sketch, "E2297", {"points": [v(-188.31, -28.67) * mm, v(-188.31, -29.24) * mm, v(-188, -29.77) * mm, v(-187.51, -30.05) * mm]});
            skFitSpline(sketch, "E2298", {"points": [v(-187.51, -30.05) * mm, v(-187.02, -30.34) * mm, v(-186.4, -30.34) * mm, v(-185.91, -30.05) * mm]});
            skFitSpline(sketch, "E2299", {"points": [v(-185.91, -30.05) * mm, v(-185.42, -29.77) * mm, v(-185.11, -29.24) * mm, v(-185.11, -28.67) * mm]});
            skFitSpline(sketch, "E2300", {"points": [v(-185.11, -48.67) * mm, v(-185.11, -48.1) * mm, v(-185.42, -47.57) * mm, v(-185.91, -47.28) * mm]});
            skFitSpline(sketch, "E2301", {"points": [v(-185.91, -47.28) * mm, v(-186.4, -47) * mm, v(-187.02, -47) * mm, v(-187.51, -47.28) * mm]});
            skFitSpline(sketch, "E2302", {"points": [v(-187.51, -47.28) * mm, v(-188, -47.57) * mm, v(-188.31, -48.1) * mm, v(-188.31, -48.67) * mm]});
            skFitSpline(sketch, "E2303", {"points": [v(-188.31, -48.67) * mm, v(-188.31, -49.24) * mm, v(-188, -49.77) * mm, v(-187.51, -50.05) * mm]});
            skFitSpline(sketch, "E2304", {"points": [v(-187.51, -50.05) * mm, v(-187.02, -50.34) * mm, v(-186.4, -50.34) * mm, v(-185.91, -50.05) * mm]});
            skFitSpline(sketch, "E2305", {"points": [v(-185.91, -50.05) * mm, v(-185.42, -49.77) * mm, v(-185.11, -49.24) * mm, v(-185.11, -48.67) * mm]});
            skFitSpline(sketch, "E2306", {"points": [v(-213.81, -39.05) * mm, v(-213.81, -38.48) * mm, v(-214.12, -37.95) * mm, v(-214.61, -37.67) * mm]});
            skFitSpline(sketch, "E2307", {"points": [v(-214.61, -37.67) * mm, v(-215.1, -37.38) * mm, v(-215.72, -37.38) * mm, v(-216.21, -37.67) * mm]});
            skFitSpline(sketch, "E2308", {"points": [v(-216.21, -37.67) * mm, v(-216.7, -37.95) * mm, v(-217.01, -38.48) * mm, v(-217.01, -39.05) * mm]});
            skFitSpline(sketch, "E2309", {"points": [v(-217.01, -39.05) * mm, v(-217.01, -39.63) * mm, v(-216.7, -40.15) * mm, v(-216.21, -40.44) * mm]});
            skFitSpline(sketch, "E2310", {"points": [v(-216.21, -40.44) * mm, v(-215.72, -40.73) * mm, v(-215.1, -40.73) * mm, v(-214.61, -40.44) * mm]});
            skFitSpline(sketch, "E2311", {"points": [v(-214.61, -40.44) * mm, v(-214.12, -40.15) * mm, v(-213.81, -39.63) * mm, v(-213.81, -39.05) * mm]});
            skFitSpline(sketch, "E2312", {"points": [v(-226.41, -39.05) * mm, v(-226.41, -38.48) * mm, v(-226.72, -37.95) * mm, v(-227.21, -37.67) * mm]});
            skFitSpline(sketch, "E2313", {"points": [v(-227.21, -37.67) * mm, v(-227.7, -37.38) * mm, v(-228.32, -37.38) * mm, v(-228.81, -37.67) * mm]});
            skFitSpline(sketch, "E2314", {"points": [v(-228.81, -37.67) * mm, v(-229.3, -37.95) * mm, v(-229.61, -38.48) * mm, v(-229.61, -39.05) * mm]});
            skFitSpline(sketch, "E2315", {"points": [v(-229.61, -39.05) * mm, v(-229.61, -39.94) * mm, v(-228.9, -40.65) * mm, v(-228.01, -40.65) * mm]});
            skFitSpline(sketch, "E2316", {"points": [v(-228.01, -40.65) * mm, v(-227.13, -40.65) * mm, v(-226.41, -39.94) * mm, v(-226.41, -39.05) * mm]});
            skFitSpline(sketch, "E2317", {"points": [v(-255.11, -28.67) * mm, v(-255.11, -28.1) * mm, v(-255.42, -27.57) * mm, v(-255.91, -27.28) * mm]});
            skFitSpline(sketch, "E2318", {"points": [v(-255.91, -27.28) * mm, v(-256.4, -27) * mm, v(-257.02, -27) * mm, v(-257.51, -27.28) * mm]});
            skFitSpline(sketch, "E2319", {"points": [v(-257.51, -27.28) * mm, v(-258, -27.57) * mm, v(-258.31, -28.1) * mm, v(-258.31, -28.67) * mm]});
            skFitSpline(sketch, "E2320", {"points": [v(-258.31, -28.67) * mm, v(-258.31, -29.24) * mm, v(-258, -29.77) * mm, v(-257.51, -30.05) * mm]});
            skFitSpline(sketch, "E2321", {"points": [v(-257.51, -30.05) * mm, v(-257.02, -30.34) * mm, v(-256.4, -30.34) * mm, v(-255.91, -30.05) * mm]});
            skFitSpline(sketch, "E2322", {"points": [v(-255.91, -30.05) * mm, v(-255.42, -29.77) * mm, v(-255.11, -29.24) * mm, v(-255.11, -28.67) * mm]});
            skFitSpline(sketch, "E2323", {"points": [v(-255.11, -48.67) * mm, v(-255.11, -48.1) * mm, v(-255.42, -47.57) * mm, v(-255.91, -47.28) * mm]});
            skFitSpline(sketch, "E2324", {"points": [v(-255.91, -47.28) * mm, v(-256.4, -47) * mm, v(-257.02, -47) * mm, v(-257.51, -47.28) * mm]});
            skFitSpline(sketch, "E2325", {"points": [v(-257.51, -47.28) * mm, v(-258, -47.57) * mm, v(-258.31, -48.1) * mm, v(-258.31, -48.67) * mm]});
            skFitSpline(sketch, "E2326", {"points": [v(-258.31, -48.67) * mm, v(-258.31, -49.24) * mm, v(-258, -49.77) * mm, v(-257.51, -50.05) * mm]});
            skFitSpline(sketch, "E2327", {"points": [v(-257.51, -50.05) * mm, v(-257.02, -50.34) * mm, v(-256.4, -50.34) * mm, v(-255.91, -50.05) * mm]});
            skFitSpline(sketch, "E2328", {"points": [v(-255.91, -50.05) * mm, v(-255.42, -49.77) * mm, v(-255.11, -49.24) * mm, v(-255.11, -48.67) * mm]});
            skFitSpline(sketch, "E2329", {"points": [v(-286.11, -28.67) * mm, v(-286.11, -28.1) * mm, v(-286.42, -27.57) * mm, v(-286.91, -27.28) * mm]});
            skFitSpline(sketch, "E2330", {"points": [v(-286.91, -27.28) * mm, v(-287.4, -27) * mm, v(-288.02, -27) * mm, v(-288.51, -27.28) * mm]});
            skFitSpline(sketch, "E2331", {"points": [v(-288.51, -27.28) * mm, v(-289, -27.57) * mm, v(-289.31, -28.1) * mm, v(-289.31, -28.67) * mm]});
            skFitSpline(sketch, "E2332", {"points": [v(-289.31, -28.67) * mm, v(-289.31, -29.24) * mm, v(-289, -29.77) * mm, v(-288.51, -30.05) * mm]});
            skFitSpline(sketch, "E2333", {"points": [v(-288.51, -30.05) * mm, v(-288.02, -30.34) * mm, v(-287.4, -30.34) * mm, v(-286.91, -30.05) * mm]});
            skFitSpline(sketch, "E2334", {"points": [v(-286.91, -30.05) * mm, v(-286.42, -29.77) * mm, v(-286.11, -29.24) * mm, v(-286.11, -28.67) * mm]});
            skFitSpline(sketch, "E2335", {"points": [v(-286.11, -48.67) * mm, v(-286.11, -48.1) * mm, v(-286.42, -47.57) * mm, v(-286.91, -47.28) * mm]});
            skFitSpline(sketch, "E2336", {"points": [v(-286.91, -47.28) * mm, v(-287.4, -47) * mm, v(-288.02, -47) * mm, v(-288.51, -47.28) * mm]});
            skFitSpline(sketch, "E2337", {"points": [v(-288.51, -47.28) * mm, v(-289, -47.57) * mm, v(-289.31, -48.1) * mm, v(-289.31, -48.67) * mm]});
            skFitSpline(sketch, "E2338", {"points": [v(-289.31, -48.67) * mm, v(-289.31, -49.24) * mm, v(-289, -49.77) * mm, v(-288.51, -50.05) * mm]});
            skFitSpline(sketch, "E2339", {"points": [v(-288.51, -50.05) * mm, v(-288.02, -50.34) * mm, v(-287.4, -50.34) * mm, v(-286.91, -50.05) * mm]});
            skFitSpline(sketch, "E2340", {"points": [v(-286.91, -50.05) * mm, v(-286.42, -49.77) * mm, v(-286.11, -49.24) * mm, v(-286.11, -48.67) * mm]});
            skFitSpline(sketch, "E2341", {"points": [v(-340.29, -38.67) * mm, v(-340.29, -38.1) * mm, v(-340.6, -37.57) * mm, v(-341.09, -37.28) * mm]});
            skFitSpline(sketch, "E2342", {"points": [v(-341.09, -37.28) * mm, v(-341.58, -37) * mm, v(-342.2, -37) * mm, v(-342.69, -37.28) * mm]});
            skFitSpline(sketch, "E2343", {"points": [v(-342.69, -37.28) * mm, v(-343.18, -37.57) * mm, v(-343.49, -38.1) * mm, v(-343.49, -38.67) * mm]});
            skFitSpline(sketch, "E2344", {"points": [v(-343.49, -38.67) * mm, v(-343.49, -39.24) * mm, v(-343.18, -39.77) * mm, v(-342.69, -40.05) * mm]});
            skFitSpline(sketch, "E2345", {"points": [v(-342.69, -40.05) * mm, v(-342.2, -40.34) * mm, v(-341.58, -40.34) * mm, v(-341.09, -40.05) * mm]});
            skFitSpline(sketch, "E2346", {"points": [v(-341.09, -40.05) * mm, v(-340.6, -39.77) * mm, v(-340.29, -39.24) * mm, v(-340.29, -38.67) * mm]});
            skFitSpline(sketch, "E2347", {"points": [v(-325.1, -19.35) * mm, v(-324.98, -19.77) * mm, v(-324.59, -20.05) * mm, v(-324.15, -20.05) * mm]});
            skFitSpline(sketch, "E2348", {"points": [v(-326.67, -14.37) * mm, v(-326.8, -13.95) * mm, v(-327.18, -13.67) * mm, v(-327.62, -13.67) * mm]});
            skFitSpline(sketch, "E2349", {"points": [v(-119.27, -20.05) * mm, v(-118.83, -20.05) * mm, v(-118.45, -19.77) * mm, v(-118.32, -19.35) * mm]});
            skFitSpline(sketch, "E2350", {"points": [v(-115.8, -13.67) * mm, v(-116.24, -13.67) * mm, v(-116.63, -13.95) * mm, v(-116.76, -14.37) * mm]});
            skFitSpline(sketch, "E2351", {"points": [v(-140.4, -66.05) * mm, v(-140.2, -66.05) * mm, v(-140.04, -65.95) * mm, v(-139.95, -65.79) * mm]});
            skFitSpline(sketch, "E2352", {"points": [v(-139.95, -65.79) * mm, v(-139.87, -65.62) * mm, v(-139.88, -65.43) * mm, v(-139.98, -65.27) * mm]});
            skFitSpline(sketch, "E2353", {"points": [v(-133.44, -65.27) * mm, v(-133.54, -65.43) * mm, v(-133.55, -65.62) * mm, v(-133.47, -65.79) * mm]});
            skFitSpline(sketch, "E2354", {"points": [v(-133.47, -65.79) * mm, v(-133.38, -65.95) * mm, v(-133.21, -66.05) * mm, v(-133.03, -66.05) * mm]});
            skFitSpline(sketch, "E2355", {"points": [v(-316.71, -64.05) * mm, v(-316.71, -65.16) * mm, v(-315.82, -66.05) * mm, v(-314.71, -66.05) * mm]});
            skFitSpline(sketch, "E2356", {"points": [v(-298.71, -66.05) * mm, v(-297.61, -66.05) * mm, v(-296.71, -65.16) * mm, v(-296.71, -64.05) * mm]});
            skFitSpline(sketch, "E2357", {"points": [v(-310.4, -66.05) * mm, v(-310.21, -66.05) * mm, v(-310.04, -65.95) * mm, v(-309.96, -65.79) * mm]});
            skFitSpline(sketch, "E2358", {"points": [v(-309.96, -65.79) * mm, v(-309.87, -65.62) * mm, v(-309.88, -65.43) * mm, v(-309.98, -65.27) * mm]});
            skFitSpline(sketch, "E2359", {"points": [v(-303.44, -65.27) * mm, v(-303.55, -65.43) * mm, v(-303.56, -65.62) * mm, v(-303.47, -65.79) * mm]});
            skFitSpline(sketch, "E2360", {"points": [v(-303.47, -65.79) * mm, v(-303.39, -65.95) * mm, v(-303.22, -66.05) * mm, v(-303.03, -66.05) * mm]});
            skFitSpline(sketch, "E2361", {"points": [v(-303.44, -65.27) * mm, v(-302.33, -63.63) * mm, v(-302.61, -61.4) * mm, v(-304.1, -60.1) * mm]});
            skFitSpline(sketch, "E2362", {"points": [v(-304.1, -60.1) * mm, v(-305.6, -58.78) * mm, v(-307.83, -58.78) * mm, v(-309.33, -60.1) * mm]});
            skFitSpline(sketch, "E2363", {"points": [v(-309.33, -60.1) * mm, v(-310.82, -61.4) * mm, v(-311.1, -63.63) * mm, v(-309.98, -65.27) * mm]});
            skLineSegment(sketch, "E2364", {"start": v(-314.71, -66.05) * mm, "end": v(-310.4, -66.05) * mm});
            skLineSegment(sketch, "E2365", {"start": v(-303.03, -66.05) * mm, "end": v(-298.71, -66.05) * mm});
            skLineSegment(sketch, "E2366", {"start": v(-296.71, -64.05) * mm, "end": v(-296.71, -58.55) * mm});
            skLineSegment(sketch, "E2367", {"start": v(-316.71, -58.55) * mm, "end": v(-316.71, -64.05) * mm});
            skFitSpline(sketch, "E2368", {"points": [v(-346.89, 42.9) * mm, v(-349.65, 42.9) * mm, v(-351.89, 40.67) * mm, v(-351.89, 37.9) * mm]});
            skLineSegment(sketch, "E2369", {"start": v(-119.27, 36.52) * mm, "end": v(-324.15, 36.52) * mm});
            skFitSpline(sketch, "E2370", {"points": [v(-351.89, 3.52) * mm, v(-351.89, 0.76) * mm, v(-349.65, -1.48) * mm, v(-346.89, -1.48) * mm]});
            skLineSegment(sketch, "E2371", {"start": v(-325.1, 37.22) * mm, "end": v(-326.67, 42.2) * mm});
            skFitSpline(sketch, "E2372", {"points": [v(-316.71, -1.98) * mm, v(-316.71, -1.7) * mm, v(-316.94, -1.48) * mm, v(-317.21, -1.48) * mm]});
            skFitSpline(sketch, "E2373", {"points": [v(-296.21, -1.48) * mm, v(-296.35, -1.48) * mm, v(-296.47, -1.53) * mm, v(-296.57, -1.63) * mm]});
            skFitSpline(sketch, "E2374", {"points": [v(-296.57, -1.63) * mm, v(-296.66, -1.72) * mm, v(-296.71, -1.85) * mm, v(-296.71, -1.98) * mm]});
            skLineSegment(sketch, "E2375", {"start": v(-327.62, 42.9) * mm, "end": v(-346.89, 42.9) * mm});
            skFitSpline(sketch, "E2376", {"points": [v(-146.7, -1.98) * mm, v(-146.7, -1.7) * mm, v(-146.93, -1.48) * mm, v(-147.2, -1.48) * mm]});
            skLineSegment(sketch, "E2377", {"start": v(-351.89, 37.9) * mm, "end": v(-351.89, 3.52) * mm});
            skFitSpline(sketch, "E2378", {"points": [v(-146.7, -7.48) * mm, v(-146.7, -8.58) * mm, v(-145.81, -9.48) * mm, v(-144.7, -9.48) * mm]});
            skLineSegment(sketch, "E2379", {"start": v(-346.89, -1.48) * mm, "end": v(-317.21, -1.48) * mm});
            skFitSpline(sketch, "E2380", {"points": [v(-133.44, -8.7) * mm, v(-132.32, -7.05) * mm, v(-132.6, -4.83) * mm, v(-134.1, -3.52) * mm]});
            skFitSpline(sketch, "E2381", {"points": [v(-134.1, -3.52) * mm, v(-135.6, -2.2) * mm, v(-137.83, -2.2) * mm, v(-139.32, -3.52) * mm]});
            skFitSpline(sketch, "E2382", {"points": [v(-139.32, -3.52) * mm, v(-140.81, -4.83) * mm, v(-141.1, -7.05) * mm, v(-139.98, -8.7) * mm]});
            skLineSegment(sketch, "E2383", {"start": v(-296.21, -1.48) * mm, "end": v(-147.2, -1.48) * mm});
            skFitSpline(sketch, "E2384", {"points": [v(-128.7, -9.48) * mm, v(-128.18, -9.48) * mm, v(-127.67, -9.27) * mm, v(-127.3, -8.9) * mm]});
            skFitSpline(sketch, "E2385", {"points": [v(-127.3, -8.9) * mm, v(-126.92, -8.52) * mm, v(-126.7, -8) * mm, v(-126.7, -7.48) * mm]});
            skLineSegment(sketch, "E2386", {"start": v(-146.7, -1.98) * mm, "end": v(-146.7, -7.48) * mm});
            skFitSpline(sketch, "E2387", {"points": [v(-126.2, -1.48) * mm, v(-126.49, -1.48) * mm, v(-126.7, -1.7) * mm, v(-126.7, -1.98) * mm]});
            skLineSegment(sketch, "E2388", {"start": v(-144.7, -9.48) * mm, "end": v(-140.4, -9.48) * mm});
            skFitSpline(sketch, "E2389", {"points": [v(-96.54, -1.48) * mm, v(-93.78, -1.48) * mm, v(-91.54, 0.76) * mm, v(-91.54, 3.52) * mm]});
            skLineSegment(sketch, "E2390", {"start": v(-133.03, -9.48) * mm, "end": v(-128.7, -9.48) * mm});
            skFitSpline(sketch, "E2391", {"points": [v(-91.54, 37.9) * mm, v(-91.54, 40.67) * mm, v(-93.78, 42.9) * mm, v(-96.54, 42.9) * mm]});
            skLineSegment(sketch, "E2392", {"start": v(-126.7, -7.48) * mm, "end": v(-126.7, -1.98) * mm});
            skLineSegment(sketch, "E2393", {"start": v(-126.2, -1.48) * mm, "end": v(-96.54, -1.48) * mm});
            skFitSpline(sketch, "E2394", {"points": [v(-102.32, 25.4) * mm, v(-102.5, 25.4) * mm, v(-102.66, 25.31) * mm, v(-102.75, 25.16) * mm]});
            skFitSpline(sketch, "E2395", {"points": [v(-103.44, 25.84) * mm, v(-103.62, 25.74) * mm, v(-103.72, 25.53) * mm, v(-103.68, 25.32) * mm]});
            skFitSpline(sketch, "E2396", {"points": [v(-103.68, 25.32) * mm, v(-103.64, 25.11) * mm, v(-103.48, 24.95) * mm, v(-103.27, 24.91) * mm]});
            skFitSpline(sketch, "E2397", {"points": [v(-103.27, 24.91) * mm, v(-103.07, 24.88) * mm, v(-102.86, 24.98) * mm, v(-102.75, 25.16) * mm]});
            skFitSpline(sketch, "E2398", {"points": [v(-103.44, 25.84) * mm, v(-103.28, 25.93) * mm, v(-103.19, 26.1) * mm, v(-103.19, 26.27) * mm]});
            skLineSegment(sketch, "E2399", {"start": v(-91.54, 3.52) * mm, "end": v(-91.54, 37.9) * mm});
            skFitSpline(sketch, "E2400", {"points": [v(-103.19, 30.74) * mm, v(-103.19, 30.92) * mm, v(-103.28, 31.08) * mm, v(-103.44, 31.17) * mm]});
            skFitSpline(sketch, "E2401", {"points": [v(-102.75, 31.86) * mm, v(-102.86, 32.04) * mm, v(-103.07, 32.14) * mm, v(-103.27, 32.1) * mm]});
            skFitSpline(sketch, "E2402", {"points": [v(-103.27, 32.1) * mm, v(-103.48, 32.06) * mm, v(-103.64, 31.9) * mm, v(-103.68, 31.7) * mm]});
            skFitSpline(sketch, "E2403", {"points": [v(-103.68, 31.7) * mm, v(-103.72, 31.49) * mm, v(-103.62, 31.28) * mm, v(-103.44, 31.17) * mm]});
            skFitSpline(sketch, "E2404", {"points": [v(-102.75, 31.86) * mm, v(-102.67, 31.7) * mm, v(-102.5, 31.6) * mm, v(-102.32, 31.6) * mm]});
            skLineSegment(sketch, "E2405", {"start": v(-96.54, 42.9) * mm, "end": v(-115.8, 42.9) * mm});
            skFitSpline(sketch, "E2406", {"points": [v(-100.75, 31.6) * mm, v(-100.57, 31.6) * mm, v(-100.4, 31.7) * mm, v(-100.32, 31.86) * mm]});
            skFitSpline(sketch, "E2407", {"points": [v(-99.64, 31.17) * mm, v(-99.46, 31.28) * mm, v(-99.36, 31.49) * mm, v(-99.4, 31.7) * mm]});
            skFitSpline(sketch, "E2408", {"points": [v(-99.4, 31.7) * mm, v(-99.43, 31.9) * mm, v(-99.6, 32.06) * mm, v(-99.8, 32.1) * mm]});
            skFitSpline(sketch, "E2409", {"points": [v(-99.8, 32.1) * mm, v(-100, 32.14) * mm, v(-100.22, 32.04) * mm, v(-100.32, 31.86) * mm]});
            skFitSpline(sketch, "E2410", {"points": [v(-99.64, 31.17) * mm, v(-99.8, 31.08) * mm, v(-99.89, 30.92) * mm, v(-99.89, 30.74) * mm]});
            skLineSegment(sketch, "E2411", {"start": v(-116.76, 42.2) * mm, "end": v(-118.32, 37.22) * mm});
            skFitSpline(sketch, "E2412", {"points": [v(-99.89, 26.27) * mm, v(-99.89, 26.1) * mm, v(-99.8, 25.93) * mm, v(-99.64, 25.84) * mm]});
            skFitSpline(sketch, "E2413", {"points": [v(-100.32, 25.16) * mm, v(-100.22, 24.98) * mm, v(-100, 24.88) * mm, v(-99.8, 24.91) * mm]});
            skFitSpline(sketch, "E2414", {"points": [v(-99.8, 24.91) * mm, v(-99.6, 24.95) * mm, v(-99.43, 25.11) * mm, v(-99.4, 25.32) * mm]});
            skFitSpline(sketch, "E2415", {"points": [v(-99.4, 25.32) * mm, v(-99.36, 25.53) * mm, v(-99.46, 25.74) * mm, v(-99.64, 25.84) * mm]});
            skFitSpline(sketch, "E2416", {"points": [v(-100.32, 25.16) * mm, v(-100.4, 25.31) * mm, v(-100.57, 25.4) * mm, v(-100.75, 25.4) * mm]});
            skLineSegment(sketch, "E2417", {"start": v(-103.19, 26.27) * mm, "end": v(-103.19, 30.74) * mm});
            skFitSpline(sketch, "E2418", {"points": [v(-102.32, 4.2) * mm, v(-102.5, 4.2) * mm, v(-102.66, 4.11) * mm, v(-102.75, 3.96) * mm]});
            skFitSpline(sketch, "E2419", {"points": [v(-103.44, 4.64) * mm, v(-103.62, 4.54) * mm, v(-103.72, 4.33) * mm, v(-103.68, 4.12) * mm]});
            skFitSpline(sketch, "E2420", {"points": [v(-103.68, 4.12) * mm, v(-103.64, 3.91) * mm, v(-103.48, 3.75) * mm, v(-103.27, 3.71) * mm]});
            skFitSpline(sketch, "E2421", {"points": [v(-103.27, 3.71) * mm, v(-103.07, 3.68) * mm, v(-102.86, 3.78) * mm, v(-102.75, 3.96) * mm]});
            skFitSpline(sketch, "E2422", {"points": [v(-103.44, 4.64) * mm, v(-103.28, 4.73) * mm, v(-103.19, 4.9) * mm, v(-103.19, 5.07) * mm]});
            skLineSegment(sketch, "E2423", {"start": v(-102.32, 31.6) * mm, "end": v(-100.75, 31.6) * mm});
            skFitSpline(sketch, "E2424", {"points": [v(-103.19, 9.54) * mm, v(-103.19, 9.72) * mm, v(-103.28, 9.88) * mm, v(-103.44, 9.97) * mm]});
            skFitSpline(sketch, "E2425", {"points": [v(-102.75, 10.66) * mm, v(-102.86, 10.84) * mm, v(-103.07, 10.94) * mm, v(-103.27, 10.9) * mm]});
            skFitSpline(sketch, "E2426", {"points": [v(-103.27, 10.9) * mm, v(-103.48, 10.86) * mm, v(-103.64, 10.7) * mm, v(-103.68, 10.5) * mm]});
            skFitSpline(sketch, "E2427", {"points": [v(-103.68, 10.5) * mm, v(-103.72, 10.29) * mm, v(-103.62, 10.08) * mm, v(-103.44, 9.97) * mm]});
            skFitSpline(sketch, "E2428", {"points": [v(-102.75, 10.66) * mm, v(-102.67, 10.5) * mm, v(-102.5, 10.4) * mm, v(-102.32, 10.4) * mm]});
            skLineSegment(sketch, "E2429", {"start": v(-99.89, 30.74) * mm, "end": v(-99.89, 26.27) * mm});
            skFitSpline(sketch, "E2430", {"points": [v(-100.75, 10.4) * mm, v(-100.57, 10.4) * mm, v(-100.4, 10.5) * mm, v(-100.32, 10.66) * mm]});
            skFitSpline(sketch, "E2431", {"points": [v(-99.64, 9.97) * mm, v(-99.46, 10.08) * mm, v(-99.36, 10.29) * mm, v(-99.4, 10.5) * mm]});
            skFitSpline(sketch, "E2432", {"points": [v(-99.4, 10.5) * mm, v(-99.43, 10.7) * mm, v(-99.6, 10.86) * mm, v(-99.8, 10.9) * mm]});
            skFitSpline(sketch, "E2433", {"points": [v(-99.8, 10.9) * mm, v(-100, 10.94) * mm, v(-100.22, 10.84) * mm, v(-100.32, 10.66) * mm]});
            skFitSpline(sketch, "E2434", {"points": [v(-99.64, 9.97) * mm, v(-99.8, 9.88) * mm, v(-99.89, 9.72) * mm, v(-99.89, 9.54) * mm]});
            skLineSegment(sketch, "E2435", {"start": v(-100.75, 25.4) * mm, "end": v(-102.32, 25.4) * mm});
            skFitSpline(sketch, "E2436", {"points": [v(-99.89, 5.07) * mm, v(-99.89, 4.9) * mm, v(-99.8, 4.73) * mm, v(-99.64, 4.64) * mm]});
            skFitSpline(sketch, "E2437", {"points": [v(-100.32, 3.96) * mm, v(-100.22, 3.78) * mm, v(-100, 3.68) * mm, v(-99.8, 3.71) * mm]});
            skFitSpline(sketch, "E2438", {"points": [v(-99.8, 3.71) * mm, v(-99.6, 3.75) * mm, v(-99.43, 3.91) * mm, v(-99.4, 4.12) * mm]});
            skFitSpline(sketch, "E2439", {"points": [v(-99.4, 4.12) * mm, v(-99.36, 4.33) * mm, v(-99.46, 4.54) * mm, v(-99.64, 4.64) * mm]});
            skFitSpline(sketch, "E2440", {"points": [v(-100.32, 3.96) * mm, v(-100.4, 4.11) * mm, v(-100.57, 4.2) * mm, v(-100.75, 4.2) * mm]});
            skLineSegment(sketch, "E2441", {"start": v(-103.19, 5.07) * mm, "end": v(-103.19, 9.54) * mm});
            skFitSpline(sketch, "E2442", {"points": [v(-216.2, 25.02) * mm, v(-216.37, 25.02) * mm, v(-216.54, 24.92) * mm, v(-216.63, 24.77) * mm]});
            skFitSpline(sketch, "E2443", {"points": [v(-217.31, 25.45) * mm, v(-217.5, 25.35) * mm, v(-217.6, 25.14) * mm, v(-217.55, 24.93) * mm]});
            skFitSpline(sketch, "E2444", {"points": [v(-217.55, 24.93) * mm, v(-217.52, 24.73) * mm, v(-217.36, 24.56) * mm, v(-217.15, 24.53) * mm]});
            skFitSpline(sketch, "E2445", {"points": [v(-217.15, 24.53) * mm, v(-216.94, 24.5) * mm, v(-216.73, 24.59) * mm, v(-216.63, 24.77) * mm]});
            skFitSpline(sketch, "E2446", {"points": [v(-217.31, 25.45) * mm, v(-217.16, 25.54) * mm, v(-217.06, 25.7) * mm, v(-217.06, 25.89) * mm]});
            skLineSegment(sketch, "E2447", {"start": v(-102.32, 10.4) * mm, "end": v(-100.75, 10.4) * mm});
            skFitSpline(sketch, "E2448", {"points": [v(-217.06, 30.35) * mm, v(-217.06, 30.53) * mm, v(-217.16, 30.7) * mm, v(-217.31, 30.79) * mm]});
            skFitSpline(sketch, "E2449", {"points": [v(-216.63, 31.47) * mm, v(-216.73, 31.65) * mm, v(-216.94, 31.75) * mm, v(-217.15, 31.71) * mm]});
            skFitSpline(sketch, "E2450", {"points": [v(-217.15, 31.71) * mm, v(-217.36, 31.68) * mm, v(-217.52, 31.51) * mm, v(-217.55, 31.3) * mm]});
            skFitSpline(sketch, "E2451", {"points": [v(-217.55, 31.3) * mm, v(-217.6, 31.1) * mm, v(-217.5, 30.9) * mm, v(-217.31, 30.79) * mm]});
            skFitSpline(sketch, "E2452", {"points": [v(-216.63, 31.47) * mm, v(-216.54, 31.31) * mm, v(-216.37, 31.22) * mm, v(-216.2, 31.22) * mm]});
            skLineSegment(sketch, "E2453", {"start": v(-99.89, 9.54) * mm, "end": v(-99.89, 5.07) * mm});
            skFitSpline(sketch, "E2454", {"points": [v(-214.63, 31.22) * mm, v(-214.45, 31.22) * mm, v(-214.28, 31.31) * mm, v(-214.2, 31.47) * mm]});
            skFitSpline(sketch, "E2455", {"points": [v(-213.51, 30.79) * mm, v(-213.33, 30.9) * mm, v(-213.23, 31.1) * mm, v(-213.27, 31.3) * mm]});
            skFitSpline(sketch, "E2456", {"points": [v(-213.27, 31.3) * mm, v(-213.3, 31.51) * mm, v(-213.47, 31.68) * mm, v(-213.68, 31.71) * mm]});
            skFitSpline(sketch, "E2457", {"points": [v(-213.68, 31.71) * mm, v(-213.88, 31.75) * mm, v(-214.1, 31.65) * mm, v(-214.2, 31.47) * mm]});
            skFitSpline(sketch, "E2458", {"points": [v(-213.51, 30.79) * mm, v(-213.67, 30.7) * mm, v(-213.76, 30.53) * mm, v(-213.76, 30.35) * mm]});
            skLineSegment(sketch, "E2459", {"start": v(-100.75, 4.2) * mm, "end": v(-102.32, 4.2) * mm});
            skFitSpline(sketch, "E2460", {"points": [v(-213.76, 25.89) * mm, v(-213.76, 25.7) * mm, v(-213.67, 25.54) * mm, v(-213.51, 25.45) * mm]});
            skFitSpline(sketch, "E2461", {"points": [v(-214.2, 24.77) * mm, v(-214.1, 24.59) * mm, v(-213.88, 24.5) * mm, v(-213.68, 24.53) * mm]});
            skFitSpline(sketch, "E2462", {"points": [v(-213.68, 24.53) * mm, v(-213.47, 24.56) * mm, v(-213.3, 24.73) * mm, v(-213.27, 24.93) * mm]});
            skFitSpline(sketch, "E2463", {"points": [v(-213.27, 24.93) * mm, v(-213.23, 25.14) * mm, v(-213.33, 25.35) * mm, v(-213.51, 25.45) * mm]});
            skFitSpline(sketch, "E2464", {"points": [v(-214.2, 24.77) * mm, v(-214.28, 24.92) * mm, v(-214.45, 25.02) * mm, v(-214.63, 25.02) * mm]});
            skLineSegment(sketch, "E2465", {"start": v(-217.06, 25.89) * mm, "end": v(-217.06, 30.35) * mm});
            skFitSpline(sketch, "E2466", {"points": [v(-216.2, 3.82) * mm, v(-216.37, 3.82) * mm, v(-216.54, 3.72) * mm, v(-216.63, 3.57) * mm]});
            skFitSpline(sketch, "E2467", {"points": [v(-217.31, 4.25) * mm, v(-217.5, 4.15) * mm, v(-217.6, 3.94) * mm, v(-217.55, 3.73) * mm]});
            skFitSpline(sketch, "E2468", {"points": [v(-217.55, 3.73) * mm, v(-217.52, 3.53) * mm, v(-217.36, 3.36) * mm, v(-217.15, 3.33) * mm]});
            skFitSpline(sketch, "E2469", {"points": [v(-217.15, 3.33) * mm, v(-216.94, 3.3) * mm, v(-216.73, 3.39) * mm, v(-216.63, 3.57) * mm]});
            skFitSpline(sketch, "E2470", {"points": [v(-217.31, 4.25) * mm, v(-217.16, 4.34) * mm, v(-217.06, 4.5) * mm, v(-217.06, 4.69) * mm]});
            skLineSegment(sketch, "E2471", {"start": v(-216.2, 31.22) * mm, "end": v(-214.63, 31.22) * mm});
            skFitSpline(sketch, "E2472", {"points": [v(-217.06, 9.15) * mm, v(-217.06, 9.33) * mm, v(-217.16, 9.5) * mm, v(-217.31, 9.59) * mm]});
            skFitSpline(sketch, "E2473", {"points": [v(-216.63, 10.27) * mm, v(-216.73, 10.45) * mm, v(-216.94, 10.55) * mm, v(-217.15, 10.51) * mm]});
            skFitSpline(sketch, "E2474", {"points": [v(-217.15, 10.51) * mm, v(-217.36, 10.48) * mm, v(-217.52, 10.31) * mm, v(-217.55, 10.1) * mm]});
            skFitSpline(sketch, "E2475", {"points": [v(-217.55, 10.1) * mm, v(-217.6, 9.9) * mm, v(-217.5, 9.7) * mm, v(-217.31, 9.59) * mm]});
            skFitSpline(sketch, "E2476", {"points": [v(-216.63, 10.27) * mm, v(-216.54, 10.11) * mm, v(-216.37, 10.02) * mm, v(-216.2, 10.02) * mm]});
            skLineSegment(sketch, "E2477", {"start": v(-213.76, 30.35) * mm, "end": v(-213.76, 25.89) * mm});
            skFitSpline(sketch, "E2478", {"points": [v(-214.63, 10.02) * mm, v(-214.45, 10.02) * mm, v(-214.28, 10.11) * mm, v(-214.2, 10.27) * mm]});
            skFitSpline(sketch, "E2479", {"points": [v(-213.51, 9.59) * mm, v(-213.33, 9.7) * mm, v(-213.23, 9.9) * mm, v(-213.27, 10.1) * mm]});
            skFitSpline(sketch, "E2480", {"points": [v(-213.27, 10.1) * mm, v(-213.3, 10.31) * mm, v(-213.47, 10.48) * mm, v(-213.68, 10.51) * mm]});
            skFitSpline(sketch, "E2481", {"points": [v(-213.68, 10.51) * mm, v(-213.88, 10.55) * mm, v(-214.1, 10.45) * mm, v(-214.2, 10.27) * mm]});
            skFitSpline(sketch, "E2482", {"points": [v(-213.51, 9.59) * mm, v(-213.67, 9.5) * mm, v(-213.76, 9.33) * mm, v(-213.76, 9.15) * mm]});
            skLineSegment(sketch, "E2483", {"start": v(-214.63, 25.02) * mm, "end": v(-216.2, 25.02) * mm});
            skFitSpline(sketch, "E2484", {"points": [v(-213.76, 4.69) * mm, v(-213.76, 4.5) * mm, v(-213.67, 4.34) * mm, v(-213.51, 4.25) * mm]});
            skFitSpline(sketch, "E2485", {"points": [v(-214.2, 3.57) * mm, v(-214.1, 3.39) * mm, v(-213.88, 3.3) * mm, v(-213.68, 3.33) * mm]});
            skFitSpline(sketch, "E2486", {"points": [v(-213.68, 3.33) * mm, v(-213.47, 3.36) * mm, v(-213.3, 3.53) * mm, v(-213.27, 3.73) * mm]});
            skFitSpline(sketch, "E2487", {"points": [v(-213.27, 3.73) * mm, v(-213.23, 3.94) * mm, v(-213.33, 4.15) * mm, v(-213.51, 4.25) * mm]});
            skFitSpline(sketch, "E2488", {"points": [v(-214.2, 3.57) * mm, v(-214.28, 3.72) * mm, v(-214.45, 3.82) * mm, v(-214.63, 3.82) * mm]});
            skLineSegment(sketch, "E2489", {"start": v(-217.06, 4.69) * mm, "end": v(-217.06, 9.15) * mm});
            skFitSpline(sketch, "E2490", {"points": [v(-228.8, 25.02) * mm, v(-228.97, 25.02) * mm, v(-229.14, 24.92) * mm, v(-229.23, 24.77) * mm]});
            skFitSpline(sketch, "E2491", {"points": [v(-229.91, 25.45) * mm, v(-230.1, 25.35) * mm, v(-230.2, 25.14) * mm, v(-230.15, 24.93) * mm]});
            skFitSpline(sketch, "E2492", {"points": [v(-230.15, 24.93) * mm, v(-230.12, 24.73) * mm, v(-229.96, 24.56) * mm, v(-229.75, 24.53) * mm]});
            skFitSpline(sketch, "E2493", {"points": [v(-229.75, 24.53) * mm, v(-229.54, 24.5) * mm, v(-229.33, 24.59) * mm, v(-229.23, 24.77) * mm]});
            skFitSpline(sketch, "E2494", {"points": [v(-229.91, 25.45) * mm, v(-229.76, 25.54) * mm, v(-229.66, 25.7) * mm, v(-229.66, 25.89) * mm]});
            skLineSegment(sketch, "E2495", {"start": v(-216.2, 10.02) * mm, "end": v(-214.63, 10.02) * mm});
            skFitSpline(sketch, "E2496", {"points": [v(-229.66, 30.35) * mm, v(-229.66, 30.53) * mm, v(-229.76, 30.7) * mm, v(-229.91, 30.79) * mm]});
            skFitSpline(sketch, "E2497", {"points": [v(-229.23, 31.47) * mm, v(-229.33, 31.65) * mm, v(-229.54, 31.75) * mm, v(-229.75, 31.71) * mm]});
            skFitSpline(sketch, "E2498", {"points": [v(-229.75, 31.71) * mm, v(-229.96, 31.68) * mm, v(-230.12, 31.51) * mm, v(-230.15, 31.3) * mm]});
            skFitSpline(sketch, "E2499", {"points": [v(-230.15, 31.3) * mm, v(-230.2, 31.1) * mm, v(-230.1, 30.9) * mm, v(-229.91, 30.79) * mm]});
            skFitSpline(sketch, "E2500", {"points": [v(-229.23, 31.47) * mm, v(-229.14, 31.31) * mm, v(-228.97, 31.22) * mm, v(-228.8, 31.22) * mm]});
            skLineSegment(sketch, "E2501", {"start": v(-213.76, 9.15) * mm, "end": v(-213.76, 4.69) * mm});
            skFitSpline(sketch, "E2502", {"points": [v(-227.23, 31.22) * mm, v(-227.05, 31.22) * mm, v(-226.88, 31.31) * mm, v(-226.8, 31.47) * mm]});
            skFitSpline(sketch, "E2503", {"points": [v(-226.11, 30.79) * mm, v(-225.93, 30.9) * mm, v(-225.83, 31.1) * mm, v(-225.87, 31.3) * mm]});
            skFitSpline(sketch, "E2504", {"points": [v(-225.87, 31.3) * mm, v(-225.9, 31.51) * mm, v(-226.07, 31.68) * mm, v(-226.28, 31.71) * mm]});
            skFitSpline(sketch, "E2505", {"points": [v(-226.28, 31.71) * mm, v(-226.48, 31.75) * mm, v(-226.7, 31.65) * mm, v(-226.8, 31.47) * mm]});
            skFitSpline(sketch, "E2506", {"points": [v(-226.11, 30.79) * mm, v(-226.27, 30.7) * mm, v(-226.36, 30.53) * mm, v(-226.36, 30.35) * mm]});
            skLineSegment(sketch, "E2507", {"start": v(-214.63, 3.82) * mm, "end": v(-216.2, 3.82) * mm});
            skFitSpline(sketch, "E2508", {"points": [v(-226.36, 25.89) * mm, v(-226.36, 25.7) * mm, v(-226.27, 25.54) * mm, v(-226.11, 25.45) * mm]});
            skFitSpline(sketch, "E2509", {"points": [v(-226.8, 24.77) * mm, v(-226.7, 24.59) * mm, v(-226.48, 24.5) * mm, v(-226.28, 24.53) * mm]});
            skFitSpline(sketch, "E2510", {"points": [v(-226.28, 24.53) * mm, v(-226.07, 24.56) * mm, v(-225.9, 24.73) * mm, v(-225.87, 24.93) * mm]});
            skFitSpline(sketch, "E2511", {"points": [v(-225.87, 24.93) * mm, v(-225.83, 25.14) * mm, v(-225.93, 25.35) * mm, v(-226.11, 25.45) * mm]});
            skFitSpline(sketch, "E2512", {"points": [v(-226.8, 24.77) * mm, v(-226.88, 24.92) * mm, v(-227.05, 25.02) * mm, v(-227.23, 25.02) * mm]});
            skLineSegment(sketch, "E2513", {"start": v(-229.66, 25.89) * mm, "end": v(-229.66, 30.35) * mm});
            skFitSpline(sketch, "E2514", {"points": [v(-228.8, 3.82) * mm, v(-228.97, 3.82) * mm, v(-229.14, 3.72) * mm, v(-229.23, 3.57) * mm]});
            skFitSpline(sketch, "E2515", {"points": [v(-229.91, 4.25) * mm, v(-230.1, 4.15) * mm, v(-230.2, 3.94) * mm, v(-230.15, 3.73) * mm]});
            skFitSpline(sketch, "E2516", {"points": [v(-230.15, 3.73) * mm, v(-230.12, 3.53) * mm, v(-229.96, 3.36) * mm, v(-229.75, 3.33) * mm]});
            skFitSpline(sketch, "E2517", {"points": [v(-229.75, 3.33) * mm, v(-229.54, 3.3) * mm, v(-229.33, 3.39) * mm, v(-229.23, 3.57) * mm]});
            skFitSpline(sketch, "E2518", {"points": [v(-229.91, 4.25) * mm, v(-229.76, 4.34) * mm, v(-229.66, 4.5) * mm, v(-229.66, 4.69) * mm]});
            skLineSegment(sketch, "E2519", {"start": v(-228.8, 31.22) * mm, "end": v(-227.23, 31.22) * mm});
            skFitSpline(sketch, "E2520", {"points": [v(-229.66, 9.15) * mm, v(-229.66, 9.33) * mm, v(-229.76, 9.5) * mm, v(-229.91, 9.59) * mm]});
            skFitSpline(sketch, "E2521", {"points": [v(-229.23, 10.27) * mm, v(-229.33, 10.45) * mm, v(-229.54, 10.55) * mm, v(-229.75, 10.51) * mm]});
            skFitSpline(sketch, "E2522", {"points": [v(-229.75, 10.51) * mm, v(-229.96, 10.48) * mm, v(-230.12, 10.31) * mm, v(-230.15, 10.1) * mm]});
            skFitSpline(sketch, "E2523", {"points": [v(-230.15, 10.1) * mm, v(-230.2, 9.9) * mm, v(-230.1, 9.7) * mm, v(-229.91, 9.59) * mm]});
            skFitSpline(sketch, "E2524", {"points": [v(-229.23, 10.27) * mm, v(-229.14, 10.11) * mm, v(-228.97, 10.02) * mm, v(-228.8, 10.02) * mm]});
            skLineSegment(sketch, "E2525", {"start": v(-226.36, 30.35) * mm, "end": v(-226.36, 25.89) * mm});
            skFitSpline(sketch, "E2526", {"points": [v(-227.23, 10.02) * mm, v(-227.05, 10.02) * mm, v(-226.88, 10.11) * mm, v(-226.8, 10.27) * mm]});
            skFitSpline(sketch, "E2527", {"points": [v(-226.11, 9.59) * mm, v(-225.93, 9.7) * mm, v(-225.83, 9.9) * mm, v(-225.87, 10.1) * mm]});
            skFitSpline(sketch, "E2528", {"points": [v(-225.87, 10.1) * mm, v(-225.9, 10.31) * mm, v(-226.07, 10.48) * mm, v(-226.28, 10.51) * mm]});
            skFitSpline(sketch, "E2529", {"points": [v(-226.28, 10.51) * mm, v(-226.48, 10.55) * mm, v(-226.7, 10.45) * mm, v(-226.8, 10.27) * mm]});
            skFitSpline(sketch, "E2530", {"points": [v(-226.11, 9.59) * mm, v(-226.27, 9.5) * mm, v(-226.36, 9.33) * mm, v(-226.36, 9.15) * mm]});
            skLineSegment(sketch, "E2531", {"start": v(-227.23, 25.02) * mm, "end": v(-228.8, 25.02) * mm});
            skFitSpline(sketch, "E2532", {"points": [v(-226.36, 4.69) * mm, v(-226.36, 4.5) * mm, v(-226.27, 4.34) * mm, v(-226.11, 4.25) * mm]});
            skFitSpline(sketch, "E2533", {"points": [v(-226.8, 3.57) * mm, v(-226.7, 3.39) * mm, v(-226.48, 3.3) * mm, v(-226.28, 3.33) * mm]});
            skFitSpline(sketch, "E2534", {"points": [v(-226.28, 3.33) * mm, v(-226.07, 3.36) * mm, v(-225.9, 3.53) * mm, v(-225.87, 3.73) * mm]});
            skFitSpline(sketch, "E2535", {"points": [v(-225.87, 3.73) * mm, v(-225.83, 3.94) * mm, v(-225.93, 4.15) * mm, v(-226.11, 4.25) * mm]});
            skFitSpline(sketch, "E2536", {"points": [v(-226.8, 3.57) * mm, v(-226.88, 3.72) * mm, v(-227.05, 3.82) * mm, v(-227.23, 3.82) * mm]});
            skLineSegment(sketch, "E2537", {"start": v(-229.66, 4.69) * mm, "end": v(-229.66, 9.15) * mm});
            skFitSpline(sketch, "E2538", {"points": [v(-340.67, 25.16) * mm, v(-340.76, 25.31) * mm, v(-340.92, 25.4) * mm, v(-341.1, 25.4) * mm]});
            skFitSpline(sketch, "E2539", {"points": [v(-340.67, 25.16) * mm, v(-340.57, 24.98) * mm, v(-340.36, 24.88) * mm, v(-340.15, 24.91) * mm]});
            skFitSpline(sketch, "E2540", {"points": [v(-340.15, 24.91) * mm, v(-339.94, 24.95) * mm, v(-339.78, 25.11) * mm, v(-339.75, 25.32) * mm]});
            skFitSpline(sketch, "E2541", {"points": [v(-339.75, 25.32) * mm, v(-339.7, 25.53) * mm, v(-339.8, 25.74) * mm, v(-339.99, 25.84) * mm]});
            skFitSpline(sketch, "E2542", {"points": [v(-340.24, 26.27) * mm, v(-340.24, 26.1) * mm, v(-340.14, 25.93) * mm, v(-339.99, 25.84) * mm]});
            skLineSegment(sketch, "E2543", {"start": v(-228.8, 10.02) * mm, "end": v(-227.23, 10.02) * mm});
            skFitSpline(sketch, "E2544", {"points": [v(-339.99, 31.17) * mm, v(-340.14, 31.08) * mm, v(-340.24, 30.92) * mm, v(-340.24, 30.74) * mm]});
            skFitSpline(sketch, "E2545", {"points": [v(-339.99, 31.17) * mm, v(-339.8, 31.28) * mm, v(-339.7, 31.49) * mm, v(-339.75, 31.7) * mm]});
            skFitSpline(sketch, "E2546", {"points": [v(-339.75, 31.7) * mm, v(-339.78, 31.9) * mm, v(-339.94, 32.06) * mm, v(-340.15, 32.1) * mm]});
            skFitSpline(sketch, "E2547", {"points": [v(-340.15, 32.1) * mm, v(-340.36, 32.14) * mm, v(-340.57, 32.04) * mm, v(-340.67, 31.86) * mm]});
            skFitSpline(sketch, "E2548", {"points": [v(-341.1, 31.6) * mm, v(-340.92, 31.6) * mm, v(-340.76, 31.7) * mm, v(-340.67, 31.86) * mm]});
            skLineSegment(sketch, "E2549", {"start": v(-226.36, 9.15) * mm, "end": v(-226.36, 4.69) * mm});
            skFitSpline(sketch, "E2550", {"points": [v(-343.1, 31.86) * mm, v(-343.02, 31.7) * mm, v(-342.85, 31.6) * mm, v(-342.67, 31.6) * mm]});
            skFitSpline(sketch, "E2551", {"points": [v(-343.1, 31.86) * mm, v(-343.2, 32.04) * mm, v(-343.42, 32.14) * mm, v(-343.62, 32.1) * mm]});
            skFitSpline(sketch, "E2552", {"points": [v(-343.62, 32.1) * mm, v(-343.83, 32.06) * mm, v(-344, 31.9) * mm, v(-344.03, 31.7) * mm]});
            skFitSpline(sketch, "E2553", {"points": [v(-344.03, 31.7) * mm, v(-344.07, 31.49) * mm, v(-343.97, 31.28) * mm, v(-343.79, 31.17) * mm]});
            skFitSpline(sketch, "E2554", {"points": [v(-343.54, 30.74) * mm, v(-343.54, 30.92) * mm, v(-343.63, 31.08) * mm, v(-343.79, 31.17) * mm]});
            skLineSegment(sketch, "E2555", {"start": v(-227.23, 3.82) * mm, "end": v(-228.8, 3.82) * mm});
            skFitSpline(sketch, "E2556", {"points": [v(-343.79, 25.84) * mm, v(-343.63, 25.93) * mm, v(-343.54, 26.1) * mm, v(-343.54, 26.27) * mm]});
            skFitSpline(sketch, "E2557", {"points": [v(-343.79, 25.84) * mm, v(-343.97, 25.74) * mm, v(-344.07, 25.53) * mm, v(-344.03, 25.32) * mm]});
            skFitSpline(sketch, "E2558", {"points": [v(-344.03, 25.32) * mm, v(-344, 25.11) * mm, v(-343.83, 24.95) * mm, v(-343.62, 24.91) * mm]});
            skFitSpline(sketch, "E2559", {"points": [v(-343.62, 24.91) * mm, v(-343.42, 24.88) * mm, v(-343.2, 24.98) * mm, v(-343.1, 25.16) * mm]});
            skFitSpline(sketch, "E2560", {"points": [v(-342.67, 25.4) * mm, v(-342.85, 25.4) * mm, v(-343.02, 25.31) * mm, v(-343.1, 25.16) * mm]});
            skLineSegment(sketch, "E2561", {"start": v(-340.24, 26.27) * mm, "end": v(-340.24, 30.74) * mm});
            skFitSpline(sketch, "E2562", {"points": [v(-340.67, 3.96) * mm, v(-340.76, 4.11) * mm, v(-340.92, 4.2) * mm, v(-341.1, 4.2) * mm]});
            skFitSpline(sketch, "E2563", {"points": [v(-340.67, 3.96) * mm, v(-340.57, 3.78) * mm, v(-340.36, 3.68) * mm, v(-340.15, 3.71) * mm]});
            skFitSpline(sketch, "E2564", {"points": [v(-340.15, 3.71) * mm, v(-339.94, 3.75) * mm, v(-339.78, 3.91) * mm, v(-339.75, 4.12) * mm]});
            skFitSpline(sketch, "E2565", {"points": [v(-339.75, 4.12) * mm, v(-339.7, 4.33) * mm, v(-339.8, 4.54) * mm, v(-339.99, 4.64) * mm]});
            skFitSpline(sketch, "E2566", {"points": [v(-340.24, 5.07) * mm, v(-340.24, 4.9) * mm, v(-340.14, 4.73) * mm, v(-339.99, 4.64) * mm]});
            skLineSegment(sketch, "E2567", {"start": v(-341.1, 31.6) * mm, "end": v(-342.67, 31.6) * mm});
            skFitSpline(sketch, "E2568", {"points": [v(-339.99, 9.97) * mm, v(-340.14, 9.88) * mm, v(-340.24, 9.72) * mm, v(-340.24, 9.54) * mm]});
            skFitSpline(sketch, "E2569", {"points": [v(-339.99, 9.97) * mm, v(-339.8, 10.08) * mm, v(-339.7, 10.29) * mm, v(-339.75, 10.5) * mm]});
            skFitSpline(sketch, "E2570", {"points": [v(-339.75, 10.5) * mm, v(-339.78, 10.7) * mm, v(-339.94, 10.86) * mm, v(-340.15, 10.9) * mm]});
            skFitSpline(sketch, "E2571", {"points": [v(-340.15, 10.9) * mm, v(-340.36, 10.94) * mm, v(-340.57, 10.84) * mm, v(-340.67, 10.66) * mm]});
            skFitSpline(sketch, "E2572", {"points": [v(-341.1, 10.4) * mm, v(-340.92, 10.4) * mm, v(-340.76, 10.5) * mm, v(-340.67, 10.66) * mm]});
            skLineSegment(sketch, "E2573", {"start": v(-343.54, 30.74) * mm, "end": v(-343.54, 26.27) * mm});
            skFitSpline(sketch, "E2574", {"points": [v(-343.1, 10.66) * mm, v(-343.02, 10.5) * mm, v(-342.85, 10.4) * mm, v(-342.67, 10.4) * mm]});
            skFitSpline(sketch, "E2575", {"points": [v(-343.1, 10.66) * mm, v(-343.2, 10.84) * mm, v(-343.42, 10.94) * mm, v(-343.62, 10.9) * mm]});
            skFitSpline(sketch, "E2576", {"points": [v(-343.62, 10.9) * mm, v(-343.83, 10.86) * mm, v(-344, 10.7) * mm, v(-344.03, 10.5) * mm]});
            skFitSpline(sketch, "E2577", {"points": [v(-344.03, 10.5) * mm, v(-344.07, 10.29) * mm, v(-343.97, 10.08) * mm, v(-343.79, 9.97) * mm]});
            skFitSpline(sketch, "E2578", {"points": [v(-343.54, 9.54) * mm, v(-343.54, 9.72) * mm, v(-343.63, 9.88) * mm, v(-343.79, 9.97) * mm]});
            skLineSegment(sketch, "E2579", {"start": v(-342.67, 25.4) * mm, "end": v(-341.1, 25.4) * mm});
            skFitSpline(sketch, "E2580", {"points": [v(-343.79, 4.64) * mm, v(-343.63, 4.73) * mm, v(-343.54, 4.9) * mm, v(-343.54, 5.07) * mm]});
            skFitSpline(sketch, "E2581", {"points": [v(-343.79, 4.64) * mm, v(-343.97, 4.54) * mm, v(-344.07, 4.33) * mm, v(-344.03, 4.12) * mm]});
            skFitSpline(sketch, "E2582", {"points": [v(-344.03, 4.12) * mm, v(-344, 3.91) * mm, v(-343.83, 3.75) * mm, v(-343.62, 3.71) * mm]});
            skFitSpline(sketch, "E2583", {"points": [v(-343.62, 3.71) * mm, v(-343.42, 3.68) * mm, v(-343.2, 3.78) * mm, v(-343.1, 3.96) * mm]});
            skFitSpline(sketch, "E2584", {"points": [v(-342.67, 4.2) * mm, v(-342.85, 4.2) * mm, v(-343.02, 4.11) * mm, v(-343.1, 3.96) * mm]});
            skLineSegment(sketch, "E2585", {"start": v(-340.24, 5.07) * mm, "end": v(-340.24, 9.54) * mm});
            skFitSpline(sketch, "E2586", {"points": [v(-99.94, 17.9) * mm, v(-99.94, 18.48) * mm, v(-100.24, 19) * mm, v(-100.74, 19.3) * mm]});
            skFitSpline(sketch, "E2587", {"points": [v(-100.74, 19.3) * mm, v(-101.23, 19.58) * mm, v(-101.84, 19.58) * mm, v(-102.34, 19.3) * mm]});
            skFitSpline(sketch, "E2588", {"points": [v(-102.34, 19.3) * mm, v(-102.83, 19) * mm, v(-103.14, 18.48) * mm, v(-103.14, 17.9) * mm]});
            skFitSpline(sketch, "E2589", {"points": [v(-103.14, 17.9) * mm, v(-103.14, 17.34) * mm, v(-102.83, 16.8) * mm, v(-102.34, 16.52) * mm]});
            skFitSpline(sketch, "E2590", {"points": [v(-102.34, 16.52) * mm, v(-101.84, 16.24) * mm, v(-101.23, 16.24) * mm, v(-100.74, 16.52) * mm]});
            skFitSpline(sketch, "E2591", {"points": [v(-100.74, 16.52) * mm, v(-100.24, 16.8) * mm, v(-99.94, 17.34) * mm, v(-99.94, 17.9) * mm]});
            skLineSegment(sketch, "E2592", {"start": v(-341.1, 10.4) * mm, "end": v(-342.67, 10.4) * mm});
            skFitSpline(sketch, "E2593", {"points": [v(-154.11, 27.9) * mm, v(-154.11, 28.48) * mm, v(-154.42, 29) * mm, v(-154.91, 29.3) * mm]});
            skFitSpline(sketch, "E2594", {"points": [v(-154.91, 29.3) * mm, v(-155.4, 29.58) * mm, v(-156.02, 29.58) * mm, v(-156.51, 29.3) * mm]});
            skFitSpline(sketch, "E2595", {"points": [v(-156.51, 29.3) * mm, v(-157, 29) * mm, v(-157.31, 28.48) * mm, v(-157.31, 27.9) * mm]});
            skFitSpline(sketch, "E2596", {"points": [v(-157.31, 27.9) * mm, v(-157.31, 27.34) * mm, v(-157, 26.8) * mm, v(-156.51, 26.52) * mm]});
            skFitSpline(sketch, "E2597", {"points": [v(-156.51, 26.52) * mm, v(-156.02, 26.24) * mm, v(-155.4, 26.24) * mm, v(-154.91, 26.52) * mm]});
            skFitSpline(sketch, "E2598", {"points": [v(-154.91, 26.52) * mm, v(-154.42, 26.8) * mm, v(-154.11, 27.34) * mm, v(-154.11, 27.9) * mm]});
            skLineSegment(sketch, "E2599", {"start": v(-343.54, 9.54) * mm, "end": v(-343.54, 5.07) * mm});
            skFitSpline(sketch, "E2600", {"points": [v(-154.11, 7.9) * mm, v(-154.11, 8.48) * mm, v(-154.42, 9) * mm, v(-154.91, 9.3) * mm]});
            skFitSpline(sketch, "E2601", {"points": [v(-154.91, 9.3) * mm, v(-155.4, 9.58) * mm, v(-156.02, 9.58) * mm, v(-156.51, 9.3) * mm]});
            skFitSpline(sketch, "E2602", {"points": [v(-156.51, 9.3) * mm, v(-157, 9) * mm, v(-157.31, 8.48) * mm, v(-157.31, 7.9) * mm]});
            skFitSpline(sketch, "E2603", {"points": [v(-157.31, 7.9) * mm, v(-157.31, 7.34) * mm, v(-157, 6.8) * mm, v(-156.51, 6.52) * mm]});
            skFitSpline(sketch, "E2604", {"points": [v(-156.51, 6.52) * mm, v(-156.02, 6.24) * mm, v(-155.4, 6.24) * mm, v(-154.91, 6.52) * mm]});
            skFitSpline(sketch, "E2605", {"points": [v(-154.91, 6.52) * mm, v(-154.42, 6.8) * mm, v(-154.11, 7.34) * mm, v(-154.11, 7.9) * mm]});
            skLineSegment(sketch, "E2606", {"start": v(-342.67, 4.2) * mm, "end": v(-341.1, 4.2) * mm});
            skFitSpline(sketch, "E2607", {"points": [v(-185.11, 27.9) * mm, v(-185.11, 28.48) * mm, v(-185.42, 29) * mm, v(-185.91, 29.3) * mm]});
            skFitSpline(sketch, "E2608", {"points": [v(-185.91, 29.3) * mm, v(-186.4, 29.58) * mm, v(-187.02, 29.58) * mm, v(-187.51, 29.3) * mm]});
            skFitSpline(sketch, "E2609", {"points": [v(-187.51, 29.3) * mm, v(-188, 29) * mm, v(-188.31, 28.48) * mm, v(-188.31, 27.9) * mm]});
            skFitSpline(sketch, "E2610", {"points": [v(-188.31, 27.9) * mm, v(-188.31, 27.34) * mm, v(-188, 26.8) * mm, v(-187.51, 26.52) * mm]});
            skFitSpline(sketch, "E2611", {"points": [v(-187.51, 26.52) * mm, v(-187.02, 26.24) * mm, v(-186.4, 26.24) * mm, v(-185.91, 26.52) * mm]});
            skFitSpline(sketch, "E2612", {"points": [v(-185.91, 26.52) * mm, v(-185.42, 26.8) * mm, v(-185.11, 27.34) * mm, v(-185.11, 27.9) * mm]});
            skFitSpline(sketch, "E2613", {"points": [v(-185.11, 7.9) * mm, v(-185.11, 8.48) * mm, v(-185.42, 9) * mm, v(-185.91, 9.3) * mm]});
            skFitSpline(sketch, "E2614", {"points": [v(-185.91, 9.3) * mm, v(-186.4, 9.58) * mm, v(-187.02, 9.58) * mm, v(-187.51, 9.3) * mm]});
            skFitSpline(sketch, "E2615", {"points": [v(-187.51, 9.3) * mm, v(-188, 9) * mm, v(-188.31, 8.48) * mm, v(-188.31, 7.9) * mm]});
            skFitSpline(sketch, "E2616", {"points": [v(-188.31, 7.9) * mm, v(-188.31, 7.34) * mm, v(-188, 6.8) * mm, v(-187.51, 6.52) * mm]});
            skFitSpline(sketch, "E2617", {"points": [v(-187.51, 6.52) * mm, v(-187.02, 6.24) * mm, v(-186.4, 6.24) * mm, v(-185.91, 6.52) * mm]});
            skFitSpline(sketch, "E2618", {"points": [v(-185.91, 6.52) * mm, v(-185.42, 6.8) * mm, v(-185.11, 7.34) * mm, v(-185.11, 7.9) * mm]});
            skFitSpline(sketch, "E2619", {"points": [v(-213.81, 17.52) * mm, v(-213.81, 18.1) * mm, v(-214.12, 18.62) * mm, v(-214.61, 18.9) * mm]});
            skFitSpline(sketch, "E2620", {"points": [v(-214.61, 18.9) * mm, v(-215.1, 19.2) * mm, v(-215.72, 19.2) * mm, v(-216.21, 18.9) * mm]});
            skFitSpline(sketch, "E2621", {"points": [v(-216.21, 18.9) * mm, v(-216.7, 18.62) * mm, v(-217.01, 18.1) * mm, v(-217.01, 17.52) * mm]});
            skFitSpline(sketch, "E2622", {"points": [v(-217.01, 17.52) * mm, v(-217.01, 16.95) * mm, v(-216.7, 16.42) * mm, v(-216.21, 16.13) * mm]});
            skFitSpline(sketch, "E2623", {"points": [v(-216.21, 16.13) * mm, v(-215.72, 15.85) * mm, v(-215.1, 15.85) * mm, v(-214.61, 16.13) * mm]});
            skFitSpline(sketch, "E2624", {"points": [v(-214.61, 16.13) * mm, v(-214.12, 16.42) * mm, v(-213.81, 16.95) * mm, v(-213.81, 17.52) * mm]});
            skFitSpline(sketch, "E2625", {"points": [v(-226.41, 17.52) * mm, v(-226.41, 18.1) * mm, v(-226.72, 18.62) * mm, v(-227.21, 18.9) * mm]});
            skFitSpline(sketch, "E2626", {"points": [v(-227.21, 18.9) * mm, v(-227.7, 19.2) * mm, v(-228.32, 19.2) * mm, v(-228.81, 18.9) * mm]});
            skFitSpline(sketch, "E2627", {"points": [v(-228.81, 18.9) * mm, v(-229.3, 18.62) * mm, v(-229.61, 18.1) * mm, v(-229.61, 17.52) * mm]});
            skFitSpline(sketch, "E2628", {"points": [v(-229.61, 17.52) * mm, v(-229.61, 16.64) * mm, v(-228.9, 15.92) * mm, v(-228.01, 15.92) * mm]});
            skFitSpline(sketch, "E2629", {"points": [v(-228.01, 15.92) * mm, v(-227.13, 15.92) * mm, v(-226.41, 16.64) * mm, v(-226.41, 17.52) * mm]});
            skFitSpline(sketch, "E2630", {"points": [v(-255.11, 27.9) * mm, v(-255.11, 28.48) * mm, v(-255.42, 29) * mm, v(-255.91, 29.3) * mm]});
            skFitSpline(sketch, "E2631", {"points": [v(-255.91, 29.3) * mm, v(-256.4, 29.58) * mm, v(-257.02, 29.58) * mm, v(-257.51, 29.3) * mm]});
            skFitSpline(sketch, "E2632", {"points": [v(-257.51, 29.3) * mm, v(-258, 29) * mm, v(-258.31, 28.48) * mm, v(-258.31, 27.9) * mm]});
            skFitSpline(sketch, "E2633", {"points": [v(-258.31, 27.9) * mm, v(-258.31, 27.34) * mm, v(-258, 26.8) * mm, v(-257.51, 26.52) * mm]});
            skFitSpline(sketch, "E2634", {"points": [v(-257.51, 26.52) * mm, v(-257.02, 26.24) * mm, v(-256.4, 26.24) * mm, v(-255.91, 26.52) * mm]});
            skFitSpline(sketch, "E2635", {"points": [v(-255.91, 26.52) * mm, v(-255.42, 26.8) * mm, v(-255.11, 27.34) * mm, v(-255.11, 27.9) * mm]});
            skFitSpline(sketch, "E2636", {"points": [v(-255.11, 7.9) * mm, v(-255.11, 8.48) * mm, v(-255.42, 9) * mm, v(-255.91, 9.3) * mm]});
            skFitSpline(sketch, "E2637", {"points": [v(-255.91, 9.3) * mm, v(-256.4, 9.58) * mm, v(-257.02, 9.58) * mm, v(-257.51, 9.3) * mm]});
            skFitSpline(sketch, "E2638", {"points": [v(-257.51, 9.3) * mm, v(-258, 9) * mm, v(-258.31, 8.48) * mm, v(-258.31, 7.9) * mm]});
            skFitSpline(sketch, "E2639", {"points": [v(-258.31, 7.9) * mm, v(-258.31, 7.34) * mm, v(-258, 6.8) * mm, v(-257.51, 6.52) * mm]});
            skFitSpline(sketch, "E2640", {"points": [v(-257.51, 6.52) * mm, v(-257.02, 6.24) * mm, v(-256.4, 6.24) * mm, v(-255.91, 6.52) * mm]});
            skFitSpline(sketch, "E2641", {"points": [v(-255.91, 6.52) * mm, v(-255.42, 6.8) * mm, v(-255.11, 7.34) * mm, v(-255.11, 7.9) * mm]});
            skFitSpline(sketch, "E2642", {"points": [v(-286.11, 27.9) * mm, v(-286.11, 28.48) * mm, v(-286.42, 29) * mm, v(-286.91, 29.3) * mm]});
            skFitSpline(sketch, "E2643", {"points": [v(-286.91, 29.3) * mm, v(-287.4, 29.58) * mm, v(-288.02, 29.58) * mm, v(-288.51, 29.3) * mm]});
            skFitSpline(sketch, "E2644", {"points": [v(-288.51, 29.3) * mm, v(-289, 29) * mm, v(-289.31, 28.48) * mm, v(-289.31, 27.9) * mm]});
            skFitSpline(sketch, "E2645", {"points": [v(-289.31, 27.9) * mm, v(-289.31, 27.34) * mm, v(-289, 26.8) * mm, v(-288.51, 26.52) * mm]});
            skFitSpline(sketch, "E2646", {"points": [v(-288.51, 26.52) * mm, v(-288.02, 26.24) * mm, v(-287.4, 26.24) * mm, v(-286.91, 26.52) * mm]});
            skFitSpline(sketch, "E2647", {"points": [v(-286.91, 26.52) * mm, v(-286.42, 26.8) * mm, v(-286.11, 27.34) * mm, v(-286.11, 27.9) * mm]});
            skFitSpline(sketch, "E2648", {"points": [v(-286.11, 7.9) * mm, v(-286.11, 8.48) * mm, v(-286.42, 9) * mm, v(-286.91, 9.3) * mm]});
            skFitSpline(sketch, "E2649", {"points": [v(-286.91, 9.3) * mm, v(-287.4, 9.58) * mm, v(-288.02, 9.58) * mm, v(-288.51, 9.3) * mm]});
            skFitSpline(sketch, "E2650", {"points": [v(-288.51, 9.3) * mm, v(-289, 9) * mm, v(-289.31, 8.48) * mm, v(-289.31, 7.9) * mm]});
            skFitSpline(sketch, "E2651", {"points": [v(-289.31, 7.9) * mm, v(-289.31, 7.34) * mm, v(-289, 6.8) * mm, v(-288.51, 6.52) * mm]});
            skFitSpline(sketch, "E2652", {"points": [v(-288.51, 6.52) * mm, v(-288.02, 6.24) * mm, v(-287.4, 6.24) * mm, v(-286.91, 6.52) * mm]});
            skFitSpline(sketch, "E2653", {"points": [v(-286.91, 6.52) * mm, v(-286.42, 6.8) * mm, v(-286.11, 7.34) * mm, v(-286.11, 7.9) * mm]});
            skFitSpline(sketch, "E2654", {"points": [v(-340.29, 17.9) * mm, v(-340.29, 18.48) * mm, v(-340.6, 19) * mm, v(-341.09, 19.3) * mm]});
            skFitSpline(sketch, "E2655", {"points": [v(-341.09, 19.3) * mm, v(-341.58, 19.58) * mm, v(-342.2, 19.58) * mm, v(-342.69, 19.3) * mm]});
            skFitSpline(sketch, "E2656", {"points": [v(-342.69, 19.3) * mm, v(-343.18, 19) * mm, v(-343.49, 18.48) * mm, v(-343.49, 17.9) * mm]});
            skFitSpline(sketch, "E2657", {"points": [v(-343.49, 17.9) * mm, v(-343.49, 17.34) * mm, v(-343.18, 16.8) * mm, v(-342.69, 16.52) * mm]});
            skFitSpline(sketch, "E2658", {"points": [v(-342.69, 16.52) * mm, v(-342.2, 16.24) * mm, v(-341.58, 16.24) * mm, v(-341.09, 16.52) * mm]});
            skFitSpline(sketch, "E2659", {"points": [v(-341.09, 16.52) * mm, v(-340.6, 16.8) * mm, v(-340.29, 17.34) * mm, v(-340.29, 17.9) * mm]});
            skFitSpline(sketch, "E2660", {"points": [v(-325.1, 37.22) * mm, v(-324.98, 36.8) * mm, v(-324.59, 36.52) * mm, v(-324.15, 36.52) * mm]});
            skFitSpline(sketch, "E2661", {"points": [v(-326.67, 42.2) * mm, v(-326.8, 42.62) * mm, v(-327.18, 42.9) * mm, v(-327.62, 42.9) * mm]});
            skFitSpline(sketch, "E2662", {"points": [v(-119.27, 36.52) * mm, v(-118.83, 36.52) * mm, v(-118.45, 36.8) * mm, v(-118.32, 37.22) * mm]});
            skFitSpline(sketch, "E2663", {"points": [v(-115.8, 42.9) * mm, v(-116.24, 42.9) * mm, v(-116.63, 42.62) * mm, v(-116.76, 42.2) * mm]});
            skFitSpline(sketch, "E2664", {"points": [v(-140.4, -9.48) * mm, v(-140.2, -9.48) * mm, v(-140.04, -9.38) * mm, v(-139.95, -9.21) * mm]});
            skFitSpline(sketch, "E2665", {"points": [v(-139.95, -9.21) * mm, v(-139.87, -9.05) * mm, v(-139.88, -8.85) * mm, v(-139.98, -8.7) * mm]});
            skFitSpline(sketch, "E2666", {"points": [v(-133.44, -8.7) * mm, v(-133.54, -8.85) * mm, v(-133.55, -9.05) * mm, v(-133.47, -9.21) * mm]});
            skFitSpline(sketch, "E2667", {"points": [v(-133.47, -9.21) * mm, v(-133.38, -9.38) * mm, v(-133.21, -9.48) * mm, v(-133.03, -9.48) * mm]});
            skFitSpline(sketch, "E2668", {"points": [v(-316.71, -7.48) * mm, v(-316.71, -8.58) * mm, v(-315.82, -9.48) * mm, v(-314.71, -9.48) * mm]});
            skFitSpline(sketch, "E2669", {"points": [v(-298.71, -9.48) * mm, v(-297.61, -9.48) * mm, v(-296.71, -8.58) * mm, v(-296.71, -7.48) * mm]});
            skFitSpline(sketch, "E2670", {"points": [v(-310.4, -9.48) * mm, v(-310.21, -9.48) * mm, v(-310.04, -9.38) * mm, v(-309.96, -9.21) * mm]});
            skFitSpline(sketch, "E2671", {"points": [v(-309.96, -9.21) * mm, v(-309.87, -9.05) * mm, v(-309.88, -8.85) * mm, v(-309.98, -8.7) * mm]});
            skFitSpline(sketch, "E2672", {"points": [v(-303.44, -8.7) * mm, v(-303.55, -8.85) * mm, v(-303.56, -9.05) * mm, v(-303.47, -9.21) * mm]});
            skFitSpline(sketch, "E2673", {"points": [v(-303.47, -9.21) * mm, v(-303.39, -9.38) * mm, v(-303.22, -9.48) * mm, v(-303.03, -9.48) * mm]});
            skFitSpline(sketch, "E2674", {"points": [v(-303.44, -8.7) * mm, v(-302.33, -7.05) * mm, v(-302.61, -4.83) * mm, v(-304.1, -3.52) * mm]});
            skFitSpline(sketch, "E2675", {"points": [v(-304.1, -3.52) * mm, v(-305.6, -2.2) * mm, v(-307.83, -2.2) * mm, v(-309.33, -3.52) * mm]});
            skFitSpline(sketch, "E2676", {"points": [v(-309.33, -3.52) * mm, v(-310.82, -4.83) * mm, v(-311.1, -7.05) * mm, v(-309.98, -8.7) * mm]});
            skLineSegment(sketch, "E2677", {"start": v(-314.71, -9.48) * mm, "end": v(-310.4, -9.48) * mm});
            skLineSegment(sketch, "E2678", {"start": v(-303.03, -9.48) * mm, "end": v(-298.71, -9.48) * mm});
            skLineSegment(sketch, "E2679", {"start": v(-296.71, -7.48) * mm, "end": v(-296.71, -1.98) * mm});
            skLineSegment(sketch, "E2680", {"start": v(-316.71, -1.98) * mm, "end": v(-316.71, -7.48) * mm});
            skFitSpline(sketch, "E2681", {"points": [v(-30.13, -63.06) * mm, v(-28.8, -63.06) * mm, v(-27.53, -62.54) * mm, v(-26.6, -61.6) * mm]});
            skFitSpline(sketch, "E2682", {"points": [v(-26.6, -61.6) * mm, v(-25.66, -60.66) * mm, v(-25.13, -59.39) * mm, v(-25.13, -58.06) * mm]});
            skFitSpline(sketch, "E2683", {"points": [v(-85.13, -58.06) * mm, v(-85.13, -60.82) * mm, v(-82.9, -63.06) * mm, v(-80.13, -63.06) * mm]});
            skFitSpline(sketch, "E2684", {"points": [v(-69.16, -3.31) * mm, v(-69.25, -3.16) * mm, v(-69.42, -3.06) * mm, v(-69.6, -3.06) * mm]});
            skFitSpline(sketch, "E2685", {"points": [v(-69.16, -3.31) * mm, v(-69.06, -3.5) * mm, v(-68.85, -3.6) * mm, v(-68.64, -3.56) * mm]});
            skFitSpline(sketch, "E2686", {"points": [v(-68.64, -3.56) * mm, v(-68.44, -3.52) * mm, v(-68.27, -3.36) * mm, v(-68.24, -3.15) * mm]});
            skFitSpline(sketch, "E2687", {"points": [v(-68.24, -3.15) * mm, v(-68.2, -2.94) * mm, v(-68.3, -2.74) * mm, v(-68.48, -2.63) * mm]});
            skFitSpline(sketch, "E2688", {"points": [v(-68.73, -2.2) * mm, v(-68.73, -2.38) * mm, v(-68.63, -2.54) * mm, v(-68.48, -2.63) * mm]});
            skLineSegment(sketch, "E2689", {"start": v(-25.13, -3.06) * mm, "end": v(-25.13, -58.06) * mm});
            skFitSpline(sketch, "E2690", {"points": [v(-68.23, -0.06) * mm, v(-68.36, -0.06) * mm, v(-68.49, -0.12) * mm, v(-68.58, -0.2) * mm]});
            skFitSpline(sketch, "E2691", {"points": [v(-68.58, -0.2) * mm, v(-68.68, -0.3) * mm, v(-68.73, -0.43) * mm, v(-68.73, -0.56) * mm]});
            skLineSegment(sketch, "E2692", {"start": v(-30.13, -63.06) * mm, "end": v(-80.13, -63.06) * mm});
            skFitSpline(sketch, "E2693", {"points": [v(-62.73, -0.56) * mm, v(-62.73, -0.29) * mm, v(-62.95, -0.06) * mm, v(-63.23, -0.06) * mm]});
            skLineSegment(sketch, "E2694", {"start": v(-85.13, -58.06) * mm, "end": v(-85.13, -3.06) * mm});
            skLineSegment(sketch, "E2695", {"start": v(-85.13, -3.06) * mm, "end": v(-69.6, -3.06) * mm});
            skFitSpline(sketch, "E2696", {"points": [v(-62.98, -2.63) * mm, v(-62.83, -2.54) * mm, v(-62.73, -2.38) * mm, v(-62.73, -2.2) * mm]});
            skFitSpline(sketch, "E2697", {"points": [v(-62.98, -2.63) * mm, v(-63.16, -2.74) * mm, v(-63.26, -2.94) * mm, v(-63.22, -3.15) * mm]});
            skFitSpline(sketch, "E2698", {"points": [v(-63.22, -3.15) * mm, v(-63.19, -3.36) * mm, v(-63.02, -3.52) * mm, v(-62.82, -3.56) * mm]});
            skFitSpline(sketch, "E2699", {"points": [v(-62.82, -3.56) * mm, v(-62.6, -3.6) * mm, v(-62.4, -3.5) * mm, v(-62.3, -3.31) * mm]});
            skFitSpline(sketch, "E2700", {"points": [v(-61.86, -3.06) * mm, v(-62.04, -3.06) * mm, v(-62.2, -3.16) * mm, v(-62.3, -3.31) * mm]});
            skLineSegment(sketch, "E2701", {"start": v(-68.73, -2.2) * mm, "end": v(-68.73, -0.56) * mm});
            skFitSpline(sketch, "E2702", {"points": [v(-47.96, -3.31) * mm, v(-48.05, -3.16) * mm, v(-48.22, -3.06) * mm, v(-48.4, -3.06) * mm]});
            skFitSpline(sketch, "E2703", {"points": [v(-47.96, -3.31) * mm, v(-47.86, -3.5) * mm, v(-47.65, -3.6) * mm, v(-47.44, -3.56) * mm]});
            skFitSpline(sketch, "E2704", {"points": [v(-47.44, -3.56) * mm, v(-47.24, -3.52) * mm, v(-47.07, -3.36) * mm, v(-47.04, -3.15) * mm]});
            skFitSpline(sketch, "E2705", {"points": [v(-47.04, -3.15) * mm, v(-47, -2.94) * mm, v(-47.1, -2.74) * mm, v(-47.28, -2.63) * mm]});
            skFitSpline(sketch, "E2706", {"points": [v(-47.53, -2.2) * mm, v(-47.53, -2.38) * mm, v(-47.43, -2.54) * mm, v(-47.28, -2.63) * mm]});
            skLineSegment(sketch, "E2707", {"start": v(-68.23, -0.06) * mm, "end": v(-63.23, -0.06) * mm});
            skFitSpline(sketch, "E2708", {"points": [v(-47.03, -0.06) * mm, v(-47.16, -0.06) * mm, v(-47.29, -0.12) * mm, v(-47.38, -0.2) * mm]});
            skFitSpline(sketch, "E2709", {"points": [v(-47.38, -0.2) * mm, v(-47.48, -0.3) * mm, v(-47.53, -0.43) * mm, v(-47.53, -0.56) * mm]});
            skLineSegment(sketch, "E2710", {"start": v(-62.73, -0.56) * mm, "end": v(-62.73, -2.2) * mm});
            skFitSpline(sketch, "E2711", {"points": [v(-41.53, -0.56) * mm, v(-41.53, -0.43) * mm, v(-41.58, -0.3) * mm, v(-41.68, -0.2) * mm]});
            skFitSpline(sketch, "E2712", {"points": [v(-41.68, -0.2) * mm, v(-41.77, -0.12) * mm, v(-41.9, -0.06) * mm, v(-42.03, -0.06) * mm]});
            skLineSegment(sketch, "E2713", {"start": v(-61.86, -3.06) * mm, "end": v(-56.73, -3.06) * mm});
            skLineSegment(sketch, "E2714", {"start": v(-56.73, -3.06) * mm, "end": v(-56.73, -6.06) * mm});
            skLineSegment(sketch, "E2715", {"start": v(-56.73, -6.06) * mm, "end": v(-58, -6.06) * mm});
            skLineSegment(sketch, "E2716", {"start": v(-58, -6.06) * mm, "end": v(-58, -10.06) * mm});
            skLineSegment(sketch, "E2717", {"start": v(-58, -10.06) * mm, "end": v(-56.73, -10.06) * mm});
            skLineSegment(sketch, "E2718", {"start": v(-56.73, -10.06) * mm, "end": v(-56.73, -13.06) * mm});
            skLineSegment(sketch, "E2719", {"start": v(-56.73, -13.06) * mm, "end": v(-53.53, -13.06) * mm});
            skLineSegment(sketch, "E2720", {"start": v(-53.53, -13.06) * mm, "end": v(-53.53, -10.06) * mm});
            skLineSegment(sketch, "E2721", {"start": v(-53.53, -10.06) * mm, "end": v(-52.26, -10.06) * mm});
            skLineSegment(sketch, "E2722", {"start": v(-52.26, -10.06) * mm, "end": v(-52.26, -6.06) * mm});
            skLineSegment(sketch, "E2723", {"start": v(-52.26, -6.06) * mm, "end": v(-53.53, -6.06) * mm});
            skLineSegment(sketch, "E2724", {"start": v(-53.53, -6.06) * mm, "end": v(-53.53, -3.06) * mm});
            skLineSegment(sketch, "E2725", {"start": v(-53.53, -3.06) * mm, "end": v(-48.4, -3.06) * mm});
            skFitSpline(sketch, "E2726", {"points": [v(-41.78, -2.63) * mm, v(-41.63, -2.54) * mm, v(-41.53, -2.38) * mm, v(-41.53, -2.2) * mm]});
            skFitSpline(sketch, "E2727", {"points": [v(-41.78, -2.63) * mm, v(-41.96, -2.74) * mm, v(-42.06, -2.94) * mm, v(-42.02, -3.15) * mm]});
            skFitSpline(sketch, "E2728", {"points": [v(-42.02, -3.15) * mm, v(-41.99, -3.36) * mm, v(-41.82, -3.52) * mm, v(-41.62, -3.56) * mm]});
            skFitSpline(sketch, "E2729", {"points": [v(-41.62, -3.56) * mm, v(-41.4, -3.6) * mm, v(-41.2, -3.5) * mm, v(-41.1, -3.31) * mm]});
            skFitSpline(sketch, "E2730", {"points": [v(-40.66, -3.06) * mm, v(-40.84, -3.06) * mm, v(-41, -3.16) * mm, v(-41.1, -3.31) * mm]});
            skLineSegment(sketch, "E2731", {"start": v(-47.53, -2.2) * mm, "end": v(-47.53, -0.56) * mm});
            skFitSpline(sketch, "E2732", {"points": [v(-44.03, -42.36) * mm, v(-44.03, -38.4) * mm, v(-46.14, -34.73) * mm, v(-49.58, -32.74) * mm]});
            skFitSpline(sketch, "E2733", {"points": [v(-49.58, -32.74) * mm, v(-53.01, -30.76) * mm, v(-57.25, -30.76) * mm, v(-60.68, -32.74) * mm]});
            skFitSpline(sketch, "E2734", {"points": [v(-60.68, -32.74) * mm, v(-64.12, -34.73) * mm, v(-66.23, -38.4) * mm, v(-66.23, -42.36) * mm]});
            skFitSpline(sketch, "E2735", {"points": [v(-66.23, -42.36) * mm, v(-66.23, -46.33) * mm, v(-64.12, -50) * mm, v(-60.68, -51.98) * mm]});
            skFitSpline(sketch, "E2736", {"points": [v(-60.68, -51.98) * mm, v(-57.25, -53.97) * mm, v(-53.01, -53.97) * mm, v(-49.58, -51.98) * mm]});
            skFitSpline(sketch, "E2737", {"points": [v(-49.58, -51.98) * mm, v(-46.14, -50) * mm, v(-44.03, -46.33) * mm, v(-44.03, -42.36) * mm]});
            skLineSegment(sketch, "E2738", {"start": v(-47.03, -0.06) * mm, "end": v(-42.03, -0.06) * mm});
            skFitSpline(sketch, "E2739", {"points": [v(-34.13, -42.36) * mm, v(-34.13, -40.93) * mm, v(-34.89, -39.6) * mm, v(-36.13, -38.9) * mm]});
            skFitSpline(sketch, "E2740", {"points": [v(-36.13, -38.9) * mm, v(-37.37, -38.18) * mm, v(-38.9, -38.18) * mm, v(-40.13, -38.9) * mm]});
            skFitSpline(sketch, "E2741", {"points": [v(-40.13, -38.9) * mm, v(-41.37, -39.6) * mm, v(-42.13, -40.93) * mm, v(-42.13, -42.36) * mm]});
            skFitSpline(sketch, "E2742", {"points": [v(-42.13, -42.36) * mm, v(-42.13, -43.8) * mm, v(-41.37, -45.12) * mm, v(-40.13, -45.83) * mm]});
            skFitSpline(sketch, "E2743", {"points": [v(-40.13, -45.83) * mm, v(-38.9, -46.55) * mm, v(-37.37, -46.55) * mm, v(-36.13, -45.83) * mm]});
            skFitSpline(sketch, "E2744", {"points": [v(-36.13, -45.83) * mm, v(-34.89, -45.12) * mm, v(-34.13, -43.8) * mm, v(-34.13, -42.36) * mm]});
            skLineSegment(sketch, "E2745", {"start": v(-41.53, -0.56) * mm, "end": v(-41.53, -2.2) * mm});
            skFitSpline(sketch, "E2746", {"points": [v(-31.4, -30.56) * mm, v(-31.57, -30.56) * mm, v(-31.74, -30.66) * mm, v(-31.83, -30.81) * mm]});
            skFitSpline(sketch, "E2747", {"points": [v(-32.51, -30.13) * mm, v(-32.7, -30.24) * mm, v(-32.79, -30.44) * mm, v(-32.75, -30.65) * mm]});
            skFitSpline(sketch, "E2748", {"points": [v(-32.75, -30.65) * mm, v(-32.72, -30.86) * mm, v(-32.55, -31.02) * mm, v(-32.35, -31.06) * mm]});
            skFitSpline(sketch, "E2749", {"points": [v(-32.35, -31.06) * mm, v(-32.14, -31.1) * mm, v(-31.93, -31) * mm, v(-31.83, -30.81) * mm]});
            skFitSpline(sketch, "E2750", {"points": [v(-32.51, -30.13) * mm, v(-32.36, -30.04) * mm, v(-32.26, -29.88) * mm, v(-32.26, -29.7) * mm]});
            skLineSegment(sketch, "E2751", {"start": v(-40.66, -3.06) * mm, "end": v(-25.13, -3.06) * mm});
            skFitSpline(sketch, "E2752", {"points": [v(-32.26, -25.23) * mm, v(-32.26, -25.05) * mm, v(-32.36, -24.89) * mm, v(-32.51, -24.8) * mm]});
            skFitSpline(sketch, "E2753", {"points": [v(-31.83, -24.11) * mm, v(-31.93, -23.93) * mm, v(-32.14, -23.83) * mm, v(-32.35, -23.87) * mm]});
            skFitSpline(sketch, "E2754", {"points": [v(-32.35, -23.87) * mm, v(-32.55, -23.9) * mm, v(-32.72, -24.07) * mm, v(-32.75, -24.28) * mm]});
            skFitSpline(sketch, "E2755", {"points": [v(-32.75, -24.28) * mm, v(-32.79, -24.48) * mm, v(-32.7, -24.7) * mm, v(-32.51, -24.8) * mm]});
            skFitSpline(sketch, "E2756", {"points": [v(-31.83, -24.11) * mm, v(-31.74, -24.27) * mm, v(-31.57, -24.36) * mm, v(-31.4, -24.36) * mm]});
            skFitSpline(sketch, "E2757", {"points": [v(-29.83, -24.36) * mm, v(-29.65, -24.36) * mm, v(-29.48, -24.27) * mm, v(-29.4, -24.11) * mm]});
            skFitSpline(sketch, "E2758", {"points": [v(-28.71, -24.8) * mm, v(-28.53, -24.7) * mm, v(-28.43, -24.48) * mm, v(-28.47, -24.28) * mm]});
            skFitSpline(sketch, "E2759", {"points": [v(-28.47, -24.28) * mm, v(-28.5, -24.07) * mm, v(-28.67, -23.9) * mm, v(-28.87, -23.87) * mm]});
            skFitSpline(sketch, "E2760", {"points": [v(-28.87, -23.87) * mm, v(-29.08, -23.83) * mm, v(-29.29, -23.93) * mm, v(-29.4, -24.11) * mm]});
            skFitSpline(sketch, "E2761", {"points": [v(-28.71, -24.8) * mm, v(-28.86, -24.89) * mm, v(-28.96, -25.05) * mm, v(-28.96, -25.23) * mm]});
            skFitSpline(sketch, "E2762", {"points": [v(-28.96, -29.7) * mm, v(-28.96, -29.88) * mm, v(-28.86, -30.04) * mm, v(-28.71, -30.13) * mm]});
            skFitSpline(sketch, "E2763", {"points": [v(-29.4, -30.81) * mm, v(-29.29, -31) * mm, v(-29.08, -31.1) * mm, v(-28.87, -31.06) * mm]});
            skFitSpline(sketch, "E2764", {"points": [v(-28.87, -31.06) * mm, v(-28.67, -31.02) * mm, v(-28.5, -30.86) * mm, v(-28.47, -30.65) * mm]});
            skFitSpline(sketch, "E2765", {"points": [v(-28.47, -30.65) * mm, v(-28.43, -30.44) * mm, v(-28.53, -30.24) * mm, v(-28.71, -30.13) * mm]});
            skFitSpline(sketch, "E2766", {"points": [v(-29.4, -30.81) * mm, v(-29.48, -30.66) * mm, v(-29.65, -30.56) * mm, v(-29.83, -30.56) * mm]});
            skLineSegment(sketch, "E2767", {"start": v(-32.26, -29.7) * mm, "end": v(-32.26, -25.23) * mm});
            skFitSpline(sketch, "E2768", {"points": [v(-31.4, -51.76) * mm, v(-31.57, -51.76) * mm, v(-31.74, -51.86) * mm, v(-31.83, -52.01) * mm]});
            skFitSpline(sketch, "E2769", {"points": [v(-32.51, -51.33) * mm, v(-32.7, -51.44) * mm, v(-32.79, -51.64) * mm, v(-32.75, -51.85) * mm]});
            skFitSpline(sketch, "E2770", {"points": [v(-32.75, -51.85) * mm, v(-32.72, -52.06) * mm, v(-32.55, -52.22) * mm, v(-32.35, -52.26) * mm]});
            skFitSpline(sketch, "E2771", {"points": [v(-32.35, -52.26) * mm, v(-32.14, -52.3) * mm, v(-31.93, -52.2) * mm, v(-31.83, -52.01) * mm]});
            skFitSpline(sketch, "E2772", {"points": [v(-32.51, -51.33) * mm, v(-32.36, -51.24) * mm, v(-32.26, -51.08) * mm, v(-32.26, -50.9) * mm]});
            skLineSegment(sketch, "E2773", {"start": v(-31.4, -24.36) * mm, "end": v(-29.83, -24.36) * mm});
            skFitSpline(sketch, "E2774", {"points": [v(-32.26, -46.43) * mm, v(-32.26, -46.25) * mm, v(-32.36, -46.09) * mm, v(-32.51, -46) * mm]});
            skFitSpline(sketch, "E2775", {"points": [v(-31.83, -45.31) * mm, v(-31.93, -45.13) * mm, v(-32.14, -45.03) * mm, v(-32.35, -45.07) * mm]});
            skFitSpline(sketch, "E2776", {"points": [v(-32.35, -45.07) * mm, v(-32.55, -45.1) * mm, v(-32.72, -45.27) * mm, v(-32.75, -45.48) * mm]});
            skFitSpline(sketch, "E2777", {"points": [v(-32.75, -45.48) * mm, v(-32.79, -45.68) * mm, v(-32.7, -45.9) * mm, v(-32.51, -46) * mm]});
            skFitSpline(sketch, "E2778", {"points": [v(-31.83, -45.31) * mm, v(-31.74, -45.47) * mm, v(-31.57, -45.56) * mm, v(-31.4, -45.56) * mm]});
            skLineSegment(sketch, "E2779", {"start": v(-28.96, -25.23) * mm, "end": v(-28.96, -29.7) * mm});
            skFitSpline(sketch, "E2780", {"points": [v(-29.83, -45.56) * mm, v(-29.65, -45.56) * mm, v(-29.48, -45.47) * mm, v(-29.4, -45.31) * mm]});
            skFitSpline(sketch, "E2781", {"points": [v(-28.71, -46) * mm, v(-28.53, -45.9) * mm, v(-28.43, -45.68) * mm, v(-28.47, -45.48) * mm]});
            skFitSpline(sketch, "E2782", {"points": [v(-28.47, -45.48) * mm, v(-28.5, -45.27) * mm, v(-28.67, -45.1) * mm, v(-28.87, -45.07) * mm]});
            skFitSpline(sketch, "E2783", {"points": [v(-28.87, -45.07) * mm, v(-29.08, -45.03) * mm, v(-29.29, -45.13) * mm, v(-29.4, -45.31) * mm]});
            skFitSpline(sketch, "E2784", {"points": [v(-28.71, -46) * mm, v(-28.86, -46.09) * mm, v(-28.96, -46.25) * mm, v(-28.96, -46.43) * mm]});
            skLineSegment(sketch, "E2785", {"start": v(-29.83, -30.56) * mm, "end": v(-31.4, -30.56) * mm});
            skFitSpline(sketch, "E2786", {"points": [v(-28.96, -50.9) * mm, v(-28.96, -51.08) * mm, v(-28.86, -51.24) * mm, v(-28.71, -51.33) * mm]});
            skFitSpline(sketch, "E2787", {"points": [v(-29.4, -52.01) * mm, v(-29.29, -52.2) * mm, v(-29.08, -52.3) * mm, v(-28.87, -52.26) * mm]});
            skFitSpline(sketch, "E2788", {"points": [v(-28.87, -52.26) * mm, v(-28.67, -52.22) * mm, v(-28.5, -52.06) * mm, v(-28.47, -51.85) * mm]});
            skFitSpline(sketch, "E2789", {"points": [v(-28.47, -51.85) * mm, v(-28.43, -51.64) * mm, v(-28.53, -51.44) * mm, v(-28.71, -51.33) * mm]});
            skFitSpline(sketch, "E2790", {"points": [v(-29.4, -52.01) * mm, v(-29.48, -51.86) * mm, v(-29.65, -51.76) * mm, v(-29.83, -51.76) * mm]});
            skLineSegment(sketch, "E2791", {"start": v(-32.26, -50.9) * mm, "end": v(-32.26, -46.43) * mm});
            skFitSpline(sketch, "E2792", {"points": [v(-80.43, -30.56) * mm, v(-80.61, -30.56) * mm, v(-80.78, -30.66) * mm, v(-80.87, -30.81) * mm]});
            skFitSpline(sketch, "E2793", {"points": [v(-81.55, -30.13) * mm, v(-81.73, -30.24) * mm, v(-81.83, -30.44) * mm, v(-81.8, -30.65) * mm]});
            skFitSpline(sketch, "E2794", {"points": [v(-81.8, -30.65) * mm, v(-81.76, -30.86) * mm, v(-81.6, -31.02) * mm, v(-81.39, -31.06) * mm]});
            skFitSpline(sketch, "E2795", {"points": [v(-81.39, -31.06) * mm, v(-81.18, -31.1) * mm, v(-80.97, -31) * mm, v(-80.87, -30.81) * mm]});
            skFitSpline(sketch, "E2796", {"points": [v(-81.55, -30.13) * mm, v(-81.4, -30.04) * mm, v(-81.3, -29.88) * mm, v(-81.3, -29.7) * mm]});
            skLineSegment(sketch, "E2797", {"start": v(-31.4, -45.56) * mm, "end": v(-29.83, -45.56) * mm});
            skFitSpline(sketch, "E2798", {"points": [v(-81.3, -25.23) * mm, v(-81.3, -25.05) * mm, v(-81.4, -24.89) * mm, v(-81.55, -24.8) * mm]});
            skFitSpline(sketch, "E2799", {"points": [v(-80.87, -24.11) * mm, v(-80.97, -23.93) * mm, v(-81.18, -23.83) * mm, v(-81.39, -23.87) * mm]});
            skFitSpline(sketch, "E2800", {"points": [v(-81.39, -23.87) * mm, v(-81.6, -23.9) * mm, v(-81.76, -24.07) * mm, v(-81.8, -24.28) * mm]});
            skFitSpline(sketch, "E2801", {"points": [v(-81.8, -24.28) * mm, v(-81.83, -24.48) * mm, v(-81.73, -24.7) * mm, v(-81.55, -24.8) * mm]});
            skFitSpline(sketch, "E2802", {"points": [v(-80.87, -24.11) * mm, v(-80.78, -24.27) * mm, v(-80.61, -24.36) * mm, v(-80.43, -24.36) * mm]});
            skLineSegment(sketch, "E2803", {"start": v(-28.96, -46.43) * mm, "end": v(-28.96, -50.9) * mm});
            skFitSpline(sketch, "E2804", {"points": [v(-78.87, -24.36) * mm, v(-78.69, -24.36) * mm, v(-78.52, -24.27) * mm, v(-78.43, -24.11) * mm]});
            skFitSpline(sketch, "E2805", {"points": [v(-77.75, -24.8) * mm, v(-77.57, -24.7) * mm, v(-77.47, -24.48) * mm, v(-77.5, -24.28) * mm]});
            skFitSpline(sketch, "E2806", {"points": [v(-77.5, -24.28) * mm, v(-77.54, -24.07) * mm, v(-77.7, -23.9) * mm, v(-77.91, -23.87) * mm]});
            skFitSpline(sketch, "E2807", {"points": [v(-77.91, -23.87) * mm, v(-78.12, -23.83) * mm, v(-78.33, -23.93) * mm, v(-78.43, -24.11) * mm]});
            skFitSpline(sketch, "E2808", {"points": [v(-77.75, -24.8) * mm, v(-77.9, -24.89) * mm, v(-78, -25.05) * mm, v(-78, -25.23) * mm]});
            skLineSegment(sketch, "E2809", {"start": v(-29.83, -51.76) * mm, "end": v(-31.4, -51.76) * mm});
            skFitSpline(sketch, "E2810", {"points": [v(-78, -29.7) * mm, v(-78, -29.88) * mm, v(-77.9, -30.04) * mm, v(-77.75, -30.13) * mm]});
            skFitSpline(sketch, "E2811", {"points": [v(-78.43, -30.81) * mm, v(-78.33, -31) * mm, v(-78.12, -31.1) * mm, v(-77.91, -31.06) * mm]});
            skFitSpline(sketch, "E2812", {"points": [v(-77.91, -31.06) * mm, v(-77.7, -31.02) * mm, v(-77.54, -30.86) * mm, v(-77.5, -30.65) * mm]});
            skFitSpline(sketch, "E2813", {"points": [v(-77.5, -30.65) * mm, v(-77.47, -30.44) * mm, v(-77.57, -30.24) * mm, v(-77.75, -30.13) * mm]});
            skFitSpline(sketch, "E2814", {"points": [v(-78.43, -30.81) * mm, v(-78.52, -30.66) * mm, v(-78.69, -30.56) * mm, v(-78.87, -30.56) * mm]});
            skLineSegment(sketch, "E2815", {"start": v(-81.3, -29.7) * mm, "end": v(-81.3, -25.23) * mm});
            skFitSpline(sketch, "E2816", {"points": [v(-80.43, -51.76) * mm, v(-80.61, -51.76) * mm, v(-80.78, -51.86) * mm, v(-80.87, -52.01) * mm]});
            skFitSpline(sketch, "E2817", {"points": [v(-81.55, -51.33) * mm, v(-81.73, -51.44) * mm, v(-81.83, -51.64) * mm, v(-81.8, -51.85) * mm]});
            skFitSpline(sketch, "E2818", {"points": [v(-81.8, -51.85) * mm, v(-81.76, -52.06) * mm, v(-81.6, -52.22) * mm, v(-81.39, -52.26) * mm]});
            skFitSpline(sketch, "E2819", {"points": [v(-81.39, -52.26) * mm, v(-81.18, -52.3) * mm, v(-80.97, -52.2) * mm, v(-80.87, -52.01) * mm]});
            skFitSpline(sketch, "E2820", {"points": [v(-81.55, -51.33) * mm, v(-81.4, -51.24) * mm, v(-81.3, -51.08) * mm, v(-81.3, -50.9) * mm]});
            skLineSegment(sketch, "E2821", {"start": v(-80.43, -24.36) * mm, "end": v(-78.87, -24.36) * mm});
            skFitSpline(sketch, "E2822", {"points": [v(-81.3, -46.43) * mm, v(-81.3, -46.25) * mm, v(-81.4, -46.09) * mm, v(-81.55, -46) * mm]});
            skFitSpline(sketch, "E2823", {"points": [v(-80.87, -45.31) * mm, v(-80.97, -45.13) * mm, v(-81.18, -45.03) * mm, v(-81.39, -45.07) * mm]});
            skFitSpline(sketch, "E2824", {"points": [v(-81.39, -45.07) * mm, v(-81.6, -45.1) * mm, v(-81.76, -45.27) * mm, v(-81.8, -45.48) * mm]});
            skFitSpline(sketch, "E2825", {"points": [v(-81.8, -45.48) * mm, v(-81.83, -45.68) * mm, v(-81.73, -45.9) * mm, v(-81.55, -46) * mm]});
            skFitSpline(sketch, "E2826", {"points": [v(-80.87, -45.31) * mm, v(-80.78, -45.47) * mm, v(-80.61, -45.56) * mm, v(-80.43, -45.56) * mm]});
            skLineSegment(sketch, "E2827", {"start": v(-78, -25.23) * mm, "end": v(-78, -29.7) * mm});
            skFitSpline(sketch, "E2828", {"points": [v(-78.87, -45.56) * mm, v(-78.69, -45.56) * mm, v(-78.52, -45.47) * mm, v(-78.43, -45.31) * mm]});
            skFitSpline(sketch, "E2829", {"points": [v(-77.75, -46) * mm, v(-77.57, -45.9) * mm, v(-77.47, -45.68) * mm, v(-77.5, -45.48) * mm]});
            skFitSpline(sketch, "E2830", {"points": [v(-77.5, -45.48) * mm, v(-77.54, -45.27) * mm, v(-77.7, -45.1) * mm, v(-77.91, -45.07) * mm]});
            skFitSpline(sketch, "E2831", {"points": [v(-77.91, -45.07) * mm, v(-78.12, -45.03) * mm, v(-78.33, -45.13) * mm, v(-78.43, -45.31) * mm]});
            skFitSpline(sketch, "E2832", {"points": [v(-77.75, -46) * mm, v(-77.9, -46.09) * mm, v(-78, -46.25) * mm, v(-78, -46.43) * mm]});
            skLineSegment(sketch, "E2833", {"start": v(-78.87, -30.56) * mm, "end": v(-80.43, -30.56) * mm});
            skFitSpline(sketch, "E2834", {"points": [v(-78, -50.9) * mm, v(-78, -51.08) * mm, v(-77.9, -51.24) * mm, v(-77.75, -51.33) * mm]});
            skFitSpline(sketch, "E2835", {"points": [v(-78.43, -52.01) * mm, v(-78.33, -52.2) * mm, v(-78.12, -52.3) * mm, v(-77.91, -52.26) * mm]});
            skFitSpline(sketch, "E2836", {"points": [v(-77.91, -52.26) * mm, v(-77.7, -52.22) * mm, v(-77.54, -52.06) * mm, v(-77.5, -51.85) * mm]});
            skFitSpline(sketch, "E2837", {"points": [v(-77.5, -51.85) * mm, v(-77.47, -51.64) * mm, v(-77.57, -51.44) * mm, v(-77.75, -51.33) * mm]});
            skFitSpline(sketch, "E2838", {"points": [v(-78.43, -52.01) * mm, v(-78.52, -51.86) * mm, v(-78.69, -51.76) * mm, v(-78.87, -51.76) * mm]});
            skLineSegment(sketch, "E2839", {"start": v(-81.3, -50.9) * mm, "end": v(-81.3, -46.43) * mm});
            skFitSpline(sketch, "E2840", {"points": [v(-29.01, -38.06) * mm, v(-29, -37.5) * mm, v(-29.31, -36.96) * mm, v(-29.8, -36.67) * mm]});
            skFitSpline(sketch, "E2841", {"points": [v(-29.8, -36.67) * mm, v(-30.3, -36.39) * mm, v(-30.92, -36.39) * mm, v(-31.41, -36.67) * mm]});
            skFitSpline(sketch, "E2842", {"points": [v(-31.41, -36.67) * mm, v(-31.9, -36.96) * mm, v(-32.21, -37.5) * mm, v(-32.21, -38.06) * mm]});
            skFitSpline(sketch, "E2843", {"points": [v(-32.21, -38.06) * mm, v(-32.21, -38.64) * mm, v(-31.9, -39.17) * mm, v(-31.41, -39.45) * mm]});
            skFitSpline(sketch, "E2844", {"points": [v(-31.41, -39.45) * mm, v(-30.92, -39.74) * mm, v(-30.3, -39.74) * mm, v(-29.8, -39.45) * mm]});
            skFitSpline(sketch, "E2845", {"points": [v(-29.8, -39.45) * mm, v(-29.31, -39.17) * mm, v(-29, -38.64) * mm, v(-29.01, -38.06) * mm]});
            skLineSegment(sketch, "E2846", {"start": v(-80.43, -45.56) * mm, "end": v(-78.87, -45.56) * mm});
            skFitSpline(sketch, "E2847", {"points": [v(-38.03, -26.86) * mm, v(-38.03, -26.3) * mm, v(-38.34, -25.76) * mm, v(-38.83, -25.48) * mm]});
            skFitSpline(sketch, "E2848", {"points": [v(-38.83, -25.48) * mm, v(-39.33, -25.2) * mm, v(-39.94, -25.2) * mm, v(-40.43, -25.48) * mm]});
            skFitSpline(sketch, "E2849", {"points": [v(-40.43, -25.48) * mm, v(-40.93, -25.76) * mm, v(-41.23, -26.3) * mm, v(-41.23, -26.86) * mm]});
            skFitSpline(sketch, "E2850", {"points": [v(-41.23, -26.86) * mm, v(-41.23, -27.75) * mm, v(-40.51, -28.46) * mm, v(-39.63, -28.46) * mm]});
            skFitSpline(sketch, "E2851", {"points": [v(-39.63, -28.46) * mm, v(-38.75, -28.46) * mm, v(-38.03, -27.75) * mm, v(-38.03, -26.86) * mm]});
            skLineSegment(sketch, "E2852", {"start": v(-78, -46.43) * mm, "end": v(-78, -50.9) * mm});
            skFitSpline(sketch, "E2853", {"points": [v(-38.03, -57.86) * mm, v(-38.03, -57.3) * mm, v(-38.34, -56.76) * mm, v(-38.83, -56.48) * mm]});
            skFitSpline(sketch, "E2854", {"points": [v(-38.83, -56.48) * mm, v(-39.33, -56.2) * mm, v(-39.94, -56.2) * mm, v(-40.43, -56.48) * mm]});
            skFitSpline(sketch, "E2855", {"points": [v(-40.43, -56.48) * mm, v(-40.93, -56.76) * mm, v(-41.23, -57.3) * mm, v(-41.23, -57.86) * mm]});
            skFitSpline(sketch, "E2856", {"points": [v(-41.23, -57.86) * mm, v(-41.23, -58.75) * mm, v(-40.51, -59.46) * mm, v(-39.63, -59.46) * mm]});
            skFitSpline(sketch, "E2857", {"points": [v(-39.63, -59.46) * mm, v(-38.75, -59.46) * mm, v(-38.03, -58.75) * mm, v(-38.03, -57.86) * mm]});
            skLineSegment(sketch, "E2858", {"start": v(-78.87, -51.76) * mm, "end": v(-80.43, -51.76) * mm});
            skFitSpline(sketch, "E2859", {"points": [v(-69.03, -26.86) * mm, v(-69.03, -26.3) * mm, v(-69.34, -25.76) * mm, v(-69.83, -25.48) * mm]});
            skFitSpline(sketch, "E2860", {"points": [v(-69.83, -25.48) * mm, v(-70.33, -25.2) * mm, v(-70.94, -25.2) * mm, v(-71.43, -25.48) * mm]});
            skFitSpline(sketch, "E2861", {"points": [v(-71.43, -25.48) * mm, v(-71.93, -25.76) * mm, v(-72.23, -26.3) * mm, v(-72.23, -26.86) * mm]});
            skFitSpline(sketch, "E2862", {"points": [v(-72.23, -26.86) * mm, v(-72.23, -27.75) * mm, v(-71.51, -28.46) * mm, v(-70.63, -28.46) * mm]});
            skFitSpline(sketch, "E2863", {"points": [v(-70.63, -28.46) * mm, v(-69.75, -28.46) * mm, v(-69.03, -27.75) * mm, v(-69.03, -26.86) * mm]});
            skFitSpline(sketch, "E2864", {"points": [v(-69.03, -57.86) * mm, v(-69.03, -57.3) * mm, v(-69.34, -56.76) * mm, v(-69.83, -56.48) * mm]});
            skFitSpline(sketch, "E2865", {"points": [v(-69.83, -56.48) * mm, v(-70.33, -56.2) * mm, v(-70.94, -56.2) * mm, v(-71.43, -56.48) * mm]});
            skFitSpline(sketch, "E2866", {"points": [v(-71.43, -56.48) * mm, v(-71.93, -56.76) * mm, v(-72.23, -57.3) * mm, v(-72.23, -57.86) * mm]});
            skFitSpline(sketch, "E2867", {"points": [v(-72.23, -57.86) * mm, v(-72.23, -58.75) * mm, v(-71.51, -59.46) * mm, v(-70.63, -59.46) * mm]});
            skFitSpline(sketch, "E2868", {"points": [v(-70.63, -59.46) * mm, v(-69.75, -59.46) * mm, v(-69.03, -58.75) * mm, v(-69.03, -57.86) * mm]});
            skFitSpline(sketch, "E2869", {"points": [v(-78.05, -38.06) * mm, v(-78.05, -37.5) * mm, v(-78.36, -36.96) * mm, v(-78.85, -36.68) * mm]});
            skFitSpline(sketch, "E2870", {"points": [v(-78.85, -36.68) * mm, v(-79.35, -36.4) * mm, v(-79.96, -36.4) * mm, v(-80.45, -36.68) * mm]});
            skFitSpline(sketch, "E2871", {"points": [v(-80.45, -36.68) * mm, v(-80.95, -36.96) * mm, v(-81.25, -37.5) * mm, v(-81.25, -38.06) * mm]});
            skFitSpline(sketch, "E2872", {"points": [v(-81.25, -38.06) * mm, v(-81.25, -38.95) * mm, v(-80.53, -39.66) * mm, v(-79.65, -39.66) * mm]});
            skFitSpline(sketch, "E2873", {"points": [v(-79.65, -39.66) * mm, v(-78.77, -39.66) * mm, v(-78.05, -38.95) * mm, v(-78.05, -38.06) * mm]});
            skFitSpline(sketch, "E2874", {"points": [v(-335.74, 163.5) * mm, v(-340.82, 161.99) * mm, v(-344.3, 157.31) * mm, v(-344.3, 152) * mm]});
            skFitSpline(sketch, "E2875", {"points": [v(-335.17, 148.77) * mm, v(-335, 148.77) * mm, v(-334.83, 148.87) * mm, v(-334.74, 149.02) * mm]});
            skFitSpline(sketch, "E2876", {"points": [v(-334.05, 148.34) * mm, v(-333.87, 148.44) * mm, v(-333.78, 148.65) * mm, v(-333.81, 148.86) * mm]});
            skFitSpline(sketch, "E2877", {"points": [v(-333.81, 148.86) * mm, v(-333.85, 149.06) * mm, v(-334.01, 149.23) * mm, v(-334.22, 149.26) * mm]});
            skFitSpline(sketch, "E2878", {"points": [v(-334.22, 149.26) * mm, v(-334.42, 149.3) * mm, v(-334.63, 149.2) * mm, v(-334.74, 149.02) * mm]});
            skFitSpline(sketch, "E2879", {"points": [v(-334.05, 148.34) * mm, v(-334.2, 148.25) * mm, v(-334.3, 148.08) * mm, v(-334.3, 147.9) * mm]});
            skFitSpline(sketch, "E2880", {"points": [v(-334.3, 146.34) * mm, v(-334.3, 146.16) * mm, v(-334.2, 146) * mm, v(-334.05, 145.9) * mm]});
            skFitSpline(sketch, "E2881", {"points": [v(-334.74, 145.22) * mm, v(-334.63, 145.04) * mm, v(-334.43, 144.94) * mm, v(-334.22, 144.98) * mm]});
            skFitSpline(sketch, "E2882", {"points": [v(-334.22, 144.98) * mm, v(-334.01, 145.02) * mm, v(-333.85, 145.18) * mm, v(-333.81, 145.38) * mm]});
            skFitSpline(sketch, "E2883", {"points": [v(-333.81, 145.38) * mm, v(-333.78, 145.6) * mm, v(-333.87, 145.8) * mm, v(-334.05, 145.9) * mm]});
            skFitSpline(sketch, "E2884", {"points": [v(-334.74, 145.22) * mm, v(-334.83, 145.38) * mm, v(-335, 145.47) * mm, v(-335.17, 145.47) * mm]});
            skFitSpline(sketch, "E2885", {"points": [v(-344.3, 114.95) * mm, v(-344.3, 108.32) * mm, v(-338.93, 102.95) * mm, v(-332.3, 102.95) * mm]});
            skLineSegment(sketch, "E2886", {"start": v(-344.3, 152) * mm, "end": v(-344.3, 148.77) * mm});
            skLineSegment(sketch, "E2887", {"start": v(-344.3, 148.77) * mm, "end": v(-335.17, 148.77) * mm});
            skFitSpline(sketch, "E2888", {"points": [v(-310.7, 102.95) * mm, v(-306.16, 102.95) * mm, v(-302.02, 105.5) * mm, v(-299.98, 109.55) * mm]});
            skFitSpline(sketch, "E2889", {"points": [v(-309.6, 116.32) * mm, v(-309.6, 118.1) * mm, v(-310.56, 119.75) * mm, v(-312.1, 120.65) * mm]});
            skFitSpline(sketch, "E2890", {"points": [v(-312.1, 120.65) * mm, v(-313.65, 121.54) * mm, v(-315.56, 121.54) * mm, v(-317.1, 120.65) * mm]});
            skFitSpline(sketch, "E2891", {"points": [v(-317.1, 120.65) * mm, v(-318.65, 119.75) * mm, v(-319.6, 118.1) * mm, v(-319.6, 116.32) * mm]});
            skFitSpline(sketch, "E2892", {"points": [v(-319.6, 116.32) * mm, v(-319.6, 114.53) * mm, v(-318.65, 112.88) * mm, v(-317.1, 111.99) * mm]});
            skFitSpline(sketch, "E2893", {"points": [v(-317.1, 111.99) * mm, v(-315.56, 111.1) * mm, v(-313.65, 111.1) * mm, v(-312.1, 111.99) * mm]});
            skFitSpline(sketch, "E2894", {"points": [v(-312.1, 111.99) * mm, v(-310.56, 112.88) * mm, v(-309.6, 114.53) * mm, v(-309.6, 116.32) * mm]});
            skLineSegment(sketch, "E2895", {"start": v(-334.3, 147.9) * mm, "end": v(-334.3, 146.34) * mm});
            skFitSpline(sketch, "E2896", {"points": [v(-327.6, 116.32) * mm, v(-327.6, 117.75) * mm, v(-328.37, 119.07) * mm, v(-329.6, 119.78) * mm]});
            skFitSpline(sketch, "E2897", {"points": [v(-329.6, 119.78) * mm, v(-330.84, 120.5) * mm, v(-332.37, 120.5) * mm, v(-333.6, 119.78) * mm]});
            skFitSpline(sketch, "E2898", {"points": [v(-333.6, 119.78) * mm, v(-334.84, 119.07) * mm, v(-335.6, 117.75) * mm, v(-335.6, 116.32) * mm]});
            skFitSpline(sketch, "E2899", {"points": [v(-335.6, 116.32) * mm, v(-335.6, 114.9) * mm, v(-334.84, 113.57) * mm, v(-333.6, 112.86) * mm]});
            skFitSpline(sketch, "E2900", {"points": [v(-333.6, 112.86) * mm, v(-332.37, 112.14) * mm, v(-330.84, 112.14) * mm, v(-329.6, 112.86) * mm]});
            skFitSpline(sketch, "E2901", {"points": [v(-329.6, 112.86) * mm, v(-328.37, 113.57) * mm, v(-327.6, 114.9) * mm, v(-327.6, 116.32) * mm]});
            skLineSegment(sketch, "E2902", {"start": v(-335.17, 145.47) * mm, "end": v(-344.3, 145.47) * mm});
            skLineSegment(sketch, "E2903", {"start": v(-344.3, 145.47) * mm, "end": v(-344.3, 114.95) * mm});
            skFitSpline(sketch, "E2904", {"points": [v(-306.88, 147.12) * mm, v(-306.88, 147.7) * mm, v(-307.18, 148.22) * mm, v(-307.68, 148.51) * mm]});
            skFitSpline(sketch, "E2905", {"points": [v(-307.68, 148.51) * mm, v(-308.17, 148.8) * mm, v(-308.79, 148.8) * mm, v(-309.28, 148.51) * mm]});
            skFitSpline(sketch, "E2906", {"points": [v(-309.28, 148.51) * mm, v(-309.78, 148.22) * mm, v(-310.08, 147.7) * mm, v(-310.08, 147.12) * mm]});
            skFitSpline(sketch, "E2907", {"points": [v(-310.08, 147.12) * mm, v(-310.08, 146.55) * mm, v(-309.78, 146.02) * mm, v(-309.28, 145.73) * mm]});
            skFitSpline(sketch, "E2908", {"points": [v(-309.28, 145.73) * mm, v(-308.79, 145.44) * mm, v(-308.17, 145.44) * mm, v(-307.68, 145.73) * mm]});
            skFitSpline(sketch, "E2909", {"points": [v(-307.68, 145.73) * mm, v(-307.18, 146.02) * mm, v(-306.88, 146.55) * mm, v(-306.88, 147.12) * mm]});
            skLineSegment(sketch, "E2910", {"start": v(-332.3, 102.95) * mm, "end": v(-310.7, 102.95) * mm});
            skFitSpline(sketch, "E2911", {"points": [v(-256.3, 158.28) * mm, v(-256.3, 160.04) * mm, v(-256.69, 161.77) * mm, v(-257.43, 163.36) * mm]});
            skFitSpline(sketch, "E2912", {"points": [v(-282.66, 147.95) * mm, v(-282.66, 148.13) * mm, v(-282.75, 148.3) * mm, v(-282.9, 148.38) * mm]});
            skFitSpline(sketch, "E2913", {"points": [v(-282.22, 149.07) * mm, v(-282.33, 149.25) * mm, v(-282.53, 149.34) * mm, v(-282.74, 149.3) * mm]});
            skFitSpline(sketch, "E2914", {"points": [v(-282.74, 149.3) * mm, v(-282.95, 149.27) * mm, v(-283.11, 149.1) * mm, v(-283.15, 148.9) * mm]});
            skFitSpline(sketch, "E2915", {"points": [v(-283.15, 148.9) * mm, v(-283.18, 148.7) * mm, v(-283.09, 148.49) * mm, v(-282.9, 148.38) * mm]});
            skFitSpline(sketch, "E2916", {"points": [v(-282.22, 149.07) * mm, v(-282.13, 148.91) * mm, v(-281.97, 148.82) * mm, v(-281.79, 148.82) * mm]});
            skLineSegment(sketch, "E2917", {"start": v(-267.83, 148.82) * mm, "end": v(-256.3, 148.81) * mm});
            skLineSegment(sketch, "E2918", {"start": v(-256.3, 148.81) * mm, "end": v(-256.3, 158.28) * mm});
            skFitSpline(sketch, "E2919", {"points": [v(-271.13, 158.6) * mm, v(-271.13, 158.78) * mm, v(-271.22, 158.94) * mm, v(-271.38, 159.03) * mm]});
            skFitSpline(sketch, "E2920", {"points": [v(-270.7, 159.71) * mm, v(-270.8, 159.9) * mm, v(-271, 160) * mm, v(-271.22, 159.96) * mm]});
            skFitSpline(sketch, "E2921", {"points": [v(-271.22, 159.96) * mm, v(-271.42, 159.92) * mm, v(-271.58, 159.76) * mm, v(-271.62, 159.55) * mm]});
            skFitSpline(sketch, "E2922", {"points": [v(-271.62, 159.55) * mm, v(-271.66, 159.34) * mm, v(-271.56, 159.14) * mm, v(-271.38, 159.03) * mm]});
            skFitSpline(sketch, "E2923", {"points": [v(-270.7, 159.71) * mm, v(-270.6, 159.56) * mm, v(-270.44, 159.46) * mm, v(-270.26, 159.46) * mm]});
            skLineSegment(sketch, "E2924", {"start": v(-257.43, 163.36) * mm, "end": v(-267.83, 179.82) * mm});
            skLineSegment(sketch, "E2925", {"start": v(-267.83, 179.82) * mm, "end": v(-270.92, 179.82) * mm});
            skFitSpline(sketch, "E2926", {"points": [v(-268.7, 159.46) * mm, v(-268.52, 159.46) * mm, v(-268.35, 159.56) * mm, v(-268.26, 159.71) * mm]});
            skFitSpline(sketch, "E2927", {"points": [v(-267.58, 159.03) * mm, v(-267.4, 159.14) * mm, v(-267.3, 159.34) * mm, v(-267.34, 159.55) * mm]});
            skFitSpline(sketch, "E2928", {"points": [v(-267.34, 159.55) * mm, v(-267.37, 159.76) * mm, v(-267.54, 159.92) * mm, v(-267.74, 159.96) * mm]});
            skFitSpline(sketch, "E2929", {"points": [v(-267.74, 159.96) * mm, v(-267.95, 160) * mm, v(-268.16, 159.9) * mm, v(-268.26, 159.71) * mm]});
            skFitSpline(sketch, "E2930", {"points": [v(-267.58, 159.03) * mm, v(-267.73, 158.94) * mm, v(-267.83, 158.78) * mm, v(-267.83, 158.6) * mm]});
            skLineSegment(sketch, "E2931", {"start": v(-282.66, 145.46) * mm, "end": v(-282.66, 147.95) * mm});
            skFitSpline(sketch, "E2932", {"points": [v(-267.88, 169.47) * mm, v(-267.88, 170.04) * mm, v(-268.18, 170.57) * mm, v(-268.68, 170.85) * mm]});
            skFitSpline(sketch, "E2933", {"points": [v(-268.68, 170.85) * mm, v(-269.17, 171.14) * mm, v(-269.78, 171.14) * mm, v(-270.28, 170.85) * mm]});
            skFitSpline(sketch, "E2934", {"points": [v(-270.28, 170.85) * mm, v(-270.77, 170.57) * mm, v(-271.08, 170.04) * mm, v(-271.08, 169.47) * mm]});
            skFitSpline(sketch, "E2935", {"points": [v(-271.08, 169.47) * mm, v(-271.08, 168.9) * mm, v(-270.77, 168.37) * mm, v(-270.28, 168.08) * mm]});
            skFitSpline(sketch, "E2936", {"points": [v(-270.28, 168.08) * mm, v(-269.78, 167.8) * mm, v(-269.17, 167.8) * mm, v(-268.68, 168.08) * mm]});
            skFitSpline(sketch, "E2937", {"points": [v(-268.68, 168.08) * mm, v(-268.18, 168.37) * mm, v(-267.88, 168.9) * mm, v(-267.88, 169.47) * mm]});
            skLineSegment(sketch, "E2938", {"start": v(-281.79, 148.82) * mm, "end": v(-271.13, 148.82) * mm});
            skLineSegment(sketch, "E2939", {"start": v(-271.13, 148.82) * mm, "end": v(-271.13, 158.6) * mm});
            skLineSegment(sketch, "E2940", {"start": v(-270.26, 159.46) * mm, "end": v(-268.7, 159.46) * mm});
            skLineSegment(sketch, "E2941", {"start": v(-267.83, 158.6) * mm, "end": v(-267.83, 148.82) * mm});
            skFitSpline(sketch, "E2942", {"points": [v(-38.13, -182.63) * mm, v(-33.05, -181.1) * mm, v(-29.57, -176.43) * mm, v(-29.57, -171.13) * mm]});
            skFitSpline(sketch, "E2943", {"points": [v(-38.7, -167.9) * mm, v(-38.88, -167.9) * mm, v(-39.04, -167.99) * mm, v(-39.13, -168.14) * mm]});
            skFitSpline(sketch, "E2944", {"points": [v(-39.82, -167.46) * mm, v(-40, -167.57) * mm, v(-40.1, -167.77) * mm, v(-40.06, -167.98) * mm]});
            skFitSpline(sketch, "E2945", {"points": [v(-40.06, -167.98) * mm, v(-40.02, -168.19) * mm, v(-39.86, -168.35) * mm, v(-39.65, -168.39) * mm]});
            skFitSpline(sketch, "E2946", {"points": [v(-39.65, -168.39) * mm, v(-39.45, -168.42) * mm, v(-39.24, -168.33) * mm, v(-39.13, -168.14) * mm]});
            skFitSpline(sketch, "E2947", {"points": [v(-39.82, -167.46) * mm, v(-39.66, -167.37) * mm, v(-39.57, -167.2) * mm, v(-39.57, -167.03) * mm]});
            skLineSegment(sketch, "E2948", {"start": v(-270.92, 179.82) * mm, "end": v(-335.74, 163.5) * mm});
            skFitSpline(sketch, "E2949", {"points": [v(-39.13, -164.34) * mm, v(-39.24, -164.16) * mm, v(-39.45, -164.06) * mm, v(-39.65, -164.1) * mm]});
            skFitSpline(sketch, "E2950", {"points": [v(-39.65, -164.1) * mm, v(-39.86, -164.14) * mm, v(-40.02, -164.3) * mm, v(-40.06, -164.5) * mm]});
            skFitSpline(sketch, "E2951", {"points": [v(-40.06, -164.5) * mm, v(-40.1, -164.71) * mm, v(-40, -164.92) * mm, v(-39.82, -165.03) * mm]});
            skFitSpline(sketch, "E2952", {"points": [v(-39.13, -164.34) * mm, v(-39.04, -164.5) * mm, v(-38.88, -164.6) * mm, v(-38.7, -164.6) * mm]});
            skLineSegment(sketch, "E2953", {"start": v(-299.98, 109.55) * mm, "end": v(-282.66, 145.46) * mm});
            skLineSegment(sketch, "E2954", {"start": v(-29.57, -171.13) * mm, "end": v(-29.57, -167.9) * mm});
            skLineSegment(sketch, "E2955", {"start": v(-29.57, -167.9) * mm, "end": v(-38.7, -167.9) * mm});
            skFitSpline(sketch, "E2956", {"points": [v(-39.57, -165.46) * mm, v(-39.57, -165.28) * mm, v(-39.66, -165.12) * mm, v(-39.82, -165.03) * mm]});
            skFitSpline(sketch, "E2957", {"points": [v(-63.17, -122.07) * mm, v(-67.7, -122.07) * mm, v(-71.85, -124.62) * mm, v(-73.9, -128.67) * mm]});
            skFitSpline(sketch, "E2958", {"points": [v(-54.27, -135.44) * mm, v(-54.27, -133.65) * mm, v(-55.22, -132) * mm, v(-56.77, -131.1) * mm]});
            skFitSpline(sketch, "E2959", {"points": [v(-56.77, -131.1) * mm, v(-58.31, -130.22) * mm, v(-60.22, -130.22) * mm, v(-61.77, -131.1) * mm]});
            skFitSpline(sketch, "E2960", {"points": [v(-61.77, -131.1) * mm, v(-63.31, -132) * mm, v(-64.27, -133.65) * mm, v(-64.27, -135.44) * mm]});
            skFitSpline(sketch, "E2961", {"points": [v(-64.27, -135.44) * mm, v(-64.27, -137.22) * mm, v(-63.31, -138.88) * mm, v(-61.77, -139.77) * mm]});
            skFitSpline(sketch, "E2962", {"points": [v(-61.77, -139.77) * mm, v(-60.22, -140.66) * mm, v(-58.31, -140.66) * mm, v(-56.77, -139.77) * mm]});
            skFitSpline(sketch, "E2963", {"points": [v(-56.77, -139.77) * mm, v(-55.22, -138.88) * mm, v(-54.27, -137.22) * mm, v(-54.27, -135.44) * mm]});
            skLineSegment(sketch, "E2964", {"start": v(-39.57, -167.03) * mm, "end": v(-39.57, -165.46) * mm});
            skFitSpline(sketch, "E2965", {"points": [v(-29.57, -134.07) * mm, v(-29.57, -127.44) * mm, v(-34.94, -122.07) * mm, v(-41.57, -122.07) * mm]});
            skFitSpline(sketch, "E2966", {"points": [v(-38.27, -135.44) * mm, v(-38.27, -134.01) * mm, v(-39.03, -132.7) * mm, v(-40.27, -131.98) * mm]});
            skFitSpline(sketch, "E2967", {"points": [v(-40.27, -131.98) * mm, v(-41.5, -131.26) * mm, v(-43.03, -131.26) * mm, v(-44.27, -131.98) * mm]});
            skFitSpline(sketch, "E2968", {"points": [v(-44.27, -131.98) * mm, v(-45.5, -132.7) * mm, v(-46.27, -134.01) * mm, v(-46.27, -135.44) * mm]});
            skFitSpline(sketch, "E2969", {"points": [v(-46.27, -135.44) * mm, v(-46.27, -136.87) * mm, v(-45.5, -138.2) * mm, v(-44.27, -138.9) * mm]});
            skFitSpline(sketch, "E2970", {"points": [v(-44.27, -138.9) * mm, v(-43.03, -139.62) * mm, v(-41.5, -139.62) * mm, v(-40.27, -138.9) * mm]});
            skFitSpline(sketch, "E2971", {"points": [v(-40.27, -138.9) * mm, v(-39.03, -138.2) * mm, v(-38.27, -136.87) * mm, v(-38.27, -135.44) * mm]});
            skLineSegment(sketch, "E2972", {"start": v(-38.7, -164.6) * mm, "end": v(-29.57, -164.6) * mm});
            skLineSegment(sketch, "E2973", {"start": v(-29.57, -164.6) * mm, "end": v(-29.57, -134.07) * mm});
            skFitSpline(sketch, "E2974", {"points": [v(-63.8, -166.24) * mm, v(-63.8, -165.67) * mm, v(-64.1, -165.14) * mm, v(-64.6, -164.86) * mm]});
            skFitSpline(sketch, "E2975", {"points": [v(-64.6, -164.86) * mm, v(-65.09, -164.57) * mm, v(-65.7, -164.57) * mm, v(-66.2, -164.86) * mm]});
            skFitSpline(sketch, "E2976", {"points": [v(-66.2, -164.86) * mm, v(-66.69, -165.14) * mm, v(-67, -165.67) * mm, v(-67, -166.24) * mm]});
            skFitSpline(sketch, "E2977", {"points": [v(-67, -166.24) * mm, v(-67, -166.81) * mm, v(-66.69, -167.34) * mm, v(-66.2, -167.63) * mm]});
            skFitSpline(sketch, "E2978", {"points": [v(-66.2, -167.63) * mm, v(-65.7, -167.91) * mm, v(-65.09, -167.91) * mm, v(-64.6, -167.63) * mm]});
            skFitSpline(sketch, "E2979", {"points": [v(-64.6, -167.63) * mm, v(-64.1, -167.34) * mm, v(-63.8, -166.81) * mm, v(-63.8, -166.24) * mm]});
            skLineSegment(sketch, "E2980", {"start": v(-41.57, -122.07) * mm, "end": v(-63.17, -122.07) * mm});
            skFitSpline(sketch, "E2981", {"points": [v(-117.57, -177.4) * mm, v(-117.57, -179.16) * mm, v(-117.18, -180.9) * mm, v(-116.44, -182.48) * mm]});
            skFitSpline(sketch, "E2982", {"points": [v(-91.65, -168.19) * mm, v(-91.54, -168.37) * mm, v(-91.34, -168.47) * mm, v(-91.13, -168.43) * mm]});
            skFitSpline(sketch, "E2983", {"points": [v(-91.13, -168.43) * mm, v(-90.92, -168.4) * mm, v(-90.76, -168.23) * mm, v(-90.72, -168.02) * mm]});
            skFitSpline(sketch, "E2984", {"points": [v(-90.72, -168.02) * mm, v(-90.69, -167.82) * mm, v(-90.78, -167.6) * mm, v(-90.97, -167.5) * mm]});
            skFitSpline(sketch, "E2985", {"points": [v(-91.65, -168.19) * mm, v(-91.74, -168.03) * mm, v(-91.9, -167.94) * mm, v(-92.08, -167.94) * mm]});
            skLineSegment(sketch, "E2986", {"start": v(-106.04, -167.94) * mm, "end": v(-117.57, -167.93) * mm});
            skLineSegment(sketch, "E2987", {"start": v(-117.57, -167.93) * mm, "end": v(-117.57, -177.4) * mm});
            skFitSpline(sketch, "E2988", {"points": [v(-102.74, -177.72) * mm, v(-102.74, -177.9) * mm, v(-102.65, -178.06) * mm, v(-102.5, -178.15) * mm]});
            skFitSpline(sketch, "E2989", {"points": [v(-103.18, -178.84) * mm, v(-103.07, -179.02) * mm, v(-102.86, -179.12) * mm, v(-102.66, -179.08) * mm]});
            skFitSpline(sketch, "E2990", {"points": [v(-102.66, -179.08) * mm, v(-102.45, -179.04) * mm, v(-102.29, -178.88) * mm, v(-102.25, -178.67) * mm]});
            skFitSpline(sketch, "E2991", {"points": [v(-102.25, -178.67) * mm, v(-102.21, -178.47) * mm, v(-102.31, -178.26) * mm, v(-102.5, -178.15) * mm]});
            skFitSpline(sketch, "E2992", {"points": [v(-103.18, -178.84) * mm, v(-103.26, -178.68) * mm, v(-103.43, -178.59) * mm, v(-103.6, -178.59) * mm]});
            skLineSegment(sketch, "E2993", {"start": v(-116.44, -182.48) * mm, "end": v(-106.04, -198.94) * mm});
            skLineSegment(sketch, "E2994", {"start": v(-106.04, -198.94) * mm, "end": v(-102.95, -198.94) * mm});
            skFitSpline(sketch, "E2995", {"points": [v(-105.18, -178.59) * mm, v(-105.35, -178.59) * mm, v(-105.52, -178.68) * mm, v(-105.6, -178.84) * mm]});
            skLineSegment(sketch, "E2996", {"start": v(-103.6, -178.59) * mm, "end": v(-105.18, -178.59) * mm});
            skFitSpline(sketch, "E2997", {"points": [v(-91.22, -167.07) * mm, v(-91.22, -167.25) * mm, v(-91.12, -167.42) * mm, v(-90.97, -167.5) * mm]});
            skFitSpline(sketch, "E2998", {"points": [v(-106.3, -178.15) * mm, v(-106.47, -178.26) * mm, v(-106.57, -178.47) * mm, v(-106.53, -178.67) * mm]});
            skFitSpline(sketch, "E2999", {"points": [v(-106.53, -178.67) * mm, v(-106.5, -178.88) * mm, v(-106.34, -179.04) * mm, v(-106.13, -179.08) * mm]});
            skFitSpline(sketch, "E3000", {"points": [v(-106.13, -179.08) * mm, v(-105.92, -179.11) * mm, v(-105.71, -179.02) * mm, v(-105.6, -178.84) * mm]});
            skFitSpline(sketch, "E3001", {"points": [v(-106.3, -178.15) * mm, v(-106.14, -178.06) * mm, v(-106.04, -177.9) * mm, v(-106.04, -177.72) * mm]});
            skLineSegment(sketch, "E3002", {"start": v(-91.22, -164.58) * mm, "end": v(-91.22, -167.07) * mm});
            skFitSpline(sketch, "E3003", {"points": [v(-102.8, -188.59) * mm, v(-102.8, -188.02) * mm, v(-103.1, -187.49) * mm, v(-103.6, -187.2) * mm]});
            skFitSpline(sketch, "E3004", {"points": [v(-103.6, -187.2) * mm, v(-104.09, -186.92) * mm, v(-104.7, -186.92) * mm, v(-105.2, -187.2) * mm]});
            skFitSpline(sketch, "E3005", {"points": [v(-105.2, -187.2) * mm, v(-105.69, -187.49) * mm, v(-106, -188.02) * mm, v(-106, -188.59) * mm]});
            skFitSpline(sketch, "E3006", {"points": [v(-106, -188.59) * mm, v(-106, -189.16) * mm, v(-105.69, -189.69) * mm, v(-105.2, -189.97) * mm]});
            skFitSpline(sketch, "E3007", {"points": [v(-105.2, -189.97) * mm, v(-104.7, -190.26) * mm, v(-104.09, -190.26) * mm, v(-103.6, -189.97) * mm]});
            skFitSpline(sketch, "E3008", {"points": [v(-103.6, -189.97) * mm, v(-103.1, -189.69) * mm, v(-102.8, -189.16) * mm, v(-102.8, -188.59) * mm]});
            skLineSegment(sketch, "E3009", {"start": v(-92.08, -167.94) * mm, "end": v(-102.74, -167.94) * mm});
            skLineSegment(sketch, "E3010", {"start": v(-102.74, -167.94) * mm, "end": v(-102.74, -177.72) * mm});
            skLineSegment(sketch, "E3011", {"start": v(-106.04, -177.72) * mm, "end": v(-106.04, -167.94) * mm});
            skFitSpline(sketch, "E3012", {"points": [v(169.88, -35.87) * mm, v(170.07, -35.68) * mm, v(170.18, -35.41) * mm, v(170.17, -35.14) * mm]});
            skFitSpline(sketch, "E3013", {"points": [v(170.15, 13.5) * mm, v(170.15, 13.75) * mm, v(170.04, 14) * mm, v(169.86, 14.18) * mm]});
            skLineSegment(sketch, "E3014", {"start": v(-102.95, -198.94) * mm, "end": v(-38.13, -182.63) * mm});
            skLineSegment(sketch, "E3015", {"start": v(-73.9, -128.67) * mm, "end": v(-91.22, -164.58) * mm});
            skFitSpline(sketch, "E3016", {"points": [v(162.25, -43.14) * mm, v(162.42, -43.19) * mm, v(162.6, -43.14) * mm, v(162.73, -43.01) * mm]});
            skFitSpline(sketch, "E3017", {"points": [v(162.25, -43.14) * mm, v(162.04, -43.09) * mm, v(161.83, -43.17) * mm, v(161.7, -43.34) * mm]});
            skFitSpline(sketch, "E3018", {"points": [v(161.7, -43.34) * mm, v(161.59, -43.51) * mm, v(161.59, -43.74) * mm, v(161.7, -43.91) * mm]});
            skFitSpline(sketch, "E3019", {"points": [v(161.7, -43.91) * mm, v(161.83, -44.09) * mm, v(162.04, -44.16) * mm, v(162.25, -44.1) * mm]});
            skFitSpline(sketch, "E3020", {"points": [v(162.73, -44.24) * mm, v(162.6, -44.11) * mm, v(162.42, -44.06) * mm, v(162.25, -44.1) * mm]});
            skLineSegment(sketch, "E3021", {"start": v(170.15, 13.5) * mm, "end": v(170.17, -35.14) * mm});
            skFitSpline(sketch, "E3022", {"points": [v(163.89, -46.1) * mm, v(163.98, -46) * mm, v(164.03, -45.88) * mm, v(164.03, -45.75) * mm]});
            skFitSpline(sketch, "E3023", {"points": [v(164.03, -45.75) * mm, v(164.03, -45.62) * mm, v(163.98, -45.49) * mm, v(163.89, -45.4) * mm]});
            skLineSegment(sketch, "E3024", {"start": v(133.37, 41.7) * mm, "end": v(133.4, -63.36) * mm});
            skFitSpline(sketch, "E3025", {"points": [v(159.64, -49.64) * mm, v(159.74, -49.73) * mm, v(159.86, -49.78) * mm, v(160, -49.78) * mm]});
            skFitSpline(sketch, "E3026", {"points": [v(160, -49.78) * mm, v(160.13, -49.78) * mm, v(160.26, -49.73) * mm, v(160.35, -49.64) * mm]});
            skLineSegment(sketch, "E3027", {"start": v(169.88, -35.87) * mm, "end": v(162.73, -43.01) * mm});
            skFitSpline(sketch, "E3028", {"points": [v(158.36, -48) * mm, v(158.31, -48.17) * mm, v(158.36, -48.36) * mm, v(158.49, -48.48) * mm]});
            skFitSpline(sketch, "E3029", {"points": [v(158.36, -48) * mm, v(158.41, -47.8) * mm, v(158.33, -47.58) * mm, v(158.16, -47.46) * mm]});
            skFitSpline(sketch, "E3030", {"points": [v(158.16, -47.46) * mm, v(158, -47.34) * mm, v(157.76, -47.34) * mm, v(157.59, -47.46) * mm]});
            skFitSpline(sketch, "E3031", {"points": [v(157.59, -47.46) * mm, v(157.42, -47.58) * mm, v(157.34, -47.8) * mm, v(157.4, -48) * mm]});
            skFitSpline(sketch, "E3032", {"points": [v(157.26, -48.48) * mm, v(157.39, -48.36) * mm, v(157.44, -48.17) * mm, v(157.4, -48) * mm]});
            skLineSegment(sketch, "E3033", {"start": v(162.73, -44.24) * mm, "end": v(163.89, -45.4) * mm});
            skLineSegment(sketch, "E3034", {"start": v(163.89, -46.1) * mm, "end": v(160.35, -49.64) * mm});
            skFitSpline(sketch, "E3035", {"points": [v(147.26, -58.13) * mm, v(147.43, -58.18) * mm, v(147.61, -58.13) * mm, v(147.74, -58) * mm]});
            skFitSpline(sketch, "E3036", {"points": [v(147.26, -58.13) * mm, v(147.05, -58.08) * mm, v(146.84, -58.16) * mm, v(146.72, -58.33) * mm]});
            skFitSpline(sketch, "E3037", {"points": [v(146.72, -58.33) * mm, v(146.6, -58.5) * mm, v(146.6, -58.73) * mm, v(146.72, -58.9) * mm]});
            skFitSpline(sketch, "E3038", {"points": [v(146.72, -58.9) * mm, v(146.84, -59.08) * mm, v(147.05, -59.15) * mm, v(147.26, -59.1) * mm]});
            skFitSpline(sketch, "E3039", {"points": [v(147.74, -59.23) * mm, v(147.61, -59.1) * mm, v(147.43, -59.05) * mm, v(147.26, -59.1) * mm]});
            skLineSegment(sketch, "E3040", {"start": v(159.64, -49.64) * mm, "end": v(158.49, -48.48) * mm});
            skFitSpline(sketch, "E3041", {"points": [v(148.9, -61.1) * mm, v(149.1, -60.9) * mm, v(149.1, -60.58) * mm, v(148.9, -60.39) * mm]});
            skLineSegment(sketch, "E3042", {"start": v(157.26, -48.48) * mm, "end": v(153.63, -52.11) * mm});
            skLineSegment(sketch, "E3043", {"start": v(153.63, -52.11) * mm, "end": v(151.51, -50) * mm});
            skLineSegment(sketch, "E3044", {"start": v(151.51, -50) * mm, "end": v(152.41, -49.09) * mm});
            skFitSpline(sketch, "E3045", {"points": [v(144.65, -64.63) * mm, v(144.75, -64.72) * mm, v(144.87, -64.77) * mm, v(145, -64.77) * mm]});
            skFitSpline(sketch, "E3046", {"points": [v(145, -64.77) * mm, v(145.14, -64.77) * mm, v(145.27, -64.72) * mm, v(145.36, -64.63) * mm]});
            skLineSegment(sketch, "E3047", {"start": v(148.35, -53.15) * mm, "end": v(149.25, -52.25) * mm});
            skLineSegment(sketch, "E3048", {"start": v(149.25, -52.25) * mm, "end": v(151.37, -54.37) * mm});
            skLineSegment(sketch, "E3049", {"start": v(151.37, -54.37) * mm, "end": v(147.74, -58) * mm});
            skFitSpline(sketch, "E3050", {"points": [v(143.37, -62.99) * mm, v(143.32, -63.16) * mm, v(143.37, -63.35) * mm, v(143.5, -63.47) * mm]});
            skFitSpline(sketch, "E3051", {"points": [v(143.37, -62.99) * mm, v(143.42, -62.79) * mm, v(143.34, -62.57) * mm, v(143.17, -62.45) * mm]});
            skFitSpline(sketch, "E3052", {"points": [v(143.17, -62.45) * mm, v(143, -62.33) * mm, v(142.77, -62.33) * mm, v(142.6, -62.45) * mm]});
            skFitSpline(sketch, "E3053", {"points": [v(142.6, -62.45) * mm, v(142.43, -62.57) * mm, v(142.35, -62.79) * mm, v(142.4, -62.99) * mm]});
            skFitSpline(sketch, "E3054", {"points": [v(142.27, -63.47) * mm, v(142.4, -63.35) * mm, v(142.45, -63.16) * mm, v(142.4, -62.99) * mm]});
            skLineSegment(sketch, "E3055", {"start": v(147.74, -59.23) * mm, "end": v(148.9, -60.39) * mm});
            skLineSegment(sketch, "E3056", {"start": v(148.9, -61.1) * mm, "end": v(145.36, -64.63) * mm});
            skFitSpline(sketch, "E3057", {"points": [v(133.4, -63.36) * mm, v(133.4, -65.49) * mm, v(134.25, -67.52) * mm, v(135.75, -69.02) * mm]});
            skFitSpline(sketch, "E3058", {"points": [v(135.72, 47.35) * mm, v(134.22, 45.85) * mm, v(133.37, 43.82) * mm, v(133.37, 41.7) * mm]});
            skLineSegment(sketch, "E3059", {"start": v(144.65, -64.63) * mm, "end": v(143.5, -63.47) * mm});
            skFitSpline(sketch, "E3060", {"points": [v(142.37, 41.32) * mm, v(142.41, 41.5) * mm, v(142.36, 41.68) * mm, v(142.24, 41.8) * mm]});
            skFitSpline(sketch, "E3061", {"points": [v(142.37, 41.32) * mm, v(142.31, 41.12) * mm, v(142.4, 40.9) * mm, v(142.56, 40.78) * mm]});
            skFitSpline(sketch, "E3062", {"points": [v(142.56, 40.78) * mm, v(142.73, 40.66) * mm, v(142.96, 40.66) * mm, v(143.14, 40.78) * mm]});
            skFitSpline(sketch, "E3063", {"points": [v(143.14, 40.78) * mm, v(143.3, 40.9) * mm, v(143.39, 41.12) * mm, v(143.33, 41.32) * mm]});
            skFitSpline(sketch, "E3064", {"points": [v(143.46, 41.8) * mm, v(143.34, 41.68) * mm, v(143.29, 41.5) * mm, v(143.33, 41.32) * mm]});
            skLineSegment(sketch, "E3065", {"start": v(142.27, -63.47) * mm, "end": v(136.24, -69.5) * mm});
            skLineSegment(sketch, "E3066", {"start": v(136.24, -69.5) * mm, "end": v(135.75, -69.02) * mm});
            skFitSpline(sketch, "E3067", {"points": [v(145.32, 42.96) * mm, v(145.23, 43.05) * mm, v(145.1, 43.1) * mm, v(144.97, 43.1) * mm]});
            skFitSpline(sketch, "E3068", {"points": [v(144.97, 43.1) * mm, v(144.84, 43.1) * mm, v(144.71, 43.05) * mm, v(144.62, 42.96) * mm]});
            skLineSegment(sketch, "E3069", {"start": v(152.41, -49.09) * mm, "end": v(149.58, -46.26) * mm});
            skLineSegment(sketch, "E3070", {"start": v(149.58, -46.26) * mm, "end": v(148.68, -47.16) * mm});
            skLineSegment(sketch, "E3071", {"start": v(148.68, -47.16) * mm, "end": v(146.56, -45.04) * mm});
            skLineSegment(sketch, "E3072", {"start": v(146.56, -45.04) * mm, "end": v(144.3, -47.3) * mm});
            skLineSegment(sketch, "E3073", {"start": v(144.3, -47.3) * mm, "end": v(146.42, -49.42) * mm});
            skLineSegment(sketch, "E3074", {"start": v(146.42, -49.42) * mm, "end": v(145.52, -50.33) * mm});
            skLineSegment(sketch, "E3075", {"start": v(145.52, -50.33) * mm, "end": v(148.35, -53.15) * mm});
            skFitSpline(sketch, "E3076", {"points": [v(148.86, 38.72) * mm, v(148.95, 38.8) * mm, v(149, 38.94) * mm, v(149, 39.07) * mm]});
            skFitSpline(sketch, "E3077", {"points": [v(149, 39.07) * mm, v(149, 39.2) * mm, v(148.95, 39.33) * mm, v(148.86, 39.42) * mm]});
            skLineSegment(sketch, "E3078", {"start": v(135.72, 47.35) * mm, "end": v(136.2, 47.84) * mm});
            skLineSegment(sketch, "E3079", {"start": v(136.2, 47.84) * mm, "end": v(142.24, 41.8) * mm});
            skFitSpline(sketch, "E3080", {"points": [v(147.22, 37.43) * mm, v(147.4, 37.38) * mm, v(147.58, 37.43) * mm, v(147.7, 37.56) * mm]});
            skFitSpline(sketch, "E3081", {"points": [v(147.22, 37.43) * mm, v(147.02, 37.49) * mm, v(146.8, 37.4) * mm, v(146.68, 37.23) * mm]});
            skFitSpline(sketch, "E3082", {"points": [v(146.68, 37.23) * mm, v(146.56, 37.06) * mm, v(146.56, 36.83) * mm, v(146.68, 36.66) * mm]});
            skFitSpline(sketch, "E3083", {"points": [v(146.68, 36.66) * mm, v(146.8, 36.49) * mm, v(147.02, 36.41) * mm, v(147.22, 36.47) * mm]});
            skFitSpline(sketch, "E3084", {"points": [v(147.7, 36.34) * mm, v(147.58, 36.46) * mm, v(147.4, 36.51) * mm, v(147.22, 36.47) * mm]});
            skLineSegment(sketch, "E3085", {"start": v(143.46, 41.8) * mm, "end": v(144.62, 42.96) * mm});
            skFitSpline(sketch, "E3086", {"points": [v(157.36, 26.33) * mm, v(157.4, 26.5) * mm, v(157.35, 26.69) * mm, v(157.23, 26.81) * mm]});
            skFitSpline(sketch, "E3087", {"points": [v(157.36, 26.33) * mm, v(157.3, 26.13) * mm, v(157.38, 25.91) * mm, v(157.55, 25.8) * mm]});
            skFitSpline(sketch, "E3088", {"points": [v(157.55, 25.8) * mm, v(157.73, 25.67) * mm, v(157.95, 25.67) * mm, v(158.13, 25.8) * mm]});
            skFitSpline(sketch, "E3089", {"points": [v(158.13, 25.8) * mm, v(158.3, 25.91) * mm, v(158.38, 26.13) * mm, v(158.32, 26.33) * mm]});
            skFitSpline(sketch, "E3090", {"points": [v(158.45, 26.81) * mm, v(158.33, 26.69) * mm, v(158.28, 26.5) * mm, v(158.32, 26.33) * mm]});
            skLineSegment(sketch, "E3091", {"start": v(145.32, 42.96) * mm, "end": v(148.86, 39.42) * mm});
            skFitSpline(sketch, "E3092", {"points": [v(160.32, 27.97) * mm, v(160.22, 28.06) * mm, v(160.1, 28.11) * mm, v(159.96, 28.11) * mm]});
            skFitSpline(sketch, "E3093", {"points": [v(159.96, 28.11) * mm, v(159.83, 28.11) * mm, v(159.7, 28.06) * mm, v(159.6, 27.97) * mm]});
            skLineSegment(sketch, "E3094", {"start": v(148.86, 38.72) * mm, "end": v(147.7, 37.56) * mm});
            skFitSpline(sketch, "E3095", {"points": [v(163.85, 23.73) * mm, v(163.94, 23.82) * mm, v(164, 23.95) * mm, v(164, 24.08) * mm]});
            skFitSpline(sketch, "E3096", {"points": [v(164, 24.08) * mm, v(164, 24.21) * mm, v(163.94, 24.34) * mm, v(163.85, 24.43) * mm]});
            skLineSegment(sketch, "E3097", {"start": v(147.7, 36.34) * mm, "end": v(151.33, 32.7) * mm});
            skLineSegment(sketch, "E3098", {"start": v(151.33, 32.7) * mm, "end": v(149.21, 30.58) * mm});
            skLineSegment(sketch, "E3099", {"start": v(149.21, 30.58) * mm, "end": v(148.31, 31.49) * mm});
            skLineSegment(sketch, "E3100", {"start": v(148.31, 31.49) * mm, "end": v(145.48, 28.66) * mm});
            skLineSegment(sketch, "E3101", {"start": v(145.48, 28.66) * mm, "end": v(146.38, 27.76) * mm});
            skLineSegment(sketch, "E3102", {"start": v(146.38, 27.76) * mm, "end": v(144.26, 25.63) * mm});
            skLineSegment(sketch, "E3103", {"start": v(144.26, 25.63) * mm, "end": v(146.53, 23.37) * mm});
            skLineSegment(sketch, "E3104", {"start": v(146.53, 23.37) * mm, "end": v(148.65, 25.5) * mm});
            skLineSegment(sketch, "E3105", {"start": v(148.65, 25.5) * mm, "end": v(149.55, 24.6) * mm});
            skLineSegment(sketch, "E3106", {"start": v(149.55, 24.6) * mm, "end": v(152.38, 27.42) * mm});
            skLineSegment(sketch, "E3107", {"start": v(152.38, 27.42) * mm, "end": v(151.48, 28.32) * mm});
            skLineSegment(sketch, "E3108", {"start": v(151.48, 28.32) * mm, "end": v(153.6, 30.44) * mm});
            skLineSegment(sketch, "E3109", {"start": v(153.6, 30.44) * mm, "end": v(157.23, 26.81) * mm});
            skFitSpline(sketch, "E3110", {"points": [v(162.21, 22.44) * mm, v(162.38, 22.4) * mm, v(162.57, 22.44) * mm, v(162.7, 22.57) * mm]});
            skFitSpline(sketch, "E3111", {"points": [v(162.21, 22.44) * mm, v(162, 22.5) * mm, v(161.8, 22.42) * mm, v(161.67, 22.24) * mm]});
            skFitSpline(sketch, "E3112", {"points": [v(161.67, 22.24) * mm, v(161.55, 22.07) * mm, v(161.55, 21.84) * mm, v(161.67, 21.67) * mm]});
            skFitSpline(sketch, "E3113", {"points": [v(161.67, 21.67) * mm, v(161.8, 21.5) * mm, v(162, 21.42) * mm, v(162.21, 21.47) * mm]});
            skFitSpline(sketch, "E3114", {"points": [v(162.7, 21.35) * mm, v(162.57, 21.47) * mm, v(162.38, 21.52) * mm, v(162.21, 21.47) * mm]});
            skLineSegment(sketch, "E3115", {"start": v(158.45, 26.81) * mm, "end": v(159.6, 27.97) * mm});
            skFitSpline(sketch, "E3116", {"points": [v(239.45, 13.58) * mm, v(239.25, 13.38) * mm, v(239.15, 13.12) * mm, v(239.16, 12.85) * mm]});
            skFitSpline(sketch, "E3117", {"points": [v(239.17, -35.79) * mm, v(239.18, -36.05) * mm, v(239.28, -36.29) * mm, v(239.46, -36.47) * mm]});
            skLineSegment(sketch, "E3118", {"start": v(160.32, 27.97) * mm, "end": v(163.85, 24.43) * mm});
            skLineSegment(sketch, "E3119", {"start": v(163.85, 23.73) * mm, "end": v(162.7, 22.57) * mm});
            skLineSegment(sketch, "E3120", {"start": v(162.7, 21.35) * mm, "end": v(169.86, 14.18) * mm});
            skFitSpline(sketch, "E3121", {"points": [v(247.08, 20.85) * mm, v(246.9, 20.9) * mm, v(246.72, 20.85) * mm, v(246.6, 20.72) * mm]});
            skFitSpline(sketch, "E3122", {"points": [v(247.08, 20.85) * mm, v(247.28, 20.8) * mm, v(247.5, 20.88) * mm, v(247.62, 21.05) * mm]});
            skFitSpline(sketch, "E3123", {"points": [v(247.62, 21.05) * mm, v(247.74, 21.22) * mm, v(247.74, 21.45) * mm, v(247.62, 21.62) * mm]});
            skFitSpline(sketch, "E3124", {"points": [v(247.62, 21.62) * mm, v(247.5, 21.8) * mm, v(247.28, 21.87) * mm, v(247.08, 21.82) * mm]});
            skFitSpline(sketch, "E3125", {"points": [v(246.6, 21.95) * mm, v(246.72, 21.82) * mm, v(246.9, 21.77) * mm, v(247.08, 21.82) * mm]});
            skLineSegment(sketch, "E3126", {"start": v(239.17, -35.79) * mm, "end": v(239.16, 12.85) * mm});
            skFitSpline(sketch, "E3127", {"points": [v(245.44, 23.8) * mm, v(245.34, 23.72) * mm, v(245.3, 23.59) * mm, v(245.3, 23.46) * mm]});
            skFitSpline(sketch, "E3128", {"points": [v(245.3, 23.46) * mm, v(245.3, 23.32) * mm, v(245.34, 23.2) * mm, v(245.44, 23.1) * mm]});
            skLineSegment(sketch, "E3129", {"start": v(275.95, -63.99) * mm, "end": v(275.91, 41.07) * mm});
            skFitSpline(sketch, "E3130", {"points": [v(249.68, 27.35) * mm, v(249.59, 27.44) * mm, v(249.46, 27.5) * mm, v(249.33, 27.5) * mm]});
            skFitSpline(sketch, "E3131", {"points": [v(249.33, 27.5) * mm, v(249.2, 27.5) * mm, v(249.07, 27.44) * mm, v(248.97, 27.35) * mm]});
            skLineSegment(sketch, "E3132", {"start": v(239.45, 13.58) * mm, "end": v(246.6, 20.72) * mm});
            skFitSpline(sketch, "E3133", {"points": [v(250.97, 25.7) * mm, v(251.01, 25.88) * mm, v(250.96, 26.06) * mm, v(250.84, 26.19) * mm]});
            skFitSpline(sketch, "E3134", {"points": [v(250.97, 25.7) * mm, v(250.91, 25.5) * mm, v(250.99, 25.29) * mm, v(251.16, 25.17) * mm]});
            skFitSpline(sketch, "E3135", {"points": [v(251.16, 25.17) * mm, v(251.33, 25.05) * mm, v(251.56, 25.05) * mm, v(251.74, 25.17) * mm]});
            skFitSpline(sketch, "E3136", {"points": [v(251.74, 25.17) * mm, v(251.9, 25.29) * mm, v(251.99, 25.5) * mm, v(251.93, 25.7) * mm]});
            skFitSpline(sketch, "E3137", {"points": [v(252.06, 26.19) * mm, v(251.93, 26.06) * mm, v(251.89, 25.88) * mm, v(251.93, 25.7) * mm]});
            skLineSegment(sketch, "E3138", {"start": v(246.6, 21.95) * mm, "end": v(245.44, 23.1) * mm});
            skLineSegment(sketch, "E3139", {"start": v(245.44, 23.8) * mm, "end": v(248.97, 27.35) * mm});
            skFitSpline(sketch, "E3140", {"points": [v(262.07, 35.84) * mm, v(261.9, 35.89) * mm, v(261.71, 35.84) * mm, v(261.58, 35.71) * mm]});
            skFitSpline(sketch, "E3141", {"points": [v(262.07, 35.84) * mm, v(262.27, 35.79) * mm, v(262.49, 35.87) * mm, v(262.6, 36.04) * mm]});
            skFitSpline(sketch, "E3142", {"points": [v(262.6, 36.04) * mm, v(262.73, 36.21) * mm, v(262.73, 36.44) * mm, v(262.6, 36.61) * mm]});
            skFitSpline(sketch, "E3143", {"points": [v(262.6, 36.61) * mm, v(262.49, 36.78) * mm, v(262.27, 36.86) * mm, v(262.07, 36.8) * mm]});
            skFitSpline(sketch, "E3144", {"points": [v(261.58, 36.94) * mm, v(261.71, 36.81) * mm, v(261.9, 36.76) * mm, v(262.07, 36.8) * mm]});
            skLineSegment(sketch, "E3145", {"start": v(249.68, 27.35) * mm, "end": v(250.84, 26.19) * mm});
            skFitSpline(sketch, "E3146", {"points": [v(260.43, 38.8) * mm, v(260.34, 38.7) * mm, v(260.28, 38.58) * mm, v(260.28, 38.45) * mm]});
            skFitSpline(sketch, "E3147", {"points": [v(260.28, 38.45) * mm, v(260.28, 38.31) * mm, v(260.34, 38.19) * mm, v(260.43, 38.1) * mm]});
            skLineSegment(sketch, "E3148", {"start": v(252.06, 26.19) * mm, "end": v(255.7, 29.82) * mm});
            skLineSegment(sketch, "E3149", {"start": v(255.7, 29.82) * mm, "end": v(257.81, 27.7) * mm});
            skLineSegment(sketch, "E3150", {"start": v(257.81, 27.7) * mm, "end": v(256.91, 26.8) * mm});
            skFitSpline(sketch, "E3151", {"points": [v(264.67, 42.34) * mm, v(264.58, 42.43) * mm, v(264.45, 42.48) * mm, v(264.32, 42.48) * mm]});
            skFitSpline(sketch, "E3152", {"points": [v(264.32, 42.48) * mm, v(264.19, 42.48) * mm, v(264.06, 42.43) * mm, v(263.96, 42.34) * mm]});
            skLineSegment(sketch, "E3153", {"start": v(260.98, 30.86) * mm, "end": v(260.08, 29.96) * mm});
            skLineSegment(sketch, "E3154", {"start": v(260.08, 29.96) * mm, "end": v(257.95, 32.08) * mm});
            skLineSegment(sketch, "E3155", {"start": v(257.95, 32.08) * mm, "end": v(261.58, 35.71) * mm});
            skFitSpline(sketch, "E3156", {"points": [v(265.96, 40.7) * mm, v(266, 40.87) * mm, v(265.95, 41.05) * mm, v(265.83, 41.18) * mm]});
            skFitSpline(sketch, "E3157", {"points": [v(265.96, 40.7) * mm, v(265.9, 40.5) * mm, v(265.98, 40.28) * mm, v(266.15, 40.16) * mm]});
            skFitSpline(sketch, "E3158", {"points": [v(266.15, 40.16) * mm, v(266.32, 40.04) * mm, v(266.55, 40.04) * mm, v(266.73, 40.16) * mm]});
            skFitSpline(sketch, "E3159", {"points": [v(266.73, 40.16) * mm, v(266.9, 40.28) * mm, v(266.98, 40.5) * mm, v(266.92, 40.7) * mm]});
            skFitSpline(sketch, "E3160", {"points": [v(267.05, 41.18) * mm, v(266.93, 41.05) * mm, v(266.88, 40.87) * mm, v(266.92, 40.7) * mm]});
            skLineSegment(sketch, "E3161", {"start": v(261.58, 36.94) * mm, "end": v(260.43, 38.1) * mm});
            skLineSegment(sketch, "E3162", {"start": v(260.43, 38.8) * mm, "end": v(263.96, 42.34) * mm});
            skFitSpline(sketch, "E3163", {"points": [v(275.91, 41.07) * mm, v(275.91, 43.2) * mm, v(275.07, 45.23) * mm, v(273.57, 46.73) * mm]});
            skFitSpline(sketch, "E3164", {"points": [v(273.6, -69.64) * mm, v(275.1, -68.14) * mm, v(275.95, -66.1) * mm, v(275.95, -63.99) * mm]});
            skLineSegment(sketch, "E3165", {"start": v(264.67, 42.34) * mm, "end": v(265.83, 41.18) * mm});
            skFitSpline(sketch, "E3166", {"points": [v(266.96, -63.61) * mm, v(266.91, -63.78) * mm, v(266.96, -63.97) * mm, v(267.09, -64.1) * mm]});
            skFitSpline(sketch, "E3167", {"points": [v(266.96, -63.61) * mm, v(267.01, -63.4) * mm, v(266.93, -63.2) * mm, v(266.76, -63.07) * mm]});
            skFitSpline(sketch, "E3168", {"points": [v(266.76, -63.07) * mm, v(266.59, -62.95) * mm, v(266.36, -62.95) * mm, v(266.19, -63.07) * mm]});
            skFitSpline(sketch, "E3169", {"points": [v(266.19, -63.07) * mm, v(266.02, -63.2) * mm, v(265.94, -63.4) * mm, v(266, -63.61) * mm]});
            skFitSpline(sketch, "E3170", {"points": [v(265.86, -64.1) * mm, v(265.99, -63.97) * mm, v(266.04, -63.78) * mm, v(266, -63.61) * mm]});
            skLineSegment(sketch, "E3171", {"start": v(267.05, 41.18) * mm, "end": v(273.09, 47.21) * mm});
            skLineSegment(sketch, "E3172", {"start": v(273.09, 47.21) * mm, "end": v(273.57, 46.73) * mm});
            skFitSpline(sketch, "E3173", {"points": [v(264, -65.25) * mm, v(264.1, -65.34) * mm, v(264.22, -65.4) * mm, v(264.35, -65.4) * mm]});
            skFitSpline(sketch, "E3174", {"points": [v(264.35, -65.4) * mm, v(264.49, -65.4) * mm, v(264.61, -65.34) * mm, v(264.7, -65.25) * mm]});
            skLineSegment(sketch, "E3175", {"start": v(256.91, 26.8) * mm, "end": v(259.74, 23.97) * mm});
            skLineSegment(sketch, "E3176", {"start": v(259.74, 23.97) * mm, "end": v(260.64, 24.87) * mm});
            skLineSegment(sketch, "E3177", {"start": v(260.64, 24.87) * mm, "end": v(262.76, 22.75) * mm});
            skLineSegment(sketch, "E3178", {"start": v(262.76, 22.75) * mm, "end": v(265.03, 25.01) * mm});
            skLineSegment(sketch, "E3179", {"start": v(265.03, 25.01) * mm, "end": v(262.9, 27.13) * mm});
            skLineSegment(sketch, "E3180", {"start": v(262.9, 27.13) * mm, "end": v(263.8, 28.03) * mm});
            skLineSegment(sketch, "E3181", {"start": v(263.8, 28.03) * mm, "end": v(260.98, 30.86) * mm});
            skFitSpline(sketch, "E3182", {"points": [v(260.46, -61) * mm, v(260.37, -61.1) * mm, v(260.32, -61.23) * mm, v(260.32, -61.36) * mm]});
            skFitSpline(sketch, "E3183", {"points": [v(260.32, -61.36) * mm, v(260.32, -61.5) * mm, v(260.37, -61.62) * mm, v(260.46, -61.72) * mm]});
            skLineSegment(sketch, "E3184", {"start": v(273.6, -69.64) * mm, "end": v(273.12, -70.13) * mm});
            skLineSegment(sketch, "E3185", {"start": v(273.12, -70.13) * mm, "end": v(267.09, -64.1) * mm});
            skFitSpline(sketch, "E3186", {"points": [v(262.1, -59.72) * mm, v(261.93, -59.68) * mm, v(261.75, -59.73) * mm, v(261.62, -59.85) * mm]});
            skFitSpline(sketch, "E3187", {"points": [v(262.1, -59.72) * mm, v(262.3, -59.78) * mm, v(262.52, -59.7) * mm, v(262.64, -59.53) * mm]});
            skFitSpline(sketch, "E3188", {"points": [v(262.64, -59.53) * mm, v(262.76, -59.35) * mm, v(262.76, -59.13) * mm, v(262.64, -58.95) * mm]});
            skFitSpline(sketch, "E3189", {"points": [v(262.64, -58.95) * mm, v(262.52, -58.78) * mm, v(262.3, -58.7) * mm, v(262.1, -58.76) * mm]});
            skFitSpline(sketch, "E3190", {"points": [v(261.62, -58.63) * mm, v(261.75, -58.75) * mm, v(261.93, -58.8) * mm, v(262.1, -58.76) * mm]});
            skLineSegment(sketch, "E3191", {"start": v(265.86, -64.1) * mm, "end": v(264.7, -65.25) * mm});
            skFitSpline(sketch, "E3192", {"points": [v(251.97, -48.62) * mm, v(251.92, -48.8) * mm, v(251.97, -48.98) * mm, v(252.1, -49.1) * mm]});
            skFitSpline(sketch, "E3193", {"points": [v(251.97, -48.62) * mm, v(252.02, -48.42) * mm, v(251.94, -48.2) * mm, v(251.77, -48.08) * mm]});
            skFitSpline(sketch, "E3194", {"points": [v(251.77, -48.08) * mm, v(251.6, -47.96) * mm, v(251.37, -47.96) * mm, v(251.2, -48.08) * mm]});
            skFitSpline(sketch, "E3195", {"points": [v(251.2, -48.08) * mm, v(251.03, -48.2) * mm, v(250.95, -48.42) * mm, v(251, -48.62) * mm]});
            skFitSpline(sketch, "E3196", {"points": [v(250.87, -49.1) * mm, v(251, -48.98) * mm, v(251.05, -48.8) * mm, v(251, -48.62) * mm]});
            skLineSegment(sketch, "E3197", {"start": v(264, -65.25) * mm, "end": v(260.46, -61.72) * mm});
            skFitSpline(sketch, "E3198", {"points": [v(249, -50.26) * mm, v(249.1, -50.35) * mm, v(249.23, -50.4) * mm, v(249.36, -50.4) * mm]});
            skFitSpline(sketch, "E3199", {"points": [v(249.36, -50.4) * mm, v(249.5, -50.4) * mm, v(249.62, -50.35) * mm, v(249.72, -50.26) * mm]});
            skLineSegment(sketch, "E3200", {"start": v(260.46, -61) * mm, "end": v(261.62, -59.85) * mm});
            skFitSpline(sketch, "E3201", {"points": [v(245.47, -46.02) * mm, v(245.28, -46.21) * mm, v(245.28, -46.53) * mm, v(245.47, -46.72) * mm]});
            skLineSegment(sketch, "E3202", {"start": v(261.62, -58.63) * mm, "end": v(257.99, -55) * mm});
            skLineSegment(sketch, "E3203", {"start": v(257.99, -55) * mm, "end": v(260.11, -52.88) * mm});
            skLineSegment(sketch, "E3204", {"start": v(260.11, -52.88) * mm, "end": v(261.01, -53.78) * mm});
            skLineSegment(sketch, "E3205", {"start": v(261.01, -53.78) * mm, "end": v(263.84, -50.95) * mm});
            skLineSegment(sketch, "E3206", {"start": v(263.84, -50.95) * mm, "end": v(262.94, -50.05) * mm});
            skLineSegment(sketch, "E3207", {"start": v(262.94, -50.05) * mm, "end": v(265.06, -47.93) * mm});
            skLineSegment(sketch, "E3208", {"start": v(265.06, -47.93) * mm, "end": v(262.8, -45.66) * mm});
            skLineSegment(sketch, "E3209", {"start": v(262.8, -45.66) * mm, "end": v(260.68, -47.79) * mm});
            skLineSegment(sketch, "E3210", {"start": v(260.68, -47.79) * mm, "end": v(259.78, -46.88) * mm});
            skLineSegment(sketch, "E3211", {"start": v(259.78, -46.88) * mm, "end": v(256.95, -49.71) * mm});
            skLineSegment(sketch, "E3212", {"start": v(256.95, -49.71) * mm, "end": v(257.85, -50.61) * mm});
            skLineSegment(sketch, "E3213", {"start": v(257.85, -50.61) * mm, "end": v(255.73, -52.73) * mm});
            skLineSegment(sketch, "E3214", {"start": v(255.73, -52.73) * mm, "end": v(252.1, -49.1) * mm});
            skFitSpline(sketch, "E3215", {"points": [v(247.11, -44.73) * mm, v(246.94, -44.69) * mm, v(246.76, -44.74) * mm, v(246.63, -44.86) * mm]});
            skFitSpline(sketch, "E3216", {"points": [v(247.11, -44.73) * mm, v(247.32, -44.79) * mm, v(247.53, -44.7) * mm, v(247.65, -44.54) * mm]});
            skFitSpline(sketch, "E3217", {"points": [v(247.65, -44.54) * mm, v(247.77, -44.36) * mm, v(247.77, -44.13) * mm, v(247.65, -43.96) * mm]});
            skFitSpline(sketch, "E3218", {"points": [v(247.65, -43.96) * mm, v(247.53, -43.8) * mm, v(247.32, -43.71) * mm, v(247.11, -43.77) * mm]});
            skFitSpline(sketch, "E3219", {"points": [v(246.63, -43.64) * mm, v(246.76, -43.76) * mm, v(246.94, -43.81) * mm, v(247.11, -43.77) * mm]});
            skLineSegment(sketch, "E3220", {"start": v(250.87, -49.1) * mm, "end": v(249.72, -50.26) * mm});
            skLineSegment(sketch, "E3221", {"start": v(249, -50.26) * mm, "end": v(245.47, -46.72) * mm});
            skFitSpline(sketch, "E3222", {"points": [v(-134.18, -164.85) * mm, v(-134.18, -164.67) * mm, v(-134.27, -164.5) * mm, v(-134.43, -164.41) * mm]});
            skFitSpline(sketch, "E3223", {"points": [v(-133.75, -163.73) * mm, v(-133.85, -163.55) * mm, v(-134.06, -163.45) * mm, v(-134.26, -163.49) * mm]});
            skFitSpline(sketch, "E3224", {"points": [v(-134.26, -163.49) * mm, v(-134.47, -163.52) * mm, v(-134.63, -163.69) * mm, v(-134.67, -163.9) * mm]});
            skFitSpline(sketch, "E3225", {"points": [v(-134.67, -163.9) * mm, v(-134.7, -164.1) * mm, v(-134.61, -164.3) * mm, v(-134.43, -164.41) * mm]});
            skFitSpline(sketch, "E3226", {"points": [v(-133.75, -163.73) * mm, v(-133.66, -163.88) * mm, v(-133.5, -163.98) * mm, v(-133.31, -163.98) * mm]});
            skLineSegment(sketch, "E3227", {"start": v(245.47, -46.02) * mm, "end": v(246.63, -44.86) * mm});
            skFitSpline(sketch, "E3228", {"points": [v(-131.68, -163.98) * mm, v(-131.55, -163.98) * mm, v(-131.42, -163.93) * mm, v(-131.32, -163.83) * mm]});
            skFitSpline(sketch, "E3229", {"points": [v(-131.32, -163.83) * mm, v(-131.23, -163.74) * mm, v(-131.18, -163.61) * mm, v(-131.18, -163.48) * mm]});
            skLineSegment(sketch, "E3230", {"start": v(246.63, -43.64) * mm, "end": v(239.46, -36.47) * mm});
            skFitSpline(sketch, "E3231", {"points": [v(-131.18, -158.48) * mm, v(-131.18, -158.35) * mm, v(-131.23, -158.22) * mm, v(-131.32, -158.13) * mm]});
            skFitSpline(sketch, "E3232", {"points": [v(-131.32, -158.13) * mm, v(-131.42, -158.03) * mm, v(-131.55, -157.98) * mm, v(-131.68, -157.98) * mm]});
            skLineSegment(sketch, "E3233", {"start": v(-144.18, -173.18) * mm, "end": v(-144.18, -169.98) * mm});
            skLineSegment(sketch, "E3234", {"start": v(-144.18, -169.98) * mm, "end": v(-141.18, -169.98) * mm});
            skLineSegment(sketch, "E3235", {"start": v(-141.18, -169.98) * mm, "end": v(-141.18, -168.7) * mm});
            skLineSegment(sketch, "E3236", {"start": v(-141.18, -168.7) * mm, "end": v(-137.18, -168.7) * mm});
            skLineSegment(sketch, "E3237", {"start": v(-137.18, -168.7) * mm, "end": v(-137.18, -169.98) * mm});
            skLineSegment(sketch, "E3238", {"start": v(-137.18, -169.98) * mm, "end": v(-134.18, -169.98) * mm});
            skLineSegment(sketch, "E3239", {"start": v(-134.18, -169.98) * mm, "end": v(-134.18, -164.85) * mm});
            skFitSpline(sketch, "E3240", {"points": [v(-133.31, -157.98) * mm, v(-133.5, -157.98) * mm, v(-133.66, -158.07) * mm, v(-133.75, -158.23) * mm]});
            skFitSpline(sketch, "E3241", {"points": [v(-134.43, -157.55) * mm, v(-134.61, -157.65) * mm, v(-134.7, -157.86) * mm, v(-134.67, -158.07) * mm]});
            skFitSpline(sketch, "E3242", {"points": [v(-134.67, -158.07) * mm, v(-134.63, -158.27) * mm, v(-134.47, -158.44) * mm, v(-134.26, -158.47) * mm]});
            skFitSpline(sketch, "E3243", {"points": [v(-134.26, -158.47) * mm, v(-134.06, -158.5) * mm, v(-133.85, -158.41) * mm, v(-133.75, -158.23) * mm]});
            skFitSpline(sketch, "E3244", {"points": [v(-134.43, -157.55) * mm, v(-134.27, -157.46) * mm, v(-134.18, -157.3) * mm, v(-134.18, -157.11) * mm]});
            skLineSegment(sketch, "E3245", {"start": v(-133.31, -163.98) * mm, "end": v(-131.68, -163.98) * mm});
            skLineSegment(sketch, "E3246", {"start": v(-131.18, -163.48) * mm, "end": v(-131.18, -158.48) * mm});
            skFitSpline(sketch, "E3247", {"points": [v(-180.18, -157.58) * mm, v(-180.7, -157.58) * mm, v(-181.22, -157.8) * mm, v(-181.6, -158.17) * mm]});
            skFitSpline(sketch, "E3248", {"points": [v(-181.6, -158.17) * mm, v(-181.97, -158.54) * mm, v(-182.18, -159.05) * mm, v(-182.18, -159.58) * mm]});
            skLineSegment(sketch, "E3249", {"start": v(-131.68, -157.98) * mm, "end": v(-133.31, -157.98) * mm});
            skFitSpline(sketch, "E3250", {"points": [v(-182.18, -193.58) * mm, v(-182.18, -194.11) * mm, v(-181.97, -194.62) * mm, v(-181.6, -195) * mm]});
            skFitSpline(sketch, "E3251", {"points": [v(-181.6, -195) * mm, v(-181.22, -195.37) * mm, v(-180.7, -195.58) * mm, v(-180.18, -195.58) * mm]});
            skLineSegment(sketch, "E3252", {"start": v(-134.18, -157.11) * mm, "end": v(-134.18, -152.58) * mm});
            skLineSegment(sketch, "E3253", {"start": v(-134.18, -152.58) * mm, "end": v(-139.38, -152.58) * mm});
            skFitSpline(sketch, "E3254", {"points": [v(-134.18, -186.05) * mm, v(-134.18, -185.87) * mm, v(-134.27, -185.7) * mm, v(-134.43, -185.61) * mm]});
            skFitSpline(sketch, "E3255", {"points": [v(-133.75, -184.93) * mm, v(-133.85, -184.75) * mm, v(-134.06, -184.65) * mm, v(-134.26, -184.69) * mm]});
            skFitSpline(sketch, "E3256", {"points": [v(-134.26, -184.69) * mm, v(-134.47, -184.72) * mm, v(-134.63, -184.89) * mm, v(-134.67, -185.1) * mm]});
            skFitSpline(sketch, "E3257", {"points": [v(-134.67, -185.1) * mm, v(-134.7, -185.3) * mm, v(-134.61, -185.5) * mm, v(-134.43, -185.61) * mm]});
            skFitSpline(sketch, "E3258", {"points": [v(-133.75, -184.93) * mm, v(-133.66, -185.08) * mm, v(-133.5, -185.18) * mm, v(-133.31, -185.18) * mm]});
            skLineSegment(sketch, "E3259", {"start": v(-148.69, -157.58) * mm, "end": v(-180.18, -157.58) * mm});
            skFitSpline(sketch, "E3260", {"points": [v(-131.68, -185.18) * mm, v(-131.55, -185.18) * mm, v(-131.42, -185.13) * mm, v(-131.32, -185.03) * mm]});
            skFitSpline(sketch, "E3261", {"points": [v(-131.32, -185.03) * mm, v(-131.23, -184.94) * mm, v(-131.18, -184.81) * mm, v(-131.18, -184.68) * mm]});
            skLineSegment(sketch, "E3262", {"start": v(-182.18, -159.58) * mm, "end": v(-182.18, -193.58) * mm});
            skFitSpline(sketch, "E3263", {"points": [v(-131.18, -179.68) * mm, v(-131.18, -179.55) * mm, v(-131.23, -179.42) * mm, v(-131.32, -179.33) * mm]});
            skFitSpline(sketch, "E3264", {"points": [v(-131.32, -179.33) * mm, v(-131.42, -179.23) * mm, v(-131.55, -179.18) * mm, v(-131.68, -179.18) * mm]});
            skLineSegment(sketch, "E3265", {"start": v(-180.18, -195.58) * mm, "end": v(-143.15, -195.58) * mm});
            skFitSpline(sketch, "E3266", {"points": [v(-133.31, -179.18) * mm, v(-133.5, -179.18) * mm, v(-133.66, -179.27) * mm, v(-133.75, -179.43) * mm]});
            skFitSpline(sketch, "E3267", {"points": [v(-134.43, -178.75) * mm, v(-134.61, -178.85) * mm, v(-134.7, -179.06) * mm, v(-134.67, -179.27) * mm]});
            skFitSpline(sketch, "E3268", {"points": [v(-134.67, -179.27) * mm, v(-134.63, -179.47) * mm, v(-134.47, -179.64) * mm, v(-134.26, -179.67) * mm]});
            skFitSpline(sketch, "E3269", {"points": [v(-134.26, -179.67) * mm, v(-134.06, -179.7) * mm, v(-133.85, -179.61) * mm, v(-133.75, -179.43) * mm]});
            skFitSpline(sketch, "E3270", {"points": [v(-134.43, -178.75) * mm, v(-134.27, -178.66) * mm, v(-134.18, -178.5) * mm, v(-134.18, -178.31) * mm]});
            skLineSegment(sketch, "E3271", {"start": v(-133.31, -185.18) * mm, "end": v(-131.68, -185.18) * mm});
            skFitSpline(sketch, "E3272", {"points": [v(-150.86, -176.58) * mm, v(-150.86, -172.61) * mm, v(-152.97, -168.94) * mm, v(-156.4, -166.96) * mm]});
            skFitSpline(sketch, "E3273", {"points": [v(-156.4, -166.96) * mm, v(-159.85, -164.98) * mm, v(-164.08, -164.98) * mm, v(-167.51, -166.96) * mm]});
            skFitSpline(sketch, "E3274", {"points": [v(-167.51, -166.96) * mm, v(-170.95, -168.94) * mm, v(-173.06, -172.61) * mm, v(-173.06, -176.58) * mm]});
            skFitSpline(sketch, "E3275", {"points": [v(-173.06, -176.58) * mm, v(-173.06, -180.55) * mm, v(-170.95, -184.21) * mm, v(-167.51, -186.2) * mm]});
            skFitSpline(sketch, "E3276", {"points": [v(-167.51, -186.2) * mm, v(-164.08, -188.18) * mm, v(-159.85, -188.18) * mm, v(-156.4, -186.2) * mm]});
            skFitSpline(sketch, "E3277", {"points": [v(-156.4, -186.2) * mm, v(-152.97, -184.21) * mm, v(-150.86, -180.55) * mm, v(-150.86, -176.58) * mm]});
            skLineSegment(sketch, "E3278", {"start": v(-131.18, -184.68) * mm, "end": v(-131.18, -179.68) * mm});
            skFitSpline(sketch, "E3279", {"points": [v(-144.86, -192.08) * mm, v(-144.86, -191.5) * mm, v(-145.17, -190.98) * mm, v(-145.66, -190.7) * mm]});
            skFitSpline(sketch, "E3280", {"points": [v(-145.66, -190.7) * mm, v(-146.16, -190.4) * mm, v(-146.77, -190.4) * mm, v(-147.26, -190.7) * mm]});
            skFitSpline(sketch, "E3281", {"points": [v(-147.26, -190.7) * mm, v(-147.76, -190.98) * mm, v(-148.06, -191.5) * mm, v(-148.06, -192.08) * mm]});
            skFitSpline(sketch, "E3282", {"points": [v(-148.06, -192.08) * mm, v(-148.06, -192.65) * mm, v(-147.76, -193.18) * mm, v(-147.26, -193.47) * mm]});
            skFitSpline(sketch, "E3283", {"points": [v(-147.26, -193.47) * mm, v(-146.77, -193.75) * mm, v(-146.16, -193.75) * mm, v(-145.66, -193.47) * mm]});
            skFitSpline(sketch, "E3284", {"points": [v(-145.66, -193.47) * mm, v(-145.17, -193.18) * mm, v(-144.86, -192.65) * mm, v(-144.86, -192.08) * mm]});
            skLineSegment(sketch, "E3285", {"start": v(-131.68, -179.18) * mm, "end": v(-133.31, -179.18) * mm});
            skFitSpline(sketch, "E3286", {"points": [v(-175.86, -192.08) * mm, v(-175.86, -191.5) * mm, v(-176.17, -190.98) * mm, v(-176.66, -190.7) * mm]});
            skFitSpline(sketch, "E3287", {"points": [v(-176.66, -190.7) * mm, v(-177.16, -190.4) * mm, v(-177.77, -190.4) * mm, v(-178.26, -190.7) * mm]});
            skFitSpline(sketch, "E3288", {"points": [v(-178.26, -190.7) * mm, v(-178.76, -190.98) * mm, v(-179.06, -191.5) * mm, v(-179.06, -192.08) * mm]});
            skFitSpline(sketch, "E3289", {"points": [v(-179.06, -192.08) * mm, v(-179.06, -192.65) * mm, v(-178.76, -193.18) * mm, v(-178.26, -193.47) * mm]});
            skFitSpline(sketch, "E3290", {"points": [v(-178.26, -193.47) * mm, v(-177.77, -193.75) * mm, v(-177.16, -193.75) * mm, v(-176.66, -193.47) * mm]});
            skFitSpline(sketch, "E3291", {"points": [v(-176.66, -193.47) * mm, v(-176.17, -193.18) * mm, v(-175.86, -192.65) * mm, v(-175.86, -192.08) * mm]});
            skLineSegment(sketch, "E3292", {"start": v(-134.18, -178.31) * mm, "end": v(-134.18, -173.18) * mm});
            skLineSegment(sketch, "E3293", {"start": v(-134.18, -173.18) * mm, "end": v(-137.18, -173.18) * mm});
            skLineSegment(sketch, "E3294", {"start": v(-137.18, -173.18) * mm, "end": v(-137.18, -174.45) * mm});
            skLineSegment(sketch, "E3295", {"start": v(-137.18, -174.45) * mm, "end": v(-141.18, -174.45) * mm});
            skLineSegment(sketch, "E3296", {"start": v(-141.18, -174.45) * mm, "end": v(-141.18, -173.18) * mm});
            skLineSegment(sketch, "E3297", {"start": v(-141.18, -173.18) * mm, "end": v(-144.18, -173.18) * mm});
            skFitSpline(sketch, "E3298", {"points": [v(-144.86, -161.08) * mm, v(-144.86, -160.5) * mm, v(-145.17, -159.98) * mm, v(-145.66, -159.7) * mm]});
            skFitSpline(sketch, "E3299", {"points": [v(-145.66, -159.7) * mm, v(-146.16, -159.4) * mm, v(-146.77, -159.4) * mm, v(-147.26, -159.7) * mm]});
            skFitSpline(sketch, "E3300", {"points": [v(-147.26, -159.7) * mm, v(-147.76, -159.98) * mm, v(-148.06, -160.5) * mm, v(-148.06, -161.08) * mm]});
            skFitSpline(sketch, "E3301", {"points": [v(-148.06, -161.08) * mm, v(-148.06, -161.65) * mm, v(-147.76, -162.18) * mm, v(-147.26, -162.47) * mm]});
            skFitSpline(sketch, "E3302", {"points": [v(-147.26, -162.47) * mm, v(-146.77, -162.75) * mm, v(-146.16, -162.75) * mm, v(-145.66, -162.47) * mm]});
            skFitSpline(sketch, "E3303", {"points": [v(-145.66, -162.47) * mm, v(-145.17, -162.18) * mm, v(-144.86, -161.65) * mm, v(-144.86, -161.08) * mm]});
            skFitSpline(sketch, "E3304", {"points": [v(-175.86, -161.08) * mm, v(-175.86, -160.5) * mm, v(-176.17, -159.98) * mm, v(-176.66, -159.7) * mm]});
            skFitSpline(sketch, "E3305", {"points": [v(-176.66, -159.7) * mm, v(-177.16, -159.4) * mm, v(-177.77, -159.4) * mm, v(-178.26, -159.7) * mm]});
            skFitSpline(sketch, "E3306", {"points": [v(-178.26, -159.7) * mm, v(-178.76, -159.98) * mm, v(-179.06, -160.5) * mm, v(-179.06, -161.08) * mm]});
            skFitSpline(sketch, "E3307", {"points": [v(-179.06, -161.08) * mm, v(-179.06, -161.65) * mm, v(-178.76, -162.18) * mm, v(-178.26, -162.47) * mm]});
            skFitSpline(sketch, "E3308", {"points": [v(-178.26, -162.47) * mm, v(-177.77, -162.75) * mm, v(-177.16, -162.75) * mm, v(-176.66, -162.47) * mm]});
            skFitSpline(sketch, "E3309", {"points": [v(-176.66, -162.47) * mm, v(-176.17, -162.18) * mm, v(-175.86, -161.65) * mm, v(-175.86, -161.08) * mm]});
            skFitSpline(sketch, "E3310", {"points": [v(-384.92, 182.95) * mm, v(-385.2, 182.95) * mm, v(-385.42, 182.72) * mm, v(-385.42, 182.45) * mm]});
            skFitSpline(sketch, "E3311", {"points": [v(-379.42, 182.45) * mm, v(-379.42, 182.72) * mm, v(-379.64, 182.95) * mm, v(-379.92, 182.95) * mm]});
            skLineSegment(sketch, "E3312", {"start": v(-134.18, -190.58) * mm, "end": v(-134.18, -186.05) * mm});
            skFitSpline(sketch, "E3313", {"points": [v(-379.67, 180.38) * mm, v(-379.51, 180.47) * mm, v(-379.42, 180.63) * mm, v(-379.42, 180.81) * mm]});
            skFitSpline(sketch, "E3314", {"points": [v(-379.67, 180.38) * mm, v(-379.85, 180.27) * mm, v(-379.95, 180.07) * mm, v(-379.9, 179.86) * mm]});
            skFitSpline(sketch, "E3315", {"points": [v(-379.9, 179.86) * mm, v(-379.87, 179.65) * mm, v(-379.71, 179.49) * mm, v(-379.5, 179.45) * mm]});
            skFitSpline(sketch, "E3316", {"points": [v(-379.5, 179.45) * mm, v(-379.3, 179.42) * mm, v(-379.09, 179.51) * mm, v(-378.98, 179.7) * mm]});
            skFitSpline(sketch, "E3317", {"points": [v(-378.55, 179.95) * mm, v(-378.73, 179.95) * mm, v(-378.9, 179.85) * mm, v(-378.98, 179.7) * mm]});
            skLineSegment(sketch, "E3318", {"start": v(-358.22, 182.45) * mm, "end": v(-358.22, 182.41) * mm});
            skFitSpline(sketch, "E3319", {"points": [v(-364.65, 179.7) * mm, v(-364.74, 179.85) * mm, v(-364.9, 179.95) * mm, v(-365.08, 179.95) * mm]});
            skFitSpline(sketch, "E3320", {"points": [v(-364.65, 179.7) * mm, v(-364.55, 179.51) * mm, v(-364.34, 179.42) * mm, v(-364.13, 179.45) * mm]});
            skFitSpline(sketch, "E3321", {"points": [v(-364.13, 179.45) * mm, v(-363.92, 179.49) * mm, v(-363.76, 179.65) * mm, v(-363.72, 179.86) * mm]});
            skFitSpline(sketch, "E3322", {"points": [v(-363.72, 179.86) * mm, v(-363.69, 180.07) * mm, v(-363.79, 180.27) * mm, v(-363.97, 180.38) * mm]});
            skFitSpline(sketch, "E3323", {"points": [v(-364.22, 180.81) * mm, v(-364.22, 180.63) * mm, v(-364.12, 180.47) * mm, v(-363.97, 180.38) * mm]});
            skLineSegment(sketch, "E3324", {"start": v(-384.92, 182.95) * mm, "end": v(-379.92, 182.95) * mm});
            skFitSpline(sketch, "E3325", {"points": [v(-363.72, 182.95) * mm, v(-364, 182.95) * mm, v(-364.22, 182.72) * mm, v(-364.22, 182.45) * mm]});
            skLineSegment(sketch, "E3326", {"start": v(-379.42, 182.45) * mm, "end": v(-379.42, 180.81) * mm});
            skFitSpline(sketch, "E3327", {"points": [v(-358.22, 182.45) * mm, v(-358.22, 182.72) * mm, v(-358.44, 182.95) * mm, v(-358.72, 182.95) * mm]});
            skFitSpline(sketch, "E3328", {"points": [v(-370.22, 128.95) * mm, v(-370.22, 129.52) * mm, v(-370.52, 130.05) * mm, v(-371.02, 130.33) * mm]});
            skFitSpline(sketch, "E3329", {"points": [v(-371.02, 130.33) * mm, v(-371.51, 130.62) * mm, v(-372.12, 130.62) * mm, v(-372.62, 130.33) * mm]});
            skFitSpline(sketch, "E3330", {"points": [v(-372.62, 130.33) * mm, v(-373.11, 130.05) * mm, v(-373.42, 129.52) * mm, v(-373.42, 128.95) * mm]});
            skFitSpline(sketch, "E3331", {"points": [v(-373.42, 128.95) * mm, v(-373.42, 128.37) * mm, v(-373.11, 127.84) * mm, v(-372.62, 127.56) * mm]});
            skFitSpline(sketch, "E3332", {"points": [v(-372.62, 127.56) * mm, v(-372.12, 127.27) * mm, v(-371.51, 127.27) * mm, v(-371.02, 127.56) * mm]});
            skFitSpline(sketch, "E3333", {"points": [v(-371.02, 127.56) * mm, v(-370.52, 127.84) * mm, v(-370.22, 128.37) * mm, v(-370.22, 128.95) * mm]});
            skLineSegment(sketch, "E3334", {"start": v(-378.55, 179.95) * mm, "end": v(-373.42, 179.95) * mm});
            skLineSegment(sketch, "E3335", {"start": v(-373.42, 179.95) * mm, "end": v(-373.42, 176.95) * mm});
            skLineSegment(sketch, "E3336", {"start": v(-373.42, 176.95) * mm, "end": v(-374.7, 176.95) * mm});
            skLineSegment(sketch, "E3337", {"start": v(-374.7, 176.95) * mm, "end": v(-374.7, 172.95) * mm});
            skLineSegment(sketch, "E3338", {"start": v(-374.7, 172.95) * mm, "end": v(-373.42, 172.95) * mm});
            skLineSegment(sketch, "E3339", {"start": v(-373.42, 172.95) * mm, "end": v(-373.42, 169.95) * mm});
            skLineSegment(sketch, "E3340", {"start": v(-373.42, 169.95) * mm, "end": v(-370.22, 169.95) * mm});
            skLineSegment(sketch, "E3341", {"start": v(-370.22, 169.95) * mm, "end": v(-370.22, 172.95) * mm});
            skLineSegment(sketch, "E3342", {"start": v(-370.22, 172.95) * mm, "end": v(-368.94, 172.95) * mm});
            skLineSegment(sketch, "E3343", {"start": v(-368.94, 172.95) * mm, "end": v(-368.94, 176.95) * mm});
            skLineSegment(sketch, "E3344", {"start": v(-368.94, 176.95) * mm, "end": v(-370.22, 176.95) * mm});
            skLineSegment(sketch, "E3345", {"start": v(-370.22, 176.95) * mm, "end": v(-370.22, 179.95) * mm});
            skLineSegment(sketch, "E3346", {"start": v(-370.22, 179.95) * mm, "end": v(-365.08, 179.95) * mm});
            skLineSegment(sketch, "E3347", {"start": v(-364.22, 180.81) * mm, "end": v(-364.22, 182.45) * mm});
            skFitSpline(sketch, "E3348", {"points": [v(325.91, 153.65) * mm, v(326.54, 153.65) * mm, v(327.12, 153.98) * mm, v(327.43, 154.52) * mm]});
            skFitSpline(sketch, "E3349", {"points": [v(327.43, 154.52) * mm, v(327.74, 155.07) * mm, v(327.74, 155.73) * mm, v(327.43, 156.27) * mm]});
            skFitSpline(sketch, "E3350", {"points": [v(327.43, 156.27) * mm, v(327.12, 156.82) * mm, v(326.54, 157.15) * mm, v(325.91, 157.15) * mm]});
            skFitSpline(sketch, "E3351", {"points": [v(325.91, 157.15) * mm, v(325.29, 157.15) * mm, v(324.71, 156.82) * mm, v(324.4, 156.27) * mm]});
            skFitSpline(sketch, "E3352", {"points": [v(324.4, 156.27) * mm, v(324.09, 155.73) * mm, v(324.09, 155.07) * mm, v(324.4, 154.52) * mm]});
            skFitSpline(sketch, "E3353", {"points": [v(324.4, 154.52) * mm, v(324.71, 153.98) * mm, v(325.29, 153.65) * mm, v(325.91, 153.65) * mm]});
            skLineSegment(sketch, "E3354", {"start": v(-363.72, 182.95) * mm, "end": v(-358.72, 182.95) * mm});
            skFitSpline(sketch, "E3355", {"points": [v(225.91, 153.65) * mm, v(226.54, 153.65) * mm, v(227.12, 153.98) * mm, v(227.43, 154.52) * mm]});
            skFitSpline(sketch, "E3356", {"points": [v(227.43, 154.52) * mm, v(227.74, 155.07) * mm, v(227.74, 155.73) * mm, v(227.43, 156.27) * mm]});
            skFitSpline(sketch, "E3357", {"points": [v(227.43, 156.27) * mm, v(227.12, 156.82) * mm, v(226.54, 157.15) * mm, v(225.91, 157.15) * mm]});
            skFitSpline(sketch, "E3358", {"points": [v(225.91, 157.15) * mm, v(225.29, 157.15) * mm, v(224.71, 156.82) * mm, v(224.4, 156.27) * mm]});
            skFitSpline(sketch, "E3359", {"points": [v(224.4, 156.27) * mm, v(224.09, 155.73) * mm, v(224.09, 155.07) * mm, v(224.4, 154.52) * mm]});
            skFitSpline(sketch, "E3360", {"points": [v(224.4, 154.52) * mm, v(224.71, 153.98) * mm, v(225.29, 153.65) * mm, v(225.91, 153.65) * mm]});
            skFitSpline(sketch, "E3361", {"points": [v(-18.99, -182.45) * mm, v(-18.98, -103.9) * mm, v(-18.98, -25.34) * mm, v(-18.97, 53.21) * mm]});
            skFitSpline(sketch, "E3362", {"points": [v(-18.97, 53.21) * mm, v(-18.96, 53.38) * mm, v(-18.87, 53.53) * mm, v(-18.7, 53.61) * mm]});
            skFitSpline(sketch, "E3363", {"points": [v(-18.7, 53.61) * mm, v(-18.53, 53.72) * mm, v(-18.43, 53.93) * mm, v(-18.47, 54.13) * mm]});
            skFitSpline(sketch, "E3364", {"points": [v(-18.47, 54.13) * mm, v(-18.5, 54.34) * mm, v(-18.67, 54.5) * mm, v(-18.87, 54.54) * mm]});
            skFitSpline(sketch, "E3365", {"points": [v(-18.87, 54.54) * mm, v(-19.08, 54.58) * mm, v(-19.29, 54.48) * mm, v(-19.4, 54.3) * mm]});
            skFitSpline(sketch, "E3366", {"points": [v(-19.4, 54.3) * mm, v(-19.48, 54.14) * mm, v(-19.65, 54.05) * mm, v(-19.83, 54.05) * mm]});
            skFitSpline(sketch, "E3367", {"points": [v(7.71, -182.95) * mm, v(7.85, -182.95) * mm, v(7.97, -182.9) * mm, v(8.07, -182.8) * mm]});
            skFitSpline(sketch, "E3368", {"points": [v(8.07, -182.8) * mm, v(8.16, -182.71) * mm, v(8.21, -182.58) * mm, v(8.21, -182.45) * mm]});
            skLineSegment(sketch, "E3369", {"start": v(-19.83, 54.05) * mm, "end": v(-30.9, 54.05) * mm});
            skFitSpline(sketch, "E3370", {"points": [v(2.21, -182.45) * mm, v(2.21, -182.73) * mm, v(2.44, -182.95) * mm, v(2.71, -182.95) * mm]});
            skFitSpline(sketch, "E3371", {"points": [v(2.46, -180.38) * mm, v(2.3, -180.47) * mm, v(2.21, -180.64) * mm, v(2.21, -180.82) * mm]});
            skFitSpline(sketch, "E3372", {"points": [v(2.46, -180.38) * mm, v(2.65, -180.28) * mm, v(2.74, -180.07) * mm, v(2.7, -179.86) * mm]});
            skFitSpline(sketch, "E3373", {"points": [v(2.7, -179.86) * mm, v(2.67, -179.66) * mm, v(2.5, -179.5) * mm, v(2.3, -179.46) * mm]});
            skFitSpline(sketch, "E3374", {"points": [v(2.3, -179.46) * mm, v(2.1, -179.42) * mm, v(1.89, -179.52) * mm, v(1.78, -179.7) * mm]});
            skFitSpline(sketch, "E3375", {"points": [v(1.35, -179.95) * mm, v(1.53, -179.95) * mm, v(1.7, -179.86) * mm, v(1.78, -179.7) * mm]});
            skFitSpline(sketch, "E3376", {"points": [v(-12.55, -179.7) * mm, v(-12.46, -179.86) * mm, v(-12.3, -179.95) * mm, v(-12.12, -179.95) * mm]});
            skFitSpline(sketch, "E3377", {"points": [v(-12.55, -179.7) * mm, v(-12.66, -179.52) * mm, v(-12.87, -179.42) * mm, v(-13.07, -179.46) * mm]});
            skFitSpline(sketch, "E3378", {"points": [v(-13.07, -179.46) * mm, v(-13.28, -179.5) * mm, v(-13.44, -179.66) * mm, v(-13.48, -179.86) * mm]});
            skFitSpline(sketch, "E3379", {"points": [v(-13.48, -179.86) * mm, v(-13.52, -180.07) * mm, v(-13.42, -180.28) * mm, v(-13.24, -180.38) * mm]});
            skFitSpline(sketch, "E3380", {"points": [v(-12.99, -180.82) * mm, v(-12.99, -180.64) * mm, v(-13.08, -180.47) * mm, v(-13.24, -180.38) * mm]});
            skLineSegment(sketch, "E3381", {"start": v(7.71, -182.95) * mm, "end": v(2.71, -182.95) * mm});
            skFitSpline(sketch, "E3382", {"points": [v(-13.49, -182.95) * mm, v(-13.21, -182.95) * mm, v(-12.99, -182.73) * mm, v(-12.99, -182.45) * mm]});
            skLineSegment(sketch, "E3383", {"start": v(2.21, -182.45) * mm, "end": v(2.21, -180.82) * mm});
            skFitSpline(sketch, "E3384", {"points": [v(-18.99, -182.45) * mm, v(-18.99, -182.73) * mm, v(-18.76, -182.95) * mm, v(-18.49, -182.95) * mm]});
            skFitSpline(sketch, "E3385", {"points": [v(-3.86, -128.95) * mm, v(-3.86, -128.38) * mm, v(-4.16, -127.85) * mm, v(-4.66, -127.56) * mm]});
            skFitSpline(sketch, "E3386", {"points": [v(-4.66, -127.56) * mm, v(-5.15, -127.28) * mm, v(-5.76, -127.28) * mm, v(-6.26, -127.56) * mm]});
            skFitSpline(sketch, "E3387", {"points": [v(-6.26, -127.56) * mm, v(-6.75, -127.85) * mm, v(-7.06, -128.38) * mm, v(-7.06, -128.95) * mm]});
            skFitSpline(sketch, "E3388", {"points": [v(-7.06, -128.95) * mm, v(-7.06, -129.52) * mm, v(-6.75, -130.05) * mm, v(-6.26, -130.34) * mm]});
            skFitSpline(sketch, "E3389", {"points": [v(-6.26, -130.34) * mm, v(-5.76, -130.62) * mm, v(-5.15, -130.62) * mm, v(-4.66, -130.34) * mm]});
            skFitSpline(sketch, "E3390", {"points": [v(-4.66, -130.34) * mm, v(-4.16, -130.05) * mm, v(-3.86, -129.52) * mm, v(-3.86, -128.95) * mm]});
            skLineSegment(sketch, "E3391", {"start": v(1.35, -179.95) * mm, "end": v(-3.79, -179.95) * mm});
            skLineSegment(sketch, "E3392", {"start": v(-3.79, -179.95) * mm, "end": v(-3.79, -176.95) * mm});
            skLineSegment(sketch, "E3393", {"start": v(-3.79, -176.95) * mm, "end": v(-2.51, -176.95) * mm});
            skLineSegment(sketch, "E3394", {"start": v(-2.51, -176.95) * mm, "end": v(-2.51, -172.95) * mm});
            skLineSegment(sketch, "E3395", {"start": v(-2.51, -172.95) * mm, "end": v(-3.79, -172.95) * mm});
            skLineSegment(sketch, "E3396", {"start": v(-3.79, -172.95) * mm, "end": v(-3.79, -169.95) * mm});
            skLineSegment(sketch, "E3397", {"start": v(-3.79, -169.95) * mm, "end": v(-6.99, -169.95) * mm});
            skLineSegment(sketch, "E3398", {"start": v(-6.99, -169.95) * mm, "end": v(-6.99, -172.95) * mm});
            skLineSegment(sketch, "E3399", {"start": v(-6.99, -172.95) * mm, "end": v(-8.26, -172.95) * mm});
            skLineSegment(sketch, "E3400", {"start": v(-8.26, -172.95) * mm, "end": v(-8.26, -176.95) * mm});
            skLineSegment(sketch, "E3401", {"start": v(-8.26, -176.95) * mm, "end": v(-6.99, -176.95) * mm});
            skLineSegment(sketch, "E3402", {"start": v(-6.99, -176.95) * mm, "end": v(-6.99, -179.95) * mm});
            skLineSegment(sketch, "E3403", {"start": v(-6.99, -179.95) * mm, "end": v(-12.12, -179.95) * mm});
            skLineSegment(sketch, "E3404", {"start": v(-12.99, -180.82) * mm, "end": v(-12.99, -182.45) * mm});
            skLineSegment(sketch, "E3405", {"start": v(-13.49, -182.95) * mm, "end": v(-18.49, -182.95) * mm});
            skFitSpline(sketch, "E3406", {"points": [v(125.91, 153.65) * mm, v(126.54, 153.65) * mm, v(127.12, 153.98) * mm, v(127.43, 154.52) * mm]});
            skFitSpline(sketch, "E3407", {"points": [v(127.43, 154.52) * mm, v(127.74, 155.07) * mm, v(127.74, 155.73) * mm, v(127.43, 156.27) * mm]});
            skFitSpline(sketch, "E3408", {"points": [v(127.43, 156.27) * mm, v(127.12, 156.82) * mm, v(126.54, 157.15) * mm, v(125.91, 157.15) * mm]});
            skFitSpline(sketch, "E3409", {"points": [v(125.91, 157.15) * mm, v(125.29, 157.15) * mm, v(124.71, 156.82) * mm, v(124.4, 156.27) * mm]});
            skFitSpline(sketch, "E3410", {"points": [v(124.4, 156.27) * mm, v(124.09, 155.73) * mm, v(124.09, 155.07) * mm, v(124.4, 154.52) * mm]});
            skFitSpline(sketch, "E3411", {"points": [v(124.4, 154.52) * mm, v(124.71, 153.98) * mm, v(125.29, 153.65) * mm, v(125.91, 153.65) * mm]});
            skFitSpline(sketch, "E3412", {"points": [v(50.91, 153.65) * mm, v(51.54, 153.65) * mm, v(52.12, 153.98) * mm, v(52.43, 154.52) * mm]});
            skFitSpline(sketch, "E3413", {"points": [v(52.43, 154.52) * mm, v(52.74, 155.07) * mm, v(52.74, 155.73) * mm, v(52.43, 156.27) * mm]});
            skFitSpline(sketch, "E3414", {"points": [v(52.43, 156.27) * mm, v(52.12, 156.82) * mm, v(51.54, 157.15) * mm, v(50.91, 157.15) * mm]});
            skFitSpline(sketch, "E3415", {"points": [v(50.91, 157.15) * mm, v(50.29, 157.15) * mm, v(49.71, 156.82) * mm, v(49.4, 156.27) * mm]});
            skFitSpline(sketch, "E3416", {"points": [v(49.4, 156.27) * mm, v(49.09, 155.73) * mm, v(49.09, 155.07) * mm, v(49.4, 154.52) * mm]});
            skFitSpline(sketch, "E3417", {"points": [v(49.4, 154.52) * mm, v(49.71, 153.98) * mm, v(50.29, 153.65) * mm, v(50.91, 153.65) * mm]});
            skFitSpline(sketch, "E3418", {"points": [v(325.91, -176.95) * mm, v(326.88, -176.95) * mm, v(327.66, -176.16) * mm, v(327.66, -175.2) * mm]});
            skFitSpline(sketch, "E3419", {"points": [v(327.66, -175.2) * mm, v(327.66, -174.23) * mm, v(326.88, -173.45) * mm, v(325.91, -173.45) * mm]});
            skFitSpline(sketch, "E3420", {"points": [v(325.91, -173.45) * mm, v(325.29, -173.45) * mm, v(324.71, -173.78) * mm, v(324.4, -174.32) * mm]});
            skFitSpline(sketch, "E3421", {"points": [v(324.4, -174.32) * mm, v(324.08, -174.86) * mm, v(324.08, -175.53) * mm, v(324.4, -176.07) * mm]});
            skFitSpline(sketch, "E3422", {"points": [v(324.4, -176.07) * mm, v(324.71, -176.61) * mm, v(325.29, -176.95) * mm, v(325.91, -176.95) * mm]});
            skFitSpline(sketch, "E3423", {"points": [v(225.91, -176.95) * mm, v(226.88, -176.95) * mm, v(227.66, -176.16) * mm, v(227.66, -175.2) * mm]});
            skFitSpline(sketch, "E3424", {"points": [v(227.66, -175.2) * mm, v(227.66, -174.23) * mm, v(226.88, -173.45) * mm, v(225.91, -173.45) * mm]});
            skFitSpline(sketch, "E3425", {"points": [v(225.91, -173.45) * mm, v(225.29, -173.45) * mm, v(224.71, -173.78) * mm, v(224.4, -174.32) * mm]});
            skFitSpline(sketch, "E3426", {"points": [v(224.4, -174.32) * mm, v(224.08, -174.86) * mm, v(224.08, -175.53) * mm, v(224.4, -176.07) * mm]});
            skFitSpline(sketch, "E3427", {"points": [v(224.4, -176.07) * mm, v(224.71, -176.61) * mm, v(225.29, -176.95) * mm, v(225.91, -176.95) * mm]});
            skFitSpline(sketch, "E3428", {"points": [v(125.91, -176.95) * mm, v(126.88, -176.95) * mm, v(127.66, -176.16) * mm, v(127.66, -175.2) * mm]});
            skFitSpline(sketch, "E3429", {"points": [v(127.66, -175.2) * mm, v(127.66, -174.23) * mm, v(126.88, -173.45) * mm, v(125.91, -173.45) * mm]});
            skFitSpline(sketch, "E3430", {"points": [v(125.91, -173.45) * mm, v(125.29, -173.45) * mm, v(124.71, -173.78) * mm, v(124.4, -174.32) * mm]});
            skFitSpline(sketch, "E3431", {"points": [v(124.4, -174.32) * mm, v(124.08, -174.86) * mm, v(124.08, -175.53) * mm, v(124.4, -176.07) * mm]});
            skFitSpline(sketch, "E3432", {"points": [v(124.4, -176.07) * mm, v(124.71, -176.61) * mm, v(125.29, -176.95) * mm, v(125.91, -176.95) * mm]});
            skFitSpline(sketch, "E3433", {"points": [v(50.91, -176.95) * mm, v(51.88, -176.95) * mm, v(52.66, -176.16) * mm, v(52.66, -175.2) * mm]});
            skFitSpline(sketch, "E3434", {"points": [v(52.66, -175.2) * mm, v(52.66, -174.23) * mm, v(51.88, -173.45) * mm, v(50.91, -173.45) * mm]});
            skFitSpline(sketch, "E3435", {"points": [v(50.91, -173.45) * mm, v(50.29, -173.45) * mm, v(49.71, -173.78) * mm, v(49.4, -174.32) * mm]});
            skFitSpline(sketch, "E3436", {"points": [v(49.4, -174.32) * mm, v(49.08, -174.86) * mm, v(49.08, -175.53) * mm, v(49.4, -176.07) * mm]});
            skFitSpline(sketch, "E3437", {"points": [v(49.4, -176.07) * mm, v(49.71, -176.61) * mm, v(50.29, -176.95) * mm, v(50.91, -176.95) * mm]});
            skFitSpline(sketch, "E3438", {"points": [v(143.2, -102.6) * mm, v(142.08, -101.47) * mm, v(140.55, -100.83) * mm, v(138.96, -100.83) * mm]});
            skFitSpline(sketch, "E3439", {"points": [v(289.45, -25.78) * mm, v(289.45, -20.26) * mm, v(293.93, -15.78) * mm, v(299.45, -15.78) * mm]});
            skLineSegment(sketch, "E3440", {"start": v(289.45, -86.35) * mm, "end": v(289.45, -25.78) * mm});
            skFitSpline(sketch, "E3441", {"points": [v(318.95, -15.78) * mm, v(321.68, -15.78) * mm, v(323.9, -13.57) * mm, v(323.9, -10.83) * mm]});
            skFitSpline(sketch, "E3442", {"points": [v(323.9, -10.83) * mm, v(323.9, -8.1) * mm, v(321.68, -5.88) * mm, v(318.95, -5.88) * mm]});
            skLineSegment(sketch, "E3443", {"start": v(299.45, -15.78) * mm, "end": v(318.95, -15.78) * mm});
            skFitSpline(sketch, "E3444", {"points": [v(299.45, -5.88) * mm, v(296.8, -5.88) * mm, v(294.25, -4.83) * mm, v(292.38, -2.96) * mm]});
            skFitSpline(sketch, "E3445", {"points": [v(292.38, -2.96) * mm, v(290.5, -1.08) * mm, v(289.45, 1.46) * mm, v(289.45, 4.12) * mm]});
            skLineSegment(sketch, "E3446", {"start": v(318.95, -5.88) * mm, "end": v(299.45, -5.88) * mm});
            skLineSegment(sketch, "E3447", {"start": v(289.45, 4.12) * mm, "end": v(289.45, 64.68) * mm});
            skFitSpline(sketch, "E3448", {"points": [v(117.7, -90.6) * mm, v(118.82, -89.47) * mm, v(119.45, -87.94) * mm, v(119.45, -86.35) * mm]});
            skLineSegment(sketch, "E3449", {"start": v(157.7, -117.08) * mm, "end": v(143.2, -102.6) * mm});
            skFitSpline(sketch, "E3450", {"points": [v(123.93, -100.83) * mm, v(122.34, -100.83) * mm, v(120.82, -101.47) * mm, v(119.7, -102.6) * mm]});
            skLineSegment(sketch, "E3451", {"start": v(138.96, -100.83) * mm, "end": v(123.93, -100.83) * mm});
            skFitSpline(sketch, "E3452", {"points": [v(103.45, -118.83) * mm, v(101.52, -120.77) * mm, v(98.38, -120.77) * mm, v(96.45, -118.83) * mm]});
            skFitSpline(sketch, "E3453", {"points": [v(96.45, -118.83) * mm, v(94.52, -116.9) * mm, v(94.52, -113.77) * mm, v(96.45, -111.83) * mm]});
            skLineSegment(sketch, "E3454", {"start": v(119.7, -102.6) * mm, "end": v(103.45, -118.83) * mm});
            skFitSpline(sketch, "E3455", {"points": [v(119.45, 64.68) * mm, v(119.45, 66.27) * mm, v(118.82, 67.8) * mm, v(117.7, 68.92) * mm]});
            skLineSegment(sketch, "E3456", {"start": v(96.45, -111.83) * mm, "end": v(117.7, -90.6) * mm});
            skFitSpline(sketch, "E3457", {"points": [v(96.45, 90.17) * mm, v(94.52, 92.1) * mm, v(94.52, 95.23) * mm, v(96.45, 97.17) * mm]});
            skFitSpline(sketch, "E3458", {"points": [v(96.45, 97.17) * mm, v(98.38, 99.1) * mm, v(101.52, 99.1) * mm, v(103.45, 97.17) * mm]});
            skLineSegment(sketch, "E3459", {"start": v(117.7, 68.92) * mm, "end": v(96.45, 90.17) * mm});
            skLineSegment(sketch, "E3460", {"start": v(103.45, 97.17) * mm, "end": v(119.7, 80.92) * mm});
            skFitSpline(sketch, "E3461", {"points": [v(291.2, 68.92) * mm, v(290.08, 67.8) * mm, v(289.45, 66.27) * mm, v(289.45, 64.68) * mm]});
            skLineSegment(sketch, "E3462", {"start": v(119.45, -86.35) * mm, "end": v(119.45, 64.68) * mm});
            skFitSpline(sketch, "E3463", {"points": [v(305.45, 97.17) * mm, v(307.38, 99.1) * mm, v(310.51, 99.1) * mm, v(312.45, 97.17) * mm]});
            skFitSpline(sketch, "E3464", {"points": [v(312.45, 97.17) * mm, v(314.38, 95.23) * mm, v(314.38, 92.1) * mm, v(312.45, 90.17) * mm]});
            skLineSegment(sketch, "E3465", {"start": v(289.2, 80.92) * mm, "end": v(305.45, 97.17) * mm});
            skFitSpline(sketch, "E3466", {"points": [v(269.93, -100.83) * mm, v(268.34, -100.83) * mm, v(266.82, -101.47) * mm, v(265.7, -102.6) * mm]});
            skFitSpline(sketch, "E3467", {"points": [v(246.96, -118.83) * mm, v(248.55, -118.83) * mm, v(250.08, -118.2) * mm, v(251.2, -117.08) * mm]});
            skFitSpline(sketch, "E3468", {"points": [v(225.7, -117.08) * mm, v(226.82, -118.2) * mm, v(228.34, -118.83) * mm, v(229.93, -118.83) * mm]});
            skLineSegment(sketch, "E3469", {"start": v(312.45, 90.17) * mm, "end": v(291.2, 68.92) * mm});
            skFitSpline(sketch, "E3470", {"points": [v(211.2, -102.6) * mm, v(210.08, -101.47) * mm, v(208.55, -100.83) * mm, v(206.96, -100.83) * mm]});
            skLineSegment(sketch, "E3471", {"start": v(284.96, -100.83) * mm, "end": v(269.93, -100.83) * mm});
            skFitSpline(sketch, "E3472", {"points": [v(201.93, -100.83) * mm, v(200.34, -100.83) * mm, v(198.82, -101.47) * mm, v(197.7, -102.6) * mm]});
            skLineSegment(sketch, "E3473", {"start": v(265.7, -102.6) * mm, "end": v(251.2, -117.08) * mm});
            skFitSpline(sketch, "E3474", {"points": [v(178.96, -118.83) * mm, v(180.55, -118.83) * mm, v(182.08, -118.2) * mm, v(183.2, -117.08) * mm]});
            skLineSegment(sketch, "E3475", {"start": v(246.96, -118.83) * mm, "end": v(229.93, -118.83) * mm});
            skFitSpline(sketch, "E3476", {"points": [v(157.7, -117.08) * mm, v(158.82, -118.2) * mm, v(160.34, -118.83) * mm, v(161.93, -118.83) * mm]});
            skLineSegment(sketch, "E3477", {"start": v(225.7, -117.08) * mm, "end": v(211.2, -102.6) * mm});
            skFitSpline(sketch, "E3478", {"points": [v(279.45, 48.03) * mm, v(279.45, 50.7) * mm, v(277.84, 53.1) * mm, v(275.37, 54.13) * mm]});
            skFitSpline(sketch, "E3479", {"points": [v(275.37, 54.13) * mm, v(272.9, 55.15) * mm, v(270.07, 54.59) * mm, v(268.18, 52.7) * mm]});
            skLineSegment(sketch, "E3480", {"start": v(206.96, -100.83) * mm, "end": v(201.93, -100.83) * mm});
            skFitSpline(sketch, "E3481", {"points": [v(268.18, -74.37) * mm, v(270.07, -76.25) * mm, v(272.9, -76.82) * mm, v(275.37, -75.8) * mm]});
            skFitSpline(sketch, "E3482", {"points": [v(275.37, -75.8) * mm, v(277.84, -74.78) * mm, v(279.45, -72.37) * mm, v(279.45, -69.7) * mm]});
            skLineSegment(sketch, "E3483", {"start": v(197.7, -102.6) * mm, "end": v(183.2, -117.08) * mm});
            skFitSpline(sketch, "E3484", {"points": [v(235.45, -38.9) * mm, v(235.45, -40.65) * mm, v(236.14, -42.33) * mm, v(237.38, -43.57) * mm]});
            skLineSegment(sketch, "E3485", {"start": v(178.96, -118.83) * mm, "end": v(161.93, -118.83) * mm});
            skFitSpline(sketch, "E3486", {"points": [v(237.38, 21.9) * mm, v(236.14, 20.66) * mm, v(235.45, 18.98) * mm, v(235.45, 17.23) * mm]});
            skLineSegment(sketch, "E3487", {"start": v(237.38, 21.9) * mm, "end": v(268.18, 52.7) * mm});
            skFitSpline(sketch, "E3488", {"points": [v(179.45, -68.35) * mm, v(179.45, -69.94) * mm, v(180.08, -71.47) * mm, v(181.2, -72.6) * mm]});
            skLineSegment(sketch, "E3489", {"start": v(279.45, 48.03) * mm, "end": v(279.45, -69.7) * mm});
            skFitSpline(sketch, "E3490", {"points": [v(181.2, -49.08) * mm, v(180.08, -50.2) * mm, v(179.45, -51.73) * mm, v(179.45, -53.32) * mm]});
            skLineSegment(sketch, "E3491", {"start": v(268.18, -74.37) * mm, "end": v(237.38, -43.57) * mm});
            skFitSpline(sketch, "E3492", {"points": [v(201.93, -30.83) * mm, v(200.34, -30.83) * mm, v(198.82, -31.47) * mm, v(197.7, -32.6) * mm]});
            skLineSegment(sketch, "E3493", {"start": v(235.45, -38.9) * mm, "end": v(235.45, 17.23) * mm});
            skFitSpline(sketch, "E3494", {"points": [v(211.2, -32.6) * mm, v(210.08, -31.47) * mm, v(208.55, -30.83) * mm, v(206.96, -30.83) * mm]});
            skLineSegment(sketch, "E3495", {"start": v(197.7, -89.08) * mm, "end": v(181.2, -72.6) * mm});
            skFitSpline(sketch, "E3496", {"points": [v(229.45, -53.32) * mm, v(229.45, -51.73) * mm, v(228.82, -50.2) * mm, v(227.7, -49.08) * mm]});
            skLineSegment(sketch, "E3497", {"start": v(179.45, -68.35) * mm, "end": v(179.45, -53.32) * mm});
            skFitSpline(sketch, "E3498", {"points": [v(227.7, -72.6) * mm, v(228.82, -71.47) * mm, v(229.45, -69.94) * mm, v(229.45, -68.35) * mm]});
            skLineSegment(sketch, "E3499", {"start": v(181.2, -49.08) * mm, "end": v(197.7, -32.6) * mm});
            skFitSpline(sketch, "E3500", {"points": [v(206.96, -90.83) * mm, v(208.55, -90.83) * mm, v(210.08, -90.2) * mm, v(211.2, -89.08) * mm]});
            skLineSegment(sketch, "E3501", {"start": v(201.93, -30.83) * mm, "end": v(206.96, -30.83) * mm});
            skFitSpline(sketch, "E3502", {"points": [v(197.7, -89.08) * mm, v(198.82, -90.2) * mm, v(200.34, -90.83) * mm, v(201.93, -90.83) * mm]});
            skLineSegment(sketch, "E3503", {"start": v(211.2, -32.6) * mm, "end": v(227.7, -49.08) * mm});
            skFitSpline(sketch, "E3504", {"points": [v(206.96, 9.17) * mm, v(208.55, 9.17) * mm, v(210.08, 9.8) * mm, v(211.2, 10.92) * mm]});
            skLineSegment(sketch, "E3505", {"start": v(229.45, -53.32) * mm, "end": v(229.45, -68.35) * mm});
            skFitSpline(sketch, "E3506", {"points": [v(197.7, 10.92) * mm, v(198.82, 9.8) * mm, v(200.34, 9.17) * mm, v(201.93, 9.17) * mm]});
            skLineSegment(sketch, "E3507", {"start": v(227.7, -72.6) * mm, "end": v(211.2, -89.08) * mm});
            skFitSpline(sketch, "E3508", {"points": [v(179.45, 31.65) * mm, v(179.45, 30.06) * mm, v(180.08, 28.53) * mm, v(181.2, 27.4) * mm]});
            skFitSpline(sketch, "E3509", {"points": [v(227.7, 27.4) * mm, v(228.82, 28.53) * mm, v(229.45, 30.06) * mm, v(229.45, 31.65) * mm]});
            skLineSegment(sketch, "E3510", {"start": v(206.96, -90.83) * mm, "end": v(201.93, -90.83) * mm});
            skLineSegment(sketch, "E3511", {"start": v(227.7, 27.4) * mm, "end": v(211.2, 10.92) * mm});
            skFitSpline(sketch, "E3512", {"points": [v(181.07, -100.58) * mm, v(180.98, -100.43) * mm, v(180.81, -100.33) * mm, v(180.63, -100.33) * mm]});
            skFitSpline(sketch, "E3513", {"points": [v(181.07, -100.58) * mm, v(181.17, -100.77) * mm, v(181.38, -100.86) * mm, v(181.59, -100.83) * mm]});
            skFitSpline(sketch, "E3514", {"points": [v(181.59, -100.83) * mm, v(181.8, -100.79) * mm, v(181.95, -100.63) * mm, v(182, -100.42) * mm]});
            skFitSpline(sketch, "E3515", {"points": [v(182, -100.42) * mm, v(182.03, -100.21) * mm, v(181.93, -100) * mm, v(181.75, -99.9) * mm]});
            skFitSpline(sketch, "E3516", {"points": [v(181.5, -99.47) * mm, v(181.5, -99.65) * mm, v(181.6, -99.81) * mm, v(181.75, -99.9) * mm]});
            skLineSegment(sketch, "E3517", {"start": v(206.96, 9.17) * mm, "end": v(201.93, 9.17) * mm});
            skFitSpline(sketch, "E3518", {"points": [v(181.75, -91.77) * mm, v(181.6, -91.86) * mm, v(181.5, -92.02) * mm, v(181.5, -92.2) * mm]});
            skFitSpline(sketch, "E3519", {"points": [v(181.75, -91.77) * mm, v(181.93, -91.66) * mm, v(182.03, -91.45) * mm, v(182, -91.25) * mm]});
            skFitSpline(sketch, "E3520", {"points": [v(182, -91.25) * mm, v(181.95, -91.04) * mm, v(181.8, -90.88) * mm, v(181.59, -90.84) * mm]});
            skFitSpline(sketch, "E3521", {"points": [v(181.59, -90.84) * mm, v(181.38, -90.8) * mm, v(181.17, -90.9) * mm, v(181.07, -91.08) * mm]});
            skFitSpline(sketch, "E3522", {"points": [v(180.63, -91.33) * mm, v(180.81, -91.33) * mm, v(180.98, -91.24) * mm, v(181.07, -91.08) * mm]});
            skLineSegment(sketch, "E3523", {"start": v(197.7, 10.92) * mm, "end": v(181.2, 27.4) * mm});
            skFitSpline(sketch, "E3524", {"points": [v(157.83, -91.08) * mm, v(157.92, -91.24) * mm, v(158.09, -91.33) * mm, v(158.26, -91.33) * mm]});
            skFitSpline(sketch, "E3525", {"points": [v(157.83, -91.08) * mm, v(157.73, -90.9) * mm, v(157.52, -90.8) * mm, v(157.31, -90.84) * mm]});
            skFitSpline(sketch, "E3526", {"points": [v(157.31, -90.84) * mm, v(157.1, -90.88) * mm, v(156.94, -91.04) * mm, v(156.9, -91.25) * mm]});
            skFitSpline(sketch, "E3527", {"points": [v(156.9, -91.25) * mm, v(156.87, -91.45) * mm, v(156.97, -91.66) * mm, v(157.15, -91.77) * mm]});
            skFitSpline(sketch, "E3528", {"points": [v(157.4, -92.2) * mm, v(157.4, -92.02) * mm, v(157.3, -91.86) * mm, v(157.15, -91.77) * mm]});
            skLineSegment(sketch, "E3529", {"start": v(251.5, -99.47) * mm, "end": v(251.5, -92.2) * mm});
            skFitSpline(sketch, "E3530", {"points": [v(157.15, -99.9) * mm, v(157.3, -99.81) * mm, v(157.4, -99.65) * mm, v(157.4, -99.47) * mm]});
            skFitSpline(sketch, "E3531", {"points": [v(157.15, -99.9) * mm, v(156.97, -100) * mm, v(156.87, -100.21) * mm, v(156.9, -100.42) * mm]});
            skFitSpline(sketch, "E3532", {"points": [v(156.9, -100.42) * mm, v(156.94, -100.63) * mm, v(157.1, -100.79) * mm, v(157.31, -100.83) * mm]});
            skFitSpline(sketch, "E3533", {"points": [v(157.31, -100.83) * mm, v(157.52, -100.86) * mm, v(157.73, -100.77) * mm, v(157.83, -100.58) * mm]});
            skFitSpline(sketch, "E3534", {"points": [v(158.26, -100.33) * mm, v(158.09, -100.33) * mm, v(157.92, -100.43) * mm, v(157.83, -100.58) * mm]});
            skLineSegment(sketch, "E3535", {"start": v(158.26, -100.33) * mm, "end": v(180.63, -100.33) * mm});
            skFitSpline(sketch, "E3536", {"points": [v(101.55, -115.33) * mm, v(101.55, -114.76) * mm, v(101.24, -114.23) * mm, v(100.75, -113.95) * mm]});
            skFitSpline(sketch, "E3537", {"points": [v(100.75, -113.95) * mm, v(100.25, -113.66) * mm, v(99.64, -113.66) * mm, v(99.15, -113.95) * mm]});
            skFitSpline(sketch, "E3538", {"points": [v(99.15, -113.95) * mm, v(98.65, -114.23) * mm, v(98.35, -114.76) * mm, v(98.35, -115.33) * mm]});
            skFitSpline(sketch, "E3539", {"points": [v(98.35, -115.33) * mm, v(98.35, -115.9) * mm, v(98.65, -116.43) * mm, v(99.15, -116.72) * mm]});
            skFitSpline(sketch, "E3540", {"points": [v(99.15, -116.72) * mm, v(99.64, -117) * mm, v(100.25, -117) * mm, v(100.75, -116.72) * mm]});
            skFitSpline(sketch, "E3541", {"points": [v(100.75, -116.72) * mm, v(101.24, -116.43) * mm, v(101.55, -115.9) * mm, v(101.55, -115.33) * mm]});
            skLineSegment(sketch, "E3542", {"start": v(181.5, -99.47) * mm, "end": v(181.5, -92.2) * mm});
            skFitSpline(sketch, "E3543", {"points": [v(241.05, -110.83) * mm, v(241.05, -110.26) * mm, v(240.74, -109.73) * mm, v(240.25, -109.45) * mm]});
            skFitSpline(sketch, "E3544", {"points": [v(240.25, -109.45) * mm, v(239.75, -109.16) * mm, v(239.14, -109.16) * mm, v(238.65, -109.45) * mm]});
            skFitSpline(sketch, "E3545", {"points": [v(238.65, -109.45) * mm, v(238.15, -109.73) * mm, v(237.85, -110.26) * mm, v(237.85, -110.83) * mm]});
            skFitSpline(sketch, "E3546", {"points": [v(237.85, -110.83) * mm, v(237.85, -111.4) * mm, v(238.15, -111.93) * mm, v(238.65, -112.22) * mm]});
            skFitSpline(sketch, "E3547", {"points": [v(238.65, -112.22) * mm, v(239.14, -112.5) * mm, v(239.75, -112.5) * mm, v(240.25, -112.22) * mm]});
            skFitSpline(sketch, "E3548", {"points": [v(240.25, -112.22) * mm, v(240.74, -111.93) * mm, v(241.05, -111.4) * mm, v(241.05, -110.83) * mm]});
            skLineSegment(sketch, "E3549", {"start": v(180.63, -91.33) * mm, "end": v(158.26, -91.33) * mm});
            skFitSpline(sketch, "E3550", {"points": [v(171.05, -110.83) * mm, v(171.05, -110.26) * mm, v(170.74, -109.73) * mm, v(170.25, -109.45) * mm]});
            skFitSpline(sketch, "E3551", {"points": [v(170.25, -109.45) * mm, v(169.75, -109.16) * mm, v(169.14, -109.16) * mm, v(168.65, -109.45) * mm]});
            skFitSpline(sketch, "E3552", {"points": [v(168.65, -109.45) * mm, v(168.15, -109.73) * mm, v(167.85, -110.26) * mm, v(167.85, -110.83) * mm]});
            skFitSpline(sketch, "E3553", {"points": [v(167.85, -110.83) * mm, v(167.85, -111.4) * mm, v(168.15, -111.93) * mm, v(168.65, -112.22) * mm]});
            skFitSpline(sketch, "E3554", {"points": [v(168.65, -112.22) * mm, v(169.14, -112.5) * mm, v(169.75, -112.5) * mm, v(170.25, -112.22) * mm]});
            skFitSpline(sketch, "E3555", {"points": [v(170.25, -112.22) * mm, v(170.74, -111.93) * mm, v(171.05, -111.4) * mm, v(171.05, -110.83) * mm]});
            skFitSpline(sketch, "E3556", {"points": [v(289.45, -86.35) * mm, v(289.45, -87.94) * mm, v(290.08, -89.47) * mm, v(291.2, -90.6) * mm]});
            skLineSegment(sketch, "E3557", {"start": v(157.4, -92.2) * mm, "end": v(157.4, -99.47) * mm});
            skFitSpline(sketch, "E3558", {"points": [v(312.45, -111.83) * mm, v(314.38, -113.77) * mm, v(314.38, -116.9) * mm, v(312.45, -118.83) * mm]});
            skFitSpline(sketch, "E3559", {"points": [v(312.45, -118.83) * mm, v(310.52, -120.77) * mm, v(307.38, -120.77) * mm, v(305.45, -118.83) * mm]});
            skLineSegment(sketch, "E3560", {"start": v(291.2, -90.6) * mm, "end": v(312.45, -111.83) * mm});
            skFitSpline(sketch, "E3561", {"points": [v(289.2, -102.6) * mm, v(288.08, -101.47) * mm, v(286.55, -100.83) * mm, v(284.96, -100.83) * mm]});
            skFitSpline(sketch, "E3562", {"points": [v(310.55, -115.33) * mm, v(310.55, -114.76) * mm, v(310.24, -114.23) * mm, v(309.75, -113.95) * mm]});
            skFitSpline(sketch, "E3563", {"points": [v(309.75, -113.95) * mm, v(309.25, -113.66) * mm, v(308.64, -113.66) * mm, v(308.15, -113.95) * mm]});
            skFitSpline(sketch, "E3564", {"points": [v(308.15, -113.95) * mm, v(307.65, -114.23) * mm, v(307.35, -114.76) * mm, v(307.35, -115.33) * mm]});
            skFitSpline(sketch, "E3565", {"points": [v(307.35, -115.33) * mm, v(307.35, -115.9) * mm, v(307.65, -116.43) * mm, v(308.15, -116.72) * mm]});
            skFitSpline(sketch, "E3566", {"points": [v(308.15, -116.72) * mm, v(308.64, -117) * mm, v(309.25, -117) * mm, v(309.75, -116.72) * mm]});
            skFitSpline(sketch, "E3567", {"points": [v(309.75, -116.72) * mm, v(310.24, -116.43) * mm, v(310.55, -115.9) * mm, v(310.55, -115.33) * mm]});
            skLineSegment(sketch, "E3568", {"start": v(305.45, -118.83) * mm, "end": v(289.2, -102.6) * mm});
            skFitSpline(sketch, "E3569", {"points": [v(241.05, -80.83) * mm, v(241.05, -80.26) * mm, v(240.74, -79.73) * mm, v(240.25, -79.45) * mm]});
            skFitSpline(sketch, "E3570", {"points": [v(240.25, -79.45) * mm, v(239.75, -79.16) * mm, v(239.14, -79.16) * mm, v(238.65, -79.45) * mm]});
            skFitSpline(sketch, "E3571", {"points": [v(238.65, -79.45) * mm, v(238.15, -79.73) * mm, v(237.85, -80.26) * mm, v(237.85, -80.83) * mm]});
            skFitSpline(sketch, "E3572", {"points": [v(237.85, -80.83) * mm, v(237.85, -81.4) * mm, v(238.15, -81.93) * mm, v(238.65, -82.22) * mm]});
            skFitSpline(sketch, "E3573", {"points": [v(238.65, -82.22) * mm, v(239.14, -82.5) * mm, v(239.75, -82.5) * mm, v(240.25, -82.22) * mm]});
            skFitSpline(sketch, "E3574", {"points": [v(240.25, -82.22) * mm, v(240.74, -81.93) * mm, v(241.05, -81.4) * mm, v(241.05, -80.83) * mm]});
            skLineSegment(sketch, "E3575", {"start": v(310.55, -115.33) * mm, "end": v(310.55, -115.33) * mm});
            skFitSpline(sketch, "E3576", {"points": [v(171.05, -80.83) * mm, v(171.05, -80.26) * mm, v(170.74, -79.73) * mm, v(170.25, -79.45) * mm]});
            skFitSpline(sketch, "E3577", {"points": [v(170.25, -79.45) * mm, v(169.75, -79.16) * mm, v(169.14, -79.16) * mm, v(168.65, -79.45) * mm]});
            skFitSpline(sketch, "E3578", {"points": [v(168.65, -79.45) * mm, v(168.15, -79.73) * mm, v(167.85, -80.26) * mm, v(167.85, -80.83) * mm]});
            skFitSpline(sketch, "E3579", {"points": [v(167.85, -80.83) * mm, v(167.85, -81.4) * mm, v(168.15, -81.93) * mm, v(168.65, -82.22) * mm]});
            skFitSpline(sketch, "E3580", {"points": [v(168.65, -82.22) * mm, v(169.14, -82.5) * mm, v(169.75, -82.5) * mm, v(170.25, -82.22) * mm]});
            skFitSpline(sketch, "E3581", {"points": [v(170.25, -82.22) * mm, v(170.74, -81.93) * mm, v(171.05, -81.4) * mm, v(171.05, -80.83) * mm]});
            skFitSpline(sketch, "E3582", {"points": [v(223.55, -22.83) * mm, v(223.55, -22.26) * mm, v(223.24, -21.73) * mm, v(222.75, -21.45) * mm]});
            skFitSpline(sketch, "E3583", {"points": [v(222.75, -21.45) * mm, v(222.25, -21.16) * mm, v(221.64, -21.16) * mm, v(221.15, -21.45) * mm]});
            skFitSpline(sketch, "E3584", {"points": [v(221.15, -21.45) * mm, v(220.65, -21.73) * mm, v(220.35, -22.26) * mm, v(220.35, -22.83) * mm]});
            skFitSpline(sketch, "E3585", {"points": [v(220.35, -22.83) * mm, v(220.35, -23.4) * mm, v(220.65, -23.93) * mm, v(221.15, -24.22) * mm]});
            skFitSpline(sketch, "E3586", {"points": [v(221.15, -24.22) * mm, v(221.64, -24.5) * mm, v(222.25, -24.5) * mm, v(222.75, -24.22) * mm]});
            skFitSpline(sketch, "E3587", {"points": [v(222.75, -24.22) * mm, v(223.24, -23.93) * mm, v(223.55, -23.4) * mm, v(223.55, -22.83) * mm]});
            skFitSpline(sketch, "E3588", {"points": [v(188.55, -10.83) * mm, v(188.55, -10.26) * mm, v(188.24, -9.73) * mm, v(187.75, -9.45) * mm]});
            skFitSpline(sketch, "E3589", {"points": [v(187.75, -9.45) * mm, v(187.25, -9.16) * mm, v(186.64, -9.16) * mm, v(186.15, -9.45) * mm]});
            skFitSpline(sketch, "E3590", {"points": [v(186.15, -9.45) * mm, v(185.65, -9.73) * mm, v(185.35, -10.26) * mm, v(185.35, -10.83) * mm]});
            skFitSpline(sketch, "E3591", {"points": [v(185.35, -10.83) * mm, v(185.35, -11.4) * mm, v(185.65, -11.93) * mm, v(186.15, -12.22) * mm]});
            skFitSpline(sketch, "E3592", {"points": [v(186.15, -12.22) * mm, v(186.64, -12.5) * mm, v(187.25, -12.5) * mm, v(187.75, -12.22) * mm]});
            skFitSpline(sketch, "E3593", {"points": [v(187.75, -12.22) * mm, v(188.24, -11.93) * mm, v(188.55, -11.4) * mm, v(188.55, -10.83) * mm]});
            skFitSpline(sketch, "E3594", {"points": [v(223.55, 1.17) * mm, v(223.55, 1.74) * mm, v(223.24, 2.27) * mm, v(222.75, 2.55) * mm]});
            skFitSpline(sketch, "E3595", {"points": [v(222.75, 2.55) * mm, v(222.25, 2.84) * mm, v(221.64, 2.84) * mm, v(221.15, 2.55) * mm]});
            skFitSpline(sketch, "E3596", {"points": [v(221.15, 2.55) * mm, v(220.65, 2.27) * mm, v(220.35, 1.74) * mm, v(220.35, 1.17) * mm]});
            skFitSpline(sketch, "E3597", {"points": [v(220.35, 1.17) * mm, v(220.35, 0.6) * mm, v(220.65, 0.07) * mm, v(221.15, -0.22) * mm]});
            skFitSpline(sketch, "E3598", {"points": [v(221.15, -0.22) * mm, v(221.64, -0.5) * mm, v(222.25, -0.5) * mm, v(222.75, -0.22) * mm]});
            skFitSpline(sketch, "E3599", {"points": [v(222.75, -0.22) * mm, v(223.24, 0.07) * mm, v(223.55, 0.6) * mm, v(223.55, 1.17) * mm]});
            skFitSpline(sketch, "E3600", {"points": [v(310.55, 93.67) * mm, v(310.55, 94.24) * mm, v(310.24, 94.77) * mm, v(309.75, 95.05) * mm]});
            skFitSpline(sketch, "E3601", {"points": [v(309.75, 95.05) * mm, v(309.25, 95.34) * mm, v(308.64, 95.34) * mm, v(308.15, 95.05) * mm]});
            skFitSpline(sketch, "E3602", {"points": [v(308.15, 95.05) * mm, v(307.65, 94.77) * mm, v(307.35, 94.24) * mm, v(307.35, 93.67) * mm]});
            skFitSpline(sketch, "E3603", {"points": [v(307.35, 93.67) * mm, v(307.35, 93.1) * mm, v(307.65, 92.57) * mm, v(308.15, 92.28) * mm]});
            skFitSpline(sketch, "E3604", {"points": [v(308.15, 92.28) * mm, v(308.64, 92) * mm, v(309.25, 92) * mm, v(309.75, 92.28) * mm]});
            skFitSpline(sketch, "E3605", {"points": [v(309.75, 92.28) * mm, v(310.24, 92.57) * mm, v(310.55, 93.1) * mm, v(310.55, 93.67) * mm]});
            skFitSpline(sketch, "E3606", {"points": [v(101.55, 93.67) * mm, v(101.55, 94.24) * mm, v(101.24, 94.77) * mm, v(100.75, 95.05) * mm]});
            skFitSpline(sketch, "E3607", {"points": [v(100.75, 95.05) * mm, v(100.25, 95.34) * mm, v(99.64, 95.34) * mm, v(99.15, 95.05) * mm]});
            skFitSpline(sketch, "E3608", {"points": [v(99.15, 95.05) * mm, v(98.65, 94.77) * mm, v(98.35, 94.24) * mm, v(98.35, 93.67) * mm]});
            skFitSpline(sketch, "E3609", {"points": [v(98.35, 93.67) * mm, v(98.35, 93.1) * mm, v(98.65, 92.57) * mm, v(99.15, 92.28) * mm]});
            skFitSpline(sketch, "E3610", {"points": [v(99.15, 92.28) * mm, v(99.64, 92) * mm, v(100.25, 92) * mm, v(100.75, 92.28) * mm]});
            skFitSpline(sketch, "E3611", {"points": [v(100.75, 92.28) * mm, v(101.24, 92.57) * mm, v(101.55, 93.1) * mm, v(101.55, 93.67) * mm]});
            skFitSpline(sketch, "E3612", {"points": [v(251.07, -100.58) * mm, v(250.98, -100.43) * mm, v(250.81, -100.33) * mm, v(250.63, -100.33) * mm]});
            skFitSpline(sketch, "E3613", {"points": [v(251.07, -100.58) * mm, v(251.17, -100.77) * mm, v(251.38, -100.86) * mm, v(251.59, -100.83) * mm]});
            skFitSpline(sketch, "E3614", {"points": [v(251.59, -100.83) * mm, v(251.8, -100.79) * mm, v(251.95, -100.63) * mm, v(252, -100.42) * mm]});
            skFitSpline(sketch, "E3615", {"points": [v(252, -100.42) * mm, v(252.03, -100.21) * mm, v(251.93, -100) * mm, v(251.75, -99.9) * mm]});
            skFitSpline(sketch, "E3616", {"points": [v(251.5, -99.47) * mm, v(251.5, -99.65) * mm, v(251.6, -99.81) * mm, v(251.75, -99.9) * mm]});
            skFitSpline(sketch, "E3617", {"points": [v(251.75, -91.77) * mm, v(251.6, -91.86) * mm, v(251.5, -92.02) * mm, v(251.5, -92.2) * mm]});
            skFitSpline(sketch, "E3618", {"points": [v(251.75, -91.77) * mm, v(251.93, -91.66) * mm, v(252.03, -91.45) * mm, v(252, -91.25) * mm]});
            skFitSpline(sketch, "E3619", {"points": [v(252, -91.25) * mm, v(251.95, -91.04) * mm, v(251.8, -90.88) * mm, v(251.59, -90.84) * mm]});
            skFitSpline(sketch, "E3620", {"points": [v(251.59, -90.84) * mm, v(251.38, -90.8) * mm, v(251.17, -90.9) * mm, v(251.07, -91.08) * mm]});
            skFitSpline(sketch, "E3621", {"points": [v(250.63, -91.33) * mm, v(250.81, -91.33) * mm, v(250.98, -91.24) * mm, v(251.07, -91.08) * mm]});
            skFitSpline(sketch, "E3622", {"points": [v(227.83, -91.08) * mm, v(227.92, -91.24) * mm, v(228.09, -91.33) * mm, v(228.26, -91.33) * mm]});
            skFitSpline(sketch, "E3623", {"points": [v(227.83, -91.08) * mm, v(227.73, -90.9) * mm, v(227.52, -90.8) * mm, v(227.31, -90.84) * mm]});
            skFitSpline(sketch, "E3624", {"points": [v(227.31, -90.84) * mm, v(227.1, -90.88) * mm, v(226.94, -91.04) * mm, v(226.9, -91.25) * mm]});
            skFitSpline(sketch, "E3625", {"points": [v(226.9, -91.25) * mm, v(226.87, -91.45) * mm, v(226.97, -91.66) * mm, v(227.15, -91.77) * mm]});
            skFitSpline(sketch, "E3626", {"points": [v(227.4, -92.2) * mm, v(227.4, -92.02) * mm, v(227.3, -91.86) * mm, v(227.15, -91.77) * mm]});
            skLineSegment(sketch, "E3627", {"start": v(310.55, 93.67) * mm, "end": v(310.55, 93.67) * mm});
            skFitSpline(sketch, "E3628", {"points": [v(227.15, -99.9) * mm, v(227.3, -99.81) * mm, v(227.4, -99.65) * mm, v(227.4, -99.47) * mm]});
            skFitSpline(sketch, "E3629", {"points": [v(227.15, -99.9) * mm, v(226.97, -100) * mm, v(226.87, -100.21) * mm, v(226.9, -100.42) * mm]});
            skFitSpline(sketch, "E3630", {"points": [v(226.9, -100.42) * mm, v(226.94, -100.63) * mm, v(227.1, -100.79) * mm, v(227.31, -100.83) * mm]});
            skFitSpline(sketch, "E3631", {"points": [v(227.31, -100.83) * mm, v(227.52, -100.86) * mm, v(227.73, -100.77) * mm, v(227.83, -100.58) * mm]});
            skFitSpline(sketch, "E3632", {"points": [v(228.26, -100.33) * mm, v(228.09, -100.33) * mm, v(227.92, -100.43) * mm, v(227.83, -100.58) * mm]});
            skFitSpline(sketch, "E3633", {"points": [v(206.05, -22.83) * mm, v(206.05, -22.26) * mm, v(205.74, -21.73) * mm, v(205.25, -21.45) * mm]});
            skFitSpline(sketch, "E3634", {"points": [v(205.25, -21.45) * mm, v(204.75, -21.16) * mm, v(204.14, -21.16) * mm, v(203.65, -21.45) * mm]});
            skFitSpline(sketch, "E3635", {"points": [v(203.65, -21.45) * mm, v(203.15, -21.73) * mm, v(202.85, -22.26) * mm, v(202.85, -22.83) * mm]});
            skFitSpline(sketch, "E3636", {"points": [v(202.85, -22.83) * mm, v(202.85, -23.4) * mm, v(203.15, -23.93) * mm, v(203.65, -24.22) * mm]});
            skFitSpline(sketch, "E3637", {"points": [v(203.65, -24.22) * mm, v(204.14, -24.5) * mm, v(204.75, -24.5) * mm, v(205.25, -24.22) * mm]});
            skFitSpline(sketch, "E3638", {"points": [v(205.25, -24.22) * mm, v(205.74, -23.93) * mm, v(206.05, -23.4) * mm, v(206.05, -22.83) * mm]});
            skFitSpline(sketch, "E3639", {"points": [v(206.05, 1.17) * mm, v(206.05, 1.74) * mm, v(205.74, 2.27) * mm, v(205.25, 2.55) * mm]});
            skFitSpline(sketch, "E3640", {"points": [v(205.25, 2.55) * mm, v(204.75, 2.84) * mm, v(204.14, 2.84) * mm, v(203.65, 2.55) * mm]});
            skFitSpline(sketch, "E3641", {"points": [v(203.65, 2.55) * mm, v(203.15, 2.27) * mm, v(202.85, 1.74) * mm, v(202.85, 1.17) * mm]});
            skFitSpline(sketch, "E3642", {"points": [v(202.85, 1.17) * mm, v(202.85, 0.6) * mm, v(203.15, 0.07) * mm, v(203.65, -0.22) * mm]});
            skFitSpline(sketch, "E3643", {"points": [v(203.65, -0.22) * mm, v(204.14, -0.5) * mm, v(204.75, -0.5) * mm, v(205.25, -0.22) * mm]});
            skFitSpline(sketch, "E3644", {"points": [v(205.25, -0.22) * mm, v(205.74, 0.07) * mm, v(206.05, 0.6) * mm, v(206.05, 1.17) * mm]});
            skLineSegment(sketch, "E3645", {"start": v(228.26, -100.33) * mm, "end": v(250.63, -100.33) * mm});
            skFitSpline(sketch, "E3646", {"points": [v(173.45, 17.23) * mm, v(173.45, 18.98) * mm, v(172.75, 20.66) * mm, v(171.52, 21.9) * mm]});
            skLineSegment(sketch, "E3647", {"start": v(250.63, -91.33) * mm, "end": v(228.26, -91.33) * mm});
            skFitSpline(sketch, "E3648", {"points": [v(171.52, -43.57) * mm, v(172.75, -42.33) * mm, v(173.45, -40.65) * mm, v(173.45, -38.9) * mm]});
            skFitSpline(sketch, "E3649", {"points": [v(140.72, 52.7) * mm, v(138.83, 54.59) * mm, v(135.99, 55.15) * mm, v(133.52, 54.13) * mm]});
            skFitSpline(sketch, "E3650", {"points": [v(133.52, 54.13) * mm, v(131.06, 53.1) * mm, v(129.45, 50.7) * mm, v(129.45, 48.03) * mm]});
            skFitSpline(sketch, "E3651", {"points": [v(129.45, -69.7) * mm, v(129.45, -72.37) * mm, v(131.06, -74.78) * mm, v(133.52, -75.8) * mm]});
            skFitSpline(sketch, "E3652", {"points": [v(133.52, -75.8) * mm, v(135.99, -76.82) * mm, v(138.83, -76.25) * mm, v(140.72, -74.37) * mm]});
            skLineSegment(sketch, "E3653", {"start": v(227.4, -92.2) * mm, "end": v(227.4, -99.47) * mm});
            skLineSegment(sketch, "E3654", {"start": v(173.45, 17.23) * mm, "end": v(173.45, -38.9) * mm});
            skFitSpline(sketch, "E3655", {"points": [v(138.96, 79.17) * mm, v(140.55, 79.17) * mm, v(142.08, 79.8) * mm, v(143.2, 80.92) * mm]});
            skFitSpline(sketch, "E3656", {"points": [v(265.7, 80.92) * mm, v(266.82, 79.8) * mm, v(268.34, 79.17) * mm, v(269.93, 79.17) * mm]});
            skLineSegment(sketch, "E3657", {"start": v(171.52, -43.57) * mm, "end": v(140.72, -74.37) * mm});
            skFitSpline(sketch, "E3658", {"points": [v(251.2, 95.4) * mm, v(250.08, 96.53) * mm, v(248.55, 97.17) * mm, v(246.96, 97.17) * mm]});
            skLineSegment(sketch, "E3659", {"start": v(140.72, 52.7) * mm, "end": v(171.52, 21.9) * mm});
            skFitSpline(sketch, "E3660", {"points": [v(229.93, 97.17) * mm, v(228.34, 97.17) * mm, v(226.82, 96.53) * mm, v(225.7, 95.4) * mm]});
            skLineSegment(sketch, "E3661", {"start": v(129.45, -69.7) * mm, "end": v(129.45, 48.03) * mm});
            skFitSpline(sketch, "E3662", {"points": [v(206.96, 79.17) * mm, v(208.55, 79.17) * mm, v(210.08, 79.8) * mm, v(211.2, 80.92) * mm]});
            skLineSegment(sketch, "E3663", {"start": v(157.7, 95.4) * mm, "end": v(143.2, 80.92) * mm});
            skFitSpline(sketch, "E3664", {"points": [v(197.7, 80.92) * mm, v(198.82, 79.8) * mm, v(200.34, 79.17) * mm, v(201.93, 79.17) * mm]});
            skLineSegment(sketch, "E3665", {"start": v(265.7, 80.92) * mm, "end": v(251.2, 95.4) * mm});
            skFitSpline(sketch, "E3666", {"points": [v(183.2, 95.4) * mm, v(182.08, 96.53) * mm, v(180.55, 97.17) * mm, v(178.96, 97.17) * mm]});
            skLineSegment(sketch, "E3667", {"start": v(246.96, 97.17) * mm, "end": v(229.93, 97.17) * mm});
            skFitSpline(sketch, "E3668", {"points": [v(161.93, 97.17) * mm, v(160.34, 97.17) * mm, v(158.82, 96.53) * mm, v(157.7, 95.4) * mm]});
            skFitSpline(sketch, "E3669", {"points": [v(211.2, 67.4) * mm, v(210.08, 68.53) * mm, v(208.55, 69.17) * mm, v(206.96, 69.17) * mm]});
            skLineSegment(sketch, "E3670", {"start": v(225.7, 95.4) * mm, "end": v(211.2, 80.92) * mm});
            skFitSpline(sketch, "E3671", {"points": [v(201.93, 69.17) * mm, v(200.34, 69.17) * mm, v(198.82, 68.53) * mm, v(197.7, 67.4) * mm]});
            skLineSegment(sketch, "E3672", {"start": v(206.96, 79.17) * mm, "end": v(201.93, 79.17) * mm});
            skLineSegment(sketch, "E3673", {"start": v(197.7, 80.92) * mm, "end": v(183.2, 95.4) * mm});
            skFitSpline(sketch, "E3674", {"points": [v(180.63, 78.67) * mm, v(180.81, 78.67) * mm, v(180.98, 78.76) * mm, v(181.07, 78.92) * mm]});
            skFitSpline(sketch, "E3675", {"points": [v(181.75, 78.23) * mm, v(181.93, 78.34) * mm, v(182.03, 78.55) * mm, v(182, 78.75) * mm]});
            skFitSpline(sketch, "E3676", {"points": [v(182, 78.75) * mm, v(181.95, 78.96) * mm, v(181.8, 79.12) * mm, v(181.59, 79.16) * mm]});
            skFitSpline(sketch, "E3677", {"points": [v(181.59, 79.16) * mm, v(181.38, 79.2) * mm, v(181.17, 79.1) * mm, v(181.07, 78.92) * mm]});
            skFitSpline(sketch, "E3678", {"points": [v(181.75, 78.23) * mm, v(181.6, 78.14) * mm, v(181.5, 77.98) * mm, v(181.5, 77.8) * mm]});
            skLineSegment(sketch, "E3679", {"start": v(178.96, 97.17) * mm, "end": v(161.93, 97.17) * mm});
            skFitSpline(sketch, "E3680", {"points": [v(181.5, 70.53) * mm, v(181.5, 70.35) * mm, v(181.6, 70.19) * mm, v(181.75, 70.1) * mm]});
            skFitSpline(sketch, "E3681", {"points": [v(181.07, 69.42) * mm, v(181.17, 69.23) * mm, v(181.38, 69.14) * mm, v(181.59, 69.17) * mm]});
            skFitSpline(sketch, "E3682", {"points": [v(181.59, 69.17) * mm, v(181.8, 69.21) * mm, v(181.95, 69.37) * mm, v(182, 69.58) * mm]});
            skFitSpline(sketch, "E3683", {"points": [v(182, 69.58) * mm, v(182.03, 69.79) * mm, v(181.93, 70) * mm, v(181.75, 70.1) * mm]});
            skFitSpline(sketch, "E3684", {"points": [v(181.07, 69.42) * mm, v(180.98, 69.57) * mm, v(180.81, 69.67) * mm, v(180.63, 69.67) * mm]});
            skLineSegment(sketch, "E3685", {"start": v(206.96, 69.17) * mm, "end": v(201.93, 69.17) * mm});
            skFitSpline(sketch, "E3686", {"points": [v(158.26, 69.67) * mm, v(158.09, 69.67) * mm, v(157.92, 69.57) * mm, v(157.83, 69.42) * mm]});
            skFitSpline(sketch, "E3687", {"points": [v(157.15, 70.1) * mm, v(156.97, 70) * mm, v(156.87, 69.79) * mm, v(156.9, 69.58) * mm]});
            skFitSpline(sketch, "E3688", {"points": [v(156.9, 69.58) * mm, v(156.94, 69.37) * mm, v(157.1, 69.21) * mm, v(157.31, 69.17) * mm]});
            skFitSpline(sketch, "E3689", {"points": [v(157.31, 69.17) * mm, v(157.52, 69.14) * mm, v(157.73, 69.23) * mm, v(157.83, 69.42) * mm]});
            skFitSpline(sketch, "E3690", {"points": [v(157.15, 70.1) * mm, v(157.3, 70.19) * mm, v(157.4, 70.35) * mm, v(157.4, 70.53) * mm]});
            skLineSegment(sketch, "E3691", {"start": v(251.5, 77.8) * mm, "end": v(251.5, 70.53) * mm});
            skFitSpline(sketch, "E3692", {"points": [v(157.4, 77.8) * mm, v(157.4, 77.98) * mm, v(157.3, 78.14) * mm, v(157.15, 78.23) * mm]});
            skFitSpline(sketch, "E3693", {"points": [v(157.83, 78.92) * mm, v(157.73, 79.1) * mm, v(157.52, 79.2) * mm, v(157.31, 79.16) * mm]});
            skFitSpline(sketch, "E3694", {"points": [v(157.31, 79.16) * mm, v(157.1, 79.12) * mm, v(156.94, 78.96) * mm, v(156.9, 78.75) * mm]});
            skFitSpline(sketch, "E3695", {"points": [v(156.9, 78.75) * mm, v(156.87, 78.55) * mm, v(156.97, 78.34) * mm, v(157.15, 78.23) * mm]});
            skFitSpline(sketch, "E3696", {"points": [v(157.83, 78.92) * mm, v(157.92, 78.76) * mm, v(158.09, 78.67) * mm, v(158.26, 78.67) * mm]});
            skFitSpline(sketch, "E3697", {"points": [v(241.05, 89.17) * mm, v(241.05, 89.74) * mm, v(240.74, 90.27) * mm, v(240.25, 90.55) * mm]});
            skFitSpline(sketch, "E3698", {"points": [v(240.25, 90.55) * mm, v(239.75, 90.84) * mm, v(239.14, 90.84) * mm, v(238.65, 90.55) * mm]});
            skFitSpline(sketch, "E3699", {"points": [v(238.65, 90.55) * mm, v(238.15, 90.27) * mm, v(237.85, 89.74) * mm, v(237.85, 89.17) * mm]});
            skFitSpline(sketch, "E3700", {"points": [v(237.85, 89.17) * mm, v(237.85, 88.6) * mm, v(238.15, 88.07) * mm, v(238.65, 87.78) * mm]});
            skFitSpline(sketch, "E3701", {"points": [v(238.65, 87.78) * mm, v(239.14, 87.5) * mm, v(239.75, 87.5) * mm, v(240.25, 87.78) * mm]});
            skFitSpline(sketch, "E3702", {"points": [v(240.25, 87.78) * mm, v(240.74, 88.07) * mm, v(241.05, 88.6) * mm, v(241.05, 89.17) * mm]});
            skLineSegment(sketch, "E3703", {"start": v(158.26, 78.67) * mm, "end": v(180.63, 78.67) * mm});
            skFitSpline(sketch, "E3704", {"points": [v(171.05, 89.17) * mm, v(171.05, 89.74) * mm, v(170.74, 90.27) * mm, v(170.25, 90.55) * mm]});
            skFitSpline(sketch, "E3705", {"points": [v(170.25, 90.55) * mm, v(169.75, 90.84) * mm, v(169.14, 90.84) * mm, v(168.65, 90.55) * mm]});
            skFitSpline(sketch, "E3706", {"points": [v(168.65, 90.55) * mm, v(168.15, 90.27) * mm, v(167.85, 89.74) * mm, v(167.85, 89.17) * mm]});
            skFitSpline(sketch, "E3707", {"points": [v(167.85, 89.17) * mm, v(167.85, 88.6) * mm, v(168.15, 88.07) * mm, v(168.65, 87.78) * mm]});
            skFitSpline(sketch, "E3708", {"points": [v(168.65, 87.78) * mm, v(169.14, 87.5) * mm, v(169.75, 87.5) * mm, v(170.25, 87.78) * mm]});
            skFitSpline(sketch, "E3709", {"points": [v(170.25, 87.78) * mm, v(170.74, 88.07) * mm, v(171.05, 88.6) * mm, v(171.05, 89.17) * mm]});
            skLineSegment(sketch, "E3710", {"start": v(181.5, 77.8) * mm, "end": v(181.5, 70.53) * mm});
            skLineSegment(sketch, "E3711", {"start": v(180.63, 69.67) * mm, "end": v(158.26, 69.67) * mm});
            skFitSpline(sketch, "E3712", {"points": [v(250.63, 78.67) * mm, v(250.81, 78.67) * mm, v(250.98, 78.76) * mm, v(251.07, 78.92) * mm]});
            skFitSpline(sketch, "E3713", {"points": [v(251.75, 78.23) * mm, v(251.93, 78.34) * mm, v(252.03, 78.55) * mm, v(252, 78.75) * mm]});
            skFitSpline(sketch, "E3714", {"points": [v(252, 78.75) * mm, v(251.95, 78.96) * mm, v(251.8, 79.12) * mm, v(251.59, 79.16) * mm]});
            skFitSpline(sketch, "E3715", {"points": [v(251.59, 79.16) * mm, v(251.38, 79.2) * mm, v(251.17, 79.1) * mm, v(251.07, 78.92) * mm]});
            skFitSpline(sketch, "E3716", {"points": [v(251.75, 78.23) * mm, v(251.6, 78.14) * mm, v(251.5, 77.98) * mm, v(251.5, 77.8) * mm]});
            skFitSpline(sketch, "E3717", {"points": [v(251.5, 70.53) * mm, v(251.5, 70.35) * mm, v(251.6, 70.19) * mm, v(251.75, 70.1) * mm]});
            skFitSpline(sketch, "E3718", {"points": [v(251.07, 69.42) * mm, v(251.17, 69.23) * mm, v(251.38, 69.14) * mm, v(251.59, 69.17) * mm]});
            skFitSpline(sketch, "E3719", {"points": [v(251.59, 69.17) * mm, v(251.8, 69.21) * mm, v(251.95, 69.37) * mm, v(252, 69.58) * mm]});
            skFitSpline(sketch, "E3720", {"points": [v(252, 69.58) * mm, v(252.03, 69.79) * mm, v(251.93, 70) * mm, v(251.75, 70.1) * mm]});
            skFitSpline(sketch, "E3721", {"points": [v(251.07, 69.42) * mm, v(250.98, 69.57) * mm, v(250.81, 69.67) * mm, v(250.63, 69.67) * mm]});
            skLineSegment(sketch, "E3722", {"start": v(157.4, 70.53) * mm, "end": v(157.4, 77.8) * mm});
            skFitSpline(sketch, "E3723", {"points": [v(228.26, 69.67) * mm, v(228.09, 69.67) * mm, v(227.92, 69.57) * mm, v(227.83, 69.42) * mm]});
            skFitSpline(sketch, "E3724", {"points": [v(227.15, 70.1) * mm, v(226.97, 70) * mm, v(226.87, 69.79) * mm, v(226.9, 69.58) * mm]});
            skFitSpline(sketch, "E3725", {"points": [v(226.9, 69.58) * mm, v(226.94, 69.37) * mm, v(227.1, 69.21) * mm, v(227.31, 69.17) * mm]});
            skFitSpline(sketch, "E3726", {"points": [v(227.31, 69.17) * mm, v(227.52, 69.14) * mm, v(227.73, 69.23) * mm, v(227.83, 69.42) * mm]});
            skFitSpline(sketch, "E3727", {"points": [v(227.15, 70.1) * mm, v(227.3, 70.19) * mm, v(227.4, 70.35) * mm, v(227.4, 70.53) * mm]});
            skFitSpline(sketch, "E3728", {"points": [v(227.4, 77.8) * mm, v(227.4, 77.98) * mm, v(227.3, 78.14) * mm, v(227.15, 78.23) * mm]});
            skFitSpline(sketch, "E3729", {"points": [v(227.83, 78.92) * mm, v(227.73, 79.1) * mm, v(227.52, 79.2) * mm, v(227.31, 79.16) * mm]});
            skFitSpline(sketch, "E3730", {"points": [v(227.31, 79.16) * mm, v(227.1, 79.12) * mm, v(226.94, 78.96) * mm, v(226.9, 78.75) * mm]});
            skFitSpline(sketch, "E3731", {"points": [v(226.9, 78.75) * mm, v(226.87, 78.55) * mm, v(226.97, 78.34) * mm, v(227.15, 78.23) * mm]});
            skFitSpline(sketch, "E3732", {"points": [v(227.83, 78.92) * mm, v(227.92, 78.76) * mm, v(228.09, 78.67) * mm, v(228.26, 78.67) * mm]});
            skFitSpline(sketch, "E3733", {"points": [v(181.2, 50.92) * mm, v(180.08, 49.8) * mm, v(179.45, 48.27) * mm, v(179.45, 46.68) * mm]});
            skFitSpline(sketch, "E3734", {"points": [v(229.45, 46.68) * mm, v(229.45, 48.27) * mm, v(228.82, 49.8) * mm, v(227.7, 50.92) * mm]});
            skLineSegment(sketch, "E3735", {"start": v(228.26, 78.67) * mm, "end": v(250.63, 78.67) * mm});
            skFitSpline(sketch, "E3736", {"points": [v(241.05, 59.17) * mm, v(241.05, 59.74) * mm, v(240.74, 60.27) * mm, v(240.25, 60.55) * mm]});
            skFitSpline(sketch, "E3737", {"points": [v(240.25, 60.55) * mm, v(239.75, 60.84) * mm, v(239.14, 60.84) * mm, v(238.65, 60.55) * mm]});
            skFitSpline(sketch, "E3738", {"points": [v(238.65, 60.55) * mm, v(238.15, 60.27) * mm, v(237.85, 59.74) * mm, v(237.85, 59.17) * mm]});
            skFitSpline(sketch, "E3739", {"points": [v(237.85, 59.17) * mm, v(237.85, 58.6) * mm, v(238.15, 58.07) * mm, v(238.65, 57.78) * mm]});
            skFitSpline(sketch, "E3740", {"points": [v(238.65, 57.78) * mm, v(239.14, 57.5) * mm, v(239.75, 57.5) * mm, v(240.25, 57.78) * mm]});
            skFitSpline(sketch, "E3741", {"points": [v(240.25, 57.78) * mm, v(240.74, 58.07) * mm, v(241.05, 58.6) * mm, v(241.05, 59.17) * mm]});
            skLineSegment(sketch, "E3742", {"start": v(250.63, 69.67) * mm, "end": v(228.26, 69.67) * mm});
            skFitSpline(sketch, "E3743", {"points": [v(171.05, 59.17) * mm, v(171.05, 59.74) * mm, v(170.74, 60.27) * mm, v(170.25, 60.55) * mm]});
            skFitSpline(sketch, "E3744", {"points": [v(170.25, 60.55) * mm, v(169.75, 60.84) * mm, v(169.14, 60.84) * mm, v(168.65, 60.55) * mm]});
            skFitSpline(sketch, "E3745", {"points": [v(168.65, 60.55) * mm, v(168.15, 60.27) * mm, v(167.85, 59.74) * mm, v(167.85, 59.17) * mm]});
            skFitSpline(sketch, "E3746", {"points": [v(167.85, 59.17) * mm, v(167.85, 58.6) * mm, v(168.15, 58.07) * mm, v(168.65, 57.78) * mm]});
            skFitSpline(sketch, "E3747", {"points": [v(168.65, 57.78) * mm, v(169.14, 57.5) * mm, v(169.75, 57.5) * mm, v(170.25, 57.78) * mm]});
            skFitSpline(sketch, "E3748", {"points": [v(170.25, 57.78) * mm, v(170.74, 58.07) * mm, v(171.05, 58.6) * mm, v(171.05, 59.17) * mm]});
            skLineSegment(sketch, "E3749", {"start": v(227.4, 70.53) * mm, "end": v(227.4, 77.8) * mm});
            skLineSegment(sketch, "E3750", {"start": v(197.7, 67.4) * mm, "end": v(181.2, 50.92) * mm});
            skLineSegment(sketch, "E3751", {"start": v(227.7, 50.92) * mm, "end": v(211.2, 67.4) * mm});
            skFitSpline(sketch, "E3752", {"points": [v(284.96, 79.17) * mm, v(286.55, 79.17) * mm, v(288.08, 79.8) * mm, v(289.2, 80.92) * mm]});
            skFitSpline(sketch, "E3753", {"points": [v(119.7, 80.92) * mm, v(120.82, 79.8) * mm, v(122.34, 79.17) * mm, v(123.93, 79.17) * mm]});
            skFitSpline(sketch, "E3754", {"points": [v(320.55, -10.83) * mm, v(320.55, -10.26) * mm, v(320.24, -9.73) * mm, v(319.75, -9.45) * mm]});
            skFitSpline(sketch, "E3755", {"points": [v(319.75, -9.45) * mm, v(319.25, -9.16) * mm, v(318.64, -9.16) * mm, v(318.15, -9.45) * mm]});
            skFitSpline(sketch, "E3756", {"points": [v(318.15, -9.45) * mm, v(317.65, -9.73) * mm, v(317.35, -10.26) * mm, v(317.35, -10.83) * mm]});
            skFitSpline(sketch, "E3757", {"points": [v(317.35, -10.83) * mm, v(317.35, -11.4) * mm, v(317.65, -11.93) * mm, v(318.15, -12.22) * mm]});
            skFitSpline(sketch, "E3758", {"points": [v(318.15, -12.22) * mm, v(318.64, -12.5) * mm, v(319.25, -12.5) * mm, v(319.75, -12.22) * mm]});
            skFitSpline(sketch, "E3759", {"points": [v(319.75, -12.22) * mm, v(320.24, -11.93) * mm, v(320.55, -11.4) * mm, v(320.55, -10.83) * mm]});
            skLineSegment(sketch, "E3760", {"start": v(179.45, 46.68) * mm, "end": v(179.45, 31.65) * mm});
            skLineSegment(sketch, "E3761", {"start": v(229.45, 31.65) * mm, "end": v(229.45, 46.68) * mm});
            skLineSegment(sketch, "E3762", {"start": v(138.96, 79.17) * mm, "end": v(123.93, 79.17) * mm});
            skLineSegment(sketch, "E3763", {"start": v(284.96, 79.17) * mm, "end": v(269.93, 79.17) * mm});
            skFitSpline(sketch, "E3764", {"points": [v(160.56, 65.67) * mm, v(160.02, 65.67) * mm, v(159.52, 65.39) * mm, v(159.25, 64.92) * mm]});
            skFitSpline(sketch, "E3765", {"points": [v(159.25, 64.92) * mm, v(158.99, 64.46) * mm, v(158.99, 63.88) * mm, v(159.25, 63.42) * mm]});
            skFitSpline(sketch, "E3766", {"points": [v(159.25, 63.42) * mm, v(159.52, 62.95) * mm, v(160.02, 62.67) * mm, v(160.56, 62.67) * mm]});
            skFitSpline(sketch, "E3767", {"points": [v(160.56, 62.67) * mm, v(161.1, 62.67) * mm, v(161.59, 62.95) * mm, v(161.86, 63.42) * mm]});
            skFitSpline(sketch, "E3768", {"points": [v(161.86, 63.42) * mm, v(162.13, 63.88) * mm, v(162.13, 64.46) * mm, v(161.86, 64.92) * mm]});
            skFitSpline(sketch, "E3769", {"points": [v(161.86, 64.92) * mm, v(161.59, 65.39) * mm, v(161.1, 65.67) * mm, v(160.56, 65.67) * mm]});
            skFitSpline(sketch, "E3770", {"points": [v(160.56, 85.67) * mm, v(160.02, 85.67) * mm, v(159.52, 85.39) * mm, v(159.25, 84.92) * mm]});
            skFitSpline(sketch, "E3771", {"points": [v(159.25, 84.92) * mm, v(158.99, 84.46) * mm, v(158.99, 83.88) * mm, v(159.25, 83.42) * mm]});
            skFitSpline(sketch, "E3772", {"points": [v(159.25, 83.42) * mm, v(159.52, 82.95) * mm, v(160.02, 82.67) * mm, v(160.56, 82.67) * mm]});
            skFitSpline(sketch, "E3773", {"points": [v(160.56, 82.67) * mm, v(161.1, 82.67) * mm, v(161.59, 82.95) * mm, v(161.86, 83.42) * mm]});
            skFitSpline(sketch, "E3774", {"points": [v(161.86, 83.42) * mm, v(162.13, 83.88) * mm, v(162.13, 84.46) * mm, v(161.86, 84.92) * mm]});
            skFitSpline(sketch, "E3775", {"points": [v(161.86, 84.92) * mm, v(161.59, 85.39) * mm, v(161.1, 85.67) * mm, v(160.56, 85.67) * mm]});
            skFitSpline(sketch, "E3776", {"points": [v(175.56, 65.67) * mm, v(175.02, 65.67) * mm, v(174.52, 65.39) * mm, v(174.25, 64.92) * mm]});
            skFitSpline(sketch, "E3777", {"points": [v(174.25, 64.92) * mm, v(173.99, 64.46) * mm, v(173.99, 63.88) * mm, v(174.25, 63.42) * mm]});
            skFitSpline(sketch, "E3778", {"points": [v(174.25, 63.42) * mm, v(174.52, 62.95) * mm, v(175.02, 62.67) * mm, v(175.56, 62.67) * mm]});
            skFitSpline(sketch, "E3779", {"points": [v(175.56, 62.67) * mm, v(176.1, 62.67) * mm, v(176.59, 62.95) * mm, v(176.86, 63.42) * mm]});
            skFitSpline(sketch, "E3780", {"points": [v(176.86, 63.42) * mm, v(177.13, 63.88) * mm, v(177.13, 64.46) * mm, v(176.86, 64.92) * mm]});
            skFitSpline(sketch, "E3781", {"points": [v(176.86, 64.92) * mm, v(176.59, 65.39) * mm, v(176.1, 65.67) * mm, v(175.56, 65.67) * mm]});
            skFitSpline(sketch, "E3782", {"points": [v(175.56, 85.67) * mm, v(175.02, 85.67) * mm, v(174.52, 85.39) * mm, v(174.25, 84.92) * mm]});
            skFitSpline(sketch, "E3783", {"points": [v(174.25, 84.92) * mm, v(173.99, 84.46) * mm, v(173.99, 83.88) * mm, v(174.25, 83.42) * mm]});
            skFitSpline(sketch, "E3784", {"points": [v(174.25, 83.42) * mm, v(174.52, 82.95) * mm, v(175.02, 82.67) * mm, v(175.56, 82.67) * mm]});
            skFitSpline(sketch, "E3785", {"points": [v(175.56, 82.67) * mm, v(176.1, 82.67) * mm, v(176.59, 82.95) * mm, v(176.86, 83.42) * mm]});
            skFitSpline(sketch, "E3786", {"points": [v(176.86, 83.42) * mm, v(177.13, 83.88) * mm, v(177.13, 84.46) * mm, v(176.86, 84.92) * mm]});
            skFitSpline(sketch, "E3787", {"points": [v(176.86, 84.92) * mm, v(176.59, 85.39) * mm, v(176.1, 85.67) * mm, v(175.56, 85.67) * mm]});
            skFitSpline(sketch, "E3788", {"points": [v(233.74, 65.67) * mm, v(233.2, 65.67) * mm, v(232.71, 65.39) * mm, v(232.44, 64.92) * mm]});
            skFitSpline(sketch, "E3789", {"points": [v(232.44, 64.92) * mm, v(232.17, 64.46) * mm, v(232.17, 63.88) * mm, v(232.44, 63.42) * mm]});
            skFitSpline(sketch, "E3790", {"points": [v(232.44, 63.42) * mm, v(232.71, 62.95) * mm, v(233.2, 62.67) * mm, v(233.74, 62.67) * mm]});
            skFitSpline(sketch, "E3791", {"points": [v(233.74, 62.67) * mm, v(234.28, 62.67) * mm, v(234.78, 62.95) * mm, v(235.05, 63.42) * mm]});
            skFitSpline(sketch, "E3792", {"points": [v(235.05, 63.42) * mm, v(235.31, 63.88) * mm, v(235.31, 64.46) * mm, v(235.05, 64.92) * mm]});
            skFitSpline(sketch, "E3793", {"points": [v(235.05, 64.92) * mm, v(234.78, 65.39) * mm, v(234.28, 65.67) * mm, v(233.74, 65.67) * mm]});
            skFitSpline(sketch, "E3794", {"points": [v(233.74, 85.67) * mm, v(233.2, 85.67) * mm, v(232.71, 85.39) * mm, v(232.44, 84.92) * mm]});
            skFitSpline(sketch, "E3795", {"points": [v(232.44, 84.92) * mm, v(232.17, 84.46) * mm, v(232.17, 83.88) * mm, v(232.44, 83.42) * mm]});
            skFitSpline(sketch, "E3796", {"points": [v(232.44, 83.42) * mm, v(232.71, 82.95) * mm, v(233.2, 82.67) * mm, v(233.74, 82.67) * mm]});
            skFitSpline(sketch, "E3797", {"points": [v(233.74, 82.67) * mm, v(234.28, 82.67) * mm, v(234.78, 82.95) * mm, v(235.05, 83.42) * mm]});
            skFitSpline(sketch, "E3798", {"points": [v(235.05, 83.42) * mm, v(235.31, 83.88) * mm, v(235.31, 84.46) * mm, v(235.05, 84.92) * mm]});
            skFitSpline(sketch, "E3799", {"points": [v(235.05, 84.92) * mm, v(234.78, 85.39) * mm, v(234.28, 85.67) * mm, v(233.74, 85.67) * mm]});
            skFitSpline(sketch, "E3800", {"points": [v(248.74, 65.67) * mm, v(248.2, 65.67) * mm, v(247.71, 65.39) * mm, v(247.44, 64.92) * mm]});
            skFitSpline(sketch, "E3801", {"points": [v(247.44, 64.92) * mm, v(247.17, 64.46) * mm, v(247.17, 63.88) * mm, v(247.44, 63.42) * mm]});
            skFitSpline(sketch, "E3802", {"points": [v(247.44, 63.42) * mm, v(247.71, 62.95) * mm, v(248.2, 62.67) * mm, v(248.74, 62.67) * mm]});
            skFitSpline(sketch, "E3803", {"points": [v(248.74, 62.67) * mm, v(249.28, 62.67) * mm, v(249.78, 62.95) * mm, v(250.05, 63.42) * mm]});
            skFitSpline(sketch, "E3804", {"points": [v(250.05, 63.42) * mm, v(250.31, 63.88) * mm, v(250.31, 64.46) * mm, v(250.05, 64.92) * mm]});
            skFitSpline(sketch, "E3805", {"points": [v(250.05, 64.92) * mm, v(249.78, 65.39) * mm, v(249.28, 65.67) * mm, v(248.74, 65.67) * mm]});
            skFitSpline(sketch, "E3806", {"points": [v(248.74, 85.67) * mm, v(248.2, 85.67) * mm, v(247.71, 85.39) * mm, v(247.44, 84.92) * mm]});
            skFitSpline(sketch, "E3807", {"points": [v(247.44, 84.92) * mm, v(247.17, 84.46) * mm, v(247.17, 83.88) * mm, v(247.44, 83.42) * mm]});
            skFitSpline(sketch, "E3808", {"points": [v(247.44, 83.42) * mm, v(247.71, 82.95) * mm, v(248.2, 82.67) * mm, v(248.74, 82.67) * mm]});
            skFitSpline(sketch, "E3809", {"points": [v(248.74, 82.67) * mm, v(249.28, 82.67) * mm, v(249.78, 82.95) * mm, v(250.05, 83.42) * mm]});
            skFitSpline(sketch, "E3810", {"points": [v(250.05, 83.42) * mm, v(250.31, 83.88) * mm, v(250.31, 84.46) * mm, v(250.05, 84.92) * mm]});
            skFitSpline(sketch, "E3811", {"points": [v(250.05, 84.92) * mm, v(249.78, 85.39) * mm, v(249.28, 85.67) * mm, v(248.74, 85.67) * mm]});
            skFitSpline(sketch, "E3812", {"points": [v(233.74, -104.34) * mm, v(233.2, -104.34) * mm, v(232.71, -104.62) * mm, v(232.44, -105.09) * mm]});
            skFitSpline(sketch, "E3813", {"points": [v(232.44, -105.09) * mm, v(232.18, -105.55) * mm, v(232.18, -106.12) * mm, v(232.44, -106.59) * mm]});
            skFitSpline(sketch, "E3814", {"points": [v(232.44, -106.59) * mm, v(232.71, -107.05) * mm, v(233.2, -107.34) * mm, v(233.74, -107.34) * mm]});
            skFitSpline(sketch, "E3815", {"points": [v(233.74, -107.34) * mm, v(234.28, -107.34) * mm, v(234.78, -107.05) * mm, v(235.04, -106.59) * mm]});
            skFitSpline(sketch, "E3816", {"points": [v(235.04, -106.59) * mm, v(235.31, -106.12) * mm, v(235.31, -105.55) * mm, v(235.04, -105.09) * mm]});
            skFitSpline(sketch, "E3817", {"points": [v(235.04, -105.09) * mm, v(234.78, -104.62) * mm, v(234.28, -104.34) * mm, v(233.74, -104.34) * mm]});
            skFitSpline(sketch, "E3818", {"points": [v(233.74, -84.34) * mm, v(233.2, -84.34) * mm, v(232.71, -84.62) * mm, v(232.44, -85.09) * mm]});
            skFitSpline(sketch, "E3819", {"points": [v(232.44, -85.09) * mm, v(232.18, -85.55) * mm, v(232.18, -86.12) * mm, v(232.44, -86.59) * mm]});
            skFitSpline(sketch, "E3820", {"points": [v(232.44, -86.59) * mm, v(232.71, -87.05) * mm, v(233.2, -87.34) * mm, v(233.74, -87.34) * mm]});
            skFitSpline(sketch, "E3821", {"points": [v(233.74, -87.34) * mm, v(234.28, -87.34) * mm, v(234.78, -87.05) * mm, v(235.04, -86.59) * mm]});
            skFitSpline(sketch, "E3822", {"points": [v(235.04, -86.59) * mm, v(235.31, -86.12) * mm, v(235.31, -85.55) * mm, v(235.04, -85.09) * mm]});
            skFitSpline(sketch, "E3823", {"points": [v(235.04, -85.09) * mm, v(234.78, -84.62) * mm, v(234.28, -84.34) * mm, v(233.74, -84.34) * mm]});
            skFitSpline(sketch, "E3824", {"points": [v(248.74, -104.34) * mm, v(248.2, -104.34) * mm, v(247.71, -104.62) * mm, v(247.44, -105.09) * mm]});
            skFitSpline(sketch, "E3825", {"points": [v(247.44, -105.09) * mm, v(247.18, -105.55) * mm, v(247.18, -106.12) * mm, v(247.44, -106.59) * mm]});
            skFitSpline(sketch, "E3826", {"points": [v(247.44, -106.59) * mm, v(247.71, -107.05) * mm, v(248.2, -107.34) * mm, v(248.74, -107.34) * mm]});
            skFitSpline(sketch, "E3827", {"points": [v(248.74, -107.34) * mm, v(249.28, -107.34) * mm, v(249.78, -107.05) * mm, v(250.04, -106.59) * mm]});
            skFitSpline(sketch, "E3828", {"points": [v(250.04, -106.59) * mm, v(250.31, -106.12) * mm, v(250.31, -105.55) * mm, v(250.04, -105.09) * mm]});
            skFitSpline(sketch, "E3829", {"points": [v(250.04, -105.09) * mm, v(249.78, -104.62) * mm, v(249.28, -104.34) * mm, v(248.74, -104.34) * mm]});
            skFitSpline(sketch, "E3830", {"points": [v(248.74, -84.34) * mm, v(248.2, -84.34) * mm, v(247.71, -84.62) * mm, v(247.44, -85.09) * mm]});
            skFitSpline(sketch, "E3831", {"points": [v(247.44, -85.09) * mm, v(247.18, -85.55) * mm, v(247.18, -86.12) * mm, v(247.44, -86.59) * mm]});
            skFitSpline(sketch, "E3832", {"points": [v(247.44, -86.59) * mm, v(247.71, -87.05) * mm, v(248.2, -87.34) * mm, v(248.74, -87.34) * mm]});
            skFitSpline(sketch, "E3833", {"points": [v(248.74, -87.34) * mm, v(249.28, -87.34) * mm, v(249.78, -87.05) * mm, v(250.04, -86.59) * mm]});
            skFitSpline(sketch, "E3834", {"points": [v(250.04, -86.59) * mm, v(250.31, -86.12) * mm, v(250.31, -85.55) * mm, v(250.04, -85.09) * mm]});
            skFitSpline(sketch, "E3835", {"points": [v(250.04, -85.09) * mm, v(249.78, -84.62) * mm, v(249.28, -84.34) * mm, v(248.74, -84.34) * mm]});
            skFitSpline(sketch, "E3836", {"points": [v(160.56, -104.34) * mm, v(160.02, -104.34) * mm, v(159.52, -104.62) * mm, v(159.26, -105.09) * mm]});
            skFitSpline(sketch, "E3837", {"points": [v(159.26, -105.09) * mm, v(158.99, -105.55) * mm, v(158.99, -106.12) * mm, v(159.26, -106.59) * mm]});
            skFitSpline(sketch, "E3838", {"points": [v(159.26, -106.59) * mm, v(159.52, -107.05) * mm, v(160.02, -107.34) * mm, v(160.56, -107.34) * mm]});
            skFitSpline(sketch, "E3839", {"points": [v(160.56, -107.34) * mm, v(161.1, -107.34) * mm, v(161.59, -107.05) * mm, v(161.86, -106.59) * mm]});
            skFitSpline(sketch, "E3840", {"points": [v(161.86, -106.59) * mm, v(162.12, -106.12) * mm, v(162.12, -105.55) * mm, v(161.86, -105.09) * mm]});
            skFitSpline(sketch, "E3841", {"points": [v(161.86, -105.09) * mm, v(161.59, -104.62) * mm, v(161.1, -104.34) * mm, v(160.56, -104.34) * mm]});
            skFitSpline(sketch, "E3842", {"points": [v(160.56, -84.34) * mm, v(160.02, -84.34) * mm, v(159.52, -84.62) * mm, v(159.26, -85.09) * mm]});
            skFitSpline(sketch, "E3843", {"points": [v(159.26, -85.09) * mm, v(158.99, -85.55) * mm, v(158.99, -86.12) * mm, v(159.26, -86.59) * mm]});
            skFitSpline(sketch, "E3844", {"points": [v(159.26, -86.59) * mm, v(159.52, -87.05) * mm, v(160.02, -87.34) * mm, v(160.56, -87.34) * mm]});
            skFitSpline(sketch, "E3845", {"points": [v(160.56, -87.34) * mm, v(161.1, -87.34) * mm, v(161.59, -87.05) * mm, v(161.86, -86.59) * mm]});
            skFitSpline(sketch, "E3846", {"points": [v(161.86, -86.59) * mm, v(162.12, -86.12) * mm, v(162.12, -85.55) * mm, v(161.86, -85.09) * mm]});
            skFitSpline(sketch, "E3847", {"points": [v(161.86, -85.09) * mm, v(161.59, -84.62) * mm, v(161.1, -84.34) * mm, v(160.56, -84.34) * mm]});
            skFitSpline(sketch, "E3848", {"points": [v(175.56, -104.34) * mm, v(175.02, -104.34) * mm, v(174.52, -104.62) * mm, v(174.26, -105.09) * mm]});
            skFitSpline(sketch, "E3849", {"points": [v(174.26, -105.09) * mm, v(173.99, -105.55) * mm, v(173.99, -106.12) * mm, v(174.26, -106.59) * mm]});
            skFitSpline(sketch, "E3850", {"points": [v(174.26, -106.59) * mm, v(174.52, -107.05) * mm, v(175.02, -107.34) * mm, v(175.56, -107.34) * mm]});
            skFitSpline(sketch, "E3851", {"points": [v(175.56, -107.34) * mm, v(176.1, -107.34) * mm, v(176.59, -107.05) * mm, v(176.86, -106.59) * mm]});
            skFitSpline(sketch, "E3852", {"points": [v(176.86, -106.59) * mm, v(177.12, -106.12) * mm, v(177.12, -105.55) * mm, v(176.86, -105.09) * mm]});
            skFitSpline(sketch, "E3853", {"points": [v(176.86, -105.09) * mm, v(176.59, -104.62) * mm, v(176.1, -104.34) * mm, v(175.56, -104.34) * mm]});
            skFitSpline(sketch, "E3854", {"points": [v(175.56, -84.34) * mm, v(175.02, -84.34) * mm, v(174.52, -84.62) * mm, v(174.26, -85.09) * mm]});
            skFitSpline(sketch, "E3855", {"points": [v(174.26, -85.09) * mm, v(173.99, -85.55) * mm, v(173.99, -86.12) * mm, v(174.26, -86.59) * mm]});
            skFitSpline(sketch, "E3856", {"points": [v(174.26, -86.59) * mm, v(174.52, -87.05) * mm, v(175.02, -87.34) * mm, v(175.56, -87.34) * mm]});
            skFitSpline(sketch, "E3857", {"points": [v(175.56, -87.34) * mm, v(176.1, -87.34) * mm, v(176.59, -87.05) * mm, v(176.86, -86.59) * mm]});
            skFitSpline(sketch, "E3858", {"points": [v(176.86, -86.59) * mm, v(177.12, -86.12) * mm, v(177.12, -85.55) * mm, v(176.86, -85.09) * mm]});
            skFitSpline(sketch, "E3859", {"points": [v(176.86, -85.09) * mm, v(176.59, -84.62) * mm, v(176.1, -84.34) * mm, v(175.56, -84.34) * mm]});
            skFitSpline(sketch, "E3860", {"points": [v(-300.9, -61.82) * mm, v(-300.8, -62) * mm, v(-300.6, -62.1) * mm, v(-300.38, -62.06) * mm]});
            skFitSpline(sketch, "E3861", {"points": [v(-300.38, -62.06) * mm, v(-300.18, -62.02) * mm, v(-300.01, -61.86) * mm, v(-299.98, -61.65) * mm]});
            skFitSpline(sketch, "E3862", {"points": [v(-299.98, -61.65) * mm, v(-299.94, -61.45) * mm, v(-300.04, -61.24) * mm, v(-300.22, -61.13) * mm]});
            skFitSpline(sketch, "E3863", {"points": [v(-300.9, -61.82) * mm, v(-301, -61.66) * mm, v(-301.16, -61.57) * mm, v(-301.33, -61.57) * mm]});
            skFitSpline(sketch, "E3864", {"points": [v(-311.94, -61.57) * mm, v(-312.12, -61.57) * mm, v(-312.28, -61.66) * mm, v(-312.37, -61.82) * mm]});
            skFitSpline(sketch, "E3865", {"points": [v(-313.06, -61.13) * mm, v(-313.24, -61.24) * mm, v(-313.33, -61.45) * mm, v(-313.3, -61.65) * mm]});
            skFitSpline(sketch, "E3866", {"points": [v(-313.3, -61.65) * mm, v(-313.26, -61.86) * mm, v(-313.1, -62.02) * mm, v(-312.9, -62.06) * mm]});
            skFitSpline(sketch, "E3867", {"points": [v(-312.9, -62.06) * mm, v(-312.69, -62.1) * mm, v(-312.48, -62) * mm, v(-312.37, -61.82) * mm]});
            skFitSpline(sketch, "E3868", {"points": [v(-313.06, -61.13) * mm, v(-312.9, -61.04) * mm, v(-312.8, -60.88) * mm, v(-312.8, -60.7) * mm]});
            skLineSegment(sketch, "E3869", {"start": v(-301.33, -61.57) * mm, "end": v(-311.94, -61.57) * mm});
            skFitSpline(sketch, "E3870", {"points": [v(-312.8, -54.09) * mm, v(-312.8, -53.93) * mm, v(-312.9, -53.77) * mm, v(-313.06, -53.68) * mm]});
            skFitSpline(sketch, "E3871", {"points": [v(-312.37, -53) * mm, v(-312.48, -52.81) * mm, v(-312.69, -52.71) * mm, v(-312.9, -52.75) * mm]});
            skFitSpline(sketch, "E3872", {"points": [v(-312.9, -52.75) * mm, v(-313.1, -52.79) * mm, v(-313.26, -52.95) * mm, v(-313.3, -53.16) * mm]});
            skFitSpline(sketch, "E3873", {"points": [v(-313.3, -53.16) * mm, v(-313.34, -53.36) * mm, v(-313.24, -53.57) * mm, v(-313.06, -53.68) * mm]});
            skFitSpline(sketch, "E3874", {"points": [v(-312.37, -53) * mm, v(-312.28, -53.15) * mm, v(-312.12, -53.24) * mm, v(-311.94, -53.26) * mm]});
            skLineSegment(sketch, "E3875", {"start": v(-312.8, -60.7) * mm, "end": v(-312.8, -54.09) * mm});
            skFitSpline(sketch, "E3876", {"points": [v(-301.33, -53.26) * mm, v(-301.16, -53.24) * mm, v(-301, -53.15) * mm, v(-300.9, -53) * mm]});
            skFitSpline(sketch, "E3877", {"points": [v(-300.22, -53.68) * mm, v(-300.04, -53.57) * mm, v(-299.94, -53.36) * mm, v(-299.98, -53.16) * mm]});
            skFitSpline(sketch, "E3878", {"points": [v(-299.98, -53.16) * mm, v(-300.01, -52.95) * mm, v(-300.18, -52.79) * mm, v(-300.38, -52.75) * mm]});
            skFitSpline(sketch, "E3879", {"points": [v(-300.38, -52.75) * mm, v(-300.6, -52.71) * mm, v(-300.8, -52.81) * mm, v(-300.9, -53) * mm]});
            skFitSpline(sketch, "E3880", {"points": [v(-300.22, -53.68) * mm, v(-300.37, -53.77) * mm, v(-300.47, -53.93) * mm, v(-300.47, -54.09) * mm]});
            skLineSegment(sketch, "E3881", {"start": v(-311.94, -53.26) * mm, "end": v(-301.33, -53.26) * mm});
            skFitSpline(sketch, "E3882", {"points": [v(-300.47, -60.7) * mm, v(-300.47, -60.88) * mm, v(-300.37, -61.04) * mm, v(-300.22, -61.13) * mm]});
            skFitSpline(sketch, "E3883", {"points": [v(-131.1, -61.82) * mm, v(-131, -62) * mm, v(-130.8, -62.1) * mm, v(-130.58, -62.06) * mm]});
            skFitSpline(sketch, "E3884", {"points": [v(-130.58, -62.06) * mm, v(-130.38, -62.02) * mm, v(-130.21, -61.86) * mm, v(-130.18, -61.65) * mm]});
            skFitSpline(sketch, "E3885", {"points": [v(-130.18, -61.65) * mm, v(-130.14, -61.45) * mm, v(-130.24, -61.24) * mm, v(-130.42, -61.13) * mm]});
            skFitSpline(sketch, "E3886", {"points": [v(-131.1, -61.82) * mm, v(-131.2, -61.66) * mm, v(-131.36, -61.57) * mm, v(-131.53, -61.57) * mm]});
            skLineSegment(sketch, "E3887", {"start": v(-300.47, -54.09) * mm, "end": v(-300.47, -60.7) * mm});
            skFitSpline(sketch, "E3888", {"points": [v(-142.14, -61.57) * mm, v(-142.32, -61.57) * mm, v(-142.48, -61.66) * mm, v(-142.57, -61.82) * mm]});
            skFitSpline(sketch, "E3889", {"points": [v(-143.26, -61.13) * mm, v(-143.44, -61.24) * mm, v(-143.53, -61.45) * mm, v(-143.5, -61.65) * mm]});
            skFitSpline(sketch, "E3890", {"points": [v(-143.5, -61.65) * mm, v(-143.46, -61.86) * mm, v(-143.3, -62.02) * mm, v(-143.1, -62.06) * mm]});
            skFitSpline(sketch, "E3891", {"points": [v(-143.1, -62.06) * mm, v(-142.89, -62.1) * mm, v(-142.68, -62) * mm, v(-142.57, -61.82) * mm]});
            skFitSpline(sketch, "E3892", {"points": [v(-143.26, -61.13) * mm, v(-143.1, -61.04) * mm, v(-143, -60.88) * mm, v(-143, -60.7) * mm]});
            skLineSegment(sketch, "E3893", {"start": v(-131.53, -61.57) * mm, "end": v(-142.14, -61.57) * mm});
            skFitSpline(sketch, "E3894", {"points": [v(-143, -54.09) * mm, v(-143, -53.93) * mm, v(-143.1, -53.77) * mm, v(-143.26, -53.68) * mm]});
            skFitSpline(sketch, "E3895", {"points": [v(-142.57, -53) * mm, v(-142.68, -52.81) * mm, v(-142.89, -52.71) * mm, v(-143.1, -52.75) * mm]});
            skFitSpline(sketch, "E3896", {"points": [v(-143.1, -52.75) * mm, v(-143.3, -52.79) * mm, v(-143.46, -52.95) * mm, v(-143.5, -53.16) * mm]});
            skFitSpline(sketch, "E3897", {"points": [v(-143.5, -53.16) * mm, v(-143.54, -53.36) * mm, v(-143.44, -53.57) * mm, v(-143.26, -53.68) * mm]});
            skFitSpline(sketch, "E3898", {"points": [v(-142.57, -53) * mm, v(-142.48, -53.15) * mm, v(-142.32, -53.24) * mm, v(-142.14, -53.26) * mm]});
            skLineSegment(sketch, "E3899", {"start": v(-143, -60.7) * mm, "end": v(-143, -54.09) * mm});
            skFitSpline(sketch, "E3900", {"points": [v(-131.53, -53.26) * mm, v(-131.36, -53.24) * mm, v(-131.2, -53.15) * mm, v(-131.1, -53) * mm]});
            skFitSpline(sketch, "E3901", {"points": [v(-130.42, -53.68) * mm, v(-130.24, -53.57) * mm, v(-130.14, -53.36) * mm, v(-130.18, -53.16) * mm]});
            skFitSpline(sketch, "E3902", {"points": [v(-130.18, -53.16) * mm, v(-130.21, -52.95) * mm, v(-130.38, -52.79) * mm, v(-130.58, -52.75) * mm]});
            skFitSpline(sketch, "E3903", {"points": [v(-130.58, -52.75) * mm, v(-130.8, -52.71) * mm, v(-131, -52.81) * mm, v(-131.1, -53) * mm]});
            skFitSpline(sketch, "E3904", {"points": [v(-130.42, -53.68) * mm, v(-130.57, -53.77) * mm, v(-130.67, -53.93) * mm, v(-130.67, -54.09) * mm]});
            skLineSegment(sketch, "E3905", {"start": v(-142.14, -53.26) * mm, "end": v(-131.53, -53.26) * mm});
            skFitSpline(sketch, "E3906", {"points": [v(-130.67, -60.7) * mm, v(-130.67, -60.88) * mm, v(-130.57, -61.04) * mm, v(-130.42, -61.13) * mm]});
            skLineSegment(sketch, "E3907", {"start": v(-130.67, -54.09) * mm, "end": v(-130.67, -60.7) * mm});
            skLineSegment(sketch, "E3908", {"start": v(-18.47, 54.13) * mm, "end": v(-18.47, 54.13) * mm});
            skLineSegment(sketch, "E3909", {"start": v(8.21, -182.45) * mm, "end": v(8.21, -182.45) * mm});
            skLineSegment(sketch, "E3910", {"start": v(-147.2, -58.05) * mm, "end": v(-126.2, -58.05) * mm, "construction": true});
            skSolve(sketch);
        }
        {
            var Q0;
            Q0=makeQuery(id+"F0.imprint","IMPRINT",FACE,{"disambiguationData":[TD([[makeQuery(id+"F0.imprint","IMPRINT",EDGE,{"derivedFrom":sQuery(id+"F0.wireOp",EDGE,"E15")}),-1.0]])]});
            var Q1;
            Q1=makeQuery(id+"F0.imprint","IMPRINT",FACE,{"disambiguationData":[TD([[makeQuery(id+"F0.imprint","IMPRINT",EDGE,{"derivedFrom":sQuery(id+"F0.wireOp",EDGE,"E1607")}),1.0]])]});
            var Q2;
            Q2=makeQuery(id+"F0.imprint","IMPRINT",FACE,{"disambiguationData":[TD([[makeQuery(id+"F0.imprint","IMPRINT",EDGE,{"derivedFrom":sQuery(id+"F0.wireOp",EDGE,"E2054")}),1.0]])]});
            var Q3;
            Q3=makeQuery(id+"F0.imprint","IMPRINT",FACE,{"disambiguationData":[TD([[makeQuery(id+"F0.imprint","IMPRINT",EDGE,{"derivedFrom":sQuery(id+"F0.wireOp",EDGE,"E20")}),1.0]])]});
            var Q4;
            Q4=makeQuery(id+"F0.imprint","IMPRINT",FACE,{"disambiguationData":[TD([[makeQuery(id+"F0.imprint","IMPRINT",EDGE,{"derivedFrom":sQuery(id+"F0.wireOp",EDGE,"E3438")}),-1.0]])]});
            var Q5;
            Q5=makeQuery(id+"F0.imprint","IMPRINT",FACE,{"disambiguationData":[TD([[makeQuery(id+"F0.imprint","IMPRINT",EDGE,{"derivedFrom":sQuery(id+"F0.wireOp",EDGE,"E2681")}),1.0]])]});
            var Q6;
            Q6=makeQuery(id+"F0.imprint","IMPRINT",FACE,{"disambiguationData":[TD([[makeQuery(id+"F0.imprint","IMPRINT",EDGE,{"derivedFrom":sQuery(id+"F0.wireOp",EDGE,"E2942")}),1.0]])]});
            extrude(context, id + "F1", {"entities" : qUnion([Q0, Q1, Q2, Q3, Q4, Q5, Q6]), "depth" : 3 * mm, "offsetDistance" : 25 * mm});
        }
    });
